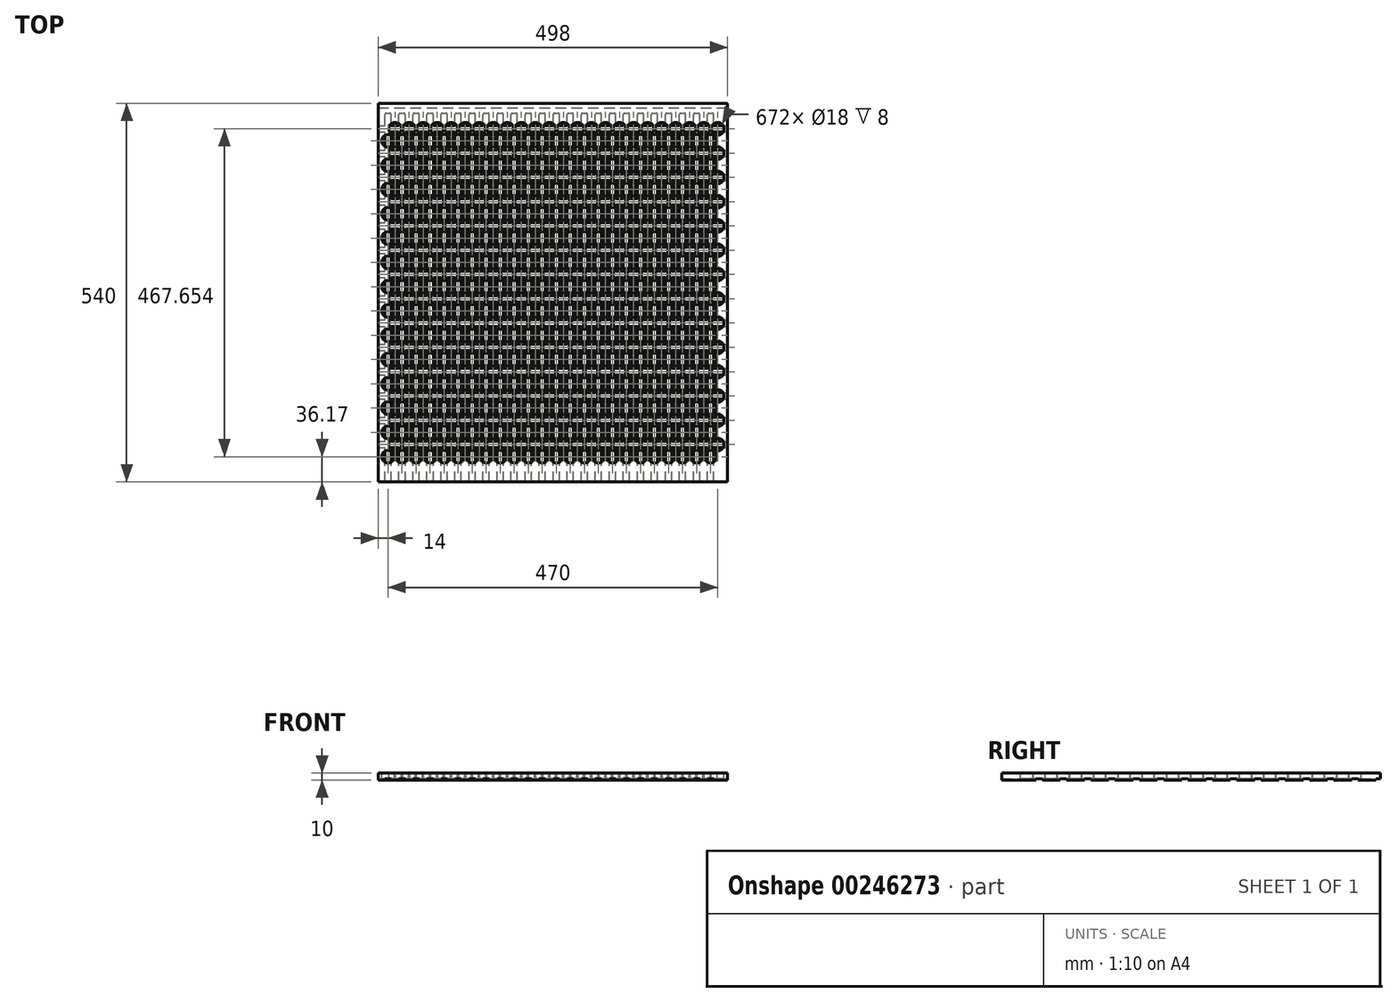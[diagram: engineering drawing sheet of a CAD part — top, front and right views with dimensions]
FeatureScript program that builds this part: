
annotation { "Feature Type Name" : "Feature", "Feature Type Description" : "" }
export const myFeature = defineFeature(function(context is Context, id is Id, definition is map)
    precondition{}
    {
        {
            var Q0;
            Q0=qCreatedBy(makeId("Top.planeOp"),FACE);
            var sketch = newSketch(context, id + "F0", { "sketchPlane" : qUnion([Q0])});
            skCircle(sketch, "E0", {"center": v(0, 0) * mm, "radius": 9 * mm});
            skCircle(sketch, "E1.1.0.0", {"center": v(20, 0) * mm, "radius": 9 * mm});
            skCircle(sketch, "E1.2.0.0", {"center": v(40, 0) * mm, "radius": 9 * mm});
            skCircle(sketch, "E1.3.0.0", {"center": v(60, 0) * mm, "radius": 9 * mm});
            skCircle(sketch, "E1.4.0.0", {"center": v(80, 0) * mm, "radius": 9 * mm});
            skCircle(sketch, "E1.5.0.0", {"center": v(100, 0) * mm, "radius": 9 * mm});
            skCircle(sketch, "E1.6.0.0", {"center": v(120, 0) * mm, "radius": 9 * mm});
            skCircle(sketch, "E1.7.0.0", {"center": v(140, 0) * mm, "radius": 9 * mm});
            skCircle(sketch, "E1.8.0.0", {"center": v(160, 0) * mm, "radius": 9 * mm});
            skCircle(sketch, "E1.9.0.0", {"center": v(180, 0) * mm, "radius": 9 * mm});
            skCircle(sketch, "E1.10.0.0", {"center": v(200, 0) * mm, "radius": 9 * mm});
            skCircle(sketch, "E1.11.0.0", {"center": v(220, 0) * mm, "radius": 9 * mm});
            skCircle(sketch, "E1.12.0.0", {"center": v(240, 0) * mm, "radius": 9 * mm});
            skCircle(sketch, "E1.13.0.0", {"center": v(260, 0) * mm, "radius": 9 * mm});
            skCircle(sketch, "E1.14.0.0", {"center": v(280, 0) * mm, "radius": 9 * mm});
            skCircle(sketch, "E1.15.0.0", {"center": v(300, 0) * mm, "radius": 9 * mm});
            skCircle(sketch, "E1.16.0.0", {"center": v(320, 0) * mm, "radius": 9 * mm});
            skCircle(sketch, "E1.17.0.0", {"center": v(340, 0) * mm, "radius": 9 * mm});
            skCircle(sketch, "E1.18.0.0", {"center": v(360, 0) * mm, "radius": 9 * mm});
            skCircle(sketch, "E1.19.0.0", {"center": v(380, 0) * mm, "radius": 9 * mm});
            skCircle(sketch, "E1.20.0.0", {"center": v(400, 0) * mm, "radius": 9 * mm});
            skCircle(sketch, "E1.21.0.0", {"center": v(420, 0) * mm, "radius": 9 * mm});
            skCircle(sketch, "E1.22.0.0", {"center": v(440, 0) * mm, "radius": 9 * mm});
            skCircle(sketch, "E1.23.0.0", {"center": v(460, 0) * mm, "radius": 9 * mm});
            skLineSegment(sketch, "E1.direction1", {"start": v(0, 0) * mm, "end": v(20, 0) * mm, "construction": true});
            skCircle(sketch, "E2", {"center": v(10, 17.32) * mm, "radius": 9 * mm});
            skCircle(sketch, "E3.1.0.0", {"center": v(30, 17.32) * mm, "radius": 9 * mm});
            skCircle(sketch, "E3.2.0.0", {"center": v(50, 17.32) * mm, "radius": 9 * mm});
            skCircle(sketch, "E3.3.0.0", {"center": v(70, 17.32) * mm, "radius": 9 * mm});
            skCircle(sketch, "E3.4.0.0", {"center": v(90, 17.32) * mm, "radius": 9 * mm});
            skCircle(sketch, "E3.5.0.0", {"center": v(110, 17.32) * mm, "radius": 9 * mm});
            skCircle(sketch, "E3.6.0.0", {"center": v(130, 17.32) * mm, "radius": 9 * mm});
            skCircle(sketch, "E3.7.0.0", {"center": v(150, 17.32) * mm, "radius": 9 * mm});
            skCircle(sketch, "E3.8.0.0", {"center": v(170, 17.32) * mm, "radius": 9 * mm});
            skCircle(sketch, "E3.9.0.0", {"center": v(190, 17.32) * mm, "radius": 9 * mm});
            skCircle(sketch, "E3.10.0.0", {"center": v(210, 17.32) * mm, "radius": 9 * mm});
            skCircle(sketch, "E3.11.0.0", {"center": v(230, 17.32) * mm, "radius": 9 * mm});
            skCircle(sketch, "E3.12.0.0", {"center": v(250, 17.32) * mm, "radius": 9 * mm});
            skCircle(sketch, "E3.13.0.0", {"center": v(270, 17.32) * mm, "radius": 9 * mm});
            skCircle(sketch, "E3.14.0.0", {"center": v(290, 17.32) * mm, "radius": 9 * mm});
            skCircle(sketch, "E3.15.0.0", {"center": v(310, 17.32) * mm, "radius": 9 * mm});
            skCircle(sketch, "E3.16.0.0", {"center": v(330, 17.32) * mm, "radius": 9 * mm});
            skCircle(sketch, "E3.17.0.0", {"center": v(350, 17.32) * mm, "radius": 9 * mm});
            skCircle(sketch, "E3.18.0.0", {"center": v(370, 17.32) * mm, "radius": 9 * mm});
            skCircle(sketch, "E3.19.0.0", {"center": v(390, 17.32) * mm, "radius": 9 * mm});
            skCircle(sketch, "E3.20.0.0", {"center": v(410, 17.32) * mm, "radius": 9 * mm});
            skCircle(sketch, "E3.21.0.0", {"center": v(430, 17.32) * mm, "radius": 9 * mm});
            skCircle(sketch, "E3.22.0.0", {"center": v(450, 17.32) * mm, "radius": 9 * mm});
            skCircle(sketch, "E3.23.0.0", {"center": v(470, 17.32) * mm, "radius": 9 * mm});
            skLineSegment(sketch, "E3.direction1", {"start": v(10, 17.32) * mm, "end": v(30, 17.32) * mm, "construction": true});
            skCircle(sketch, "E4.0.1.0", {"center": v(280, 34.64) * mm, "radius": 9 * mm});
            skCircle(sketch, "E4.0.1.1", {"center": v(260, 34.64) * mm, "radius": 9 * mm});
            skCircle(sketch, "E4.0.1.2", {"center": v(130, 51.96) * mm, "radius": 9 * mm});
            skCircle(sketch, "E4.0.1.3", {"center": v(60, 34.64) * mm, "radius": 9 * mm});
            skCircle(sketch, "E4.0.1.4", {"center": v(80, 34.64) * mm, "radius": 9 * mm});
            skCircle(sketch, "E4.0.1.5", {"center": v(100, 34.64) * mm, "radius": 9 * mm});
            skCircle(sketch, "E4.0.1.6", {"center": v(350, 51.96) * mm, "radius": 9 * mm});
            skCircle(sketch, "E4.0.1.7", {"center": v(0, 34.64) * mm, "radius": 9 * mm});
            skCircle(sketch, "E4.0.1.8", {"center": v(120, 34.64) * mm, "radius": 9 * mm});
            skCircle(sketch, "E4.0.1.9", {"center": v(30, 51.96) * mm, "radius": 9 * mm});
            skCircle(sketch, "E4.0.1.10", {"center": v(380, 34.64) * mm, "radius": 9 * mm});
            skCircle(sketch, "E4.0.1.11", {"center": v(140, 34.64) * mm, "radius": 9 * mm});
            skCircle(sketch, "E4.0.1.12", {"center": v(450, 51.96) * mm, "radius": 9 * mm});
            skCircle(sketch, "E4.0.1.13", {"center": v(160, 34.64) * mm, "radius": 9 * mm});
            skCircle(sketch, "E4.0.1.14", {"center": v(300, 34.64) * mm, "radius": 9 * mm});
            skCircle(sketch, "E4.0.1.15", {"center": v(40, 34.64) * mm, "radius": 9 * mm});
            skCircle(sketch, "E4.0.1.16", {"center": v(210, 51.96) * mm, "radius": 9 * mm});
            skCircle(sketch, "E4.0.1.17", {"center": v(330, 51.96) * mm, "radius": 9 * mm});
            skCircle(sketch, "E4.0.1.18", {"center": v(270, 51.96) * mm, "radius": 9 * mm});
            skCircle(sketch, "E4.0.1.19", {"center": v(440, 34.64) * mm, "radius": 9 * mm});
            skCircle(sketch, "E4.0.1.20", {"center": v(110, 51.96) * mm, "radius": 9 * mm});
            skCircle(sketch, "E4.0.1.21", {"center": v(250, 51.96) * mm, "radius": 9 * mm});
            skCircle(sketch, "E4.0.1.22", {"center": v(180, 34.64) * mm, "radius": 9 * mm});
            skCircle(sketch, "E4.0.1.23", {"center": v(430, 51.96) * mm, "radius": 9 * mm});
            skCircle(sketch, "E4.0.1.24", {"center": v(200, 34.64) * mm, "radius": 9 * mm});
            skCircle(sketch, "E4.0.1.25", {"center": v(420, 34.64) * mm, "radius": 9 * mm});
            skCircle(sketch, "E4.0.1.26", {"center": v(70, 51.96) * mm, "radius": 9 * mm});
            skCircle(sketch, "E4.0.1.27", {"center": v(390, 51.96) * mm, "radius": 9 * mm});
            skCircle(sketch, "E4.0.1.28", {"center": v(220, 34.64) * mm, "radius": 9 * mm});
            skCircle(sketch, "E4.0.1.29", {"center": v(190, 51.96) * mm, "radius": 9 * mm});
            skCircle(sketch, "E4.0.1.30", {"center": v(90, 51.96) * mm, "radius": 9 * mm});
            skCircle(sketch, "E4.0.1.31", {"center": v(230, 51.96) * mm, "radius": 9 * mm});
            skCircle(sketch, "E4.0.1.32", {"center": v(150, 51.96) * mm, "radius": 9 * mm});
            skCircle(sketch, "E4.0.1.33", {"center": v(470, 51.96) * mm, "radius": 9 * mm});
            skCircle(sketch, "E4.0.1.34", {"center": v(410, 51.96) * mm, "radius": 9 * mm});
            skCircle(sketch, "E4.0.1.35", {"center": v(50, 51.96) * mm, "radius": 9 * mm});
            skCircle(sketch, "E4.0.1.36", {"center": v(400, 34.64) * mm, "radius": 9 * mm});
            skCircle(sketch, "E4.0.1.37", {"center": v(240, 34.64) * mm, "radius": 9 * mm});
            skCircle(sketch, "E4.0.1.38", {"center": v(320, 34.64) * mm, "radius": 9 * mm});
            skCircle(sketch, "E4.0.1.39", {"center": v(370, 51.96) * mm, "radius": 9 * mm});
            skCircle(sketch, "E4.0.1.40", {"center": v(10, 51.96) * mm, "radius": 9 * mm});
            skCircle(sketch, "E4.0.1.41", {"center": v(290, 51.96) * mm, "radius": 9 * mm});
            skCircle(sketch, "E4.0.1.42", {"center": v(360, 34.64) * mm, "radius": 9 * mm});
            skCircle(sketch, "E4.0.1.43", {"center": v(460, 34.64) * mm, "radius": 9 * mm});
            skCircle(sketch, "E4.0.1.44", {"center": v(310, 51.96) * mm, "radius": 9 * mm});
            skCircle(sketch, "E4.0.1.45", {"center": v(340, 34.64) * mm, "radius": 9 * mm});
            skCircle(sketch, "E4.0.1.46", {"center": v(170, 51.96) * mm, "radius": 9 * mm});
            skCircle(sketch, "E4.0.1.47", {"center": v(20, 34.64) * mm, "radius": 9 * mm});
            skLineSegment(sketch, "E4.0.1.48", {"start": v(0, 34.64) * mm, "end": v(20, 34.64) * mm, "construction": true});
            skLineSegment(sketch, "E4.0.1.49", {"start": v(10, 51.96) * mm, "end": v(30, 51.96) * mm, "construction": true});
            skCircle(sketch, "E4.0.2.0", {"center": v(280, 69.28) * mm, "radius": 9 * mm});
            skCircle(sketch, "E4.0.2.1", {"center": v(260, 69.28) * mm, "radius": 9 * mm});
            skCircle(sketch, "E4.0.2.2", {"center": v(130, 86.6) * mm, "radius": 9 * mm});
            skCircle(sketch, "E4.0.2.3", {"center": v(60, 69.28) * mm, "radius": 9 * mm});
            skCircle(sketch, "E4.0.2.4", {"center": v(80, 69.28) * mm, "radius": 9 * mm});
            skCircle(sketch, "E4.0.2.5", {"center": v(100, 69.28) * mm, "radius": 9 * mm});
            skCircle(sketch, "E4.0.2.6", {"center": v(350, 86.6) * mm, "radius": 9 * mm});
            skCircle(sketch, "E4.0.2.7", {"center": v(0, 69.28) * mm, "radius": 9 * mm});
            skCircle(sketch, "E4.0.2.8", {"center": v(120, 69.28) * mm, "radius": 9 * mm});
            skCircle(sketch, "E4.0.2.9", {"center": v(30, 86.6) * mm, "radius": 9 * mm});
            skCircle(sketch, "E4.0.2.10", {"center": v(380, 69.28) * mm, "radius": 9 * mm});
            skCircle(sketch, "E4.0.2.11", {"center": v(140, 69.28) * mm, "radius": 9 * mm});
            skCircle(sketch, "E4.0.2.12", {"center": v(450, 86.6) * mm, "radius": 9 * mm});
            skCircle(sketch, "E4.0.2.13", {"center": v(160, 69.28) * mm, "radius": 9 * mm});
            skCircle(sketch, "E4.0.2.14", {"center": v(300, 69.28) * mm, "radius": 9 * mm});
            skCircle(sketch, "E4.0.2.15", {"center": v(40, 69.28) * mm, "radius": 9 * mm});
            skCircle(sketch, "E4.0.2.16", {"center": v(210, 86.6) * mm, "radius": 9 * mm});
            skCircle(sketch, "E4.0.2.17", {"center": v(330, 86.6) * mm, "radius": 9 * mm});
            skCircle(sketch, "E4.0.2.18", {"center": v(270, 86.6) * mm, "radius": 9 * mm});
            skCircle(sketch, "E4.0.2.19", {"center": v(440, 69.28) * mm, "radius": 9 * mm});
            skCircle(sketch, "E4.0.2.20", {"center": v(110, 86.6) * mm, "radius": 9 * mm});
            skCircle(sketch, "E4.0.2.21", {"center": v(250, 86.6) * mm, "radius": 9 * mm});
            skCircle(sketch, "E4.0.2.22", {"center": v(180, 69.28) * mm, "radius": 9 * mm});
            skCircle(sketch, "E4.0.2.23", {"center": v(430, 86.6) * mm, "radius": 9 * mm});
            skCircle(sketch, "E4.0.2.24", {"center": v(200, 69.28) * mm, "radius": 9 * mm});
            skCircle(sketch, "E4.0.2.25", {"center": v(420, 69.28) * mm, "radius": 9 * mm});
            skCircle(sketch, "E4.0.2.26", {"center": v(70, 86.6) * mm, "radius": 9 * mm});
            skCircle(sketch, "E4.0.2.27", {"center": v(390, 86.6) * mm, "radius": 9 * mm});
            skCircle(sketch, "E4.0.2.28", {"center": v(220, 69.28) * mm, "radius": 9 * mm});
            skCircle(sketch, "E4.0.2.29", {"center": v(190, 86.6) * mm, "radius": 9 * mm});
            skCircle(sketch, "E4.0.2.30", {"center": v(90, 86.6) * mm, "radius": 9 * mm});
            skCircle(sketch, "E4.0.2.31", {"center": v(230, 86.6) * mm, "radius": 9 * mm});
            skCircle(sketch, "E4.0.2.32", {"center": v(150, 86.6) * mm, "radius": 9 * mm});
            skCircle(sketch, "E4.0.2.33", {"center": v(470, 86.6) * mm, "radius": 9 * mm});
            skCircle(sketch, "E4.0.2.34", {"center": v(410, 86.6) * mm, "radius": 9 * mm});
            skCircle(sketch, "E4.0.2.35", {"center": v(50, 86.6) * mm, "radius": 9 * mm});
            skCircle(sketch, "E4.0.2.36", {"center": v(400, 69.28) * mm, "radius": 9 * mm});
            skCircle(sketch, "E4.0.2.37", {"center": v(240, 69.28) * mm, "radius": 9 * mm});
            skCircle(sketch, "E4.0.2.38", {"center": v(320, 69.28) * mm, "radius": 9 * mm});
            skCircle(sketch, "E4.0.2.39", {"center": v(370, 86.6) * mm, "radius": 9 * mm});
            skCircle(sketch, "E4.0.2.40", {"center": v(10, 86.6) * mm, "radius": 9 * mm});
            skCircle(sketch, "E4.0.2.41", {"center": v(290, 86.6) * mm, "radius": 9 * mm});
            skCircle(sketch, "E4.0.2.42", {"center": v(360, 69.28) * mm, "radius": 9 * mm});
            skCircle(sketch, "E4.0.2.43", {"center": v(460, 69.28) * mm, "radius": 9 * mm});
            skCircle(sketch, "E4.0.2.44", {"center": v(310, 86.6) * mm, "radius": 9 * mm});
            skCircle(sketch, "E4.0.2.45", {"center": v(340, 69.28) * mm, "radius": 9 * mm});
            skCircle(sketch, "E4.0.2.46", {"center": v(170, 86.6) * mm, "radius": 9 * mm});
            skCircle(sketch, "E4.0.2.47", {"center": v(20, 69.28) * mm, "radius": 9 * mm});
            skLineSegment(sketch, "E4.0.2.48", {"start": v(0, 69.28) * mm, "end": v(20, 69.28) * mm, "construction": true});
            skLineSegment(sketch, "E4.0.2.49", {"start": v(10, 86.6) * mm, "end": v(30, 86.6) * mm, "construction": true});
            skCircle(sketch, "E4.0.3.0", {"center": v(280, 103.92) * mm, "radius": 9 * mm});
            skCircle(sketch, "E4.0.3.1", {"center": v(260, 103.92) * mm, "radius": 9 * mm});
            skCircle(sketch, "E4.0.3.2", {"center": v(130, 121.24) * mm, "radius": 9 * mm});
            skCircle(sketch, "E4.0.3.3", {"center": v(60, 103.92) * mm, "radius": 9 * mm});
            skCircle(sketch, "E4.0.3.4", {"center": v(80, 103.92) * mm, "radius": 9 * mm});
            skCircle(sketch, "E4.0.3.5", {"center": v(100, 103.92) * mm, "radius": 9 * mm});
            skCircle(sketch, "E4.0.3.6", {"center": v(350, 121.24) * mm, "radius": 9 * mm});
            skCircle(sketch, "E4.0.3.7", {"center": v(0, 103.92) * mm, "radius": 9 * mm});
            skCircle(sketch, "E4.0.3.8", {"center": v(120, 103.92) * mm, "radius": 9 * mm});
            skCircle(sketch, "E4.0.3.9", {"center": v(30, 121.24) * mm, "radius": 9 * mm});
            skCircle(sketch, "E4.0.3.10", {"center": v(380, 103.92) * mm, "radius": 9 * mm});
            skCircle(sketch, "E4.0.3.11", {"center": v(140, 103.92) * mm, "radius": 9 * mm});
            skCircle(sketch, "E4.0.3.12", {"center": v(450, 121.24) * mm, "radius": 9 * mm});
            skCircle(sketch, "E4.0.3.13", {"center": v(160, 103.92) * mm, "radius": 9 * mm});
            skCircle(sketch, "E4.0.3.14", {"center": v(300, 103.92) * mm, "radius": 9 * mm});
            skCircle(sketch, "E4.0.3.15", {"center": v(40, 103.92) * mm, "radius": 9 * mm});
            skCircle(sketch, "E4.0.3.16", {"center": v(210, 121.24) * mm, "radius": 9 * mm});
            skCircle(sketch, "E4.0.3.17", {"center": v(330, 121.24) * mm, "radius": 9 * mm});
            skCircle(sketch, "E4.0.3.18", {"center": v(270, 121.24) * mm, "radius": 9 * mm});
            skCircle(sketch, "E4.0.3.19", {"center": v(440, 103.92) * mm, "radius": 9 * mm});
            skCircle(sketch, "E4.0.3.20", {"center": v(110, 121.24) * mm, "radius": 9 * mm});
            skCircle(sketch, "E4.0.3.21", {"center": v(250, 121.24) * mm, "radius": 9 * mm});
            skCircle(sketch, "E4.0.3.22", {"center": v(180, 103.92) * mm, "radius": 9 * mm});
            skCircle(sketch, "E4.0.3.23", {"center": v(430, 121.24) * mm, "radius": 9 * mm});
            skCircle(sketch, "E4.0.3.24", {"center": v(200, 103.92) * mm, "radius": 9 * mm});
            skCircle(sketch, "E4.0.3.25", {"center": v(420, 103.92) * mm, "radius": 9 * mm});
            skCircle(sketch, "E4.0.3.26", {"center": v(70, 121.24) * mm, "radius": 9 * mm});
            skCircle(sketch, "E4.0.3.27", {"center": v(390, 121.24) * mm, "radius": 9 * mm});
            skCircle(sketch, "E4.0.3.28", {"center": v(220, 103.92) * mm, "radius": 9 * mm});
            skCircle(sketch, "E4.0.3.29", {"center": v(190, 121.24) * mm, "radius": 9 * mm});
            skCircle(sketch, "E4.0.3.30", {"center": v(90, 121.24) * mm, "radius": 9 * mm});
            skCircle(sketch, "E4.0.3.31", {"center": v(230, 121.24) * mm, "radius": 9 * mm});
            skCircle(sketch, "E4.0.3.32", {"center": v(150, 121.24) * mm, "radius": 9 * mm});
            skCircle(sketch, "E4.0.3.33", {"center": v(470, 121.24) * mm, "radius": 9 * mm});
            skCircle(sketch, "E4.0.3.34", {"center": v(410, 121.24) * mm, "radius": 9 * mm});
            skCircle(sketch, "E4.0.3.35", {"center": v(50, 121.24) * mm, "radius": 9 * mm});
            skCircle(sketch, "E4.0.3.36", {"center": v(400, 103.92) * mm, "radius": 9 * mm});
            skCircle(sketch, "E4.0.3.37", {"center": v(240, 103.92) * mm, "radius": 9 * mm});
            skCircle(sketch, "E4.0.3.38", {"center": v(320, 103.92) * mm, "radius": 9 * mm});
            skCircle(sketch, "E4.0.3.39", {"center": v(370, 121.24) * mm, "radius": 9 * mm});
            skCircle(sketch, "E4.0.3.40", {"center": v(10, 121.24) * mm, "radius": 9 * mm});
            skCircle(sketch, "E4.0.3.41", {"center": v(290, 121.24) * mm, "radius": 9 * mm});
            skCircle(sketch, "E4.0.3.42", {"center": v(360, 103.92) * mm, "radius": 9 * mm});
            skCircle(sketch, "E4.0.3.43", {"center": v(460, 103.92) * mm, "radius": 9 * mm});
            skCircle(sketch, "E4.0.3.44", {"center": v(310, 121.24) * mm, "radius": 9 * mm});
            skCircle(sketch, "E4.0.3.45", {"center": v(340, 103.92) * mm, "radius": 9 * mm});
            skCircle(sketch, "E4.0.3.46", {"center": v(170, 121.24) * mm, "radius": 9 * mm});
            skCircle(sketch, "E4.0.3.47", {"center": v(20, 103.92) * mm, "radius": 9 * mm});
            skLineSegment(sketch, "E4.0.3.48", {"start": v(0, 103.92) * mm, "end": v(20, 103.92) * mm, "construction": true});
            skLineSegment(sketch, "E4.0.3.49", {"start": v(10, 121.24) * mm, "end": v(30, 121.24) * mm, "construction": true});
            skCircle(sketch, "E4.0.4.0", {"center": v(280, 138.56) * mm, "radius": 9 * mm});
            skCircle(sketch, "E4.0.4.1", {"center": v(260, 138.56) * mm, "radius": 9 * mm});
            skCircle(sketch, "E4.0.4.2", {"center": v(130, 155.88) * mm, "radius": 9 * mm});
            skCircle(sketch, "E4.0.4.3", {"center": v(60, 138.56) * mm, "radius": 9 * mm});
            skCircle(sketch, "E4.0.4.4", {"center": v(80, 138.56) * mm, "radius": 9 * mm});
            skCircle(sketch, "E4.0.4.5", {"center": v(100, 138.56) * mm, "radius": 9 * mm});
            skCircle(sketch, "E4.0.4.6", {"center": v(350, 155.88) * mm, "radius": 9 * mm});
            skCircle(sketch, "E4.0.4.7", {"center": v(0, 138.56) * mm, "radius": 9 * mm});
            skCircle(sketch, "E4.0.4.8", {"center": v(120, 138.56) * mm, "radius": 9 * mm});
            skCircle(sketch, "E4.0.4.9", {"center": v(30, 155.88) * mm, "radius": 9 * mm});
            skCircle(sketch, "E4.0.4.10", {"center": v(380, 138.56) * mm, "radius": 9 * mm});
            skCircle(sketch, "E4.0.4.11", {"center": v(140, 138.56) * mm, "radius": 9 * mm});
            skCircle(sketch, "E4.0.4.12", {"center": v(450, 155.88) * mm, "radius": 9 * mm});
            skCircle(sketch, "E4.0.4.13", {"center": v(160, 138.56) * mm, "radius": 9 * mm});
            skCircle(sketch, "E4.0.4.14", {"center": v(300, 138.56) * mm, "radius": 9 * mm});
            skCircle(sketch, "E4.0.4.15", {"center": v(40, 138.56) * mm, "radius": 9 * mm});
            skCircle(sketch, "E4.0.4.16", {"center": v(210, 155.88) * mm, "radius": 9 * mm});
            skCircle(sketch, "E4.0.4.17", {"center": v(330, 155.88) * mm, "radius": 9 * mm});
            skCircle(sketch, "E4.0.4.18", {"center": v(270, 155.88) * mm, "radius": 9 * mm});
            skCircle(sketch, "E4.0.4.19", {"center": v(440, 138.56) * mm, "radius": 9 * mm});
            skCircle(sketch, "E4.0.4.20", {"center": v(110, 155.88) * mm, "radius": 9 * mm});
            skCircle(sketch, "E4.0.4.21", {"center": v(250, 155.88) * mm, "radius": 9 * mm});
            skCircle(sketch, "E4.0.4.22", {"center": v(180, 138.56) * mm, "radius": 9 * mm});
            skCircle(sketch, "E4.0.4.23", {"center": v(430, 155.88) * mm, "radius": 9 * mm});
            skCircle(sketch, "E4.0.4.24", {"center": v(200, 138.56) * mm, "radius": 9 * mm});
            skCircle(sketch, "E4.0.4.25", {"center": v(420, 138.56) * mm, "radius": 9 * mm});
            skCircle(sketch, "E4.0.4.26", {"center": v(70, 155.88) * mm, "radius": 9 * mm});
            skCircle(sketch, "E4.0.4.27", {"center": v(390, 155.88) * mm, "radius": 9 * mm});
            skCircle(sketch, "E4.0.4.28", {"center": v(220, 138.56) * mm, "radius": 9 * mm});
            skCircle(sketch, "E4.0.4.29", {"center": v(190, 155.88) * mm, "radius": 9 * mm});
            skCircle(sketch, "E4.0.4.30", {"center": v(90, 155.88) * mm, "radius": 9 * mm});
            skCircle(sketch, "E4.0.4.31", {"center": v(230, 155.88) * mm, "radius": 9 * mm});
            skCircle(sketch, "E4.0.4.32", {"center": v(150, 155.88) * mm, "radius": 9 * mm});
            skCircle(sketch, "E4.0.4.33", {"center": v(470, 155.88) * mm, "radius": 9 * mm});
            skCircle(sketch, "E4.0.4.34", {"center": v(410, 155.88) * mm, "radius": 9 * mm});
            skCircle(sketch, "E4.0.4.35", {"center": v(50, 155.88) * mm, "radius": 9 * mm});
            skCircle(sketch, "E4.0.4.36", {"center": v(400, 138.56) * mm, "radius": 9 * mm});
            skCircle(sketch, "E4.0.4.37", {"center": v(240, 138.56) * mm, "radius": 9 * mm});
            skCircle(sketch, "E4.0.4.38", {"center": v(320, 138.56) * mm, "radius": 9 * mm});
            skCircle(sketch, "E4.0.4.39", {"center": v(370, 155.88) * mm, "radius": 9 * mm});
            skCircle(sketch, "E4.0.4.40", {"center": v(10, 155.88) * mm, "radius": 9 * mm});
            skCircle(sketch, "E4.0.4.41", {"center": v(290, 155.88) * mm, "radius": 9 * mm});
            skCircle(sketch, "E4.0.4.42", {"center": v(360, 138.56) * mm, "radius": 9 * mm});
            skCircle(sketch, "E4.0.4.43", {"center": v(460, 138.56) * mm, "radius": 9 * mm});
            skCircle(sketch, "E4.0.4.44", {"center": v(310, 155.88) * mm, "radius": 9 * mm});
            skCircle(sketch, "E4.0.4.45", {"center": v(340, 138.56) * mm, "radius": 9 * mm});
            skCircle(sketch, "E4.0.4.46", {"center": v(170, 155.88) * mm, "radius": 9 * mm});
            skCircle(sketch, "E4.0.4.47", {"center": v(20, 138.56) * mm, "radius": 9 * mm});
            skLineSegment(sketch, "E4.0.4.48", {"start": v(0, 138.56) * mm, "end": v(20, 138.56) * mm, "construction": true});
            skLineSegment(sketch, "E4.0.4.49", {"start": v(10, 155.88) * mm, "end": v(30, 155.88) * mm, "construction": true});
            skCircle(sketch, "E4.0.5.0", {"center": v(280, 173.2) * mm, "radius": 9 * mm});
            skCircle(sketch, "E4.0.5.1", {"center": v(260, 173.2) * mm, "radius": 9 * mm});
            skCircle(sketch, "E4.0.5.2", {"center": v(130, 190.53) * mm, "radius": 9 * mm});
            skCircle(sketch, "E4.0.5.3", {"center": v(60, 173.2) * mm, "radius": 9 * mm});
            skCircle(sketch, "E4.0.5.4", {"center": v(80, 173.2) * mm, "radius": 9 * mm});
            skCircle(sketch, "E4.0.5.5", {"center": v(100, 173.2) * mm, "radius": 9 * mm});
            skCircle(sketch, "E4.0.5.6", {"center": v(350, 190.53) * mm, "radius": 9 * mm});
            skCircle(sketch, "E4.0.5.7", {"center": v(0, 173.2) * mm, "radius": 9 * mm});
            skCircle(sketch, "E4.0.5.8", {"center": v(120, 173.2) * mm, "radius": 9 * mm});
            skCircle(sketch, "E4.0.5.9", {"center": v(30, 190.53) * mm, "radius": 9 * mm});
            skCircle(sketch, "E4.0.5.10", {"center": v(380, 173.2) * mm, "radius": 9 * mm});
            skCircle(sketch, "E4.0.5.11", {"center": v(140, 173.2) * mm, "radius": 9 * mm});
            skCircle(sketch, "E4.0.5.12", {"center": v(450, 190.53) * mm, "radius": 9 * mm});
            skCircle(sketch, "E4.0.5.13", {"center": v(160, 173.2) * mm, "radius": 9 * mm});
            skCircle(sketch, "E4.0.5.14", {"center": v(300, 173.2) * mm, "radius": 9 * mm});
            skCircle(sketch, "E4.0.5.15", {"center": v(40, 173.2) * mm, "radius": 9 * mm});
            skCircle(sketch, "E4.0.5.16", {"center": v(210, 190.53) * mm, "radius": 9 * mm});
            skCircle(sketch, "E4.0.5.17", {"center": v(330, 190.53) * mm, "radius": 9 * mm});
            skCircle(sketch, "E4.0.5.18", {"center": v(270, 190.53) * mm, "radius": 9 * mm});
            skCircle(sketch, "E4.0.5.19", {"center": v(440, 173.2) * mm, "radius": 9 * mm});
            skCircle(sketch, "E4.0.5.20", {"center": v(110, 190.53) * mm, "radius": 9 * mm});
            skCircle(sketch, "E4.0.5.21", {"center": v(250, 190.53) * mm, "radius": 9 * mm});
            skCircle(sketch, "E4.0.5.22", {"center": v(180, 173.2) * mm, "radius": 9 * mm});
            skCircle(sketch, "E4.0.5.23", {"center": v(430, 190.53) * mm, "radius": 9 * mm});
            skCircle(sketch, "E4.0.5.24", {"center": v(200, 173.2) * mm, "radius": 9 * mm});
            skCircle(sketch, "E4.0.5.25", {"center": v(420, 173.2) * mm, "radius": 9 * mm});
            skCircle(sketch, "E4.0.5.26", {"center": v(70, 190.53) * mm, "radius": 9 * mm});
            skCircle(sketch, "E4.0.5.27", {"center": v(390, 190.53) * mm, "radius": 9 * mm});
            skCircle(sketch, "E4.0.5.28", {"center": v(220, 173.2) * mm, "radius": 9 * mm});
            skCircle(sketch, "E4.0.5.29", {"center": v(190, 190.53) * mm, "radius": 9 * mm});
            skCircle(sketch, "E4.0.5.30", {"center": v(90, 190.53) * mm, "radius": 9 * mm});
            skCircle(sketch, "E4.0.5.31", {"center": v(230, 190.53) * mm, "radius": 9 * mm});
            skCircle(sketch, "E4.0.5.32", {"center": v(150, 190.53) * mm, "radius": 9 * mm});
            skCircle(sketch, "E4.0.5.33", {"center": v(470, 190.53) * mm, "radius": 9 * mm});
            skCircle(sketch, "E4.0.5.34", {"center": v(410, 190.53) * mm, "radius": 9 * mm});
            skCircle(sketch, "E4.0.5.35", {"center": v(50, 190.53) * mm, "radius": 9 * mm});
            skCircle(sketch, "E4.0.5.36", {"center": v(400, 173.2) * mm, "radius": 9 * mm});
            skCircle(sketch, "E4.0.5.37", {"center": v(240, 173.2) * mm, "radius": 9 * mm});
            skCircle(sketch, "E4.0.5.38", {"center": v(320, 173.2) * mm, "radius": 9 * mm});
            skCircle(sketch, "E4.0.5.39", {"center": v(370, 190.53) * mm, "radius": 9 * mm});
            skCircle(sketch, "E4.0.5.40", {"center": v(10, 190.53) * mm, "radius": 9 * mm});
            skCircle(sketch, "E4.0.5.41", {"center": v(290, 190.53) * mm, "radius": 9 * mm});
            skCircle(sketch, "E4.0.5.42", {"center": v(360, 173.2) * mm, "radius": 9 * mm});
            skCircle(sketch, "E4.0.5.43", {"center": v(460, 173.2) * mm, "radius": 9 * mm});
            skCircle(sketch, "E4.0.5.44", {"center": v(310, 190.53) * mm, "radius": 9 * mm});
            skCircle(sketch, "E4.0.5.45", {"center": v(340, 173.2) * mm, "radius": 9 * mm});
            skCircle(sketch, "E4.0.5.46", {"center": v(170, 190.53) * mm, "radius": 9 * mm});
            skCircle(sketch, "E4.0.5.47", {"center": v(20, 173.2) * mm, "radius": 9 * mm});
            skLineSegment(sketch, "E4.0.5.48", {"start": v(0, 173.2) * mm, "end": v(20, 173.2) * mm, "construction": true});
            skLineSegment(sketch, "E4.0.5.49", {"start": v(10, 190.53) * mm, "end": v(30, 190.53) * mm, "construction": true});
            skCircle(sketch, "E4.0.6.0", {"center": v(280, 207.85) * mm, "radius": 9 * mm});
            skCircle(sketch, "E4.0.6.1", {"center": v(260, 207.85) * mm, "radius": 9 * mm});
            skCircle(sketch, "E4.0.6.2", {"center": v(130, 225.17) * mm, "radius": 9 * mm});
            skCircle(sketch, "E4.0.6.3", {"center": v(60, 207.85) * mm, "radius": 9 * mm});
            skCircle(sketch, "E4.0.6.4", {"center": v(80, 207.85) * mm, "radius": 9 * mm});
            skCircle(sketch, "E4.0.6.5", {"center": v(100, 207.85) * mm, "radius": 9 * mm});
            skCircle(sketch, "E4.0.6.6", {"center": v(350, 225.17) * mm, "radius": 9 * mm});
            skCircle(sketch, "E4.0.6.7", {"center": v(0, 207.85) * mm, "radius": 9 * mm});
            skCircle(sketch, "E4.0.6.8", {"center": v(120, 207.85) * mm, "radius": 9 * mm});
            skCircle(sketch, "E4.0.6.9", {"center": v(30, 225.17) * mm, "radius": 9 * mm});
            skCircle(sketch, "E4.0.6.10", {"center": v(380, 207.85) * mm, "radius": 9 * mm});
            skCircle(sketch, "E4.0.6.11", {"center": v(140, 207.85) * mm, "radius": 9 * mm});
            skCircle(sketch, "E4.0.6.12", {"center": v(450, 225.17) * mm, "radius": 9 * mm});
            skCircle(sketch, "E4.0.6.13", {"center": v(160, 207.85) * mm, "radius": 9 * mm});
            skCircle(sketch, "E4.0.6.14", {"center": v(300, 207.85) * mm, "radius": 9 * mm});
            skCircle(sketch, "E4.0.6.15", {"center": v(40, 207.85) * mm, "radius": 9 * mm});
            skCircle(sketch, "E4.0.6.16", {"center": v(210, 225.17) * mm, "radius": 9 * mm});
            skCircle(sketch, "E4.0.6.17", {"center": v(330, 225.17) * mm, "radius": 9 * mm});
            skCircle(sketch, "E4.0.6.18", {"center": v(270, 225.17) * mm, "radius": 9 * mm});
            skCircle(sketch, "E4.0.6.19", {"center": v(440, 207.85) * mm, "radius": 9 * mm});
            skCircle(sketch, "E4.0.6.20", {"center": v(110, 225.17) * mm, "radius": 9 * mm});
            skCircle(sketch, "E4.0.6.21", {"center": v(250, 225.17) * mm, "radius": 9 * mm});
            skCircle(sketch, "E4.0.6.22", {"center": v(180, 207.85) * mm, "radius": 9 * mm});
            skCircle(sketch, "E4.0.6.23", {"center": v(430, 225.17) * mm, "radius": 9 * mm});
            skCircle(sketch, "E4.0.6.24", {"center": v(200, 207.85) * mm, "radius": 9 * mm});
            skCircle(sketch, "E4.0.6.25", {"center": v(420, 207.85) * mm, "radius": 9 * mm});
            skCircle(sketch, "E4.0.6.26", {"center": v(70, 225.17) * mm, "radius": 9 * mm});
            skCircle(sketch, "E4.0.6.27", {"center": v(390, 225.17) * mm, "radius": 9 * mm});
            skCircle(sketch, "E4.0.6.28", {"center": v(220, 207.85) * mm, "radius": 9 * mm});
            skCircle(sketch, "E4.0.6.29", {"center": v(190, 225.17) * mm, "radius": 9 * mm});
            skCircle(sketch, "E4.0.6.30", {"center": v(90, 225.17) * mm, "radius": 9 * mm});
            skCircle(sketch, "E4.0.6.31", {"center": v(230, 225.17) * mm, "radius": 9 * mm});
            skCircle(sketch, "E4.0.6.32", {"center": v(150, 225.17) * mm, "radius": 9 * mm});
            skCircle(sketch, "E4.0.6.33", {"center": v(470, 225.17) * mm, "radius": 9 * mm});
            skCircle(sketch, "E4.0.6.34", {"center": v(410, 225.17) * mm, "radius": 9 * mm});
            skCircle(sketch, "E4.0.6.35", {"center": v(50, 225.17) * mm, "radius": 9 * mm});
            skCircle(sketch, "E4.0.6.36", {"center": v(400, 207.85) * mm, "radius": 9 * mm});
            skCircle(sketch, "E4.0.6.37", {"center": v(240, 207.85) * mm, "radius": 9 * mm});
            skCircle(sketch, "E4.0.6.38", {"center": v(320, 207.85) * mm, "radius": 9 * mm});
            skCircle(sketch, "E4.0.6.39", {"center": v(370, 225.17) * mm, "radius": 9 * mm});
            skCircle(sketch, "E4.0.6.40", {"center": v(10, 225.17) * mm, "radius": 9 * mm});
            skCircle(sketch, "E4.0.6.41", {"center": v(290, 225.17) * mm, "radius": 9 * mm});
            skCircle(sketch, "E4.0.6.42", {"center": v(360, 207.85) * mm, "radius": 9 * mm});
            skCircle(sketch, "E4.0.6.43", {"center": v(460, 207.85) * mm, "radius": 9 * mm});
            skCircle(sketch, "E4.0.6.44", {"center": v(310, 225.17) * mm, "radius": 9 * mm});
            skCircle(sketch, "E4.0.6.45", {"center": v(340, 207.85) * mm, "radius": 9 * mm});
            skCircle(sketch, "E4.0.6.46", {"center": v(170, 225.17) * mm, "radius": 9 * mm});
            skCircle(sketch, "E4.0.6.47", {"center": v(20, 207.85) * mm, "radius": 9 * mm});
            skLineSegment(sketch, "E4.0.6.48", {"start": v(0, 207.85) * mm, "end": v(20, 207.85) * mm, "construction": true});
            skLineSegment(sketch, "E4.0.6.49", {"start": v(10, 225.17) * mm, "end": v(30, 225.17) * mm, "construction": true});
            skCircle(sketch, "E4.0.7.0", {"center": v(280, 242.49) * mm, "radius": 9 * mm});
            skCircle(sketch, "E4.0.7.1", {"center": v(260, 242.49) * mm, "radius": 9 * mm});
            skCircle(sketch, "E4.0.7.2", {"center": v(130, 259.8) * mm, "radius": 9 * mm});
            skCircle(sketch, "E4.0.7.3", {"center": v(60, 242.49) * mm, "radius": 9 * mm});
            skCircle(sketch, "E4.0.7.4", {"center": v(80, 242.49) * mm, "radius": 9 * mm});
            skCircle(sketch, "E4.0.7.5", {"center": v(100, 242.49) * mm, "radius": 9 * mm});
            skCircle(sketch, "E4.0.7.6", {"center": v(350, 259.8) * mm, "radius": 9 * mm});
            skCircle(sketch, "E4.0.7.7", {"center": v(0, 242.49) * mm, "radius": 9 * mm});
            skCircle(sketch, "E4.0.7.8", {"center": v(120, 242.49) * mm, "radius": 9 * mm});
            skCircle(sketch, "E4.0.7.9", {"center": v(30, 259.8) * mm, "radius": 9 * mm});
            skCircle(sketch, "E4.0.7.10", {"center": v(380, 242.49) * mm, "radius": 9 * mm});
            skCircle(sketch, "E4.0.7.11", {"center": v(140, 242.49) * mm, "radius": 9 * mm});
            skCircle(sketch, "E4.0.7.12", {"center": v(450, 259.8) * mm, "radius": 9 * mm});
            skCircle(sketch, "E4.0.7.13", {"center": v(160, 242.49) * mm, "radius": 9 * mm});
            skCircle(sketch, "E4.0.7.14", {"center": v(300, 242.49) * mm, "radius": 9 * mm});
            skCircle(sketch, "E4.0.7.15", {"center": v(40, 242.49) * mm, "radius": 9 * mm});
            skCircle(sketch, "E4.0.7.16", {"center": v(210, 259.8) * mm, "radius": 9 * mm});
            skCircle(sketch, "E4.0.7.17", {"center": v(330, 259.8) * mm, "radius": 9 * mm});
            skCircle(sketch, "E4.0.7.18", {"center": v(270, 259.8) * mm, "radius": 9 * mm});
            skCircle(sketch, "E4.0.7.19", {"center": v(440, 242.49) * mm, "radius": 9 * mm});
            skCircle(sketch, "E4.0.7.20", {"center": v(110, 259.8) * mm, "radius": 9 * mm});
            skCircle(sketch, "E4.0.7.21", {"center": v(250, 259.8) * mm, "radius": 9 * mm});
            skCircle(sketch, "E4.0.7.22", {"center": v(180, 242.49) * mm, "radius": 9 * mm});
            skCircle(sketch, "E4.0.7.23", {"center": v(430, 259.8) * mm, "radius": 9 * mm});
            skCircle(sketch, "E4.0.7.24", {"center": v(200, 242.49) * mm, "radius": 9 * mm});
            skCircle(sketch, "E4.0.7.25", {"center": v(420, 242.49) * mm, "radius": 9 * mm});
            skCircle(sketch, "E4.0.7.26", {"center": v(70, 259.8) * mm, "radius": 9 * mm});
            skCircle(sketch, "E4.0.7.27", {"center": v(390, 259.8) * mm, "radius": 9 * mm});
            skCircle(sketch, "E4.0.7.28", {"center": v(220, 242.49) * mm, "radius": 9 * mm});
            skCircle(sketch, "E4.0.7.29", {"center": v(190, 259.8) * mm, "radius": 9 * mm});
            skCircle(sketch, "E4.0.7.30", {"center": v(90, 259.8) * mm, "radius": 9 * mm});
            skCircle(sketch, "E4.0.7.31", {"center": v(230, 259.8) * mm, "radius": 9 * mm});
            skCircle(sketch, "E4.0.7.32", {"center": v(150, 259.8) * mm, "radius": 9 * mm});
            skCircle(sketch, "E4.0.7.33", {"center": v(470, 259.8) * mm, "radius": 9 * mm});
            skCircle(sketch, "E4.0.7.34", {"center": v(410, 259.8) * mm, "radius": 9 * mm});
            skCircle(sketch, "E4.0.7.35", {"center": v(50, 259.8) * mm, "radius": 9 * mm});
            skCircle(sketch, "E4.0.7.36", {"center": v(400, 242.49) * mm, "radius": 9 * mm});
            skCircle(sketch, "E4.0.7.37", {"center": v(240, 242.49) * mm, "radius": 9 * mm});
            skCircle(sketch, "E4.0.7.38", {"center": v(320, 242.49) * mm, "radius": 9 * mm});
            skCircle(sketch, "E4.0.7.39", {"center": v(370, 259.8) * mm, "radius": 9 * mm});
            skCircle(sketch, "E4.0.7.40", {"center": v(10, 259.8) * mm, "radius": 9 * mm});
            skCircle(sketch, "E4.0.7.41", {"center": v(290, 259.8) * mm, "radius": 9 * mm});
            skCircle(sketch, "E4.0.7.42", {"center": v(360, 242.49) * mm, "radius": 9 * mm});
            skCircle(sketch, "E4.0.7.43", {"center": v(460, 242.49) * mm, "radius": 9 * mm});
            skCircle(sketch, "E4.0.7.44", {"center": v(310, 259.8) * mm, "radius": 9 * mm});
            skCircle(sketch, "E4.0.7.45", {"center": v(340, 242.49) * mm, "radius": 9 * mm});
            skCircle(sketch, "E4.0.7.46", {"center": v(170, 259.8) * mm, "radius": 9 * mm});
            skCircle(sketch, "E4.0.7.47", {"center": v(20, 242.49) * mm, "radius": 9 * mm});
            skLineSegment(sketch, "E4.0.7.48", {"start": v(0, 242.49) * mm, "end": v(20, 242.49) * mm, "construction": true});
            skLineSegment(sketch, "E4.0.7.49", {"start": v(10, 259.8) * mm, "end": v(30, 259.8) * mm, "construction": true});
            skCircle(sketch, "E4.0.8.0", {"center": v(280, 277.13) * mm, "radius": 9 * mm});
            skCircle(sketch, "E4.0.8.1", {"center": v(260, 277.13) * mm, "radius": 9 * mm});
            skCircle(sketch, "E4.0.8.2", {"center": v(130, 294.45) * mm, "radius": 9 * mm});
            skCircle(sketch, "E4.0.8.3", {"center": v(60, 277.13) * mm, "radius": 9 * mm});
            skCircle(sketch, "E4.0.8.4", {"center": v(80, 277.13) * mm, "radius": 9 * mm});
            skCircle(sketch, "E4.0.8.5", {"center": v(100, 277.13) * mm, "radius": 9 * mm});
            skCircle(sketch, "E4.0.8.6", {"center": v(350, 294.45) * mm, "radius": 9 * mm});
            skCircle(sketch, "E4.0.8.7", {"center": v(0, 277.13) * mm, "radius": 9 * mm});
            skCircle(sketch, "E4.0.8.8", {"center": v(120, 277.13) * mm, "radius": 9 * mm});
            skCircle(sketch, "E4.0.8.9", {"center": v(30, 294.45) * mm, "radius": 9 * mm});
            skCircle(sketch, "E4.0.8.10", {"center": v(380, 277.13) * mm, "radius": 9 * mm});
            skCircle(sketch, "E4.0.8.11", {"center": v(140, 277.13) * mm, "radius": 9 * mm});
            skCircle(sketch, "E4.0.8.12", {"center": v(450, 294.45) * mm, "radius": 9 * mm});
            skCircle(sketch, "E4.0.8.13", {"center": v(160, 277.13) * mm, "radius": 9 * mm});
            skCircle(sketch, "E4.0.8.14", {"center": v(300, 277.13) * mm, "radius": 9 * mm});
            skCircle(sketch, "E4.0.8.15", {"center": v(40, 277.13) * mm, "radius": 9 * mm});
            skCircle(sketch, "E4.0.8.16", {"center": v(210, 294.45) * mm, "radius": 9 * mm});
            skCircle(sketch, "E4.0.8.17", {"center": v(330, 294.45) * mm, "radius": 9 * mm});
            skCircle(sketch, "E4.0.8.18", {"center": v(270, 294.45) * mm, "radius": 9 * mm});
            skCircle(sketch, "E4.0.8.19", {"center": v(440, 277.13) * mm, "radius": 9 * mm});
            skCircle(sketch, "E4.0.8.20", {"center": v(110, 294.45) * mm, "radius": 9 * mm});
            skCircle(sketch, "E4.0.8.21", {"center": v(250, 294.45) * mm, "radius": 9 * mm});
            skCircle(sketch, "E4.0.8.22", {"center": v(180, 277.13) * mm, "radius": 9 * mm});
            skCircle(sketch, "E4.0.8.23", {"center": v(430, 294.45) * mm, "radius": 9 * mm});
            skCircle(sketch, "E4.0.8.24", {"center": v(200, 277.13) * mm, "radius": 9 * mm});
            skCircle(sketch, "E4.0.8.25", {"center": v(420, 277.13) * mm, "radius": 9 * mm});
            skCircle(sketch, "E4.0.8.26", {"center": v(70, 294.45) * mm, "radius": 9 * mm});
            skCircle(sketch, "E4.0.8.27", {"center": v(390, 294.45) * mm, "radius": 9 * mm});
            skCircle(sketch, "E4.0.8.28", {"center": v(220, 277.13) * mm, "radius": 9 * mm});
            skCircle(sketch, "E4.0.8.29", {"center": v(190, 294.45) * mm, "radius": 9 * mm});
            skCircle(sketch, "E4.0.8.30", {"center": v(90, 294.45) * mm, "radius": 9 * mm});
            skCircle(sketch, "E4.0.8.31", {"center": v(230, 294.45) * mm, "radius": 9 * mm});
            skCircle(sketch, "E4.0.8.32", {"center": v(150, 294.45) * mm, "radius": 9 * mm});
            skCircle(sketch, "E4.0.8.33", {"center": v(470, 294.45) * mm, "radius": 9 * mm});
            skCircle(sketch, "E4.0.8.34", {"center": v(410, 294.45) * mm, "radius": 9 * mm});
            skCircle(sketch, "E4.0.8.35", {"center": v(50, 294.45) * mm, "radius": 9 * mm});
            skCircle(sketch, "E4.0.8.36", {"center": v(400, 277.13) * mm, "radius": 9 * mm});
            skCircle(sketch, "E4.0.8.37", {"center": v(240, 277.13) * mm, "radius": 9 * mm});
            skCircle(sketch, "E4.0.8.38", {"center": v(320, 277.13) * mm, "radius": 9 * mm});
            skCircle(sketch, "E4.0.8.39", {"center": v(370, 294.45) * mm, "radius": 9 * mm});
            skCircle(sketch, "E4.0.8.40", {"center": v(10, 294.45) * mm, "radius": 9 * mm});
            skCircle(sketch, "E4.0.8.41", {"center": v(290, 294.45) * mm, "radius": 9 * mm});
            skCircle(sketch, "E4.0.8.42", {"center": v(360, 277.13) * mm, "radius": 9 * mm});
            skCircle(sketch, "E4.0.8.43", {"center": v(460, 277.13) * mm, "radius": 9 * mm});
            skCircle(sketch, "E4.0.8.44", {"center": v(310, 294.45) * mm, "radius": 9 * mm});
            skCircle(sketch, "E4.0.8.45", {"center": v(340, 277.13) * mm, "radius": 9 * mm});
            skCircle(sketch, "E4.0.8.46", {"center": v(170, 294.45) * mm, "radius": 9 * mm});
            skCircle(sketch, "E4.0.8.47", {"center": v(20, 277.13) * mm, "radius": 9 * mm});
            skLineSegment(sketch, "E4.0.8.48", {"start": v(0, 277.13) * mm, "end": v(20, 277.13) * mm, "construction": true});
            skLineSegment(sketch, "E4.0.8.49", {"start": v(10, 294.45) * mm, "end": v(30, 294.45) * mm, "construction": true});
            skCircle(sketch, "E4.0.9.0", {"center": v(280, 311.77) * mm, "radius": 9 * mm});
            skCircle(sketch, "E4.0.9.1", {"center": v(260, 311.77) * mm, "radius": 9 * mm});
            skCircle(sketch, "E4.0.9.2", {"center": v(130, 329.09) * mm, "radius": 9 * mm});
            skCircle(sketch, "E4.0.9.3", {"center": v(60, 311.77) * mm, "radius": 9 * mm});
            skCircle(sketch, "E4.0.9.4", {"center": v(80, 311.77) * mm, "radius": 9 * mm});
            skCircle(sketch, "E4.0.9.5", {"center": v(100, 311.77) * mm, "radius": 9 * mm});
            skCircle(sketch, "E4.0.9.6", {"center": v(350, 329.09) * mm, "radius": 9 * mm});
            skCircle(sketch, "E4.0.9.7", {"center": v(0, 311.77) * mm, "radius": 9 * mm});
            skCircle(sketch, "E4.0.9.8", {"center": v(120, 311.77) * mm, "radius": 9 * mm});
            skCircle(sketch, "E4.0.9.9", {"center": v(30, 329.09) * mm, "radius": 9 * mm});
            skCircle(sketch, "E4.0.9.10", {"center": v(380, 311.77) * mm, "radius": 9 * mm});
            skCircle(sketch, "E4.0.9.11", {"center": v(140, 311.77) * mm, "radius": 9 * mm});
            skCircle(sketch, "E4.0.9.12", {"center": v(450, 329.09) * mm, "radius": 9 * mm});
            skCircle(sketch, "E4.0.9.13", {"center": v(160, 311.77) * mm, "radius": 9 * mm});
            skCircle(sketch, "E4.0.9.14", {"center": v(300, 311.77) * mm, "radius": 9 * mm});
            skCircle(sketch, "E4.0.9.15", {"center": v(40, 311.77) * mm, "radius": 9 * mm});
            skCircle(sketch, "E4.0.9.16", {"center": v(210, 329.09) * mm, "radius": 9 * mm});
            skCircle(sketch, "E4.0.9.17", {"center": v(330, 329.09) * mm, "radius": 9 * mm});
            skCircle(sketch, "E4.0.9.18", {"center": v(270, 329.09) * mm, "radius": 9 * mm});
            skCircle(sketch, "E4.0.9.19", {"center": v(440, 311.77) * mm, "radius": 9 * mm});
            skCircle(sketch, "E4.0.9.20", {"center": v(110, 329.09) * mm, "radius": 9 * mm});
            skCircle(sketch, "E4.0.9.21", {"center": v(250, 329.09) * mm, "radius": 9 * mm});
            skCircle(sketch, "E4.0.9.22", {"center": v(180, 311.77) * mm, "radius": 9 * mm});
            skCircle(sketch, "E4.0.9.23", {"center": v(430, 329.09) * mm, "radius": 9 * mm});
            skCircle(sketch, "E4.0.9.24", {"center": v(200, 311.77) * mm, "radius": 9 * mm});
            skCircle(sketch, "E4.0.9.25", {"center": v(420, 311.77) * mm, "radius": 9 * mm});
            skCircle(sketch, "E4.0.9.26", {"center": v(70, 329.09) * mm, "radius": 9 * mm});
            skCircle(sketch, "E4.0.9.27", {"center": v(390, 329.09) * mm, "radius": 9 * mm});
            skCircle(sketch, "E4.0.9.28", {"center": v(220, 311.77) * mm, "radius": 9 * mm});
            skCircle(sketch, "E4.0.9.29", {"center": v(190, 329.09) * mm, "radius": 9 * mm});
            skCircle(sketch, "E4.0.9.30", {"center": v(90, 329.09) * mm, "radius": 9 * mm});
            skCircle(sketch, "E4.0.9.31", {"center": v(230, 329.09) * mm, "radius": 9 * mm});
            skCircle(sketch, "E4.0.9.32", {"center": v(150, 329.09) * mm, "radius": 9 * mm});
            skCircle(sketch, "E4.0.9.33", {"center": v(470, 329.09) * mm, "radius": 9 * mm});
            skCircle(sketch, "E4.0.9.34", {"center": v(410, 329.09) * mm, "radius": 9 * mm});
            skCircle(sketch, "E4.0.9.35", {"center": v(50, 329.09) * mm, "radius": 9 * mm});
            skCircle(sketch, "E4.0.9.36", {"center": v(400, 311.77) * mm, "radius": 9 * mm});
            skCircle(sketch, "E4.0.9.37", {"center": v(240, 311.77) * mm, "radius": 9 * mm});
            skCircle(sketch, "E4.0.9.38", {"center": v(320, 311.77) * mm, "radius": 9 * mm});
            skCircle(sketch, "E4.0.9.39", {"center": v(370, 329.09) * mm, "radius": 9 * mm});
            skCircle(sketch, "E4.0.9.40", {"center": v(10, 329.09) * mm, "radius": 9 * mm});
            skCircle(sketch, "E4.0.9.41", {"center": v(290, 329.09) * mm, "radius": 9 * mm});
            skCircle(sketch, "E4.0.9.42", {"center": v(360, 311.77) * mm, "radius": 9 * mm});
            skCircle(sketch, "E4.0.9.43", {"center": v(460, 311.77) * mm, "radius": 9 * mm});
            skCircle(sketch, "E4.0.9.44", {"center": v(310, 329.09) * mm, "radius": 9 * mm});
            skCircle(sketch, "E4.0.9.45", {"center": v(340, 311.77) * mm, "radius": 9 * mm});
            skCircle(sketch, "E4.0.9.46", {"center": v(170, 329.09) * mm, "radius": 9 * mm});
            skCircle(sketch, "E4.0.9.47", {"center": v(20, 311.77) * mm, "radius": 9 * mm});
            skLineSegment(sketch, "E4.0.9.48", {"start": v(0, 311.77) * mm, "end": v(20, 311.77) * mm, "construction": true});
            skLineSegment(sketch, "E4.0.9.49", {"start": v(10, 329.09) * mm, "end": v(30, 329.09) * mm, "construction": true});
            skCircle(sketch, "E4.0.10.0", {"center": v(280, 346.41) * mm, "radius": 9 * mm});
            skCircle(sketch, "E4.0.10.1", {"center": v(260, 346.41) * mm, "radius": 9 * mm});
            skCircle(sketch, "E4.0.10.2", {"center": v(130, 363.73) * mm, "radius": 9 * mm});
            skCircle(sketch, "E4.0.10.3", {"center": v(60, 346.41) * mm, "radius": 9 * mm});
            skCircle(sketch, "E4.0.10.4", {"center": v(80, 346.41) * mm, "radius": 9 * mm});
            skCircle(sketch, "E4.0.10.5", {"center": v(100, 346.41) * mm, "radius": 9 * mm});
            skCircle(sketch, "E4.0.10.6", {"center": v(350, 363.73) * mm, "radius": 9 * mm});
            skCircle(sketch, "E4.0.10.7", {"center": v(0, 346.41) * mm, "radius": 9 * mm});
            skCircle(sketch, "E4.0.10.8", {"center": v(120, 346.41) * mm, "radius": 9 * mm});
            skCircle(sketch, "E4.0.10.9", {"center": v(30, 363.73) * mm, "radius": 9 * mm});
            skCircle(sketch, "E4.0.10.10", {"center": v(380, 346.41) * mm, "radius": 9 * mm});
            skCircle(sketch, "E4.0.10.11", {"center": v(140, 346.41) * mm, "radius": 9 * mm});
            skCircle(sketch, "E4.0.10.12", {"center": v(450, 363.73) * mm, "radius": 9 * mm});
            skCircle(sketch, "E4.0.10.13", {"center": v(160, 346.41) * mm, "radius": 9 * mm});
            skCircle(sketch, "E4.0.10.14", {"center": v(300, 346.41) * mm, "radius": 9 * mm});
            skCircle(sketch, "E4.0.10.15", {"center": v(40, 346.41) * mm, "radius": 9 * mm});
            skCircle(sketch, "E4.0.10.16", {"center": v(210, 363.73) * mm, "radius": 9 * mm});
            skCircle(sketch, "E4.0.10.17", {"center": v(330, 363.73) * mm, "radius": 9 * mm});
            skCircle(sketch, "E4.0.10.18", {"center": v(270, 363.73) * mm, "radius": 9 * mm});
            skCircle(sketch, "E4.0.10.19", {"center": v(440, 346.41) * mm, "radius": 9 * mm});
            skCircle(sketch, "E4.0.10.20", {"center": v(110, 363.73) * mm, "radius": 9 * mm});
            skCircle(sketch, "E4.0.10.21", {"center": v(250, 363.73) * mm, "radius": 9 * mm});
            skCircle(sketch, "E4.0.10.22", {"center": v(180, 346.41) * mm, "radius": 9 * mm});
            skCircle(sketch, "E4.0.10.23", {"center": v(430, 363.73) * mm, "radius": 9 * mm});
            skCircle(sketch, "E4.0.10.24", {"center": v(200, 346.41) * mm, "radius": 9 * mm});
            skCircle(sketch, "E4.0.10.25", {"center": v(420, 346.41) * mm, "radius": 9 * mm});
            skCircle(sketch, "E4.0.10.26", {"center": v(70, 363.73) * mm, "radius": 9 * mm});
            skCircle(sketch, "E4.0.10.27", {"center": v(390, 363.73) * mm, "radius": 9 * mm});
            skCircle(sketch, "E4.0.10.28", {"center": v(220, 346.41) * mm, "radius": 9 * mm});
            skCircle(sketch, "E4.0.10.29", {"center": v(190, 363.73) * mm, "radius": 9 * mm});
            skCircle(sketch, "E4.0.10.30", {"center": v(90, 363.73) * mm, "radius": 9 * mm});
            skCircle(sketch, "E4.0.10.31", {"center": v(230, 363.73) * mm, "radius": 9 * mm});
            skCircle(sketch, "E4.0.10.32", {"center": v(150, 363.73) * mm, "radius": 9 * mm});
            skCircle(sketch, "E4.0.10.33", {"center": v(470, 363.73) * mm, "radius": 9 * mm});
            skCircle(sketch, "E4.0.10.34", {"center": v(410, 363.73) * mm, "radius": 9 * mm});
            skCircle(sketch, "E4.0.10.35", {"center": v(50, 363.73) * mm, "radius": 9 * mm});
            skCircle(sketch, "E4.0.10.36", {"center": v(400, 346.41) * mm, "radius": 9 * mm});
            skCircle(sketch, "E4.0.10.37", {"center": v(240, 346.41) * mm, "radius": 9 * mm});
            skCircle(sketch, "E4.0.10.38", {"center": v(320, 346.41) * mm, "radius": 9 * mm});
            skCircle(sketch, "E4.0.10.39", {"center": v(370, 363.73) * mm, "radius": 9 * mm});
            skCircle(sketch, "E4.0.10.40", {"center": v(10, 363.73) * mm, "radius": 9 * mm});
            skCircle(sketch, "E4.0.10.41", {"center": v(290, 363.73) * mm, "radius": 9 * mm});
            skCircle(sketch, "E4.0.10.42", {"center": v(360, 346.41) * mm, "radius": 9 * mm});
            skCircle(sketch, "E4.0.10.43", {"center": v(460, 346.41) * mm, "radius": 9 * mm});
            skCircle(sketch, "E4.0.10.44", {"center": v(310, 363.73) * mm, "radius": 9 * mm});
            skCircle(sketch, "E4.0.10.45", {"center": v(340, 346.41) * mm, "radius": 9 * mm});
            skCircle(sketch, "E4.0.10.46", {"center": v(170, 363.73) * mm, "radius": 9 * mm});
            skCircle(sketch, "E4.0.10.47", {"center": v(20, 346.41) * mm, "radius": 9 * mm});
            skLineSegment(sketch, "E4.0.10.48", {"start": v(0, 346.41) * mm, "end": v(20, 346.41) * mm, "construction": true});
            skLineSegment(sketch, "E4.0.10.49", {"start": v(10, 363.73) * mm, "end": v(30, 363.73) * mm, "construction": true});
            skCircle(sketch, "E4.0.11.0", {"center": v(280, 381.05) * mm, "radius": 9 * mm});
            skCircle(sketch, "E4.0.11.1", {"center": v(260, 381.05) * mm, "radius": 9 * mm});
            skCircle(sketch, "E4.0.11.2", {"center": v(130, 398.37) * mm, "radius": 9 * mm});
            skCircle(sketch, "E4.0.11.3", {"center": v(60, 381.05) * mm, "radius": 9 * mm});
            skCircle(sketch, "E4.0.11.4", {"center": v(80, 381.05) * mm, "radius": 9 * mm});
            skCircle(sketch, "E4.0.11.5", {"center": v(100, 381.05) * mm, "radius": 9 * mm});
            skCircle(sketch, "E4.0.11.6", {"center": v(350, 398.37) * mm, "radius": 9 * mm});
            skCircle(sketch, "E4.0.11.7", {"center": v(0, 381.05) * mm, "radius": 9 * mm});
            skCircle(sketch, "E4.0.11.8", {"center": v(120, 381.05) * mm, "radius": 9 * mm});
            skCircle(sketch, "E4.0.11.9", {"center": v(30, 398.37) * mm, "radius": 9 * mm});
            skCircle(sketch, "E4.0.11.10", {"center": v(380, 381.05) * mm, "radius": 9 * mm});
            skCircle(sketch, "E4.0.11.11", {"center": v(140, 381.05) * mm, "radius": 9 * mm});
            skCircle(sketch, "E4.0.11.12", {"center": v(450, 398.37) * mm, "radius": 9 * mm});
            skCircle(sketch, "E4.0.11.13", {"center": v(160, 381.05) * mm, "radius": 9 * mm});
            skCircle(sketch, "E4.0.11.14", {"center": v(300, 381.05) * mm, "radius": 9 * mm});
            skCircle(sketch, "E4.0.11.15", {"center": v(40, 381.05) * mm, "radius": 9 * mm});
            skCircle(sketch, "E4.0.11.16", {"center": v(210, 398.37) * mm, "radius": 9 * mm});
            skCircle(sketch, "E4.0.11.17", {"center": v(330, 398.37) * mm, "radius": 9 * mm});
            skCircle(sketch, "E4.0.11.18", {"center": v(270, 398.37) * mm, "radius": 9 * mm});
            skCircle(sketch, "E4.0.11.19", {"center": v(440, 381.05) * mm, "radius": 9 * mm});
            skCircle(sketch, "E4.0.11.20", {"center": v(110, 398.37) * mm, "radius": 9 * mm});
            skCircle(sketch, "E4.0.11.21", {"center": v(250, 398.37) * mm, "radius": 9 * mm});
            skCircle(sketch, "E4.0.11.22", {"center": v(180, 381.05) * mm, "radius": 9 * mm});
            skCircle(sketch, "E4.0.11.23", {"center": v(430, 398.37) * mm, "radius": 9 * mm});
            skCircle(sketch, "E4.0.11.24", {"center": v(200, 381.05) * mm, "radius": 9 * mm});
            skCircle(sketch, "E4.0.11.25", {"center": v(420, 381.05) * mm, "radius": 9 * mm});
            skCircle(sketch, "E4.0.11.26", {"center": v(70, 398.37) * mm, "radius": 9 * mm});
            skCircle(sketch, "E4.0.11.27", {"center": v(390, 398.37) * mm, "radius": 9 * mm});
            skCircle(sketch, "E4.0.11.28", {"center": v(220, 381.05) * mm, "radius": 9 * mm});
            skCircle(sketch, "E4.0.11.29", {"center": v(190, 398.37) * mm, "radius": 9 * mm});
            skCircle(sketch, "E4.0.11.30", {"center": v(90, 398.37) * mm, "radius": 9 * mm});
            skCircle(sketch, "E4.0.11.31", {"center": v(230, 398.37) * mm, "radius": 9 * mm});
            skCircle(sketch, "E4.0.11.32", {"center": v(150, 398.37) * mm, "radius": 9 * mm});
            skCircle(sketch, "E4.0.11.33", {"center": v(470, 398.37) * mm, "radius": 9 * mm});
            skCircle(sketch, "E4.0.11.34", {"center": v(410, 398.37) * mm, "radius": 9 * mm});
            skCircle(sketch, "E4.0.11.35", {"center": v(50, 398.37) * mm, "radius": 9 * mm});
            skCircle(sketch, "E4.0.11.36", {"center": v(400, 381.05) * mm, "radius": 9 * mm});
            skCircle(sketch, "E4.0.11.37", {"center": v(240, 381.05) * mm, "radius": 9 * mm});
            skCircle(sketch, "E4.0.11.38", {"center": v(320, 381.05) * mm, "radius": 9 * mm});
            skCircle(sketch, "E4.0.11.39", {"center": v(370, 398.37) * mm, "radius": 9 * mm});
            skCircle(sketch, "E4.0.11.40", {"center": v(10, 398.37) * mm, "radius": 9 * mm});
            skCircle(sketch, "E4.0.11.41", {"center": v(290, 398.37) * mm, "radius": 9 * mm});
            skCircle(sketch, "E4.0.11.42", {"center": v(360, 381.05) * mm, "radius": 9 * mm});
            skCircle(sketch, "E4.0.11.43", {"center": v(460, 381.05) * mm, "radius": 9 * mm});
            skCircle(sketch, "E4.0.11.44", {"center": v(310, 398.37) * mm, "radius": 9 * mm});
            skCircle(sketch, "E4.0.11.45", {"center": v(340, 381.05) * mm, "radius": 9 * mm});
            skCircle(sketch, "E4.0.11.46", {"center": v(170, 398.37) * mm, "radius": 9 * mm});
            skCircle(sketch, "E4.0.11.47", {"center": v(20, 381.05) * mm, "radius": 9 * mm});
            skLineSegment(sketch, "E4.0.11.48", {"start": v(0, 381.05) * mm, "end": v(20, 381.05) * mm, "construction": true});
            skLineSegment(sketch, "E4.0.11.49", {"start": v(10, 398.37) * mm, "end": v(30, 398.37) * mm, "construction": true});
            skCircle(sketch, "E4.0.12.0", {"center": v(280, 415.7) * mm, "radius": 9 * mm});
            skCircle(sketch, "E4.0.12.1", {"center": v(260, 415.7) * mm, "radius": 9 * mm});
            skCircle(sketch, "E4.0.12.2", {"center": v(130, 433.01) * mm, "radius": 9 * mm});
            skCircle(sketch, "E4.0.12.3", {"center": v(60, 415.7) * mm, "radius": 9 * mm});
            skCircle(sketch, "E4.0.12.4", {"center": v(80, 415.7) * mm, "radius": 9 * mm});
            skCircle(sketch, "E4.0.12.5", {"center": v(100, 415.7) * mm, "radius": 9 * mm});
            skCircle(sketch, "E4.0.12.6", {"center": v(350, 433.01) * mm, "radius": 9 * mm});
            skCircle(sketch, "E4.0.12.7", {"center": v(0, 415.7) * mm, "radius": 9 * mm});
            skCircle(sketch, "E4.0.12.8", {"center": v(120, 415.7) * mm, "radius": 9 * mm});
            skCircle(sketch, "E4.0.12.9", {"center": v(30, 433.01) * mm, "radius": 9 * mm});
            skCircle(sketch, "E4.0.12.10", {"center": v(380, 415.7) * mm, "radius": 9 * mm});
            skCircle(sketch, "E4.0.12.11", {"center": v(140, 415.7) * mm, "radius": 9 * mm});
            skCircle(sketch, "E4.0.12.12", {"center": v(450, 433.01) * mm, "radius": 9 * mm});
            skCircle(sketch, "E4.0.12.13", {"center": v(160, 415.7) * mm, "radius": 9 * mm});
            skCircle(sketch, "E4.0.12.14", {"center": v(300, 415.7) * mm, "radius": 9 * mm});
            skCircle(sketch, "E4.0.12.15", {"center": v(40, 415.7) * mm, "radius": 9 * mm});
            skCircle(sketch, "E4.0.12.16", {"center": v(210, 433.01) * mm, "radius": 9 * mm});
            skCircle(sketch, "E4.0.12.17", {"center": v(330, 433.01) * mm, "radius": 9 * mm});
            skCircle(sketch, "E4.0.12.18", {"center": v(270, 433.01) * mm, "radius": 9 * mm});
            skCircle(sketch, "E4.0.12.19", {"center": v(440, 415.7) * mm, "radius": 9 * mm});
            skCircle(sketch, "E4.0.12.20", {"center": v(110, 433.01) * mm, "radius": 9 * mm});
            skCircle(sketch, "E4.0.12.21", {"center": v(250, 433.01) * mm, "radius": 9 * mm});
            skCircle(sketch, "E4.0.12.22", {"center": v(180, 415.7) * mm, "radius": 9 * mm});
            skCircle(sketch, "E4.0.12.23", {"center": v(430, 433.01) * mm, "radius": 9 * mm});
            skCircle(sketch, "E4.0.12.24", {"center": v(200, 415.7) * mm, "radius": 9 * mm});
            skCircle(sketch, "E4.0.12.25", {"center": v(420, 415.7) * mm, "radius": 9 * mm});
            skCircle(sketch, "E4.0.12.26", {"center": v(70, 433.01) * mm, "radius": 9 * mm});
            skCircle(sketch, "E4.0.12.27", {"center": v(390, 433.01) * mm, "radius": 9 * mm});
            skCircle(sketch, "E4.0.12.28", {"center": v(220, 415.7) * mm, "radius": 9 * mm});
            skCircle(sketch, "E4.0.12.29", {"center": v(190, 433.01) * mm, "radius": 9 * mm});
            skCircle(sketch, "E4.0.12.30", {"center": v(90, 433.01) * mm, "radius": 9 * mm});
            skCircle(sketch, "E4.0.12.31", {"center": v(230, 433.01) * mm, "radius": 9 * mm});
            skCircle(sketch, "E4.0.12.32", {"center": v(150, 433.01) * mm, "radius": 9 * mm});
            skCircle(sketch, "E4.0.12.33", {"center": v(470, 433.01) * mm, "radius": 9 * mm});
            skCircle(sketch, "E4.0.12.34", {"center": v(410, 433.01) * mm, "radius": 9 * mm});
            skCircle(sketch, "E4.0.12.35", {"center": v(50, 433.01) * mm, "radius": 9 * mm});
            skCircle(sketch, "E4.0.12.36", {"center": v(400, 415.7) * mm, "radius": 9 * mm});
            skCircle(sketch, "E4.0.12.37", {"center": v(240, 415.7) * mm, "radius": 9 * mm});
            skCircle(sketch, "E4.0.12.38", {"center": v(320, 415.7) * mm, "radius": 9 * mm});
            skCircle(sketch, "E4.0.12.39", {"center": v(370, 433.01) * mm, "radius": 9 * mm});
            skCircle(sketch, "E4.0.12.40", {"center": v(10, 433.01) * mm, "radius": 9 * mm});
            skCircle(sketch, "E4.0.12.41", {"center": v(290, 433.01) * mm, "radius": 9 * mm});
            skCircle(sketch, "E4.0.12.42", {"center": v(360, 415.7) * mm, "radius": 9 * mm});
            skCircle(sketch, "E4.0.12.43", {"center": v(460, 415.7) * mm, "radius": 9 * mm});
            skCircle(sketch, "E4.0.12.44", {"center": v(310, 433.01) * mm, "radius": 9 * mm});
            skCircle(sketch, "E4.0.12.45", {"center": v(340, 415.7) * mm, "radius": 9 * mm});
            skCircle(sketch, "E4.0.12.46", {"center": v(170, 433.01) * mm, "radius": 9 * mm});
            skCircle(sketch, "E4.0.12.47", {"center": v(20, 415.7) * mm, "radius": 9 * mm});
            skLineSegment(sketch, "E4.0.12.48", {"start": v(0, 415.7) * mm, "end": v(20, 415.7) * mm, "construction": true});
            skLineSegment(sketch, "E4.0.12.49", {"start": v(10, 433.01) * mm, "end": v(30, 433.01) * mm, "construction": true});
            skCircle(sketch, "E4.0.13.0", {"center": v(280, 450.33) * mm, "radius": 9 * mm});
            skCircle(sketch, "E4.0.13.1", {"center": v(260, 450.33) * mm, "radius": 9 * mm});
            skCircle(sketch, "E4.0.13.2", {"center": v(130, 467.65) * mm, "radius": 9 * mm});
            skCircle(sketch, "E4.0.13.3", {"center": v(60, 450.33) * mm, "radius": 9 * mm});
            skCircle(sketch, "E4.0.13.4", {"center": v(80, 450.33) * mm, "radius": 9 * mm});
            skCircle(sketch, "E4.0.13.5", {"center": v(100, 450.33) * mm, "radius": 9 * mm});
            skCircle(sketch, "E4.0.13.6", {"center": v(350, 467.65) * mm, "radius": 9 * mm});
            skCircle(sketch, "E4.0.13.7", {"center": v(0, 450.33) * mm, "radius": 9 * mm});
            skCircle(sketch, "E4.0.13.8", {"center": v(120, 450.33) * mm, "radius": 9 * mm});
            skCircle(sketch, "E4.0.13.9", {"center": v(30, 467.65) * mm, "radius": 9 * mm});
            skCircle(sketch, "E4.0.13.10", {"center": v(380, 450.33) * mm, "radius": 9 * mm});
            skCircle(sketch, "E4.0.13.11", {"center": v(140, 450.33) * mm, "radius": 9 * mm});
            skCircle(sketch, "E4.0.13.12", {"center": v(450, 467.65) * mm, "radius": 9 * mm});
            skCircle(sketch, "E4.0.13.13", {"center": v(160, 450.33) * mm, "radius": 9 * mm});
            skCircle(sketch, "E4.0.13.14", {"center": v(300, 450.33) * mm, "radius": 9 * mm});
            skCircle(sketch, "E4.0.13.15", {"center": v(40, 450.33) * mm, "radius": 9 * mm});
            skCircle(sketch, "E4.0.13.16", {"center": v(210, 467.65) * mm, "radius": 9 * mm});
            skCircle(sketch, "E4.0.13.17", {"center": v(330, 467.65) * mm, "radius": 9 * mm});
            skCircle(sketch, "E4.0.13.18", {"center": v(270, 467.65) * mm, "radius": 9 * mm});
            skCircle(sketch, "E4.0.13.19", {"center": v(440, 450.33) * mm, "radius": 9 * mm});
            skCircle(sketch, "E4.0.13.20", {"center": v(110, 467.65) * mm, "radius": 9 * mm});
            skCircle(sketch, "E4.0.13.21", {"center": v(250, 467.65) * mm, "radius": 9 * mm});
            skCircle(sketch, "E4.0.13.22", {"center": v(180, 450.33) * mm, "radius": 9 * mm});
            skCircle(sketch, "E4.0.13.23", {"center": v(430, 467.65) * mm, "radius": 9 * mm});
            skCircle(sketch, "E4.0.13.24", {"center": v(200, 450.33) * mm, "radius": 9 * mm});
            skCircle(sketch, "E4.0.13.25", {"center": v(420, 450.33) * mm, "radius": 9 * mm});
            skCircle(sketch, "E4.0.13.26", {"center": v(70, 467.65) * mm, "radius": 9 * mm});
            skCircle(sketch, "E4.0.13.27", {"center": v(390, 467.65) * mm, "radius": 9 * mm});
            skCircle(sketch, "E4.0.13.28", {"center": v(220, 450.33) * mm, "radius": 9 * mm});
            skCircle(sketch, "E4.0.13.29", {"center": v(190, 467.65) * mm, "radius": 9 * mm});
            skCircle(sketch, "E4.0.13.30", {"center": v(90, 467.65) * mm, "radius": 9 * mm});
            skCircle(sketch, "E4.0.13.31", {"center": v(230, 467.65) * mm, "radius": 9 * mm});
            skCircle(sketch, "E4.0.13.32", {"center": v(150, 467.65) * mm, "radius": 9 * mm});
            skCircle(sketch, "E4.0.13.33", {"center": v(470, 467.65) * mm, "radius": 9 * mm});
            skCircle(sketch, "E4.0.13.34", {"center": v(410, 467.65) * mm, "radius": 9 * mm});
            skCircle(sketch, "E4.0.13.35", {"center": v(50, 467.65) * mm, "radius": 9 * mm});
            skCircle(sketch, "E4.0.13.36", {"center": v(400, 450.33) * mm, "radius": 9 * mm});
            skCircle(sketch, "E4.0.13.37", {"center": v(240, 450.33) * mm, "radius": 9 * mm});
            skCircle(sketch, "E4.0.13.38", {"center": v(320, 450.33) * mm, "radius": 9 * mm});
            skCircle(sketch, "E4.0.13.39", {"center": v(370, 467.65) * mm, "radius": 9 * mm});
            skCircle(sketch, "E4.0.13.40", {"center": v(10, 467.65) * mm, "radius": 9 * mm});
            skCircle(sketch, "E4.0.13.41", {"center": v(290, 467.65) * mm, "radius": 9 * mm});
            skCircle(sketch, "E4.0.13.42", {"center": v(360, 450.33) * mm, "radius": 9 * mm});
            skCircle(sketch, "E4.0.13.43", {"center": v(460, 450.33) * mm, "radius": 9 * mm});
            skCircle(sketch, "E4.0.13.44", {"center": v(310, 467.65) * mm, "radius": 9 * mm});
            skCircle(sketch, "E4.0.13.45", {"center": v(340, 450.33) * mm, "radius": 9 * mm});
            skCircle(sketch, "E4.0.13.46", {"center": v(170, 467.65) * mm, "radius": 9 * mm});
            skCircle(sketch, "E4.0.13.47", {"center": v(20, 450.33) * mm, "radius": 9 * mm});
            skLineSegment(sketch, "E4.0.13.48", {"start": v(0, 450.33) * mm, "end": v(20, 450.33) * mm, "construction": true});
            skLineSegment(sketch, "E4.0.13.49", {"start": v(10, 467.65) * mm, "end": v(30, 467.65) * mm, "construction": true});
            skLineSegment(sketch, "E4.direction1", {"start": v(0, 0) * mm, "end": v(25, 0) * mm, "construction": true});
            skLineSegment(sketch, "E4.direction2", {"start": v(0, 0) * mm, "end": v(0, 34.64) * mm, "construction": true});
            skLineSegment(sketch, "E5.bottom", {"start": v(470, 467.65) * mm, "end": v(0, 467.65) * mm, "construction": true});
            skLineSegment(sketch, "E5.top", {"start": v(470, 0) * mm, "end": v(0, 0) * mm, "construction": true});
            skLineSegment(sketch, "E5.left", {"start": v(470, 467.65) * mm, "end": v(470, 0) * mm, "construction": true});
            skLineSegment(sketch, "E5.right", {"start": v(0, 467.65) * mm, "end": v(0, 0) * mm, "construction": true});
            skLineSegment(sketch, "E6", {"start": v(0, 0) * mm, "end": v(470, 467.65) * mm, "construction": true});
            skLineSegment(sketch, "E7", {"start": v(0, 467.65) * mm, "end": v(470, 0) * mm, "construction": true});
            skPoint(sketch, "E8", {"position": v(235, 233.83) * mm});
            skSolve(sketch);
        }
        {
            var Q0;
            Q0=qCreatedBy(makeId("Top.planeOp"),FACE);
            var sketch = newSketch(context, id + "F1", { "sketchPlane" : qUnion([Q0])});
            skLineSegment(sketch, "E9.bottom", {"start": v(-14, 503.83) * mm, "end": v(484, 503.83) * mm});
            skLineSegment(sketch, "E9.top", {"start": v(-14, -36.17) * mm, "end": v(484, -36.17) * mm});
            skLineSegment(sketch, "E9.left", {"start": v(-14, 503.83) * mm, "end": v(-14, -36.17) * mm});
            skLineSegment(sketch, "E9.right", {"start": v(484, 503.83) * mm, "end": v(484, -36.17) * mm});
            skLineSegment(sketch, "E10", {"start": v(-14, 503.83) * mm, "end": v(484, -36.17) * mm, "construction": true});
            skLineSegment(sketch, "E11", {"start": v(484, 503.83) * mm, "end": v(-14, -36.17) * mm, "construction": true});
            skPoint(sketch, "E12", {"position": v(235, 233.83) * mm});
            skSolve(sketch);
        }
        {
            var Q0;
            Q0=qSketchRegion(id+"F1",true);
            extrude(context, id + "F2", {"entities" : qUnion([Q0]), "oppositeDirection" : true, "depth" : 10 * mm});
        }
        {
            var Q0;
            Q0=qSketchRegion(id+"F0",true);
            extrude(context, id + "F3", {"entities" : qUnion([Q0]), "operationType" : NewBodyOperationType.REMOVE, "oppositeDirection" : true, "depth" : 8 * mm});
        }
        {
            var Q0;
            Q0=makeQuery(id+"F2.opExtrude","CAP_FACE",FACE,{"disambiguationData":[OSD([sQuery(id+"F1.wireOp",EDGE,"E9.bottom"),sQuery(id+"F1.wireOp",EDGE,"E9.top"),sQuery(id+"F1.wireOp",EDGE,"E9.left"),sQuery(id+"F1.wireOp",EDGE,"E9.right")])],"isStart":false});
            var sketch = newSketch(context, id + "F4", { "sketchPlane" : qUnion([Q0])});
            skLineSegment(sketch, "E13.bottom", {"start": v(-14, -12.82) * mm, "end": v(484, -12.82) * mm});
            skLineSegment(sketch, "E13.top", {"start": v(-14, -21.82) * mm, "end": v(484, -21.82) * mm});
            skLineSegment(sketch, "E13.left", {"start": v(-14, -12.82) * mm, "end": v(-14, -21.82) * mm});
            skLineSegment(sketch, "E13.right", {"start": v(484, -12.82) * mm, "end": v(484, -21.82) * mm});
            skLineSegment(sketch, "E14.0.1.0", {"start": v(-14, -47.46) * mm, "end": v(484, -47.46) * mm});
            skLineSegment(sketch, "E14.0.1.1", {"start": v(-14, -56.46) * mm, "end": v(484, -56.46) * mm});
            skLineSegment(sketch, "E14.0.1.2", {"start": v(-14, -47.46) * mm, "end": v(-14, -56.46) * mm});
            skLineSegment(sketch, "E14.0.1.3", {"start": v(484, -47.46) * mm, "end": v(484, -56.46) * mm});
            skLineSegment(sketch, "E14.0.2.0", {"start": v(-14, -82.1) * mm, "end": v(484, -82.1) * mm});
            skLineSegment(sketch, "E14.0.2.1", {"start": v(-14, -91.1) * mm, "end": v(484, -91.1) * mm});
            skLineSegment(sketch, "E14.0.2.2", {"start": v(-14, -82.1) * mm, "end": v(-14, -91.1) * mm});
            skLineSegment(sketch, "E14.0.2.3", {"start": v(484, -82.1) * mm, "end": v(484, -91.1) * mm});
            skLineSegment(sketch, "E14.0.3.0", {"start": v(-14, -116.74) * mm, "end": v(484, -116.74) * mm});
            skLineSegment(sketch, "E14.0.3.1", {"start": v(-14, -125.74) * mm, "end": v(484, -125.74) * mm});
            skLineSegment(sketch, "E14.0.3.2", {"start": v(-14, -116.74) * mm, "end": v(-14, -125.74) * mm});
            skLineSegment(sketch, "E14.0.3.3", {"start": v(484, -116.74) * mm, "end": v(484, -125.74) * mm});
            skLineSegment(sketch, "E14.0.4.0", {"start": v(-14, -151.38) * mm, "end": v(484, -151.38) * mm});
            skLineSegment(sketch, "E14.0.4.1", {"start": v(-14, -160.38) * mm, "end": v(484, -160.38) * mm});
            skLineSegment(sketch, "E14.0.4.2", {"start": v(-14, -151.38) * mm, "end": v(-14, -160.38) * mm});
            skLineSegment(sketch, "E14.0.4.3", {"start": v(484, -151.38) * mm, "end": v(484, -160.38) * mm});
            skLineSegment(sketch, "E14.0.5.0", {"start": v(-14, -186.03) * mm, "end": v(484, -186.03) * mm});
            skLineSegment(sketch, "E14.0.5.1", {"start": v(-14, -195.03) * mm, "end": v(484, -195.03) * mm});
            skLineSegment(sketch, "E14.0.5.2", {"start": v(-14, -186.03) * mm, "end": v(-14, -195.03) * mm});
            skLineSegment(sketch, "E14.0.5.3", {"start": v(484, -186.03) * mm, "end": v(484, -195.03) * mm});
            skLineSegment(sketch, "E14.0.6.0", {"start": v(-14, -220.67) * mm, "end": v(484, -220.67) * mm});
            skLineSegment(sketch, "E14.0.6.1", {"start": v(-14, -229.67) * mm, "end": v(484, -229.67) * mm});
            skLineSegment(sketch, "E14.0.6.2", {"start": v(-14, -220.67) * mm, "end": v(-14, -229.67) * mm});
            skLineSegment(sketch, "E14.0.6.3", {"start": v(484, -220.67) * mm, "end": v(484, -229.67) * mm});
            skLineSegment(sketch, "E14.0.7.0", {"start": v(-14, -255.3) * mm, "end": v(484, -255.3) * mm});
            skLineSegment(sketch, "E14.0.7.1", {"start": v(-14, -264.3) * mm, "end": v(484, -264.3) * mm});
            skLineSegment(sketch, "E14.0.7.2", {"start": v(-14, -255.3) * mm, "end": v(-14, -264.3) * mm});
            skLineSegment(sketch, "E14.0.7.3", {"start": v(484, -255.3) * mm, "end": v(484, -264.3) * mm});
            skLineSegment(sketch, "E14.0.8.0", {"start": v(-14, -289.95) * mm, "end": v(484, -289.95) * mm});
            skLineSegment(sketch, "E14.0.8.1", {"start": v(-14, -298.95) * mm, "end": v(484, -298.95) * mm});
            skLineSegment(sketch, "E14.0.8.2", {"start": v(-14, -289.95) * mm, "end": v(-14, -298.95) * mm});
            skLineSegment(sketch, "E14.0.8.3", {"start": v(484, -289.95) * mm, "end": v(484, -298.95) * mm});
            skLineSegment(sketch, "E14.0.9.0", {"start": v(-14, -324.59) * mm, "end": v(484, -324.59) * mm});
            skLineSegment(sketch, "E14.0.9.1", {"start": v(-14, -333.59) * mm, "end": v(484, -333.59) * mm});
            skLineSegment(sketch, "E14.0.9.2", {"start": v(-14, -324.59) * mm, "end": v(-14, -333.59) * mm});
            skLineSegment(sketch, "E14.0.9.3", {"start": v(484, -324.59) * mm, "end": v(484, -333.59) * mm});
            skLineSegment(sketch, "E14.0.10.0", {"start": v(-14, -359.23) * mm, "end": v(484, -359.23) * mm});
            skLineSegment(sketch, "E14.0.10.1", {"start": v(-14, -368.23) * mm, "end": v(484, -368.23) * mm});
            skLineSegment(sketch, "E14.0.10.2", {"start": v(-14, -359.23) * mm, "end": v(-14, -368.23) * mm});
            skLineSegment(sketch, "E14.0.10.3", {"start": v(484, -359.23) * mm, "end": v(484, -368.23) * mm});
            skLineSegment(sketch, "E14.0.11.0", {"start": v(-14, -393.87) * mm, "end": v(484, -393.87) * mm});
            skLineSegment(sketch, "E14.0.11.1", {"start": v(-14, -402.87) * mm, "end": v(484, -402.87) * mm});
            skLineSegment(sketch, "E14.0.11.2", {"start": v(-14, -393.87) * mm, "end": v(-14, -402.87) * mm});
            skLineSegment(sketch, "E14.0.11.3", {"start": v(484, -393.87) * mm, "end": v(484, -402.87) * mm});
            skLineSegment(sketch, "E14.0.12.0", {"start": v(-14, -428.51) * mm, "end": v(484, -428.51) * mm});
            skLineSegment(sketch, "E14.0.12.1", {"start": v(-14, -437.51) * mm, "end": v(484, -437.51) * mm});
            skLineSegment(sketch, "E14.0.12.2", {"start": v(-14, -428.51) * mm, "end": v(-14, -437.51) * mm});
            skLineSegment(sketch, "E14.0.12.3", {"start": v(484, -428.51) * mm, "end": v(484, -437.51) * mm});
            skLineSegment(sketch, "E14.0.13.0", {"start": v(-14, -463.15) * mm, "end": v(484, -463.15) * mm});
            skLineSegment(sketch, "E14.0.13.1", {"start": v(-14, -472.15) * mm, "end": v(484, -472.15) * mm});
            skLineSegment(sketch, "E14.0.13.2", {"start": v(-14, -463.15) * mm, "end": v(-14, -472.15) * mm});
            skLineSegment(sketch, "E14.0.13.3", {"start": v(484, -463.15) * mm, "end": v(484, -472.15) * mm});
            skLineSegment(sketch, "E14.0.14.0", {"start": v(-14, -497.8) * mm, "end": v(484, -497.8) * mm});
            skLineSegment(sketch, "E14.0.14.1", {"start": v(-14, -506.8) * mm, "end": v(484, -506.8) * mm});
            skLineSegment(sketch, "E14.0.14.2", {"start": v(-14, -497.8) * mm, "end": v(-14, -506.8) * mm});
            skLineSegment(sketch, "E14.0.14.3", {"start": v(484, -497.8) * mm, "end": v(484, -506.8) * mm});
            skLineSegment(sketch, "E14.direction1", {"start": v(-14, -21.82) * mm, "end": v(5, -21.82) * mm, "construction": true});
            skLineSegment(sketch, "E14.direction2", {"start": v(-14, -21.82) * mm, "end": v(-14, -56.46) * mm, "construction": true});
            skSolve(sketch);
        }
        {
            var Q0;
            Q0 = qSketchRegion(id + "F4", true);
            extrude(context, id + "F5", {"entities" : qUnion([Q0]), "operationType" : NewBodyOperationType.REMOVE, "oppositeDirection" : true, "depth" : 2 * mm});
        }
        {
            var Q0;
            {var subQ0=sQuery(id+"F1.wireOp",EDGE,"E9.top");var subQ1=sQuery(id+"F1.wireOp",EDGE,"E9.left");var subQ2=sQuery(id+"F1.wireOp",EDGE,"E9.right");Q0=makeQuery(id+"F5.boolean.opBoolean","SPLIT",FACE,{"disambiguationData":[TD([makeQuery(id+"F2.opExtrude","SWEPT_FACE",FACE,{"disambiguationData":[OSD([subQ0])]})])],"derivedFrom":makeQuery(id+"F2.opExtrude","CAP_FACE",FACE,{"disambiguationData":[OSD([sQuery(id+"F1.wireOp",EDGE,"E9.bottom"),subQ0,subQ1,subQ2])],"isStart":false})});}
            var sketch = newSketch(context, id + "F6", { "sketchPlane" : qUnion([Q0])});
            skLineSegment(sketch, "E15.bottom", {"start": v(-4.5, 36.17) * mm, "end": v(4.5, 36.17) * mm});
            skLineSegment(sketch, "E15.top", {"start": v(-2.5, -5) * mm, "end": v(2.5, -5) * mm});
            skLineSegment(sketch, "E15.left", {"start": v(-4.5, 36.17) * mm, "end": v(-4.5, -3) * mm});
            skLineSegment(sketch, "E15.right", {"start": v(4.5, 36.17) * mm, "end": v(4.5, -3) * mm});
            skPoint(sketch, "E16.visualSharp", {"position": v(-4.5, -5) * mm});
            skArc(sketch, "E16.filletArc", {"start": v(-4.5, -3) * mm, "mid": v(-3.91, -4.41) * mm, "end": v(-2.5, -5) * mm});
            skPoint(sketch, "E17.visualSharp", {"position": v(4.5, -5) * mm});
            skArc(sketch, "E17.filletArc", {"start": v(2.5, -5) * mm, "mid": v(3.91, -4.41) * mm, "end": v(4.5, -3) * mm});
            skPoint(sketch, "E18.0.1.0", {"position": v(-4.5, -39.64) * mm});
            skLineSegment(sketch, "E18.0.1.1", {"start": v(4.5, 1.53) * mm, "end": v(4.5, -37.64) * mm});
            skPoint(sketch, "E18.0.1.2", {"position": v(4.5, -39.64) * mm});
            skLineSegment(sketch, "E18.0.1.3", {"start": v(-4.5, 1.53) * mm, "end": v(4.5, 1.53) * mm});
            skLineSegment(sketch, "E18.0.1.4", {"start": v(-2.5, -39.64) * mm, "end": v(2.5, -39.64) * mm});
            skLineSegment(sketch, "E18.0.1.5", {"start": v(-4.5, 1.53) * mm, "end": v(-4.5, -37.64) * mm});
            skArc(sketch, "E18.0.1.6", {"start": v(2.5, -39.64) * mm, "mid": v(3.91, -39.06) * mm, "end": v(4.5, -37.64) * mm});
            skArc(sketch, "E18.0.1.7", {"start": v(-4.5, -37.64) * mm, "mid": v(-3.91, -39.06) * mm, "end": v(-2.5, -39.64) * mm});
            skPoint(sketch, "E18.0.2.0", {"position": v(-4.5, -74.28) * mm});
            skLineSegment(sketch, "E18.0.2.1", {"start": v(4.5, -33.1) * mm, "end": v(4.5, -72.28) * mm});
            skPoint(sketch, "E18.0.2.2", {"position": v(4.5, -74.28) * mm});
            skLineSegment(sketch, "E18.0.2.3", {"start": v(-4.5, -33.1) * mm, "end": v(4.5, -33.1) * mm});
            skLineSegment(sketch, "E18.0.2.4", {"start": v(-2.5, -74.28) * mm, "end": v(2.5, -74.28) * mm});
            skLineSegment(sketch, "E18.0.2.5", {"start": v(-4.5, -33.1) * mm, "end": v(-4.5, -72.28) * mm});
            skArc(sketch, "E18.0.2.6", {"start": v(2.5, -74.28) * mm, "mid": v(3.91, -73.7) * mm, "end": v(4.5, -72.28) * mm});
            skArc(sketch, "E18.0.2.7", {"start": v(-4.5, -72.28) * mm, "mid": v(-3.91, -73.7) * mm, "end": v(-2.5, -74.28) * mm});
            skPoint(sketch, "E18.0.3.0", {"position": v(-4.5, -108.92) * mm});
            skLineSegment(sketch, "E18.0.3.1", {"start": v(4.5, -67.75) * mm, "end": v(4.5, -106.92) * mm});
            skPoint(sketch, "E18.0.3.2", {"position": v(4.5, -108.92) * mm});
            skLineSegment(sketch, "E18.0.3.3", {"start": v(-4.5, -67.75) * mm, "end": v(4.5, -67.75) * mm});
            skLineSegment(sketch, "E18.0.3.4", {"start": v(-2.5, -108.92) * mm, "end": v(2.5, -108.92) * mm});
            skLineSegment(sketch, "E18.0.3.5", {"start": v(-4.5, -67.75) * mm, "end": v(-4.5, -106.92) * mm});
            skArc(sketch, "E18.0.3.6", {"start": v(2.5, -108.92) * mm, "mid": v(3.91, -108.34) * mm, "end": v(4.5, -106.92) * mm});
            skArc(sketch, "E18.0.3.7", {"start": v(-4.5, -106.92) * mm, "mid": v(-3.91, -108.34) * mm, "end": v(-2.5, -108.92) * mm});
            skPoint(sketch, "E18.0.4.0", {"position": v(-4.5, -143.56) * mm});
            skLineSegment(sketch, "E18.0.4.1", {"start": v(4.5, -102.4) * mm, "end": v(4.5, -141.56) * mm});
            skPoint(sketch, "E18.0.4.2", {"position": v(4.5, -143.56) * mm});
            skLineSegment(sketch, "E18.0.4.3", {"start": v(-4.5, -102.4) * mm, "end": v(4.5, -102.4) * mm});
            skLineSegment(sketch, "E18.0.4.4", {"start": v(-2.5, -143.56) * mm, "end": v(2.5, -143.56) * mm});
            skLineSegment(sketch, "E18.0.4.5", {"start": v(-4.5, -102.4) * mm, "end": v(-4.5, -141.56) * mm});
            skArc(sketch, "E18.0.4.6", {"start": v(2.5, -143.56) * mm, "mid": v(3.91, -142.98) * mm, "end": v(4.5, -141.56) * mm});
            skArc(sketch, "E18.0.4.7", {"start": v(-4.5, -141.56) * mm, "mid": v(-3.91, -142.98) * mm, "end": v(-2.5, -143.56) * mm});
            skPoint(sketch, "E18.0.5.0", {"position": v(-4.5, -178.2) * mm});
            skLineSegment(sketch, "E18.0.5.1", {"start": v(4.5, -137.03) * mm, "end": v(4.5, -176.2) * mm});
            skPoint(sketch, "E18.0.5.2", {"position": v(4.5, -178.2) * mm});
            skLineSegment(sketch, "E18.0.5.3", {"start": v(-4.5, -137.03) * mm, "end": v(4.5, -137.03) * mm});
            skLineSegment(sketch, "E18.0.5.4", {"start": v(-2.5, -178.2) * mm, "end": v(2.5, -178.2) * mm});
            skLineSegment(sketch, "E18.0.5.5", {"start": v(-4.5, -137.03) * mm, "end": v(-4.5, -176.2) * mm});
            skArc(sketch, "E18.0.5.6", {"start": v(2.5, -178.2) * mm, "mid": v(3.91, -177.62) * mm, "end": v(4.5, -176.2) * mm});
            skArc(sketch, "E18.0.5.7", {"start": v(-4.5, -176.2) * mm, "mid": v(-3.91, -177.62) * mm, "end": v(-2.5, -178.2) * mm});
            skPoint(sketch, "E18.0.6.0", {"position": v(-4.5, -212.85) * mm});
            skLineSegment(sketch, "E18.0.6.1", {"start": v(4.5, -171.67) * mm, "end": v(4.5, -210.85) * mm});
            skPoint(sketch, "E18.0.6.2", {"position": v(4.5, -212.85) * mm});
            skLineSegment(sketch, "E18.0.6.3", {"start": v(-4.5, -171.67) * mm, "end": v(4.5, -171.67) * mm});
            skLineSegment(sketch, "E18.0.6.4", {"start": v(-2.5, -212.85) * mm, "end": v(2.5, -212.85) * mm});
            skLineSegment(sketch, "E18.0.6.5", {"start": v(-4.5, -171.67) * mm, "end": v(-4.5, -210.85) * mm});
            skArc(sketch, "E18.0.6.6", {"start": v(2.5, -212.85) * mm, "mid": v(3.91, -212.26) * mm, "end": v(4.5, -210.85) * mm});
            skArc(sketch, "E18.0.6.7", {"start": v(-4.5, -210.85) * mm, "mid": v(-3.91, -212.26) * mm, "end": v(-2.5, -212.85) * mm});
            skPoint(sketch, "E18.0.7.0", {"position": v(-4.5, -247.49) * mm});
            skLineSegment(sketch, "E18.0.7.1", {"start": v(4.5, -206.31) * mm, "end": v(4.5, -245.49) * mm});
            skPoint(sketch, "E18.0.7.2", {"position": v(4.5, -247.49) * mm});
            skLineSegment(sketch, "E18.0.7.3", {"start": v(-4.5, -206.31) * mm, "end": v(4.5, -206.31) * mm});
            skLineSegment(sketch, "E18.0.7.4", {"start": v(-2.5, -247.49) * mm, "end": v(2.5, -247.49) * mm});
            skLineSegment(sketch, "E18.0.7.5", {"start": v(-4.5, -206.31) * mm, "end": v(-4.5, -245.49) * mm});
            skArc(sketch, "E18.0.7.6", {"start": v(2.5, -247.49) * mm, "mid": v(3.91, -246.9) * mm, "end": v(4.5, -245.49) * mm});
            skArc(sketch, "E18.0.7.7", {"start": v(-4.5, -245.49) * mm, "mid": v(-3.91, -246.9) * mm, "end": v(-2.5, -247.49) * mm});
            skPoint(sketch, "E18.0.8.0", {"position": v(-4.5, -282.13) * mm});
            skLineSegment(sketch, "E18.0.8.1", {"start": v(4.5, -240.95) * mm, "end": v(4.5, -280.13) * mm});
            skPoint(sketch, "E18.0.8.2", {"position": v(4.5, -282.13) * mm});
            skLineSegment(sketch, "E18.0.8.3", {"start": v(-4.5, -240.95) * mm, "end": v(4.5, -240.95) * mm});
            skLineSegment(sketch, "E18.0.8.4", {"start": v(-2.5, -282.13) * mm, "end": v(2.5, -282.13) * mm});
            skLineSegment(sketch, "E18.0.8.5", {"start": v(-4.5, -240.95) * mm, "end": v(-4.5, -280.13) * mm});
            skArc(sketch, "E18.0.8.6", {"start": v(2.5, -282.13) * mm, "mid": v(3.91, -281.54) * mm, "end": v(4.5, -280.13) * mm});
            skArc(sketch, "E18.0.8.7", {"start": v(-4.5, -280.13) * mm, "mid": v(-3.91, -281.54) * mm, "end": v(-2.5, -282.13) * mm});
            skPoint(sketch, "E18.0.9.0", {"position": v(-4.5, -316.77) * mm});
            skLineSegment(sketch, "E18.0.9.1", {"start": v(4.5, -275.6) * mm, "end": v(4.5, -314.77) * mm});
            skPoint(sketch, "E18.0.9.2", {"position": v(4.5, -316.77) * mm});
            skLineSegment(sketch, "E18.0.9.3", {"start": v(-4.5, -275.6) * mm, "end": v(4.5, -275.6) * mm});
            skLineSegment(sketch, "E18.0.9.4", {"start": v(-2.5, -316.77) * mm, "end": v(2.5, -316.77) * mm});
            skLineSegment(sketch, "E18.0.9.5", {"start": v(-4.5, -275.6) * mm, "end": v(-4.5, -314.77) * mm});
            skArc(sketch, "E18.0.9.6", {"start": v(2.5, -316.77) * mm, "mid": v(3.91, -316.18) * mm, "end": v(4.5, -314.77) * mm});
            skArc(sketch, "E18.0.9.7", {"start": v(-4.5, -314.77) * mm, "mid": v(-3.91, -316.18) * mm, "end": v(-2.5, -316.77) * mm});
            skPoint(sketch, "E18.0.10.0", {"position": v(-4.5, -351.41) * mm});
            skLineSegment(sketch, "E18.0.10.1", {"start": v(4.5, -310.24) * mm, "end": v(4.5, -349.41) * mm});
            skPoint(sketch, "E18.0.10.2", {"position": v(4.5, -351.41) * mm});
            skLineSegment(sketch, "E18.0.10.3", {"start": v(-4.5, -310.24) * mm, "end": v(4.5, -310.24) * mm});
            skLineSegment(sketch, "E18.0.10.4", {"start": v(-2.5, -351.41) * mm, "end": v(2.5, -351.41) * mm});
            skLineSegment(sketch, "E18.0.10.5", {"start": v(-4.5, -310.24) * mm, "end": v(-4.5, -349.41) * mm});
            skArc(sketch, "E18.0.10.6", {"start": v(2.5, -351.41) * mm, "mid": v(3.91, -350.82) * mm, "end": v(4.5, -349.41) * mm});
            skArc(sketch, "E18.0.10.7", {"start": v(-4.5, -349.41) * mm, "mid": v(-3.91, -350.82) * mm, "end": v(-2.5, -351.41) * mm});
            skPoint(sketch, "E18.0.11.0", {"position": v(-4.5, -386.05) * mm});
            skLineSegment(sketch, "E18.0.11.1", {"start": v(4.5, -344.88) * mm, "end": v(4.5, -384.05) * mm});
            skPoint(sketch, "E18.0.11.2", {"position": v(4.5, -386.05) * mm});
            skLineSegment(sketch, "E18.0.11.3", {"start": v(-4.5, -344.88) * mm, "end": v(4.5, -344.88) * mm});
            skLineSegment(sketch, "E18.0.11.4", {"start": v(-2.5, -386.05) * mm, "end": v(2.5, -386.05) * mm});
            skLineSegment(sketch, "E18.0.11.5", {"start": v(-4.5, -344.88) * mm, "end": v(-4.5, -384.05) * mm});
            skArc(sketch, "E18.0.11.6", {"start": v(2.5, -386.05) * mm, "mid": v(3.91, -385.47) * mm, "end": v(4.5, -384.05) * mm});
            skArc(sketch, "E18.0.11.7", {"start": v(-4.5, -384.05) * mm, "mid": v(-3.91, -385.47) * mm, "end": v(-2.5, -386.05) * mm});
            skPoint(sketch, "E18.0.12.0", {"position": v(-4.5, -420.7) * mm});
            skLineSegment(sketch, "E18.0.12.1", {"start": v(4.5, -379.52) * mm, "end": v(4.5, -418.7) * mm});
            skPoint(sketch, "E18.0.12.2", {"position": v(4.5, -420.7) * mm});
            skLineSegment(sketch, "E18.0.12.3", {"start": v(-4.5, -379.52) * mm, "end": v(4.5, -379.52) * mm});
            skLineSegment(sketch, "E18.0.12.4", {"start": v(-2.5, -420.7) * mm, "end": v(2.5, -420.7) * mm});
            skLineSegment(sketch, "E18.0.12.5", {"start": v(-4.5, -379.52) * mm, "end": v(-4.5, -418.7) * mm});
            skArc(sketch, "E18.0.12.6", {"start": v(2.5, -420.7) * mm, "mid": v(3.91, -420.1) * mm, "end": v(4.5, -418.7) * mm});
            skArc(sketch, "E18.0.12.7", {"start": v(-4.5, -418.7) * mm, "mid": v(-3.91, -420.1) * mm, "end": v(-2.5, -420.7) * mm});
            skPoint(sketch, "E18.0.13.0", {"position": v(-4.5, -455.33) * mm});
            skLineSegment(sketch, "E18.0.13.1", {"start": v(4.5, -414.16) * mm, "end": v(4.5, -453.33) * mm});
            skPoint(sketch, "E18.0.13.2", {"position": v(4.5, -455.33) * mm});
            skLineSegment(sketch, "E18.0.13.3", {"start": v(-4.5, -414.16) * mm, "end": v(4.5, -414.16) * mm});
            skLineSegment(sketch, "E18.0.13.4", {"start": v(-2.5, -455.33) * mm, "end": v(2.5, -455.33) * mm});
            skLineSegment(sketch, "E18.0.13.5", {"start": v(-4.5, -414.16) * mm, "end": v(-4.5, -453.33) * mm});
            skArc(sketch, "E18.0.13.6", {"start": v(2.5, -455.33) * mm, "mid": v(3.91, -454.75) * mm, "end": v(4.5, -453.33) * mm});
            skArc(sketch, "E18.0.13.7", {"start": v(-4.5, -453.33) * mm, "mid": v(-3.91, -454.75) * mm, "end": v(-2.5, -455.33) * mm});
            skPoint(sketch, "E18.0.14.0", {"position": v(-4.5, -489.97) * mm});
            skLineSegment(sketch, "E18.0.14.1", {"start": v(4.5, -448.8) * mm, "end": v(4.5, -487.97) * mm});
            skPoint(sketch, "E18.0.14.2", {"position": v(4.5, -489.97) * mm});
            skLineSegment(sketch, "E18.0.14.3", {"start": v(-4.5, -448.8) * mm, "end": v(4.5, -448.8) * mm});
            skLineSegment(sketch, "E18.0.14.4", {"start": v(-2.5, -489.97) * mm, "end": v(2.5, -489.97) * mm});
            skLineSegment(sketch, "E18.0.14.5", {"start": v(-4.5, -448.8) * mm, "end": v(-4.5, -487.97) * mm});
            skArc(sketch, "E18.0.14.6", {"start": v(2.5, -489.97) * mm, "mid": v(3.91, -489.39) * mm, "end": v(4.5, -487.97) * mm});
            skArc(sketch, "E18.0.14.7", {"start": v(-4.5, -487.97) * mm, "mid": v(-3.91, -489.39) * mm, "end": v(-2.5, -489.97) * mm});
            skPoint(sketch, "E18.1.0.0", {"position": v(15.5, -5) * mm});
            skLineSegment(sketch, "E18.1.0.1", {"start": v(24.5, 36.17) * mm, "end": v(24.5, -3) * mm});
            skPoint(sketch, "E18.1.0.2", {"position": v(24.5, -5) * mm});
            skLineSegment(sketch, "E18.1.0.3", {"start": v(15.5, 36.17) * mm, "end": v(24.5, 36.17) * mm});
            skLineSegment(sketch, "E18.1.0.4", {"start": v(17.5, -5) * mm, "end": v(22.5, -5) * mm});
            skLineSegment(sketch, "E18.1.0.5", {"start": v(15.5, 36.17) * mm, "end": v(15.5, -3) * mm});
            skArc(sketch, "E18.1.0.6", {"start": v(22.5, -5) * mm, "mid": v(23.91, -4.41) * mm, "end": v(24.5, -3) * mm});
            skArc(sketch, "E18.1.0.7", {"start": v(15.5, -3) * mm, "mid": v(16.09, -4.41) * mm, "end": v(17.5, -5) * mm});
            skPoint(sketch, "E18.1.1.0", {"position": v(15.5, -39.64) * mm});
            skLineSegment(sketch, "E18.1.1.1", {"start": v(24.5, 1.53) * mm, "end": v(24.5, -37.64) * mm});
            skPoint(sketch, "E18.1.1.2", {"position": v(24.5, -39.64) * mm});
            skLineSegment(sketch, "E18.1.1.3", {"start": v(15.5, 1.53) * mm, "end": v(24.5, 1.53) * mm});
            skLineSegment(sketch, "E18.1.1.4", {"start": v(17.5, -39.64) * mm, "end": v(22.5, -39.64) * mm});
            skLineSegment(sketch, "E18.1.1.5", {"start": v(15.5, 1.53) * mm, "end": v(15.5, -37.64) * mm});
            skArc(sketch, "E18.1.1.6", {"start": v(22.5, -39.64) * mm, "mid": v(23.91, -39.06) * mm, "end": v(24.5, -37.64) * mm});
            skArc(sketch, "E18.1.1.7", {"start": v(15.5, -37.64) * mm, "mid": v(16.09, -39.06) * mm, "end": v(17.5, -39.64) * mm});
            skPoint(sketch, "E18.1.2.0", {"position": v(15.5, -74.28) * mm});
            skLineSegment(sketch, "E18.1.2.1", {"start": v(24.5, -33.1) * mm, "end": v(24.5, -72.28) * mm});
            skPoint(sketch, "E18.1.2.2", {"position": v(24.5, -74.28) * mm});
            skLineSegment(sketch, "E18.1.2.3", {"start": v(15.5, -33.1) * mm, "end": v(24.5, -33.1) * mm});
            skLineSegment(sketch, "E18.1.2.4", {"start": v(17.5, -74.28) * mm, "end": v(22.5, -74.28) * mm});
            skLineSegment(sketch, "E18.1.2.5", {"start": v(15.5, -33.1) * mm, "end": v(15.5, -72.28) * mm});
            skArc(sketch, "E18.1.2.6", {"start": v(22.5, -74.28) * mm, "mid": v(23.91, -73.7) * mm, "end": v(24.5, -72.28) * mm});
            skArc(sketch, "E18.1.2.7", {"start": v(15.5, -72.28) * mm, "mid": v(16.09, -73.7) * mm, "end": v(17.5, -74.28) * mm});
            skPoint(sketch, "E18.1.3.0", {"position": v(15.5, -108.92) * mm});
            skLineSegment(sketch, "E18.1.3.1", {"start": v(24.5, -67.75) * mm, "end": v(24.5, -106.92) * mm});
            skPoint(sketch, "E18.1.3.2", {"position": v(24.5, -108.92) * mm});
            skLineSegment(sketch, "E18.1.3.3", {"start": v(15.5, -67.75) * mm, "end": v(24.5, -67.75) * mm});
            skLineSegment(sketch, "E18.1.3.4", {"start": v(17.5, -108.92) * mm, "end": v(22.5, -108.92) * mm});
            skLineSegment(sketch, "E18.1.3.5", {"start": v(15.5, -67.75) * mm, "end": v(15.5, -106.92) * mm});
            skArc(sketch, "E18.1.3.6", {"start": v(22.5, -108.92) * mm, "mid": v(23.91, -108.34) * mm, "end": v(24.5, -106.92) * mm});
            skArc(sketch, "E18.1.3.7", {"start": v(15.5, -106.92) * mm, "mid": v(16.09, -108.34) * mm, "end": v(17.5, -108.92) * mm});
            skPoint(sketch, "E18.1.4.0", {"position": v(15.5, -143.56) * mm});
            skLineSegment(sketch, "E18.1.4.1", {"start": v(24.5, -102.4) * mm, "end": v(24.5, -141.56) * mm});
            skPoint(sketch, "E18.1.4.2", {"position": v(24.5, -143.56) * mm});
            skLineSegment(sketch, "E18.1.4.3", {"start": v(15.5, -102.4) * mm, "end": v(24.5, -102.4) * mm});
            skLineSegment(sketch, "E18.1.4.4", {"start": v(17.5, -143.56) * mm, "end": v(22.5, -143.56) * mm});
            skLineSegment(sketch, "E18.1.4.5", {"start": v(15.5, -102.4) * mm, "end": v(15.5, -141.56) * mm});
            skArc(sketch, "E18.1.4.6", {"start": v(22.5, -143.56) * mm, "mid": v(23.91, -142.98) * mm, "end": v(24.5, -141.56) * mm});
            skArc(sketch, "E18.1.4.7", {"start": v(15.5, -141.56) * mm, "mid": v(16.09, -142.98) * mm, "end": v(17.5, -143.56) * mm});
            skPoint(sketch, "E18.1.5.0", {"position": v(15.5, -178.2) * mm});
            skLineSegment(sketch, "E18.1.5.1", {"start": v(24.5, -137.03) * mm, "end": v(24.5, -176.2) * mm});
            skPoint(sketch, "E18.1.5.2", {"position": v(24.5, -178.2) * mm});
            skLineSegment(sketch, "E18.1.5.3", {"start": v(15.5, -137.03) * mm, "end": v(24.5, -137.03) * mm});
            skLineSegment(sketch, "E18.1.5.4", {"start": v(17.5, -178.2) * mm, "end": v(22.5, -178.2) * mm});
            skLineSegment(sketch, "E18.1.5.5", {"start": v(15.5, -137.03) * mm, "end": v(15.5, -176.2) * mm});
            skArc(sketch, "E18.1.5.6", {"start": v(22.5, -178.2) * mm, "mid": v(23.91, -177.62) * mm, "end": v(24.5, -176.2) * mm});
            skArc(sketch, "E18.1.5.7", {"start": v(15.5, -176.2) * mm, "mid": v(16.09, -177.62) * mm, "end": v(17.5, -178.2) * mm});
            skPoint(sketch, "E18.1.6.0", {"position": v(15.5, -212.85) * mm});
            skLineSegment(sketch, "E18.1.6.1", {"start": v(24.5, -171.67) * mm, "end": v(24.5, -210.85) * mm});
            skPoint(sketch, "E18.1.6.2", {"position": v(24.5, -212.85) * mm});
            skLineSegment(sketch, "E18.1.6.3", {"start": v(15.5, -171.67) * mm, "end": v(24.5, -171.67) * mm});
            skLineSegment(sketch, "E18.1.6.4", {"start": v(17.5, -212.85) * mm, "end": v(22.5, -212.85) * mm});
            skLineSegment(sketch, "E18.1.6.5", {"start": v(15.5, -171.67) * mm, "end": v(15.5, -210.85) * mm});
            skArc(sketch, "E18.1.6.6", {"start": v(22.5, -212.85) * mm, "mid": v(23.91, -212.26) * mm, "end": v(24.5, -210.85) * mm});
            skArc(sketch, "E18.1.6.7", {"start": v(15.5, -210.85) * mm, "mid": v(16.09, -212.26) * mm, "end": v(17.5, -212.85) * mm});
            skPoint(sketch, "E18.1.7.0", {"position": v(15.5, -247.49) * mm});
            skLineSegment(sketch, "E18.1.7.1", {"start": v(24.5, -206.31) * mm, "end": v(24.5, -245.49) * mm});
            skPoint(sketch, "E18.1.7.2", {"position": v(24.5, -247.49) * mm});
            skLineSegment(sketch, "E18.1.7.3", {"start": v(15.5, -206.31) * mm, "end": v(24.5, -206.31) * mm});
            skLineSegment(sketch, "E18.1.7.4", {"start": v(17.5, -247.49) * mm, "end": v(22.5, -247.49) * mm});
            skLineSegment(sketch, "E18.1.7.5", {"start": v(15.5, -206.31) * mm, "end": v(15.5, -245.49) * mm});
            skArc(sketch, "E18.1.7.6", {"start": v(22.5, -247.49) * mm, "mid": v(23.91, -246.9) * mm, "end": v(24.5, -245.49) * mm});
            skArc(sketch, "E18.1.7.7", {"start": v(15.5, -245.49) * mm, "mid": v(16.09, -246.9) * mm, "end": v(17.5, -247.49) * mm});
            skPoint(sketch, "E18.1.8.0", {"position": v(15.5, -282.13) * mm});
            skLineSegment(sketch, "E18.1.8.1", {"start": v(24.5, -240.95) * mm, "end": v(24.5, -280.13) * mm});
            skPoint(sketch, "E18.1.8.2", {"position": v(24.5, -282.13) * mm});
            skLineSegment(sketch, "E18.1.8.3", {"start": v(15.5, -240.95) * mm, "end": v(24.5, -240.95) * mm});
            skLineSegment(sketch, "E18.1.8.4", {"start": v(17.5, -282.13) * mm, "end": v(22.5, -282.13) * mm});
            skLineSegment(sketch, "E18.1.8.5", {"start": v(15.5, -240.95) * mm, "end": v(15.5, -280.13) * mm});
            skArc(sketch, "E18.1.8.6", {"start": v(22.5, -282.13) * mm, "mid": v(23.91, -281.54) * mm, "end": v(24.5, -280.13) * mm});
            skArc(sketch, "E18.1.8.7", {"start": v(15.5, -280.13) * mm, "mid": v(16.09, -281.54) * mm, "end": v(17.5, -282.13) * mm});
            skPoint(sketch, "E18.1.9.0", {"position": v(15.5, -316.77) * mm});
            skLineSegment(sketch, "E18.1.9.1", {"start": v(24.5, -275.6) * mm, "end": v(24.5, -314.77) * mm});
            skPoint(sketch, "E18.1.9.2", {"position": v(24.5, -316.77) * mm});
            skLineSegment(sketch, "E18.1.9.3", {"start": v(15.5, -275.6) * mm, "end": v(24.5, -275.6) * mm});
            skLineSegment(sketch, "E18.1.9.4", {"start": v(17.5, -316.77) * mm, "end": v(22.5, -316.77) * mm});
            skLineSegment(sketch, "E18.1.9.5", {"start": v(15.5, -275.6) * mm, "end": v(15.5, -314.77) * mm});
            skArc(sketch, "E18.1.9.6", {"start": v(22.5, -316.77) * mm, "mid": v(23.91, -316.18) * mm, "end": v(24.5, -314.77) * mm});
            skArc(sketch, "E18.1.9.7", {"start": v(15.5, -314.77) * mm, "mid": v(16.09, -316.18) * mm, "end": v(17.5, -316.77) * mm});
            skPoint(sketch, "E18.1.10.0", {"position": v(15.5, -351.41) * mm});
            skLineSegment(sketch, "E18.1.10.1", {"start": v(24.5, -310.24) * mm, "end": v(24.5, -349.41) * mm});
            skPoint(sketch, "E18.1.10.2", {"position": v(24.5, -351.41) * mm});
            skLineSegment(sketch, "E18.1.10.3", {"start": v(15.5, -310.24) * mm, "end": v(24.5, -310.24) * mm});
            skLineSegment(sketch, "E18.1.10.4", {"start": v(17.5, -351.41) * mm, "end": v(22.5, -351.41) * mm});
            skLineSegment(sketch, "E18.1.10.5", {"start": v(15.5, -310.24) * mm, "end": v(15.5, -349.41) * mm});
            skArc(sketch, "E18.1.10.6", {"start": v(22.5, -351.41) * mm, "mid": v(23.91, -350.82) * mm, "end": v(24.5, -349.41) * mm});
            skArc(sketch, "E18.1.10.7", {"start": v(15.5, -349.41) * mm, "mid": v(16.09, -350.82) * mm, "end": v(17.5, -351.41) * mm});
            skPoint(sketch, "E18.1.11.0", {"position": v(15.5, -386.05) * mm});
            skLineSegment(sketch, "E18.1.11.1", {"start": v(24.5, -344.88) * mm, "end": v(24.5, -384.05) * mm});
            skPoint(sketch, "E18.1.11.2", {"position": v(24.5, -386.05) * mm});
            skLineSegment(sketch, "E18.1.11.3", {"start": v(15.5, -344.88) * mm, "end": v(24.5, -344.88) * mm});
            skLineSegment(sketch, "E18.1.11.4", {"start": v(17.5, -386.05) * mm, "end": v(22.5, -386.05) * mm});
            skLineSegment(sketch, "E18.1.11.5", {"start": v(15.5, -344.88) * mm, "end": v(15.5, -384.05) * mm});
            skArc(sketch, "E18.1.11.6", {"start": v(22.5, -386.05) * mm, "mid": v(23.91, -385.47) * mm, "end": v(24.5, -384.05) * mm});
            skArc(sketch, "E18.1.11.7", {"start": v(15.5, -384.05) * mm, "mid": v(16.09, -385.47) * mm, "end": v(17.5, -386.05) * mm});
            skPoint(sketch, "E18.1.12.0", {"position": v(15.5, -420.7) * mm});
            skLineSegment(sketch, "E18.1.12.1", {"start": v(24.5, -379.52) * mm, "end": v(24.5, -418.7) * mm});
            skPoint(sketch, "E18.1.12.2", {"position": v(24.5, -420.7) * mm});
            skLineSegment(sketch, "E18.1.12.3", {"start": v(15.5, -379.52) * mm, "end": v(24.5, -379.52) * mm});
            skLineSegment(sketch, "E18.1.12.4", {"start": v(17.5, -420.7) * mm, "end": v(22.5, -420.7) * mm});
            skLineSegment(sketch, "E18.1.12.5", {"start": v(15.5, -379.52) * mm, "end": v(15.5, -418.7) * mm});
            skArc(sketch, "E18.1.12.6", {"start": v(22.5, -420.7) * mm, "mid": v(23.91, -420.1) * mm, "end": v(24.5, -418.7) * mm});
            skArc(sketch, "E18.1.12.7", {"start": v(15.5, -418.7) * mm, "mid": v(16.09, -420.1) * mm, "end": v(17.5, -420.7) * mm});
            skPoint(sketch, "E18.1.13.0", {"position": v(15.5, -455.33) * mm});
            skLineSegment(sketch, "E18.1.13.1", {"start": v(24.5, -414.16) * mm, "end": v(24.5, -453.33) * mm});
            skPoint(sketch, "E18.1.13.2", {"position": v(24.5, -455.33) * mm});
            skLineSegment(sketch, "E18.1.13.3", {"start": v(15.5, -414.16) * mm, "end": v(24.5, -414.16) * mm});
            skLineSegment(sketch, "E18.1.13.4", {"start": v(17.5, -455.33) * mm, "end": v(22.5, -455.33) * mm});
            skLineSegment(sketch, "E18.1.13.5", {"start": v(15.5, -414.16) * mm, "end": v(15.5, -453.33) * mm});
            skArc(sketch, "E18.1.13.6", {"start": v(22.5, -455.33) * mm, "mid": v(23.91, -454.75) * mm, "end": v(24.5, -453.33) * mm});
            skArc(sketch, "E18.1.13.7", {"start": v(15.5, -453.33) * mm, "mid": v(16.09, -454.75) * mm, "end": v(17.5, -455.33) * mm});
            skPoint(sketch, "E18.1.14.0", {"position": v(15.5, -489.97) * mm});
            skLineSegment(sketch, "E18.1.14.1", {"start": v(24.5, -448.8) * mm, "end": v(24.5, -487.97) * mm});
            skPoint(sketch, "E18.1.14.2", {"position": v(24.5, -489.97) * mm});
            skLineSegment(sketch, "E18.1.14.3", {"start": v(15.5, -448.8) * mm, "end": v(24.5, -448.8) * mm});
            skLineSegment(sketch, "E18.1.14.4", {"start": v(17.5, -489.97) * mm, "end": v(22.5, -489.97) * mm});
            skLineSegment(sketch, "E18.1.14.5", {"start": v(15.5, -448.8) * mm, "end": v(15.5, -487.97) * mm});
            skArc(sketch, "E18.1.14.6", {"start": v(22.5, -489.97) * mm, "mid": v(23.91, -489.39) * mm, "end": v(24.5, -487.97) * mm});
            skArc(sketch, "E18.1.14.7", {"start": v(15.5, -487.97) * mm, "mid": v(16.09, -489.39) * mm, "end": v(17.5, -489.97) * mm});
            skPoint(sketch, "E18.2.0.0", {"position": v(35.5, -5) * mm});
            skLineSegment(sketch, "E18.2.0.1", {"start": v(44.5, 36.17) * mm, "end": v(44.5, -3) * mm});
            skPoint(sketch, "E18.2.0.2", {"position": v(44.5, -5) * mm});
            skLineSegment(sketch, "E18.2.0.3", {"start": v(35.5, 36.17) * mm, "end": v(44.5, 36.17) * mm});
            skLineSegment(sketch, "E18.2.0.4", {"start": v(37.5, -5) * mm, "end": v(42.5, -5) * mm});
            skLineSegment(sketch, "E18.2.0.5", {"start": v(35.5, 36.17) * mm, "end": v(35.5, -3) * mm});
            skArc(sketch, "E18.2.0.6", {"start": v(42.5, -5) * mm, "mid": v(43.91, -4.41) * mm, "end": v(44.5, -3) * mm});
            skArc(sketch, "E18.2.0.7", {"start": v(35.5, -3) * mm, "mid": v(36.09, -4.41) * mm, "end": v(37.5, -5) * mm});
            skPoint(sketch, "E18.2.1.0", {"position": v(35.5, -39.64) * mm});
            skLineSegment(sketch, "E18.2.1.1", {"start": v(44.5, 1.53) * mm, "end": v(44.5, -37.64) * mm});
            skPoint(sketch, "E18.2.1.2", {"position": v(44.5, -39.64) * mm});
            skLineSegment(sketch, "E18.2.1.3", {"start": v(35.5, 1.53) * mm, "end": v(44.5, 1.53) * mm});
            skLineSegment(sketch, "E18.2.1.4", {"start": v(37.5, -39.64) * mm, "end": v(42.5, -39.64) * mm});
            skLineSegment(sketch, "E18.2.1.5", {"start": v(35.5, 1.53) * mm, "end": v(35.5, -37.64) * mm});
            skArc(sketch, "E18.2.1.6", {"start": v(42.5, -39.64) * mm, "mid": v(43.91, -39.06) * mm, "end": v(44.5, -37.64) * mm});
            skArc(sketch, "E18.2.1.7", {"start": v(35.5, -37.64) * mm, "mid": v(36.09, -39.06) * mm, "end": v(37.5, -39.64) * mm});
            skPoint(sketch, "E18.2.2.0", {"position": v(35.5, -74.28) * mm});
            skLineSegment(sketch, "E18.2.2.1", {"start": v(44.5, -33.1) * mm, "end": v(44.5, -72.28) * mm});
            skPoint(sketch, "E18.2.2.2", {"position": v(44.5, -74.28) * mm});
            skLineSegment(sketch, "E18.2.2.3", {"start": v(35.5, -33.1) * mm, "end": v(44.5, -33.1) * mm});
            skLineSegment(sketch, "E18.2.2.4", {"start": v(37.5, -74.28) * mm, "end": v(42.5, -74.28) * mm});
            skLineSegment(sketch, "E18.2.2.5", {"start": v(35.5, -33.1) * mm, "end": v(35.5, -72.28) * mm});
            skArc(sketch, "E18.2.2.6", {"start": v(42.5, -74.28) * mm, "mid": v(43.91, -73.7) * mm, "end": v(44.5, -72.28) * mm});
            skArc(sketch, "E18.2.2.7", {"start": v(35.5, -72.28) * mm, "mid": v(36.09, -73.7) * mm, "end": v(37.5, -74.28) * mm});
            skPoint(sketch, "E18.2.3.0", {"position": v(35.5, -108.92) * mm});
            skLineSegment(sketch, "E18.2.3.1", {"start": v(44.5, -67.75) * mm, "end": v(44.5, -106.92) * mm});
            skPoint(sketch, "E18.2.3.2", {"position": v(44.5, -108.92) * mm});
            skLineSegment(sketch, "E18.2.3.3", {"start": v(35.5, -67.75) * mm, "end": v(44.5, -67.75) * mm});
            skLineSegment(sketch, "E18.2.3.4", {"start": v(37.5, -108.92) * mm, "end": v(42.5, -108.92) * mm});
            skLineSegment(sketch, "E18.2.3.5", {"start": v(35.5, -67.75) * mm, "end": v(35.5, -106.92) * mm});
            skArc(sketch, "E18.2.3.6", {"start": v(42.5, -108.92) * mm, "mid": v(43.91, -108.34) * mm, "end": v(44.5, -106.92) * mm});
            skArc(sketch, "E18.2.3.7", {"start": v(35.5, -106.92) * mm, "mid": v(36.09, -108.34) * mm, "end": v(37.5, -108.92) * mm});
            skPoint(sketch, "E18.2.4.0", {"position": v(35.5, -143.56) * mm});
            skLineSegment(sketch, "E18.2.4.1", {"start": v(44.5, -102.4) * mm, "end": v(44.5, -141.56) * mm});
            skPoint(sketch, "E18.2.4.2", {"position": v(44.5, -143.56) * mm});
            skLineSegment(sketch, "E18.2.4.3", {"start": v(35.5, -102.4) * mm, "end": v(44.5, -102.4) * mm});
            skLineSegment(sketch, "E18.2.4.4", {"start": v(37.5, -143.56) * mm, "end": v(42.5, -143.56) * mm});
            skLineSegment(sketch, "E18.2.4.5", {"start": v(35.5, -102.4) * mm, "end": v(35.5, -141.56) * mm});
            skArc(sketch, "E18.2.4.6", {"start": v(42.5, -143.56) * mm, "mid": v(43.91, -142.98) * mm, "end": v(44.5, -141.56) * mm});
            skArc(sketch, "E18.2.4.7", {"start": v(35.5, -141.56) * mm, "mid": v(36.09, -142.98) * mm, "end": v(37.5, -143.56) * mm});
            skPoint(sketch, "E18.2.5.0", {"position": v(35.5, -178.2) * mm});
            skLineSegment(sketch, "E18.2.5.1", {"start": v(44.5, -137.03) * mm, "end": v(44.5, -176.2) * mm});
            skPoint(sketch, "E18.2.5.2", {"position": v(44.5, -178.2) * mm});
            skLineSegment(sketch, "E18.2.5.3", {"start": v(35.5, -137.03) * mm, "end": v(44.5, -137.03) * mm});
            skLineSegment(sketch, "E18.2.5.4", {"start": v(37.5, -178.2) * mm, "end": v(42.5, -178.2) * mm});
            skLineSegment(sketch, "E18.2.5.5", {"start": v(35.5, -137.03) * mm, "end": v(35.5, -176.2) * mm});
            skArc(sketch, "E18.2.5.6", {"start": v(42.5, -178.2) * mm, "mid": v(43.91, -177.62) * mm, "end": v(44.5, -176.2) * mm});
            skArc(sketch, "E18.2.5.7", {"start": v(35.5, -176.2) * mm, "mid": v(36.09, -177.62) * mm, "end": v(37.5, -178.2) * mm});
            skPoint(sketch, "E18.2.6.0", {"position": v(35.5, -212.85) * mm});
            skLineSegment(sketch, "E18.2.6.1", {"start": v(44.5, -171.67) * mm, "end": v(44.5, -210.85) * mm});
            skPoint(sketch, "E18.2.6.2", {"position": v(44.5, -212.85) * mm});
            skLineSegment(sketch, "E18.2.6.3", {"start": v(35.5, -171.67) * mm, "end": v(44.5, -171.67) * mm});
            skLineSegment(sketch, "E18.2.6.4", {"start": v(37.5, -212.85) * mm, "end": v(42.5, -212.85) * mm});
            skLineSegment(sketch, "E18.2.6.5", {"start": v(35.5, -171.67) * mm, "end": v(35.5, -210.85) * mm});
            skArc(sketch, "E18.2.6.6", {"start": v(42.5, -212.85) * mm, "mid": v(43.91, -212.26) * mm, "end": v(44.5, -210.85) * mm});
            skArc(sketch, "E18.2.6.7", {"start": v(35.5, -210.85) * mm, "mid": v(36.09, -212.26) * mm, "end": v(37.5, -212.85) * mm});
            skPoint(sketch, "E18.2.7.0", {"position": v(35.5, -247.49) * mm});
            skLineSegment(sketch, "E18.2.7.1", {"start": v(44.5, -206.31) * mm, "end": v(44.5, -245.49) * mm});
            skPoint(sketch, "E18.2.7.2", {"position": v(44.5, -247.49) * mm});
            skLineSegment(sketch, "E18.2.7.3", {"start": v(35.5, -206.31) * mm, "end": v(44.5, -206.31) * mm});
            skLineSegment(sketch, "E18.2.7.4", {"start": v(37.5, -247.49) * mm, "end": v(42.5, -247.49) * mm});
            skLineSegment(sketch, "E18.2.7.5", {"start": v(35.5, -206.31) * mm, "end": v(35.5, -245.49) * mm});
            skArc(sketch, "E18.2.7.6", {"start": v(42.5, -247.49) * mm, "mid": v(43.91, -246.9) * mm, "end": v(44.5, -245.49) * mm});
            skArc(sketch, "E18.2.7.7", {"start": v(35.5, -245.49) * mm, "mid": v(36.09, -246.9) * mm, "end": v(37.5, -247.49) * mm});
            skPoint(sketch, "E18.2.8.0", {"position": v(35.5, -282.13) * mm});
            skLineSegment(sketch, "E18.2.8.1", {"start": v(44.5, -240.95) * mm, "end": v(44.5, -280.13) * mm});
            skPoint(sketch, "E18.2.8.2", {"position": v(44.5, -282.13) * mm});
            skLineSegment(sketch, "E18.2.8.3", {"start": v(35.5, -240.95) * mm, "end": v(44.5, -240.95) * mm});
            skLineSegment(sketch, "E18.2.8.4", {"start": v(37.5, -282.13) * mm, "end": v(42.5, -282.13) * mm});
            skLineSegment(sketch, "E18.2.8.5", {"start": v(35.5, -240.95) * mm, "end": v(35.5, -280.13) * mm});
            skArc(sketch, "E18.2.8.6", {"start": v(42.5, -282.13) * mm, "mid": v(43.91, -281.54) * mm, "end": v(44.5, -280.13) * mm});
            skArc(sketch, "E18.2.8.7", {"start": v(35.5, -280.13) * mm, "mid": v(36.09, -281.54) * mm, "end": v(37.5, -282.13) * mm});
            skPoint(sketch, "E18.2.9.0", {"position": v(35.5, -316.77) * mm});
            skLineSegment(sketch, "E18.2.9.1", {"start": v(44.5, -275.6) * mm, "end": v(44.5, -314.77) * mm});
            skPoint(sketch, "E18.2.9.2", {"position": v(44.5, -316.77) * mm});
            skLineSegment(sketch, "E18.2.9.3", {"start": v(35.5, -275.6) * mm, "end": v(44.5, -275.6) * mm});
            skLineSegment(sketch, "E18.2.9.4", {"start": v(37.5, -316.77) * mm, "end": v(42.5, -316.77) * mm});
            skLineSegment(sketch, "E18.2.9.5", {"start": v(35.5, -275.6) * mm, "end": v(35.5, -314.77) * mm});
            skArc(sketch, "E18.2.9.6", {"start": v(42.5, -316.77) * mm, "mid": v(43.91, -316.18) * mm, "end": v(44.5, -314.77) * mm});
            skArc(sketch, "E18.2.9.7", {"start": v(35.5, -314.77) * mm, "mid": v(36.09, -316.18) * mm, "end": v(37.5, -316.77) * mm});
            skPoint(sketch, "E18.2.10.0", {"position": v(35.5, -351.41) * mm});
            skLineSegment(sketch, "E18.2.10.1", {"start": v(44.5, -310.24) * mm, "end": v(44.5, -349.41) * mm});
            skPoint(sketch, "E18.2.10.2", {"position": v(44.5, -351.41) * mm});
            skLineSegment(sketch, "E18.2.10.3", {"start": v(35.5, -310.24) * mm, "end": v(44.5, -310.24) * mm});
            skLineSegment(sketch, "E18.2.10.4", {"start": v(37.5, -351.41) * mm, "end": v(42.5, -351.41) * mm});
            skLineSegment(sketch, "E18.2.10.5", {"start": v(35.5, -310.24) * mm, "end": v(35.5, -349.41) * mm});
            skArc(sketch, "E18.2.10.6", {"start": v(42.5, -351.41) * mm, "mid": v(43.91, -350.82) * mm, "end": v(44.5, -349.41) * mm});
            skArc(sketch, "E18.2.10.7", {"start": v(35.5, -349.41) * mm, "mid": v(36.09, -350.82) * mm, "end": v(37.5, -351.41) * mm});
            skPoint(sketch, "E18.2.11.0", {"position": v(35.5, -386.05) * mm});
            skLineSegment(sketch, "E18.2.11.1", {"start": v(44.5, -344.88) * mm, "end": v(44.5, -384.05) * mm});
            skPoint(sketch, "E18.2.11.2", {"position": v(44.5, -386.05) * mm});
            skLineSegment(sketch, "E18.2.11.3", {"start": v(35.5, -344.88) * mm, "end": v(44.5, -344.88) * mm});
            skLineSegment(sketch, "E18.2.11.4", {"start": v(37.5, -386.05) * mm, "end": v(42.5, -386.05) * mm});
            skLineSegment(sketch, "E18.2.11.5", {"start": v(35.5, -344.88) * mm, "end": v(35.5, -384.05) * mm});
            skArc(sketch, "E18.2.11.6", {"start": v(42.5, -386.05) * mm, "mid": v(43.91, -385.47) * mm, "end": v(44.5, -384.05) * mm});
            skArc(sketch, "E18.2.11.7", {"start": v(35.5, -384.05) * mm, "mid": v(36.09, -385.47) * mm, "end": v(37.5, -386.05) * mm});
            skPoint(sketch, "E18.2.12.0", {"position": v(35.5, -420.7) * mm});
            skLineSegment(sketch, "E18.2.12.1", {"start": v(44.5, -379.52) * mm, "end": v(44.5, -418.7) * mm});
            skPoint(sketch, "E18.2.12.2", {"position": v(44.5, -420.7) * mm});
            skLineSegment(sketch, "E18.2.12.3", {"start": v(35.5, -379.52) * mm, "end": v(44.5, -379.52) * mm});
            skLineSegment(sketch, "E18.2.12.4", {"start": v(37.5, -420.7) * mm, "end": v(42.5, -420.7) * mm});
            skLineSegment(sketch, "E18.2.12.5", {"start": v(35.5, -379.52) * mm, "end": v(35.5, -418.7) * mm});
            skArc(sketch, "E18.2.12.6", {"start": v(42.5, -420.7) * mm, "mid": v(43.91, -420.1) * mm, "end": v(44.5, -418.7) * mm});
            skArc(sketch, "E18.2.12.7", {"start": v(35.5, -418.7) * mm, "mid": v(36.09, -420.1) * mm, "end": v(37.5, -420.7) * mm});
            skPoint(sketch, "E18.2.13.0", {"position": v(35.5, -455.33) * mm});
            skLineSegment(sketch, "E18.2.13.1", {"start": v(44.5, -414.16) * mm, "end": v(44.5, -453.33) * mm});
            skPoint(sketch, "E18.2.13.2", {"position": v(44.5, -455.33) * mm});
            skLineSegment(sketch, "E18.2.13.3", {"start": v(35.5, -414.16) * mm, "end": v(44.5, -414.16) * mm});
            skLineSegment(sketch, "E18.2.13.4", {"start": v(37.5, -455.33) * mm, "end": v(42.5, -455.33) * mm});
            skLineSegment(sketch, "E18.2.13.5", {"start": v(35.5, -414.16) * mm, "end": v(35.5, -453.33) * mm});
            skArc(sketch, "E18.2.13.6", {"start": v(42.5, -455.33) * mm, "mid": v(43.91, -454.75) * mm, "end": v(44.5, -453.33) * mm});
            skArc(sketch, "E18.2.13.7", {"start": v(35.5, -453.33) * mm, "mid": v(36.09, -454.75) * mm, "end": v(37.5, -455.33) * mm});
            skPoint(sketch, "E18.2.14.0", {"position": v(35.5, -489.97) * mm});
            skLineSegment(sketch, "E18.2.14.1", {"start": v(44.5, -448.8) * mm, "end": v(44.5, -487.97) * mm});
            skPoint(sketch, "E18.2.14.2", {"position": v(44.5, -489.97) * mm});
            skLineSegment(sketch, "E18.2.14.3", {"start": v(35.5, -448.8) * mm, "end": v(44.5, -448.8) * mm});
            skLineSegment(sketch, "E18.2.14.4", {"start": v(37.5, -489.97) * mm, "end": v(42.5, -489.97) * mm});
            skLineSegment(sketch, "E18.2.14.5", {"start": v(35.5, -448.8) * mm, "end": v(35.5, -487.97) * mm});
            skArc(sketch, "E18.2.14.6", {"start": v(42.5, -489.97) * mm, "mid": v(43.91, -489.39) * mm, "end": v(44.5, -487.97) * mm});
            skArc(sketch, "E18.2.14.7", {"start": v(35.5, -487.97) * mm, "mid": v(36.09, -489.39) * mm, "end": v(37.5, -489.97) * mm});
            skLineSegment(sketch, "E18.direction1", {"start": v(-4.5, -5) * mm, "end": v(15.5, -5) * mm, "construction": true});
            skLineSegment(sketch, "E18.direction2", {"start": v(-4.5, -5) * mm, "end": v(-4.5, -39.64) * mm, "construction": true});
            skPoint(sketch, "E19.0.3.0", {"position": v(55.5, -5) * mm});
            skLineSegment(sketch, "E19.1.3.0", {"start": v(64.5, 36.17) * mm, "end": v(64.5, -3) * mm});
            skPoint(sketch, "E19.4.3.0", {"position": v(64.5, -5) * mm});
            skLineSegment(sketch, "E19.5.3.0", {"start": v(55.5, 36.17) * mm, "end": v(64.5, 36.17) * mm});
            skLineSegment(sketch, "E19.8.3.0", {"start": v(57.5, -5) * mm, "end": v(62.5, -5) * mm});
            skLineSegment(sketch, "E19.11.3.0", {"start": v(55.5, 36.17) * mm, "end": v(55.5, -3) * mm});
            skArc(sketch, "E19.14.3.0", {"start": v(62.5, -5) * mm, "mid": v(63.91, -4.41) * mm, "end": v(64.5, -3) * mm});
            skArc(sketch, "E19.18.3.0", {"start": v(55.5, -3) * mm, "mid": v(56.09, -4.41) * mm, "end": v(57.5, -5) * mm});
            skPoint(sketch, "E19.0.3.1", {"position": v(55.5, -39.64) * mm});
            skLineSegment(sketch, "E19.1.3.1", {"start": v(64.5, 1.53) * mm, "end": v(64.5, -37.64) * mm});
            skPoint(sketch, "E19.4.3.1", {"position": v(64.5, -39.64) * mm});
            skLineSegment(sketch, "E19.5.3.1", {"start": v(55.5, 1.53) * mm, "end": v(64.5, 1.53) * mm});
            skLineSegment(sketch, "E19.8.3.1", {"start": v(57.5, -39.64) * mm, "end": v(62.5, -39.64) * mm});
            skLineSegment(sketch, "E19.11.3.1", {"start": v(55.5, 1.53) * mm, "end": v(55.5, -37.64) * mm});
            skArc(sketch, "E19.14.3.1", {"start": v(62.5, -39.64) * mm, "mid": v(63.91, -39.06) * mm, "end": v(64.5, -37.64) * mm});
            skArc(sketch, "E19.18.3.1", {"start": v(55.5, -37.64) * mm, "mid": v(56.09, -39.06) * mm, "end": v(57.5, -39.64) * mm});
            skPoint(sketch, "E19.0.3.2", {"position": v(55.5, -74.28) * mm});
            skLineSegment(sketch, "E19.1.3.2", {"start": v(64.5, -33.1) * mm, "end": v(64.5, -72.28) * mm});
            skPoint(sketch, "E19.4.3.2", {"position": v(64.5, -74.28) * mm});
            skLineSegment(sketch, "E19.5.3.2", {"start": v(55.5, -33.1) * mm, "end": v(64.5, -33.1) * mm});
            skLineSegment(sketch, "E19.8.3.2", {"start": v(57.5, -74.28) * mm, "end": v(62.5, -74.28) * mm});
            skLineSegment(sketch, "E19.11.3.2", {"start": v(55.5, -33.1) * mm, "end": v(55.5, -72.28) * mm});
            skArc(sketch, "E19.14.3.2", {"start": v(62.5, -74.28) * mm, "mid": v(63.91, -73.7) * mm, "end": v(64.5, -72.28) * mm});
            skArc(sketch, "E19.18.3.2", {"start": v(55.5, -72.28) * mm, "mid": v(56.09, -73.7) * mm, "end": v(57.5, -74.28) * mm});
            skPoint(sketch, "E19.0.3.3", {"position": v(55.5, -108.92) * mm});
            skLineSegment(sketch, "E19.1.3.3", {"start": v(64.5, -67.75) * mm, "end": v(64.5, -106.92) * mm});
            skPoint(sketch, "E19.4.3.3", {"position": v(64.5, -108.92) * mm});
            skLineSegment(sketch, "E19.5.3.3", {"start": v(55.5, -67.75) * mm, "end": v(64.5, -67.75) * mm});
            skLineSegment(sketch, "E19.8.3.3", {"start": v(57.5, -108.92) * mm, "end": v(62.5, -108.92) * mm});
            skLineSegment(sketch, "E19.11.3.3", {"start": v(55.5, -67.75) * mm, "end": v(55.5, -106.92) * mm});
            skArc(sketch, "E19.14.3.3", {"start": v(62.5, -108.92) * mm, "mid": v(63.91, -108.34) * mm, "end": v(64.5, -106.92) * mm});
            skArc(sketch, "E19.18.3.3", {"start": v(55.5, -106.92) * mm, "mid": v(56.09, -108.34) * mm, "end": v(57.5, -108.92) * mm});
            skPoint(sketch, "E19.0.3.4", {"position": v(55.5, -143.56) * mm});
            skLineSegment(sketch, "E19.1.3.4", {"start": v(64.5, -102.4) * mm, "end": v(64.5, -141.56) * mm});
            skPoint(sketch, "E19.4.3.4", {"position": v(64.5, -143.56) * mm});
            skLineSegment(sketch, "E19.5.3.4", {"start": v(55.5, -102.4) * mm, "end": v(64.5, -102.4) * mm});
            skLineSegment(sketch, "E19.8.3.4", {"start": v(57.5, -143.56) * mm, "end": v(62.5, -143.56) * mm});
            skLineSegment(sketch, "E19.11.3.4", {"start": v(55.5, -102.4) * mm, "end": v(55.5, -141.56) * mm});
            skArc(sketch, "E19.14.3.4", {"start": v(62.5, -143.56) * mm, "mid": v(63.91, -142.98) * mm, "end": v(64.5, -141.56) * mm});
            skArc(sketch, "E19.18.3.4", {"start": v(55.5, -141.56) * mm, "mid": v(56.09, -142.98) * mm, "end": v(57.5, -143.56) * mm});
            skPoint(sketch, "E19.0.3.5", {"position": v(55.5, -178.2) * mm});
            skLineSegment(sketch, "E19.1.3.5", {"start": v(64.5, -137.03) * mm, "end": v(64.5, -176.2) * mm});
            skPoint(sketch, "E19.4.3.5", {"position": v(64.5, -178.2) * mm});
            skLineSegment(sketch, "E19.5.3.5", {"start": v(55.5, -137.03) * mm, "end": v(64.5, -137.03) * mm});
            skLineSegment(sketch, "E19.8.3.5", {"start": v(57.5, -178.2) * mm, "end": v(62.5, -178.2) * mm});
            skLineSegment(sketch, "E19.11.3.5", {"start": v(55.5, -137.03) * mm, "end": v(55.5, -176.2) * mm});
            skArc(sketch, "E19.14.3.5", {"start": v(62.5, -178.2) * mm, "mid": v(63.91, -177.62) * mm, "end": v(64.5, -176.2) * mm});
            skArc(sketch, "E19.18.3.5", {"start": v(55.5, -176.2) * mm, "mid": v(56.09, -177.62) * mm, "end": v(57.5, -178.2) * mm});
            skPoint(sketch, "E19.0.3.6", {"position": v(55.5, -212.85) * mm});
            skLineSegment(sketch, "E19.1.3.6", {"start": v(64.5, -171.67) * mm, "end": v(64.5, -210.85) * mm});
            skPoint(sketch, "E19.4.3.6", {"position": v(64.5, -212.85) * mm});
            skLineSegment(sketch, "E19.5.3.6", {"start": v(55.5, -171.67) * mm, "end": v(64.5, -171.67) * mm});
            skLineSegment(sketch, "E19.8.3.6", {"start": v(57.5, -212.85) * mm, "end": v(62.5, -212.85) * mm});
            skLineSegment(sketch, "E19.11.3.6", {"start": v(55.5, -171.67) * mm, "end": v(55.5, -210.85) * mm});
            skArc(sketch, "E19.14.3.6", {"start": v(62.5, -212.85) * mm, "mid": v(63.91, -212.26) * mm, "end": v(64.5, -210.85) * mm});
            skArc(sketch, "E19.18.3.6", {"start": v(55.5, -210.85) * mm, "mid": v(56.09, -212.26) * mm, "end": v(57.5, -212.85) * mm});
            skPoint(sketch, "E19.0.3.7", {"position": v(55.5, -247.49) * mm});
            skLineSegment(sketch, "E19.1.3.7", {"start": v(64.5, -206.31) * mm, "end": v(64.5, -245.49) * mm});
            skPoint(sketch, "E19.4.3.7", {"position": v(64.5, -247.49) * mm});
            skLineSegment(sketch, "E19.5.3.7", {"start": v(55.5, -206.31) * mm, "end": v(64.5, -206.31) * mm});
            skLineSegment(sketch, "E19.8.3.7", {"start": v(57.5, -247.49) * mm, "end": v(62.5, -247.49) * mm});
            skLineSegment(sketch, "E19.11.3.7", {"start": v(55.5, -206.31) * mm, "end": v(55.5, -245.49) * mm});
            skArc(sketch, "E19.14.3.7", {"start": v(62.5, -247.49) * mm, "mid": v(63.91, -246.9) * mm, "end": v(64.5, -245.49) * mm});
            skArc(sketch, "E19.18.3.7", {"start": v(55.5, -245.49) * mm, "mid": v(56.09, -246.9) * mm, "end": v(57.5, -247.49) * mm});
            skPoint(sketch, "E19.0.3.8", {"position": v(55.5, -282.13) * mm});
            skLineSegment(sketch, "E19.1.3.8", {"start": v(64.5, -240.95) * mm, "end": v(64.5, -280.13) * mm});
            skPoint(sketch, "E19.4.3.8", {"position": v(64.5, -282.13) * mm});
            skLineSegment(sketch, "E19.5.3.8", {"start": v(55.5, -240.95) * mm, "end": v(64.5, -240.95) * mm});
            skLineSegment(sketch, "E19.8.3.8", {"start": v(57.5, -282.13) * mm, "end": v(62.5, -282.13) * mm});
            skLineSegment(sketch, "E19.11.3.8", {"start": v(55.5, -240.95) * mm, "end": v(55.5, -280.13) * mm});
            skArc(sketch, "E19.14.3.8", {"start": v(62.5, -282.13) * mm, "mid": v(63.91, -281.54) * mm, "end": v(64.5, -280.13) * mm});
            skArc(sketch, "E19.18.3.8", {"start": v(55.5, -280.13) * mm, "mid": v(56.09, -281.54) * mm, "end": v(57.5, -282.13) * mm});
            skPoint(sketch, "E19.0.3.9", {"position": v(55.5, -316.77) * mm});
            skLineSegment(sketch, "E19.1.3.9", {"start": v(64.5, -275.6) * mm, "end": v(64.5, -314.77) * mm});
            skPoint(sketch, "E19.4.3.9", {"position": v(64.5, -316.77) * mm});
            skLineSegment(sketch, "E19.5.3.9", {"start": v(55.5, -275.6) * mm, "end": v(64.5, -275.6) * mm});
            skLineSegment(sketch, "E19.8.3.9", {"start": v(57.5, -316.77) * mm, "end": v(62.5, -316.77) * mm});
            skLineSegment(sketch, "E19.11.3.9", {"start": v(55.5, -275.6) * mm, "end": v(55.5, -314.77) * mm});
            skArc(sketch, "E19.14.3.9", {"start": v(62.5, -316.77) * mm, "mid": v(63.91, -316.18) * mm, "end": v(64.5, -314.77) * mm});
            skArc(sketch, "E19.18.3.9", {"start": v(55.5, -314.77) * mm, "mid": v(56.09, -316.18) * mm, "end": v(57.5, -316.77) * mm});
            skPoint(sketch, "E19.0.3.10", {"position": v(55.5, -351.41) * mm});
            skLineSegment(sketch, "E19.1.3.10", {"start": v(64.5, -310.24) * mm, "end": v(64.5, -349.41) * mm});
            skPoint(sketch, "E19.4.3.10", {"position": v(64.5, -351.41) * mm});
            skLineSegment(sketch, "E19.5.3.10", {"start": v(55.5, -310.24) * mm, "end": v(64.5, -310.24) * mm});
            skLineSegment(sketch, "E19.8.3.10", {"start": v(57.5, -351.41) * mm, "end": v(62.5, -351.41) * mm});
            skLineSegment(sketch, "E19.11.3.10", {"start": v(55.5, -310.24) * mm, "end": v(55.5, -349.41) * mm});
            skArc(sketch, "E19.14.3.10", {"start": v(62.5, -351.41) * mm, "mid": v(63.91, -350.82) * mm, "end": v(64.5, -349.41) * mm});
            skArc(sketch, "E19.18.3.10", {"start": v(55.5, -349.41) * mm, "mid": v(56.09, -350.82) * mm, "end": v(57.5, -351.41) * mm});
            skPoint(sketch, "E19.0.3.11", {"position": v(55.5, -386.05) * mm});
            skLineSegment(sketch, "E19.1.3.11", {"start": v(64.5, -344.88) * mm, "end": v(64.5, -384.05) * mm});
            skPoint(sketch, "E19.4.3.11", {"position": v(64.5, -386.05) * mm});
            skLineSegment(sketch, "E19.5.3.11", {"start": v(55.5, -344.88) * mm, "end": v(64.5, -344.88) * mm});
            skLineSegment(sketch, "E19.8.3.11", {"start": v(57.5, -386.05) * mm, "end": v(62.5, -386.05) * mm});
            skLineSegment(sketch, "E19.11.3.11", {"start": v(55.5, -344.88) * mm, "end": v(55.5, -384.05) * mm});
            skArc(sketch, "E19.14.3.11", {"start": v(62.5, -386.05) * mm, "mid": v(63.91, -385.47) * mm, "end": v(64.5, -384.05) * mm});
            skArc(sketch, "E19.18.3.11", {"start": v(55.5, -384.05) * mm, "mid": v(56.09, -385.47) * mm, "end": v(57.5, -386.05) * mm});
            skPoint(sketch, "E19.0.3.12", {"position": v(55.5, -420.7) * mm});
            skLineSegment(sketch, "E19.1.3.12", {"start": v(64.5, -379.52) * mm, "end": v(64.5, -418.7) * mm});
            skPoint(sketch, "E19.4.3.12", {"position": v(64.5, -420.7) * mm});
            skLineSegment(sketch, "E19.5.3.12", {"start": v(55.5, -379.52) * mm, "end": v(64.5, -379.52) * mm});
            skLineSegment(sketch, "E19.8.3.12", {"start": v(57.5, -420.7) * mm, "end": v(62.5, -420.7) * mm});
            skLineSegment(sketch, "E19.11.3.12", {"start": v(55.5, -379.52) * mm, "end": v(55.5, -418.7) * mm});
            skArc(sketch, "E19.14.3.12", {"start": v(62.5, -420.7) * mm, "mid": v(63.91, -420.1) * mm, "end": v(64.5, -418.7) * mm});
            skArc(sketch, "E19.18.3.12", {"start": v(55.5, -418.7) * mm, "mid": v(56.09, -420.1) * mm, "end": v(57.5, -420.7) * mm});
            skPoint(sketch, "E19.0.3.13", {"position": v(55.5, -455.33) * mm});
            skLineSegment(sketch, "E19.1.3.13", {"start": v(64.5, -414.16) * mm, "end": v(64.5, -453.33) * mm});
            skPoint(sketch, "E19.4.3.13", {"position": v(64.5, -455.33) * mm});
            skLineSegment(sketch, "E19.5.3.13", {"start": v(55.5, -414.16) * mm, "end": v(64.5, -414.16) * mm});
            skLineSegment(sketch, "E19.8.3.13", {"start": v(57.5, -455.33) * mm, "end": v(62.5, -455.33) * mm});
            skLineSegment(sketch, "E19.11.3.13", {"start": v(55.5, -414.16) * mm, "end": v(55.5, -453.33) * mm});
            skArc(sketch, "E19.14.3.13", {"start": v(62.5, -455.33) * mm, "mid": v(63.91, -454.75) * mm, "end": v(64.5, -453.33) * mm});
            skArc(sketch, "E19.18.3.13", {"start": v(55.5, -453.33) * mm, "mid": v(56.09, -454.75) * mm, "end": v(57.5, -455.33) * mm});
            skPoint(sketch, "E19.0.3.14", {"position": v(55.5, -489.97) * mm});
            skLineSegment(sketch, "E19.1.3.14", {"start": v(64.5, -448.8) * mm, "end": v(64.5, -487.97) * mm});
            skPoint(sketch, "E19.4.3.14", {"position": v(64.5, -489.97) * mm});
            skLineSegment(sketch, "E19.5.3.14", {"start": v(55.5, -448.8) * mm, "end": v(64.5, -448.8) * mm});
            skLineSegment(sketch, "E19.8.3.14", {"start": v(57.5, -489.97) * mm, "end": v(62.5, -489.97) * mm});
            skLineSegment(sketch, "E19.11.3.14", {"start": v(55.5, -448.8) * mm, "end": v(55.5, -487.97) * mm});
            skArc(sketch, "E19.14.3.14", {"start": v(62.5, -489.97) * mm, "mid": v(63.91, -489.39) * mm, "end": v(64.5, -487.97) * mm});
            skArc(sketch, "E19.18.3.14", {"start": v(55.5, -487.97) * mm, "mid": v(56.09, -489.39) * mm, "end": v(57.5, -489.97) * mm});
            skPoint(sketch, "E19.0.4.0", {"position": v(75.5, -5) * mm});
            skLineSegment(sketch, "E19.1.4.0", {"start": v(84.5, 36.17) * mm, "end": v(84.5, -3) * mm});
            skPoint(sketch, "E19.4.4.0", {"position": v(84.5, -5) * mm});
            skLineSegment(sketch, "E19.5.4.0", {"start": v(75.5, 36.17) * mm, "end": v(84.5, 36.17) * mm});
            skLineSegment(sketch, "E19.8.4.0", {"start": v(77.5, -5) * mm, "end": v(82.5, -5) * mm});
            skLineSegment(sketch, "E19.11.4.0", {"start": v(75.5, 36.17) * mm, "end": v(75.5, -3) * mm});
            skArc(sketch, "E19.14.4.0", {"start": v(82.5, -5) * mm, "mid": v(83.91, -4.41) * mm, "end": v(84.5, -3) * mm});
            skArc(sketch, "E19.18.4.0", {"start": v(75.5, -3) * mm, "mid": v(76.09, -4.41) * mm, "end": v(77.5, -5) * mm});
            skPoint(sketch, "E19.0.4.1", {"position": v(75.5, -39.64) * mm});
            skLineSegment(sketch, "E19.1.4.1", {"start": v(84.5, 1.53) * mm, "end": v(84.5, -37.64) * mm});
            skPoint(sketch, "E19.4.4.1", {"position": v(84.5, -39.64) * mm});
            skLineSegment(sketch, "E19.5.4.1", {"start": v(75.5, 1.53) * mm, "end": v(84.5, 1.53) * mm});
            skLineSegment(sketch, "E19.8.4.1", {"start": v(77.5, -39.64) * mm, "end": v(82.5, -39.64) * mm});
            skLineSegment(sketch, "E19.11.4.1", {"start": v(75.5, 1.53) * mm, "end": v(75.5, -37.64) * mm});
            skArc(sketch, "E19.14.4.1", {"start": v(82.5, -39.64) * mm, "mid": v(83.91, -39.06) * mm, "end": v(84.5, -37.64) * mm});
            skArc(sketch, "E19.18.4.1", {"start": v(75.5, -37.64) * mm, "mid": v(76.09, -39.06) * mm, "end": v(77.5, -39.64) * mm});
            skPoint(sketch, "E19.0.4.2", {"position": v(75.5, -74.28) * mm});
            skLineSegment(sketch, "E19.1.4.2", {"start": v(84.5, -33.1) * mm, "end": v(84.5, -72.28) * mm});
            skPoint(sketch, "E19.4.4.2", {"position": v(84.5, -74.28) * mm});
            skLineSegment(sketch, "E19.5.4.2", {"start": v(75.5, -33.1) * mm, "end": v(84.5, -33.1) * mm});
            skLineSegment(sketch, "E19.8.4.2", {"start": v(77.5, -74.28) * mm, "end": v(82.5, -74.28) * mm});
            skLineSegment(sketch, "E19.11.4.2", {"start": v(75.5, -33.1) * mm, "end": v(75.5, -72.28) * mm});
            skArc(sketch, "E19.14.4.2", {"start": v(82.5, -74.28) * mm, "mid": v(83.91, -73.7) * mm, "end": v(84.5, -72.28) * mm});
            skArc(sketch, "E19.18.4.2", {"start": v(75.5, -72.28) * mm, "mid": v(76.09, -73.7) * mm, "end": v(77.5, -74.28) * mm});
            skPoint(sketch, "E19.0.4.3", {"position": v(75.5, -108.92) * mm});
            skLineSegment(sketch, "E19.1.4.3", {"start": v(84.5, -67.75) * mm, "end": v(84.5, -106.92) * mm});
            skPoint(sketch, "E19.4.4.3", {"position": v(84.5, -108.92) * mm});
            skLineSegment(sketch, "E19.5.4.3", {"start": v(75.5, -67.75) * mm, "end": v(84.5, -67.75) * mm});
            skLineSegment(sketch, "E19.8.4.3", {"start": v(77.5, -108.92) * mm, "end": v(82.5, -108.92) * mm});
            skLineSegment(sketch, "E19.11.4.3", {"start": v(75.5, -67.75) * mm, "end": v(75.5, -106.92) * mm});
            skArc(sketch, "E19.14.4.3", {"start": v(82.5, -108.92) * mm, "mid": v(83.91, -108.34) * mm, "end": v(84.5, -106.92) * mm});
            skArc(sketch, "E19.18.4.3", {"start": v(75.5, -106.92) * mm, "mid": v(76.09, -108.34) * mm, "end": v(77.5, -108.92) * mm});
            skPoint(sketch, "E19.0.4.4", {"position": v(75.5, -143.56) * mm});
            skLineSegment(sketch, "E19.1.4.4", {"start": v(84.5, -102.4) * mm, "end": v(84.5, -141.56) * mm});
            skPoint(sketch, "E19.4.4.4", {"position": v(84.5, -143.56) * mm});
            skLineSegment(sketch, "E19.5.4.4", {"start": v(75.5, -102.4) * mm, "end": v(84.5, -102.4) * mm});
            skLineSegment(sketch, "E19.8.4.4", {"start": v(77.5, -143.56) * mm, "end": v(82.5, -143.56) * mm});
            skLineSegment(sketch, "E19.11.4.4", {"start": v(75.5, -102.4) * mm, "end": v(75.5, -141.56) * mm});
            skArc(sketch, "E19.14.4.4", {"start": v(82.5, -143.56) * mm, "mid": v(83.91, -142.98) * mm, "end": v(84.5, -141.56) * mm});
            skArc(sketch, "E19.18.4.4", {"start": v(75.5, -141.56) * mm, "mid": v(76.09, -142.98) * mm, "end": v(77.5, -143.56) * mm});
            skPoint(sketch, "E19.0.4.5", {"position": v(75.5, -178.2) * mm});
            skLineSegment(sketch, "E19.1.4.5", {"start": v(84.5, -137.03) * mm, "end": v(84.5, -176.2) * mm});
            skPoint(sketch, "E19.4.4.5", {"position": v(84.5, -178.2) * mm});
            skLineSegment(sketch, "E19.5.4.5", {"start": v(75.5, -137.03) * mm, "end": v(84.5, -137.03) * mm});
            skLineSegment(sketch, "E19.8.4.5", {"start": v(77.5, -178.2) * mm, "end": v(82.5, -178.2) * mm});
            skLineSegment(sketch, "E19.11.4.5", {"start": v(75.5, -137.03) * mm, "end": v(75.5, -176.2) * mm});
            skArc(sketch, "E19.14.4.5", {"start": v(82.5, -178.2) * mm, "mid": v(83.91, -177.62) * mm, "end": v(84.5, -176.2) * mm});
            skArc(sketch, "E19.18.4.5", {"start": v(75.5, -176.2) * mm, "mid": v(76.09, -177.62) * mm, "end": v(77.5, -178.2) * mm});
            skPoint(sketch, "E19.0.4.6", {"position": v(75.5, -212.85) * mm});
            skLineSegment(sketch, "E19.1.4.6", {"start": v(84.5, -171.67) * mm, "end": v(84.5, -210.85) * mm});
            skPoint(sketch, "E19.4.4.6", {"position": v(84.5, -212.85) * mm});
            skLineSegment(sketch, "E19.5.4.6", {"start": v(75.5, -171.67) * mm, "end": v(84.5, -171.67) * mm});
            skLineSegment(sketch, "E19.8.4.6", {"start": v(77.5, -212.85) * mm, "end": v(82.5, -212.85) * mm});
            skLineSegment(sketch, "E19.11.4.6", {"start": v(75.5, -171.67) * mm, "end": v(75.5, -210.85) * mm});
            skArc(sketch, "E19.14.4.6", {"start": v(82.5, -212.85) * mm, "mid": v(83.91, -212.26) * mm, "end": v(84.5, -210.85) * mm});
            skArc(sketch, "E19.18.4.6", {"start": v(75.5, -210.85) * mm, "mid": v(76.09, -212.26) * mm, "end": v(77.5, -212.85) * mm});
            skPoint(sketch, "E19.0.4.7", {"position": v(75.5, -247.49) * mm});
            skLineSegment(sketch, "E19.1.4.7", {"start": v(84.5, -206.31) * mm, "end": v(84.5, -245.49) * mm});
            skPoint(sketch, "E19.4.4.7", {"position": v(84.5, -247.49) * mm});
            skLineSegment(sketch, "E19.5.4.7", {"start": v(75.5, -206.31) * mm, "end": v(84.5, -206.31) * mm});
            skLineSegment(sketch, "E19.8.4.7", {"start": v(77.5, -247.49) * mm, "end": v(82.5, -247.49) * mm});
            skLineSegment(sketch, "E19.11.4.7", {"start": v(75.5, -206.31) * mm, "end": v(75.5, -245.49) * mm});
            skArc(sketch, "E19.14.4.7", {"start": v(82.5, -247.49) * mm, "mid": v(83.91, -246.9) * mm, "end": v(84.5, -245.49) * mm});
            skArc(sketch, "E19.18.4.7", {"start": v(75.5, -245.49) * mm, "mid": v(76.09, -246.9) * mm, "end": v(77.5, -247.49) * mm});
            skPoint(sketch, "E19.0.4.8", {"position": v(75.5, -282.13) * mm});
            skLineSegment(sketch, "E19.1.4.8", {"start": v(84.5, -240.95) * mm, "end": v(84.5, -280.13) * mm});
            skPoint(sketch, "E19.4.4.8", {"position": v(84.5, -282.13) * mm});
            skLineSegment(sketch, "E19.5.4.8", {"start": v(75.5, -240.95) * mm, "end": v(84.5, -240.95) * mm});
            skLineSegment(sketch, "E19.8.4.8", {"start": v(77.5, -282.13) * mm, "end": v(82.5, -282.13) * mm});
            skLineSegment(sketch, "E19.11.4.8", {"start": v(75.5, -240.95) * mm, "end": v(75.5, -280.13) * mm});
            skArc(sketch, "E19.14.4.8", {"start": v(82.5, -282.13) * mm, "mid": v(83.91, -281.54) * mm, "end": v(84.5, -280.13) * mm});
            skArc(sketch, "E19.18.4.8", {"start": v(75.5, -280.13) * mm, "mid": v(76.09, -281.54) * mm, "end": v(77.5, -282.13) * mm});
            skPoint(sketch, "E19.0.4.9", {"position": v(75.5, -316.77) * mm});
            skLineSegment(sketch, "E19.1.4.9", {"start": v(84.5, -275.6) * mm, "end": v(84.5, -314.77) * mm});
            skPoint(sketch, "E19.4.4.9", {"position": v(84.5, -316.77) * mm});
            skLineSegment(sketch, "E19.5.4.9", {"start": v(75.5, -275.6) * mm, "end": v(84.5, -275.6) * mm});
            skLineSegment(sketch, "E19.8.4.9", {"start": v(77.5, -316.77) * mm, "end": v(82.5, -316.77) * mm});
            skLineSegment(sketch, "E19.11.4.9", {"start": v(75.5, -275.6) * mm, "end": v(75.5, -314.77) * mm});
            skArc(sketch, "E19.14.4.9", {"start": v(82.5, -316.77) * mm, "mid": v(83.91, -316.18) * mm, "end": v(84.5, -314.77) * mm});
            skArc(sketch, "E19.18.4.9", {"start": v(75.5, -314.77) * mm, "mid": v(76.09, -316.18) * mm, "end": v(77.5, -316.77) * mm});
            skPoint(sketch, "E19.0.4.10", {"position": v(75.5, -351.41) * mm});
            skLineSegment(sketch, "E19.1.4.10", {"start": v(84.5, -310.24) * mm, "end": v(84.5, -349.41) * mm});
            skPoint(sketch, "E19.4.4.10", {"position": v(84.5, -351.41) * mm});
            skLineSegment(sketch, "E19.5.4.10", {"start": v(75.5, -310.24) * mm, "end": v(84.5, -310.24) * mm});
            skLineSegment(sketch, "E19.8.4.10", {"start": v(77.5, -351.41) * mm, "end": v(82.5, -351.41) * mm});
            skLineSegment(sketch, "E19.11.4.10", {"start": v(75.5, -310.24) * mm, "end": v(75.5, -349.41) * mm});
            skArc(sketch, "E19.14.4.10", {"start": v(82.5, -351.41) * mm, "mid": v(83.91, -350.82) * mm, "end": v(84.5, -349.41) * mm});
            skArc(sketch, "E19.18.4.10", {"start": v(75.5, -349.41) * mm, "mid": v(76.09, -350.82) * mm, "end": v(77.5, -351.41) * mm});
            skPoint(sketch, "E19.0.4.11", {"position": v(75.5, -386.05) * mm});
            skLineSegment(sketch, "E19.1.4.11", {"start": v(84.5, -344.88) * mm, "end": v(84.5, -384.05) * mm});
            skPoint(sketch, "E19.4.4.11", {"position": v(84.5, -386.05) * mm});
            skLineSegment(sketch, "E19.5.4.11", {"start": v(75.5, -344.88) * mm, "end": v(84.5, -344.88) * mm});
            skLineSegment(sketch, "E19.8.4.11", {"start": v(77.5, -386.05) * mm, "end": v(82.5, -386.05) * mm});
            skLineSegment(sketch, "E19.11.4.11", {"start": v(75.5, -344.88) * mm, "end": v(75.5, -384.05) * mm});
            skArc(sketch, "E19.14.4.11", {"start": v(82.5, -386.05) * mm, "mid": v(83.91, -385.47) * mm, "end": v(84.5, -384.05) * mm});
            skArc(sketch, "E19.18.4.11", {"start": v(75.5, -384.05) * mm, "mid": v(76.09, -385.47) * mm, "end": v(77.5, -386.05) * mm});
            skPoint(sketch, "E19.0.4.12", {"position": v(75.5, -420.7) * mm});
            skLineSegment(sketch, "E19.1.4.12", {"start": v(84.5, -379.52) * mm, "end": v(84.5, -418.7) * mm});
            skPoint(sketch, "E19.4.4.12", {"position": v(84.5, -420.7) * mm});
            skLineSegment(sketch, "E19.5.4.12", {"start": v(75.5, -379.52) * mm, "end": v(84.5, -379.52) * mm});
            skLineSegment(sketch, "E19.8.4.12", {"start": v(77.5, -420.7) * mm, "end": v(82.5, -420.7) * mm});
            skLineSegment(sketch, "E19.11.4.12", {"start": v(75.5, -379.52) * mm, "end": v(75.5, -418.7) * mm});
            skArc(sketch, "E19.14.4.12", {"start": v(82.5, -420.7) * mm, "mid": v(83.91, -420.1) * mm, "end": v(84.5, -418.7) * mm});
            skArc(sketch, "E19.18.4.12", {"start": v(75.5, -418.7) * mm, "mid": v(76.09, -420.1) * mm, "end": v(77.5, -420.7) * mm});
            skPoint(sketch, "E19.0.4.13", {"position": v(75.5, -455.33) * mm});
            skLineSegment(sketch, "E19.1.4.13", {"start": v(84.5, -414.16) * mm, "end": v(84.5, -453.33) * mm});
            skPoint(sketch, "E19.4.4.13", {"position": v(84.5, -455.33) * mm});
            skLineSegment(sketch, "E19.5.4.13", {"start": v(75.5, -414.16) * mm, "end": v(84.5, -414.16) * mm});
            skLineSegment(sketch, "E19.8.4.13", {"start": v(77.5, -455.33) * mm, "end": v(82.5, -455.33) * mm});
            skLineSegment(sketch, "E19.11.4.13", {"start": v(75.5, -414.16) * mm, "end": v(75.5, -453.33) * mm});
            skArc(sketch, "E19.14.4.13", {"start": v(82.5, -455.33) * mm, "mid": v(83.91, -454.75) * mm, "end": v(84.5, -453.33) * mm});
            skArc(sketch, "E19.18.4.13", {"start": v(75.5, -453.33) * mm, "mid": v(76.09, -454.75) * mm, "end": v(77.5, -455.33) * mm});
            skPoint(sketch, "E19.0.4.14", {"position": v(75.5, -489.97) * mm});
            skLineSegment(sketch, "E19.1.4.14", {"start": v(84.5, -448.8) * mm, "end": v(84.5, -487.97) * mm});
            skPoint(sketch, "E19.4.4.14", {"position": v(84.5, -489.97) * mm});
            skLineSegment(sketch, "E19.5.4.14", {"start": v(75.5, -448.8) * mm, "end": v(84.5, -448.8) * mm});
            skLineSegment(sketch, "E19.8.4.14", {"start": v(77.5, -489.97) * mm, "end": v(82.5, -489.97) * mm});
            skLineSegment(sketch, "E19.11.4.14", {"start": v(75.5, -448.8) * mm, "end": v(75.5, -487.97) * mm});
            skArc(sketch, "E19.14.4.14", {"start": v(82.5, -489.97) * mm, "mid": v(83.91, -489.39) * mm, "end": v(84.5, -487.97) * mm});
            skArc(sketch, "E19.18.4.14", {"start": v(75.5, -487.97) * mm, "mid": v(76.09, -489.39) * mm, "end": v(77.5, -489.97) * mm});
            skPoint(sketch, "E19.0.5.0", {"position": v(95.5, -5) * mm});
            skLineSegment(sketch, "E19.1.5.0", {"start": v(104.5, 36.17) * mm, "end": v(104.5, -3) * mm});
            skPoint(sketch, "E19.4.5.0", {"position": v(104.5, -5) * mm});
            skLineSegment(sketch, "E19.5.5.0", {"start": v(95.5, 36.17) * mm, "end": v(104.5, 36.17) * mm});
            skLineSegment(sketch, "E19.8.5.0", {"start": v(97.5, -5) * mm, "end": v(102.5, -5) * mm});
            skLineSegment(sketch, "E19.11.5.0", {"start": v(95.5, 36.17) * mm, "end": v(95.5, -3) * mm});
            skArc(sketch, "E19.14.5.0", {"start": v(102.5, -5) * mm, "mid": v(103.91, -4.41) * mm, "end": v(104.5, -3) * mm});
            skArc(sketch, "E19.18.5.0", {"start": v(95.5, -3) * mm, "mid": v(96.09, -4.41) * mm, "end": v(97.5, -5) * mm});
            skPoint(sketch, "E19.0.5.1", {"position": v(95.5, -39.64) * mm});
            skLineSegment(sketch, "E19.1.5.1", {"start": v(104.5, 1.53) * mm, "end": v(104.5, -37.64) * mm});
            skPoint(sketch, "E19.4.5.1", {"position": v(104.5, -39.64) * mm});
            skLineSegment(sketch, "E19.5.5.1", {"start": v(95.5, 1.53) * mm, "end": v(104.5, 1.53) * mm});
            skLineSegment(sketch, "E19.8.5.1", {"start": v(97.5, -39.64) * mm, "end": v(102.5, -39.64) * mm});
            skLineSegment(sketch, "E19.11.5.1", {"start": v(95.5, 1.53) * mm, "end": v(95.5, -37.64) * mm});
            skArc(sketch, "E19.14.5.1", {"start": v(102.5, -39.64) * mm, "mid": v(103.91, -39.06) * mm, "end": v(104.5, -37.64) * mm});
            skArc(sketch, "E19.18.5.1", {"start": v(95.5, -37.64) * mm, "mid": v(96.09, -39.06) * mm, "end": v(97.5, -39.64) * mm});
            skPoint(sketch, "E19.0.5.2", {"position": v(95.5, -74.28) * mm});
            skLineSegment(sketch, "E19.1.5.2", {"start": v(104.5, -33.1) * mm, "end": v(104.5, -72.28) * mm});
            skPoint(sketch, "E19.4.5.2", {"position": v(104.5, -74.28) * mm});
            skLineSegment(sketch, "E19.5.5.2", {"start": v(95.5, -33.1) * mm, "end": v(104.5, -33.1) * mm});
            skLineSegment(sketch, "E19.8.5.2", {"start": v(97.5, -74.28) * mm, "end": v(102.5, -74.28) * mm});
            skLineSegment(sketch, "E19.11.5.2", {"start": v(95.5, -33.1) * mm, "end": v(95.5, -72.28) * mm});
            skArc(sketch, "E19.14.5.2", {"start": v(102.5, -74.28) * mm, "mid": v(103.91, -73.7) * mm, "end": v(104.5, -72.28) * mm});
            skArc(sketch, "E19.18.5.2", {"start": v(95.5, -72.28) * mm, "mid": v(96.09, -73.7) * mm, "end": v(97.5, -74.28) * mm});
            skPoint(sketch, "E19.0.5.3", {"position": v(95.5, -108.92) * mm});
            skLineSegment(sketch, "E19.1.5.3", {"start": v(104.5, -67.75) * mm, "end": v(104.5, -106.92) * mm});
            skPoint(sketch, "E19.4.5.3", {"position": v(104.5, -108.92) * mm});
            skLineSegment(sketch, "E19.5.5.3", {"start": v(95.5, -67.75) * mm, "end": v(104.5, -67.75) * mm});
            skLineSegment(sketch, "E19.8.5.3", {"start": v(97.5, -108.92) * mm, "end": v(102.5, -108.92) * mm});
            skLineSegment(sketch, "E19.11.5.3", {"start": v(95.5, -67.75) * mm, "end": v(95.5, -106.92) * mm});
            skArc(sketch, "E19.14.5.3", {"start": v(102.5, -108.92) * mm, "mid": v(103.91, -108.34) * mm, "end": v(104.5, -106.92) * mm});
            skArc(sketch, "E19.18.5.3", {"start": v(95.5, -106.92) * mm, "mid": v(96.09, -108.34) * mm, "end": v(97.5, -108.92) * mm});
            skPoint(sketch, "E19.0.5.4", {"position": v(95.5, -143.56) * mm});
            skLineSegment(sketch, "E19.1.5.4", {"start": v(104.5, -102.4) * mm, "end": v(104.5, -141.56) * mm});
            skPoint(sketch, "E19.4.5.4", {"position": v(104.5, -143.56) * mm});
            skLineSegment(sketch, "E19.5.5.4", {"start": v(95.5, -102.4) * mm, "end": v(104.5, -102.4) * mm});
            skLineSegment(sketch, "E19.8.5.4", {"start": v(97.5, -143.56) * mm, "end": v(102.5, -143.56) * mm});
            skLineSegment(sketch, "E19.11.5.4", {"start": v(95.5, -102.4) * mm, "end": v(95.5, -141.56) * mm});
            skArc(sketch, "E19.14.5.4", {"start": v(102.5, -143.56) * mm, "mid": v(103.91, -142.98) * mm, "end": v(104.5, -141.56) * mm});
            skArc(sketch, "E19.18.5.4", {"start": v(95.5, -141.56) * mm, "mid": v(96.09, -142.98) * mm, "end": v(97.5, -143.56) * mm});
            skPoint(sketch, "E19.0.5.5", {"position": v(95.5, -178.2) * mm});
            skLineSegment(sketch, "E19.1.5.5", {"start": v(104.5, -137.03) * mm, "end": v(104.5, -176.2) * mm});
            skPoint(sketch, "E19.4.5.5", {"position": v(104.5, -178.2) * mm});
            skLineSegment(sketch, "E19.5.5.5", {"start": v(95.5, -137.03) * mm, "end": v(104.5, -137.03) * mm});
            skLineSegment(sketch, "E19.8.5.5", {"start": v(97.5, -178.2) * mm, "end": v(102.5, -178.2) * mm});
            skLineSegment(sketch, "E19.11.5.5", {"start": v(95.5, -137.03) * mm, "end": v(95.5, -176.2) * mm});
            skArc(sketch, "E19.14.5.5", {"start": v(102.5, -178.2) * mm, "mid": v(103.91, -177.62) * mm, "end": v(104.5, -176.2) * mm});
            skArc(sketch, "E19.18.5.5", {"start": v(95.5, -176.2) * mm, "mid": v(96.09, -177.62) * mm, "end": v(97.5, -178.2) * mm});
            skPoint(sketch, "E19.0.5.6", {"position": v(95.5, -212.85) * mm});
            skLineSegment(sketch, "E19.1.5.6", {"start": v(104.5, -171.67) * mm, "end": v(104.5, -210.85) * mm});
            skPoint(sketch, "E19.4.5.6", {"position": v(104.5, -212.85) * mm});
            skLineSegment(sketch, "E19.5.5.6", {"start": v(95.5, -171.67) * mm, "end": v(104.5, -171.67) * mm});
            skLineSegment(sketch, "E19.8.5.6", {"start": v(97.5, -212.85) * mm, "end": v(102.5, -212.85) * mm});
            skLineSegment(sketch, "E19.11.5.6", {"start": v(95.5, -171.67) * mm, "end": v(95.5, -210.85) * mm});
            skArc(sketch, "E19.14.5.6", {"start": v(102.5, -212.85) * mm, "mid": v(103.91, -212.26) * mm, "end": v(104.5, -210.85) * mm});
            skArc(sketch, "E19.18.5.6", {"start": v(95.5, -210.85) * mm, "mid": v(96.09, -212.26) * mm, "end": v(97.5, -212.85) * mm});
            skPoint(sketch, "E19.0.5.7", {"position": v(95.5, -247.49) * mm});
            skLineSegment(sketch, "E19.1.5.7", {"start": v(104.5, -206.31) * mm, "end": v(104.5, -245.49) * mm});
            skPoint(sketch, "E19.4.5.7", {"position": v(104.5, -247.49) * mm});
            skLineSegment(sketch, "E19.5.5.7", {"start": v(95.5, -206.31) * mm, "end": v(104.5, -206.31) * mm});
            skLineSegment(sketch, "E19.8.5.7", {"start": v(97.5, -247.49) * mm, "end": v(102.5, -247.49) * mm});
            skLineSegment(sketch, "E19.11.5.7", {"start": v(95.5, -206.31) * mm, "end": v(95.5, -245.49) * mm});
            skArc(sketch, "E19.14.5.7", {"start": v(102.5, -247.49) * mm, "mid": v(103.91, -246.9) * mm, "end": v(104.5, -245.49) * mm});
            skArc(sketch, "E19.18.5.7", {"start": v(95.5, -245.49) * mm, "mid": v(96.09, -246.9) * mm, "end": v(97.5, -247.49) * mm});
            skPoint(sketch, "E19.0.5.8", {"position": v(95.5, -282.13) * mm});
            skLineSegment(sketch, "E19.1.5.8", {"start": v(104.5, -240.95) * mm, "end": v(104.5, -280.13) * mm});
            skPoint(sketch, "E19.4.5.8", {"position": v(104.5, -282.13) * mm});
            skLineSegment(sketch, "E19.5.5.8", {"start": v(95.5, -240.95) * mm, "end": v(104.5, -240.95) * mm});
            skLineSegment(sketch, "E19.8.5.8", {"start": v(97.5, -282.13) * mm, "end": v(102.5, -282.13) * mm});
            skLineSegment(sketch, "E19.11.5.8", {"start": v(95.5, -240.95) * mm, "end": v(95.5, -280.13) * mm});
            skArc(sketch, "E19.14.5.8", {"start": v(102.5, -282.13) * mm, "mid": v(103.91, -281.54) * mm, "end": v(104.5, -280.13) * mm});
            skArc(sketch, "E19.18.5.8", {"start": v(95.5, -280.13) * mm, "mid": v(96.09, -281.54) * mm, "end": v(97.5, -282.13) * mm});
            skPoint(sketch, "E19.0.5.9", {"position": v(95.5, -316.77) * mm});
            skLineSegment(sketch, "E19.1.5.9", {"start": v(104.5, -275.6) * mm, "end": v(104.5, -314.77) * mm});
            skPoint(sketch, "E19.4.5.9", {"position": v(104.5, -316.77) * mm});
            skLineSegment(sketch, "E19.5.5.9", {"start": v(95.5, -275.6) * mm, "end": v(104.5, -275.6) * mm});
            skLineSegment(sketch, "E19.8.5.9", {"start": v(97.5, -316.77) * mm, "end": v(102.5, -316.77) * mm});
            skLineSegment(sketch, "E19.11.5.9", {"start": v(95.5, -275.6) * mm, "end": v(95.5, -314.77) * mm});
            skArc(sketch, "E19.14.5.9", {"start": v(102.5, -316.77) * mm, "mid": v(103.91, -316.18) * mm, "end": v(104.5, -314.77) * mm});
            skArc(sketch, "E19.18.5.9", {"start": v(95.5, -314.77) * mm, "mid": v(96.09, -316.18) * mm, "end": v(97.5, -316.77) * mm});
            skPoint(sketch, "E19.0.5.10", {"position": v(95.5, -351.41) * mm});
            skLineSegment(sketch, "E19.1.5.10", {"start": v(104.5, -310.24) * mm, "end": v(104.5, -349.41) * mm});
            skPoint(sketch, "E19.4.5.10", {"position": v(104.5, -351.41) * mm});
            skLineSegment(sketch, "E19.5.5.10", {"start": v(95.5, -310.24) * mm, "end": v(104.5, -310.24) * mm});
            skLineSegment(sketch, "E19.8.5.10", {"start": v(97.5, -351.41) * mm, "end": v(102.5, -351.41) * mm});
            skLineSegment(sketch, "E19.11.5.10", {"start": v(95.5, -310.24) * mm, "end": v(95.5, -349.41) * mm});
            skArc(sketch, "E19.14.5.10", {"start": v(102.5, -351.41) * mm, "mid": v(103.91, -350.82) * mm, "end": v(104.5, -349.41) * mm});
            skArc(sketch, "E19.18.5.10", {"start": v(95.5, -349.41) * mm, "mid": v(96.09, -350.82) * mm, "end": v(97.5, -351.41) * mm});
            skPoint(sketch, "E19.0.5.11", {"position": v(95.5, -386.05) * mm});
            skLineSegment(sketch, "E19.1.5.11", {"start": v(104.5, -344.88) * mm, "end": v(104.5, -384.05) * mm});
            skPoint(sketch, "E19.4.5.11", {"position": v(104.5, -386.05) * mm});
            skLineSegment(sketch, "E19.5.5.11", {"start": v(95.5, -344.88) * mm, "end": v(104.5, -344.88) * mm});
            skLineSegment(sketch, "E19.8.5.11", {"start": v(97.5, -386.05) * mm, "end": v(102.5, -386.05) * mm});
            skLineSegment(sketch, "E19.11.5.11", {"start": v(95.5, -344.88) * mm, "end": v(95.5, -384.05) * mm});
            skArc(sketch, "E19.14.5.11", {"start": v(102.5, -386.05) * mm, "mid": v(103.91, -385.47) * mm, "end": v(104.5, -384.05) * mm});
            skArc(sketch, "E19.18.5.11", {"start": v(95.5, -384.05) * mm, "mid": v(96.09, -385.47) * mm, "end": v(97.5, -386.05) * mm});
            skPoint(sketch, "E19.0.5.12", {"position": v(95.5, -420.7) * mm});
            skLineSegment(sketch, "E19.1.5.12", {"start": v(104.5, -379.52) * mm, "end": v(104.5, -418.7) * mm});
            skPoint(sketch, "E19.4.5.12", {"position": v(104.5, -420.7) * mm});
            skLineSegment(sketch, "E19.5.5.12", {"start": v(95.5, -379.52) * mm, "end": v(104.5, -379.52) * mm});
            skLineSegment(sketch, "E19.8.5.12", {"start": v(97.5, -420.7) * mm, "end": v(102.5, -420.7) * mm});
            skLineSegment(sketch, "E19.11.5.12", {"start": v(95.5, -379.52) * mm, "end": v(95.5, -418.7) * mm});
            skArc(sketch, "E19.14.5.12", {"start": v(102.5, -420.7) * mm, "mid": v(103.91, -420.1) * mm, "end": v(104.5, -418.7) * mm});
            skArc(sketch, "E19.18.5.12", {"start": v(95.5, -418.7) * mm, "mid": v(96.09, -420.1) * mm, "end": v(97.5, -420.7) * mm});
            skPoint(sketch, "E19.0.5.13", {"position": v(95.5, -455.33) * mm});
            skLineSegment(sketch, "E19.1.5.13", {"start": v(104.5, -414.16) * mm, "end": v(104.5, -453.33) * mm});
            skPoint(sketch, "E19.4.5.13", {"position": v(104.5, -455.33) * mm});
            skLineSegment(sketch, "E19.5.5.13", {"start": v(95.5, -414.16) * mm, "end": v(104.5, -414.16) * mm});
            skLineSegment(sketch, "E19.8.5.13", {"start": v(97.5, -455.33) * mm, "end": v(102.5, -455.33) * mm});
            skLineSegment(sketch, "E19.11.5.13", {"start": v(95.5, -414.16) * mm, "end": v(95.5, -453.33) * mm});
            skArc(sketch, "E19.14.5.13", {"start": v(102.5, -455.33) * mm, "mid": v(103.91, -454.75) * mm, "end": v(104.5, -453.33) * mm});
            skArc(sketch, "E19.18.5.13", {"start": v(95.5, -453.33) * mm, "mid": v(96.09, -454.75) * mm, "end": v(97.5, -455.33) * mm});
            skPoint(sketch, "E19.0.5.14", {"position": v(95.5, -489.97) * mm});
            skLineSegment(sketch, "E19.1.5.14", {"start": v(104.5, -448.8) * mm, "end": v(104.5, -487.97) * mm});
            skPoint(sketch, "E19.4.5.14", {"position": v(104.5, -489.97) * mm});
            skLineSegment(sketch, "E19.5.5.14", {"start": v(95.5, -448.8) * mm, "end": v(104.5, -448.8) * mm});
            skLineSegment(sketch, "E19.8.5.14", {"start": v(97.5, -489.97) * mm, "end": v(102.5, -489.97) * mm});
            skLineSegment(sketch, "E19.11.5.14", {"start": v(95.5, -448.8) * mm, "end": v(95.5, -487.97) * mm});
            skArc(sketch, "E19.14.5.14", {"start": v(102.5, -489.97) * mm, "mid": v(103.91, -489.39) * mm, "end": v(104.5, -487.97) * mm});
            skArc(sketch, "E19.18.5.14", {"start": v(95.5, -487.97) * mm, "mid": v(96.09, -489.39) * mm, "end": v(97.5, -489.97) * mm});
            skPoint(sketch, "E19.0.6.0", {"position": v(115.5, -5) * mm});
            skLineSegment(sketch, "E19.1.6.0", {"start": v(124.5, 36.17) * mm, "end": v(124.5, -3) * mm});
            skPoint(sketch, "E19.4.6.0", {"position": v(124.5, -5) * mm});
            skLineSegment(sketch, "E19.5.6.0", {"start": v(115.5, 36.17) * mm, "end": v(124.5, 36.17) * mm});
            skLineSegment(sketch, "E19.8.6.0", {"start": v(117.5, -5) * mm, "end": v(122.5, -5) * mm});
            skLineSegment(sketch, "E19.11.6.0", {"start": v(115.5, 36.17) * mm, "end": v(115.5, -3) * mm});
            skArc(sketch, "E19.14.6.0", {"start": v(122.5, -5) * mm, "mid": v(123.91, -4.41) * mm, "end": v(124.5, -3) * mm});
            skArc(sketch, "E19.18.6.0", {"start": v(115.5, -3) * mm, "mid": v(116.09, -4.41) * mm, "end": v(117.5, -5) * mm});
            skPoint(sketch, "E19.0.6.1", {"position": v(115.5, -39.64) * mm});
            skLineSegment(sketch, "E19.1.6.1", {"start": v(124.5, 1.53) * mm, "end": v(124.5, -37.64) * mm});
            skPoint(sketch, "E19.4.6.1", {"position": v(124.5, -39.64) * mm});
            skLineSegment(sketch, "E19.5.6.1", {"start": v(115.5, 1.53) * mm, "end": v(124.5, 1.53) * mm});
            skLineSegment(sketch, "E19.8.6.1", {"start": v(117.5, -39.64) * mm, "end": v(122.5, -39.64) * mm});
            skLineSegment(sketch, "E19.11.6.1", {"start": v(115.5, 1.53) * mm, "end": v(115.5, -37.64) * mm});
            skArc(sketch, "E19.14.6.1", {"start": v(122.5, -39.64) * mm, "mid": v(123.91, -39.06) * mm, "end": v(124.5, -37.64) * mm});
            skArc(sketch, "E19.18.6.1", {"start": v(115.5, -37.64) * mm, "mid": v(116.09, -39.06) * mm, "end": v(117.5, -39.64) * mm});
            skPoint(sketch, "E19.0.6.2", {"position": v(115.5, -74.28) * mm});
            skLineSegment(sketch, "E19.1.6.2", {"start": v(124.5, -33.1) * mm, "end": v(124.5, -72.28) * mm});
            skPoint(sketch, "E19.4.6.2", {"position": v(124.5, -74.28) * mm});
            skLineSegment(sketch, "E19.5.6.2", {"start": v(115.5, -33.1) * mm, "end": v(124.5, -33.1) * mm});
            skLineSegment(sketch, "E19.8.6.2", {"start": v(117.5, -74.28) * mm, "end": v(122.5, -74.28) * mm});
            skLineSegment(sketch, "E19.11.6.2", {"start": v(115.5, -33.1) * mm, "end": v(115.5, -72.28) * mm});
            skArc(sketch, "E19.14.6.2", {"start": v(122.5, -74.28) * mm, "mid": v(123.91, -73.7) * mm, "end": v(124.5, -72.28) * mm});
            skArc(sketch, "E19.18.6.2", {"start": v(115.5, -72.28) * mm, "mid": v(116.09, -73.7) * mm, "end": v(117.5, -74.28) * mm});
            skPoint(sketch, "E19.0.6.3", {"position": v(115.5, -108.92) * mm});
            skLineSegment(sketch, "E19.1.6.3", {"start": v(124.5, -67.75) * mm, "end": v(124.5, -106.92) * mm});
            skPoint(sketch, "E19.4.6.3", {"position": v(124.5, -108.92) * mm});
            skLineSegment(sketch, "E19.5.6.3", {"start": v(115.5, -67.75) * mm, "end": v(124.5, -67.75) * mm});
            skLineSegment(sketch, "E19.8.6.3", {"start": v(117.5, -108.92) * mm, "end": v(122.5, -108.92) * mm});
            skLineSegment(sketch, "E19.11.6.3", {"start": v(115.5, -67.75) * mm, "end": v(115.5, -106.92) * mm});
            skArc(sketch, "E19.14.6.3", {"start": v(122.5, -108.92) * mm, "mid": v(123.91, -108.34) * mm, "end": v(124.5, -106.92) * mm});
            skArc(sketch, "E19.18.6.3", {"start": v(115.5, -106.92) * mm, "mid": v(116.09, -108.34) * mm, "end": v(117.5, -108.92) * mm});
            skPoint(sketch, "E19.0.6.4", {"position": v(115.5, -143.56) * mm});
            skLineSegment(sketch, "E19.1.6.4", {"start": v(124.5, -102.4) * mm, "end": v(124.5, -141.56) * mm});
            skPoint(sketch, "E19.4.6.4", {"position": v(124.5, -143.56) * mm});
            skLineSegment(sketch, "E19.5.6.4", {"start": v(115.5, -102.4) * mm, "end": v(124.5, -102.4) * mm});
            skLineSegment(sketch, "E19.8.6.4", {"start": v(117.5, -143.56) * mm, "end": v(122.5, -143.56) * mm});
            skLineSegment(sketch, "E19.11.6.4", {"start": v(115.5, -102.4) * mm, "end": v(115.5, -141.56) * mm});
            skArc(sketch, "E19.14.6.4", {"start": v(122.5, -143.56) * mm, "mid": v(123.91, -142.98) * mm, "end": v(124.5, -141.56) * mm});
            skArc(sketch, "E19.18.6.4", {"start": v(115.5, -141.56) * mm, "mid": v(116.09, -142.98) * mm, "end": v(117.5, -143.56) * mm});
            skPoint(sketch, "E19.0.6.5", {"position": v(115.5, -178.2) * mm});
            skLineSegment(sketch, "E19.1.6.5", {"start": v(124.5, -137.03) * mm, "end": v(124.5, -176.2) * mm});
            skPoint(sketch, "E19.4.6.5", {"position": v(124.5, -178.2) * mm});
            skLineSegment(sketch, "E19.5.6.5", {"start": v(115.5, -137.03) * mm, "end": v(124.5, -137.03) * mm});
            skLineSegment(sketch, "E19.8.6.5", {"start": v(117.5, -178.2) * mm, "end": v(122.5, -178.2) * mm});
            skLineSegment(sketch, "E19.11.6.5", {"start": v(115.5, -137.03) * mm, "end": v(115.5, -176.2) * mm});
            skArc(sketch, "E19.14.6.5", {"start": v(122.5, -178.2) * mm, "mid": v(123.91, -177.62) * mm, "end": v(124.5, -176.2) * mm});
            skArc(sketch, "E19.18.6.5", {"start": v(115.5, -176.2) * mm, "mid": v(116.09, -177.62) * mm, "end": v(117.5, -178.2) * mm});
            skPoint(sketch, "E19.0.6.6", {"position": v(115.5, -212.85) * mm});
            skLineSegment(sketch, "E19.1.6.6", {"start": v(124.5, -171.67) * mm, "end": v(124.5, -210.85) * mm});
            skPoint(sketch, "E19.4.6.6", {"position": v(124.5, -212.85) * mm});
            skLineSegment(sketch, "E19.5.6.6", {"start": v(115.5, -171.67) * mm, "end": v(124.5, -171.67) * mm});
            skLineSegment(sketch, "E19.8.6.6", {"start": v(117.5, -212.85) * mm, "end": v(122.5, -212.85) * mm});
            skLineSegment(sketch, "E19.11.6.6", {"start": v(115.5, -171.67) * mm, "end": v(115.5, -210.85) * mm});
            skArc(sketch, "E19.14.6.6", {"start": v(122.5, -212.85) * mm, "mid": v(123.91, -212.26) * mm, "end": v(124.5, -210.85) * mm});
            skArc(sketch, "E19.18.6.6", {"start": v(115.5, -210.85) * mm, "mid": v(116.09, -212.26) * mm, "end": v(117.5, -212.85) * mm});
            skPoint(sketch, "E19.0.6.7", {"position": v(115.5, -247.49) * mm});
            skLineSegment(sketch, "E19.1.6.7", {"start": v(124.5, -206.31) * mm, "end": v(124.5, -245.49) * mm});
            skPoint(sketch, "E19.4.6.7", {"position": v(124.5, -247.49) * mm});
            skLineSegment(sketch, "E19.5.6.7", {"start": v(115.5, -206.31) * mm, "end": v(124.5, -206.31) * mm});
            skLineSegment(sketch, "E19.8.6.7", {"start": v(117.5, -247.49) * mm, "end": v(122.5, -247.49) * mm});
            skLineSegment(sketch, "E19.11.6.7", {"start": v(115.5, -206.31) * mm, "end": v(115.5, -245.49) * mm});
            skArc(sketch, "E19.14.6.7", {"start": v(122.5, -247.49) * mm, "mid": v(123.91, -246.9) * mm, "end": v(124.5, -245.49) * mm});
            skArc(sketch, "E19.18.6.7", {"start": v(115.5, -245.49) * mm, "mid": v(116.09, -246.9) * mm, "end": v(117.5, -247.49) * mm});
            skPoint(sketch, "E19.0.6.8", {"position": v(115.5, -282.13) * mm});
            skLineSegment(sketch, "E19.1.6.8", {"start": v(124.5, -240.95) * mm, "end": v(124.5, -280.13) * mm});
            skPoint(sketch, "E19.4.6.8", {"position": v(124.5, -282.13) * mm});
            skLineSegment(sketch, "E19.5.6.8", {"start": v(115.5, -240.95) * mm, "end": v(124.5, -240.95) * mm});
            skLineSegment(sketch, "E19.8.6.8", {"start": v(117.5, -282.13) * mm, "end": v(122.5, -282.13) * mm});
            skLineSegment(sketch, "E19.11.6.8", {"start": v(115.5, -240.95) * mm, "end": v(115.5, -280.13) * mm});
            skArc(sketch, "E19.14.6.8", {"start": v(122.5, -282.13) * mm, "mid": v(123.91, -281.54) * mm, "end": v(124.5, -280.13) * mm});
            skArc(sketch, "E19.18.6.8", {"start": v(115.5, -280.13) * mm, "mid": v(116.09, -281.54) * mm, "end": v(117.5, -282.13) * mm});
            skPoint(sketch, "E19.0.6.9", {"position": v(115.5, -316.77) * mm});
            skLineSegment(sketch, "E19.1.6.9", {"start": v(124.5, -275.6) * mm, "end": v(124.5, -314.77) * mm});
            skPoint(sketch, "E19.4.6.9", {"position": v(124.5, -316.77) * mm});
            skLineSegment(sketch, "E19.5.6.9", {"start": v(115.5, -275.6) * mm, "end": v(124.5, -275.6) * mm});
            skLineSegment(sketch, "E19.8.6.9", {"start": v(117.5, -316.77) * mm, "end": v(122.5, -316.77) * mm});
            skLineSegment(sketch, "E19.11.6.9", {"start": v(115.5, -275.6) * mm, "end": v(115.5, -314.77) * mm});
            skArc(sketch, "E19.14.6.9", {"start": v(122.5, -316.77) * mm, "mid": v(123.91, -316.18) * mm, "end": v(124.5, -314.77) * mm});
            skArc(sketch, "E19.18.6.9", {"start": v(115.5, -314.77) * mm, "mid": v(116.09, -316.18) * mm, "end": v(117.5, -316.77) * mm});
            skPoint(sketch, "E19.0.6.10", {"position": v(115.5, -351.41) * mm});
            skLineSegment(sketch, "E19.1.6.10", {"start": v(124.5, -310.24) * mm, "end": v(124.5, -349.41) * mm});
            skPoint(sketch, "E19.4.6.10", {"position": v(124.5, -351.41) * mm});
            skLineSegment(sketch, "E19.5.6.10", {"start": v(115.5, -310.24) * mm, "end": v(124.5, -310.24) * mm});
            skLineSegment(sketch, "E19.8.6.10", {"start": v(117.5, -351.41) * mm, "end": v(122.5, -351.41) * mm});
            skLineSegment(sketch, "E19.11.6.10", {"start": v(115.5, -310.24) * mm, "end": v(115.5, -349.41) * mm});
            skArc(sketch, "E19.14.6.10", {"start": v(122.5, -351.41) * mm, "mid": v(123.91, -350.82) * mm, "end": v(124.5, -349.41) * mm});
            skArc(sketch, "E19.18.6.10", {"start": v(115.5, -349.41) * mm, "mid": v(116.09, -350.82) * mm, "end": v(117.5, -351.41) * mm});
            skPoint(sketch, "E19.0.6.11", {"position": v(115.5, -386.05) * mm});
            skLineSegment(sketch, "E19.1.6.11", {"start": v(124.5, -344.88) * mm, "end": v(124.5, -384.05) * mm});
            skPoint(sketch, "E19.4.6.11", {"position": v(124.5, -386.05) * mm});
            skLineSegment(sketch, "E19.5.6.11", {"start": v(115.5, -344.88) * mm, "end": v(124.5, -344.88) * mm});
            skLineSegment(sketch, "E19.8.6.11", {"start": v(117.5, -386.05) * mm, "end": v(122.5, -386.05) * mm});
            skLineSegment(sketch, "E19.11.6.11", {"start": v(115.5, -344.88) * mm, "end": v(115.5, -384.05) * mm});
            skArc(sketch, "E19.14.6.11", {"start": v(122.5, -386.05) * mm, "mid": v(123.91, -385.47) * mm, "end": v(124.5, -384.05) * mm});
            skArc(sketch, "E19.18.6.11", {"start": v(115.5, -384.05) * mm, "mid": v(116.09, -385.47) * mm, "end": v(117.5, -386.05) * mm});
            skPoint(sketch, "E19.0.6.12", {"position": v(115.5, -420.7) * mm});
            skLineSegment(sketch, "E19.1.6.12", {"start": v(124.5, -379.52) * mm, "end": v(124.5, -418.7) * mm});
            skPoint(sketch, "E19.4.6.12", {"position": v(124.5, -420.7) * mm});
            skLineSegment(sketch, "E19.5.6.12", {"start": v(115.5, -379.52) * mm, "end": v(124.5, -379.52) * mm});
            skLineSegment(sketch, "E19.8.6.12", {"start": v(117.5, -420.7) * mm, "end": v(122.5, -420.7) * mm});
            skLineSegment(sketch, "E19.11.6.12", {"start": v(115.5, -379.52) * mm, "end": v(115.5, -418.7) * mm});
            skArc(sketch, "E19.14.6.12", {"start": v(122.5, -420.7) * mm, "mid": v(123.91, -420.1) * mm, "end": v(124.5, -418.7) * mm});
            skArc(sketch, "E19.18.6.12", {"start": v(115.5, -418.7) * mm, "mid": v(116.09, -420.1) * mm, "end": v(117.5, -420.7) * mm});
            skPoint(sketch, "E19.0.6.13", {"position": v(115.5, -455.33) * mm});
            skLineSegment(sketch, "E19.1.6.13", {"start": v(124.5, -414.16) * mm, "end": v(124.5, -453.33) * mm});
            skPoint(sketch, "E19.4.6.13", {"position": v(124.5, -455.33) * mm});
            skLineSegment(sketch, "E19.5.6.13", {"start": v(115.5, -414.16) * mm, "end": v(124.5, -414.16) * mm});
            skLineSegment(sketch, "E19.8.6.13", {"start": v(117.5, -455.33) * mm, "end": v(122.5, -455.33) * mm});
            skLineSegment(sketch, "E19.11.6.13", {"start": v(115.5, -414.16) * mm, "end": v(115.5, -453.33) * mm});
            skArc(sketch, "E19.14.6.13", {"start": v(122.5, -455.33) * mm, "mid": v(123.91, -454.75) * mm, "end": v(124.5, -453.33) * mm});
            skArc(sketch, "E19.18.6.13", {"start": v(115.5, -453.33) * mm, "mid": v(116.09, -454.75) * mm, "end": v(117.5, -455.33) * mm});
            skPoint(sketch, "E19.0.6.14", {"position": v(115.5, -489.97) * mm});
            skLineSegment(sketch, "E19.1.6.14", {"start": v(124.5, -448.8) * mm, "end": v(124.5, -487.97) * mm});
            skPoint(sketch, "E19.4.6.14", {"position": v(124.5, -489.97) * mm});
            skLineSegment(sketch, "E19.5.6.14", {"start": v(115.5, -448.8) * mm, "end": v(124.5, -448.8) * mm});
            skLineSegment(sketch, "E19.8.6.14", {"start": v(117.5, -489.97) * mm, "end": v(122.5, -489.97) * mm});
            skLineSegment(sketch, "E19.11.6.14", {"start": v(115.5, -448.8) * mm, "end": v(115.5, -487.97) * mm});
            skArc(sketch, "E19.14.6.14", {"start": v(122.5, -489.97) * mm, "mid": v(123.91, -489.39) * mm, "end": v(124.5, -487.97) * mm});
            skArc(sketch, "E19.18.6.14", {"start": v(115.5, -487.97) * mm, "mid": v(116.09, -489.39) * mm, "end": v(117.5, -489.97) * mm});
            skPoint(sketch, "E19.0.7.0", {"position": v(135.5, -5) * mm});
            skLineSegment(sketch, "E19.1.7.0", {"start": v(144.5, 36.17) * mm, "end": v(144.5, -3) * mm});
            skPoint(sketch, "E19.4.7.0", {"position": v(144.5, -5) * mm});
            skLineSegment(sketch, "E19.5.7.0", {"start": v(135.5, 36.17) * mm, "end": v(144.5, 36.17) * mm});
            skLineSegment(sketch, "E19.8.7.0", {"start": v(137.5, -5) * mm, "end": v(142.5, -5) * mm});
            skLineSegment(sketch, "E19.11.7.0", {"start": v(135.5, 36.17) * mm, "end": v(135.5, -3) * mm});
            skArc(sketch, "E19.14.7.0", {"start": v(142.5, -5) * mm, "mid": v(143.91, -4.41) * mm, "end": v(144.5, -3) * mm});
            skArc(sketch, "E19.18.7.0", {"start": v(135.5, -3) * mm, "mid": v(136.09, -4.41) * mm, "end": v(137.5, -5) * mm});
            skPoint(sketch, "E19.0.7.1", {"position": v(135.5, -39.64) * mm});
            skLineSegment(sketch, "E19.1.7.1", {"start": v(144.5, 1.53) * mm, "end": v(144.5, -37.64) * mm});
            skPoint(sketch, "E19.4.7.1", {"position": v(144.5, -39.64) * mm});
            skLineSegment(sketch, "E19.5.7.1", {"start": v(135.5, 1.53) * mm, "end": v(144.5, 1.53) * mm});
            skLineSegment(sketch, "E19.8.7.1", {"start": v(137.5, -39.64) * mm, "end": v(142.5, -39.64) * mm});
            skLineSegment(sketch, "E19.11.7.1", {"start": v(135.5, 1.53) * mm, "end": v(135.5, -37.64) * mm});
            skArc(sketch, "E19.14.7.1", {"start": v(142.5, -39.64) * mm, "mid": v(143.91, -39.06) * mm, "end": v(144.5, -37.64) * mm});
            skArc(sketch, "E19.18.7.1", {"start": v(135.5, -37.64) * mm, "mid": v(136.09, -39.06) * mm, "end": v(137.5, -39.64) * mm});
            skPoint(sketch, "E19.0.7.2", {"position": v(135.5, -74.28) * mm});
            skLineSegment(sketch, "E19.1.7.2", {"start": v(144.5, -33.1) * mm, "end": v(144.5, -72.28) * mm});
            skPoint(sketch, "E19.4.7.2", {"position": v(144.5, -74.28) * mm});
            skLineSegment(sketch, "E19.5.7.2", {"start": v(135.5, -33.1) * mm, "end": v(144.5, -33.1) * mm});
            skLineSegment(sketch, "E19.8.7.2", {"start": v(137.5, -74.28) * mm, "end": v(142.5, -74.28) * mm});
            skLineSegment(sketch, "E19.11.7.2", {"start": v(135.5, -33.1) * mm, "end": v(135.5, -72.28) * mm});
            skArc(sketch, "E19.14.7.2", {"start": v(142.5, -74.28) * mm, "mid": v(143.91, -73.7) * mm, "end": v(144.5, -72.28) * mm});
            skArc(sketch, "E19.18.7.2", {"start": v(135.5, -72.28) * mm, "mid": v(136.09, -73.7) * mm, "end": v(137.5, -74.28) * mm});
            skPoint(sketch, "E19.0.7.3", {"position": v(135.5, -108.92) * mm});
            skLineSegment(sketch, "E19.1.7.3", {"start": v(144.5, -67.75) * mm, "end": v(144.5, -106.92) * mm});
            skPoint(sketch, "E19.4.7.3", {"position": v(144.5, -108.92) * mm});
            skLineSegment(sketch, "E19.5.7.3", {"start": v(135.5, -67.75) * mm, "end": v(144.5, -67.75) * mm});
            skLineSegment(sketch, "E19.8.7.3", {"start": v(137.5, -108.92) * mm, "end": v(142.5, -108.92) * mm});
            skLineSegment(sketch, "E19.11.7.3", {"start": v(135.5, -67.75) * mm, "end": v(135.5, -106.92) * mm});
            skArc(sketch, "E19.14.7.3", {"start": v(142.5, -108.92) * mm, "mid": v(143.91, -108.34) * mm, "end": v(144.5, -106.92) * mm});
            skArc(sketch, "E19.18.7.3", {"start": v(135.5, -106.92) * mm, "mid": v(136.09, -108.34) * mm, "end": v(137.5, -108.92) * mm});
            skPoint(sketch, "E19.0.7.4", {"position": v(135.5, -143.56) * mm});
            skLineSegment(sketch, "E19.1.7.4", {"start": v(144.5, -102.4) * mm, "end": v(144.5, -141.56) * mm});
            skPoint(sketch, "E19.4.7.4", {"position": v(144.5, -143.56) * mm});
            skLineSegment(sketch, "E19.5.7.4", {"start": v(135.5, -102.4) * mm, "end": v(144.5, -102.4) * mm});
            skLineSegment(sketch, "E19.8.7.4", {"start": v(137.5, -143.56) * mm, "end": v(142.5, -143.56) * mm});
            skLineSegment(sketch, "E19.11.7.4", {"start": v(135.5, -102.4) * mm, "end": v(135.5, -141.56) * mm});
            skArc(sketch, "E19.14.7.4", {"start": v(142.5, -143.56) * mm, "mid": v(143.91, -142.98) * mm, "end": v(144.5, -141.56) * mm});
            skArc(sketch, "E19.18.7.4", {"start": v(135.5, -141.56) * mm, "mid": v(136.09, -142.98) * mm, "end": v(137.5, -143.56) * mm});
            skPoint(sketch, "E19.0.7.5", {"position": v(135.5, -178.2) * mm});
            skLineSegment(sketch, "E19.1.7.5", {"start": v(144.5, -137.03) * mm, "end": v(144.5, -176.2) * mm});
            skPoint(sketch, "E19.4.7.5", {"position": v(144.5, -178.2) * mm});
            skLineSegment(sketch, "E19.5.7.5", {"start": v(135.5, -137.03) * mm, "end": v(144.5, -137.03) * mm});
            skLineSegment(sketch, "E19.8.7.5", {"start": v(137.5, -178.2) * mm, "end": v(142.5, -178.2) * mm});
            skLineSegment(sketch, "E19.11.7.5", {"start": v(135.5, -137.03) * mm, "end": v(135.5, -176.2) * mm});
            skArc(sketch, "E19.14.7.5", {"start": v(142.5, -178.2) * mm, "mid": v(143.91, -177.62) * mm, "end": v(144.5, -176.2) * mm});
            skArc(sketch, "E19.18.7.5", {"start": v(135.5, -176.2) * mm, "mid": v(136.09, -177.62) * mm, "end": v(137.5, -178.2) * mm});
            skPoint(sketch, "E19.0.7.6", {"position": v(135.5, -212.85) * mm});
            skLineSegment(sketch, "E19.1.7.6", {"start": v(144.5, -171.67) * mm, "end": v(144.5, -210.85) * mm});
            skPoint(sketch, "E19.4.7.6", {"position": v(144.5, -212.85) * mm});
            skLineSegment(sketch, "E19.5.7.6", {"start": v(135.5, -171.67) * mm, "end": v(144.5, -171.67) * mm});
            skLineSegment(sketch, "E19.8.7.6", {"start": v(137.5, -212.85) * mm, "end": v(142.5, -212.85) * mm});
            skLineSegment(sketch, "E19.11.7.6", {"start": v(135.5, -171.67) * mm, "end": v(135.5, -210.85) * mm});
            skArc(sketch, "E19.14.7.6", {"start": v(142.5, -212.85) * mm, "mid": v(143.91, -212.26) * mm, "end": v(144.5, -210.85) * mm});
            skArc(sketch, "E19.18.7.6", {"start": v(135.5, -210.85) * mm, "mid": v(136.09, -212.26) * mm, "end": v(137.5, -212.85) * mm});
            skPoint(sketch, "E19.0.7.7", {"position": v(135.5, -247.49) * mm});
            skLineSegment(sketch, "E19.1.7.7", {"start": v(144.5, -206.31) * mm, "end": v(144.5, -245.49) * mm});
            skPoint(sketch, "E19.4.7.7", {"position": v(144.5, -247.49) * mm});
            skLineSegment(sketch, "E19.5.7.7", {"start": v(135.5, -206.31) * mm, "end": v(144.5, -206.31) * mm});
            skLineSegment(sketch, "E19.8.7.7", {"start": v(137.5, -247.49) * mm, "end": v(142.5, -247.49) * mm});
            skLineSegment(sketch, "E19.11.7.7", {"start": v(135.5, -206.31) * mm, "end": v(135.5, -245.49) * mm});
            skArc(sketch, "E19.14.7.7", {"start": v(142.5, -247.49) * mm, "mid": v(143.91, -246.9) * mm, "end": v(144.5, -245.49) * mm});
            skArc(sketch, "E19.18.7.7", {"start": v(135.5, -245.49) * mm, "mid": v(136.09, -246.9) * mm, "end": v(137.5, -247.49) * mm});
            skPoint(sketch, "E19.0.7.8", {"position": v(135.5, -282.13) * mm});
            skLineSegment(sketch, "E19.1.7.8", {"start": v(144.5, -240.95) * mm, "end": v(144.5, -280.13) * mm});
            skPoint(sketch, "E19.4.7.8", {"position": v(144.5, -282.13) * mm});
            skLineSegment(sketch, "E19.5.7.8", {"start": v(135.5, -240.95) * mm, "end": v(144.5, -240.95) * mm});
            skLineSegment(sketch, "E19.8.7.8", {"start": v(137.5, -282.13) * mm, "end": v(142.5, -282.13) * mm});
            skLineSegment(sketch, "E19.11.7.8", {"start": v(135.5, -240.95) * mm, "end": v(135.5, -280.13) * mm});
            skArc(sketch, "E19.14.7.8", {"start": v(142.5, -282.13) * mm, "mid": v(143.91, -281.54) * mm, "end": v(144.5, -280.13) * mm});
            skArc(sketch, "E19.18.7.8", {"start": v(135.5, -280.13) * mm, "mid": v(136.09, -281.54) * mm, "end": v(137.5, -282.13) * mm});
            skPoint(sketch, "E19.0.7.9", {"position": v(135.5, -316.77) * mm});
            skLineSegment(sketch, "E19.1.7.9", {"start": v(144.5, -275.6) * mm, "end": v(144.5, -314.77) * mm});
            skPoint(sketch, "E19.4.7.9", {"position": v(144.5, -316.77) * mm});
            skLineSegment(sketch, "E19.5.7.9", {"start": v(135.5, -275.6) * mm, "end": v(144.5, -275.6) * mm});
            skLineSegment(sketch, "E19.8.7.9", {"start": v(137.5, -316.77) * mm, "end": v(142.5, -316.77) * mm});
            skLineSegment(sketch, "E19.11.7.9", {"start": v(135.5, -275.6) * mm, "end": v(135.5, -314.77) * mm});
            skArc(sketch, "E19.14.7.9", {"start": v(142.5, -316.77) * mm, "mid": v(143.91, -316.18) * mm, "end": v(144.5, -314.77) * mm});
            skArc(sketch, "E19.18.7.9", {"start": v(135.5, -314.77) * mm, "mid": v(136.09, -316.18) * mm, "end": v(137.5, -316.77) * mm});
            skPoint(sketch, "E19.0.7.10", {"position": v(135.5, -351.41) * mm});
            skLineSegment(sketch, "E19.1.7.10", {"start": v(144.5, -310.24) * mm, "end": v(144.5, -349.41) * mm});
            skPoint(sketch, "E19.4.7.10", {"position": v(144.5, -351.41) * mm});
            skLineSegment(sketch, "E19.5.7.10", {"start": v(135.5, -310.24) * mm, "end": v(144.5, -310.24) * mm});
            skLineSegment(sketch, "E19.8.7.10", {"start": v(137.5, -351.41) * mm, "end": v(142.5, -351.41) * mm});
            skLineSegment(sketch, "E19.11.7.10", {"start": v(135.5, -310.24) * mm, "end": v(135.5, -349.41) * mm});
            skArc(sketch, "E19.14.7.10", {"start": v(142.5, -351.41) * mm, "mid": v(143.91, -350.82) * mm, "end": v(144.5, -349.41) * mm});
            skArc(sketch, "E19.18.7.10", {"start": v(135.5, -349.41) * mm, "mid": v(136.09, -350.82) * mm, "end": v(137.5, -351.41) * mm});
            skPoint(sketch, "E19.0.7.11", {"position": v(135.5, -386.05) * mm});
            skLineSegment(sketch, "E19.1.7.11", {"start": v(144.5, -344.88) * mm, "end": v(144.5, -384.05) * mm});
            skPoint(sketch, "E19.4.7.11", {"position": v(144.5, -386.05) * mm});
            skLineSegment(sketch, "E19.5.7.11", {"start": v(135.5, -344.88) * mm, "end": v(144.5, -344.88) * mm});
            skLineSegment(sketch, "E19.8.7.11", {"start": v(137.5, -386.05) * mm, "end": v(142.5, -386.05) * mm});
            skLineSegment(sketch, "E19.11.7.11", {"start": v(135.5, -344.88) * mm, "end": v(135.5, -384.05) * mm});
            skArc(sketch, "E19.14.7.11", {"start": v(142.5, -386.05) * mm, "mid": v(143.91, -385.47) * mm, "end": v(144.5, -384.05) * mm});
            skArc(sketch, "E19.18.7.11", {"start": v(135.5, -384.05) * mm, "mid": v(136.09, -385.47) * mm, "end": v(137.5, -386.05) * mm});
            skPoint(sketch, "E19.0.7.12", {"position": v(135.5, -420.7) * mm});
            skLineSegment(sketch, "E19.1.7.12", {"start": v(144.5, -379.52) * mm, "end": v(144.5, -418.7) * mm});
            skPoint(sketch, "E19.4.7.12", {"position": v(144.5, -420.7) * mm});
            skLineSegment(sketch, "E19.5.7.12", {"start": v(135.5, -379.52) * mm, "end": v(144.5, -379.52) * mm});
            skLineSegment(sketch, "E19.8.7.12", {"start": v(137.5, -420.7) * mm, "end": v(142.5, -420.7) * mm});
            skLineSegment(sketch, "E19.11.7.12", {"start": v(135.5, -379.52) * mm, "end": v(135.5, -418.7) * mm});
            skArc(sketch, "E19.14.7.12", {"start": v(142.5, -420.7) * mm, "mid": v(143.91, -420.1) * mm, "end": v(144.5, -418.7) * mm});
            skArc(sketch, "E19.18.7.12", {"start": v(135.5, -418.7) * mm, "mid": v(136.09, -420.1) * mm, "end": v(137.5, -420.7) * mm});
            skPoint(sketch, "E19.0.7.13", {"position": v(135.5, -455.33) * mm});
            skLineSegment(sketch, "E19.1.7.13", {"start": v(144.5, -414.16) * mm, "end": v(144.5, -453.33) * mm});
            skPoint(sketch, "E19.4.7.13", {"position": v(144.5, -455.33) * mm});
            skLineSegment(sketch, "E19.5.7.13", {"start": v(135.5, -414.16) * mm, "end": v(144.5, -414.16) * mm});
            skLineSegment(sketch, "E19.8.7.13", {"start": v(137.5, -455.33) * mm, "end": v(142.5, -455.33) * mm});
            skLineSegment(sketch, "E19.11.7.13", {"start": v(135.5, -414.16) * mm, "end": v(135.5, -453.33) * mm});
            skArc(sketch, "E19.14.7.13", {"start": v(142.5, -455.33) * mm, "mid": v(143.91, -454.75) * mm, "end": v(144.5, -453.33) * mm});
            skArc(sketch, "E19.18.7.13", {"start": v(135.5, -453.33) * mm, "mid": v(136.09, -454.75) * mm, "end": v(137.5, -455.33) * mm});
            skPoint(sketch, "E19.0.7.14", {"position": v(135.5, -489.97) * mm});
            skLineSegment(sketch, "E19.1.7.14", {"start": v(144.5, -448.8) * mm, "end": v(144.5, -487.97) * mm});
            skPoint(sketch, "E19.4.7.14", {"position": v(144.5, -489.97) * mm});
            skLineSegment(sketch, "E19.5.7.14", {"start": v(135.5, -448.8) * mm, "end": v(144.5, -448.8) * mm});
            skLineSegment(sketch, "E19.8.7.14", {"start": v(137.5, -489.97) * mm, "end": v(142.5, -489.97) * mm});
            skLineSegment(sketch, "E19.11.7.14", {"start": v(135.5, -448.8) * mm, "end": v(135.5, -487.97) * mm});
            skArc(sketch, "E19.14.7.14", {"start": v(142.5, -489.97) * mm, "mid": v(143.91, -489.39) * mm, "end": v(144.5, -487.97) * mm});
            skArc(sketch, "E19.18.7.14", {"start": v(135.5, -487.97) * mm, "mid": v(136.09, -489.39) * mm, "end": v(137.5, -489.97) * mm});
            skPoint(sketch, "E19.0.8.0", {"position": v(155.5, -5) * mm});
            skLineSegment(sketch, "E19.1.8.0", {"start": v(164.5, 36.17) * mm, "end": v(164.5, -3) * mm});
            skPoint(sketch, "E19.4.8.0", {"position": v(164.5, -5) * mm});
            skLineSegment(sketch, "E19.5.8.0", {"start": v(155.5, 36.17) * mm, "end": v(164.5, 36.17) * mm});
            skLineSegment(sketch, "E19.8.8.0", {"start": v(157.5, -5) * mm, "end": v(162.5, -5) * mm});
            skLineSegment(sketch, "E19.11.8.0", {"start": v(155.5, 36.17) * mm, "end": v(155.5, -3) * mm});
            skArc(sketch, "E19.14.8.0", {"start": v(162.5, -5) * mm, "mid": v(163.91, -4.41) * mm, "end": v(164.5, -3) * mm});
            skArc(sketch, "E19.18.8.0", {"start": v(155.5, -3) * mm, "mid": v(156.09, -4.41) * mm, "end": v(157.5, -5) * mm});
            skPoint(sketch, "E19.0.8.1", {"position": v(155.5, -39.64) * mm});
            skLineSegment(sketch, "E19.1.8.1", {"start": v(164.5, 1.53) * mm, "end": v(164.5, -37.64) * mm});
            skPoint(sketch, "E19.4.8.1", {"position": v(164.5, -39.64) * mm});
            skLineSegment(sketch, "E19.5.8.1", {"start": v(155.5, 1.53) * mm, "end": v(164.5, 1.53) * mm});
            skLineSegment(sketch, "E19.8.8.1", {"start": v(157.5, -39.64) * mm, "end": v(162.5, -39.64) * mm});
            skLineSegment(sketch, "E19.11.8.1", {"start": v(155.5, 1.53) * mm, "end": v(155.5, -37.64) * mm});
            skArc(sketch, "E19.14.8.1", {"start": v(162.5, -39.64) * mm, "mid": v(163.91, -39.06) * mm, "end": v(164.5, -37.64) * mm});
            skArc(sketch, "E19.18.8.1", {"start": v(155.5, -37.64) * mm, "mid": v(156.09, -39.06) * mm, "end": v(157.5, -39.64) * mm});
            skPoint(sketch, "E19.0.8.2", {"position": v(155.5, -74.28) * mm});
            skLineSegment(sketch, "E19.1.8.2", {"start": v(164.5, -33.1) * mm, "end": v(164.5, -72.28) * mm});
            skPoint(sketch, "E19.4.8.2", {"position": v(164.5, -74.28) * mm});
            skLineSegment(sketch, "E19.5.8.2", {"start": v(155.5, -33.1) * mm, "end": v(164.5, -33.1) * mm});
            skLineSegment(sketch, "E19.8.8.2", {"start": v(157.5, -74.28) * mm, "end": v(162.5, -74.28) * mm});
            skLineSegment(sketch, "E19.11.8.2", {"start": v(155.5, -33.1) * mm, "end": v(155.5, -72.28) * mm});
            skArc(sketch, "E19.14.8.2", {"start": v(162.5, -74.28) * mm, "mid": v(163.91, -73.7) * mm, "end": v(164.5, -72.28) * mm});
            skArc(sketch, "E19.18.8.2", {"start": v(155.5, -72.28) * mm, "mid": v(156.09, -73.7) * mm, "end": v(157.5, -74.28) * mm});
            skPoint(sketch, "E19.0.8.3", {"position": v(155.5, -108.92) * mm});
            skLineSegment(sketch, "E19.1.8.3", {"start": v(164.5, -67.75) * mm, "end": v(164.5, -106.92) * mm});
            skPoint(sketch, "E19.4.8.3", {"position": v(164.5, -108.92) * mm});
            skLineSegment(sketch, "E19.5.8.3", {"start": v(155.5, -67.75) * mm, "end": v(164.5, -67.75) * mm});
            skLineSegment(sketch, "E19.8.8.3", {"start": v(157.5, -108.92) * mm, "end": v(162.5, -108.92) * mm});
            skLineSegment(sketch, "E19.11.8.3", {"start": v(155.5, -67.75) * mm, "end": v(155.5, -106.92) * mm});
            skArc(sketch, "E19.14.8.3", {"start": v(162.5, -108.92) * mm, "mid": v(163.91, -108.34) * mm, "end": v(164.5, -106.92) * mm});
            skArc(sketch, "E19.18.8.3", {"start": v(155.5, -106.92) * mm, "mid": v(156.09, -108.34) * mm, "end": v(157.5, -108.92) * mm});
            skPoint(sketch, "E19.0.8.4", {"position": v(155.5, -143.56) * mm});
            skLineSegment(sketch, "E19.1.8.4", {"start": v(164.5, -102.4) * mm, "end": v(164.5, -141.56) * mm});
            skPoint(sketch, "E19.4.8.4", {"position": v(164.5, -143.56) * mm});
            skLineSegment(sketch, "E19.5.8.4", {"start": v(155.5, -102.4) * mm, "end": v(164.5, -102.4) * mm});
            skLineSegment(sketch, "E19.8.8.4", {"start": v(157.5, -143.56) * mm, "end": v(162.5, -143.56) * mm});
            skLineSegment(sketch, "E19.11.8.4", {"start": v(155.5, -102.4) * mm, "end": v(155.5, -141.56) * mm});
            skArc(sketch, "E19.14.8.4", {"start": v(162.5, -143.56) * mm, "mid": v(163.91, -142.98) * mm, "end": v(164.5, -141.56) * mm});
            skArc(sketch, "E19.18.8.4", {"start": v(155.5, -141.56) * mm, "mid": v(156.09, -142.98) * mm, "end": v(157.5, -143.56) * mm});
            skPoint(sketch, "E19.0.8.5", {"position": v(155.5, -178.2) * mm});
            skLineSegment(sketch, "E19.1.8.5", {"start": v(164.5, -137.03) * mm, "end": v(164.5, -176.2) * mm});
            skPoint(sketch, "E19.4.8.5", {"position": v(164.5, -178.2) * mm});
            skLineSegment(sketch, "E19.5.8.5", {"start": v(155.5, -137.03) * mm, "end": v(164.5, -137.03) * mm});
            skLineSegment(sketch, "E19.8.8.5", {"start": v(157.5, -178.2) * mm, "end": v(162.5, -178.2) * mm});
            skLineSegment(sketch, "E19.11.8.5", {"start": v(155.5, -137.03) * mm, "end": v(155.5, -176.2) * mm});
            skArc(sketch, "E19.14.8.5", {"start": v(162.5, -178.2) * mm, "mid": v(163.91, -177.62) * mm, "end": v(164.5, -176.2) * mm});
            skArc(sketch, "E19.18.8.5", {"start": v(155.5, -176.2) * mm, "mid": v(156.09, -177.62) * mm, "end": v(157.5, -178.2) * mm});
            skPoint(sketch, "E19.0.8.6", {"position": v(155.5, -212.85) * mm});
            skLineSegment(sketch, "E19.1.8.6", {"start": v(164.5, -171.67) * mm, "end": v(164.5, -210.85) * mm});
            skPoint(sketch, "E19.4.8.6", {"position": v(164.5, -212.85) * mm});
            skLineSegment(sketch, "E19.5.8.6", {"start": v(155.5, -171.67) * mm, "end": v(164.5, -171.67) * mm});
            skLineSegment(sketch, "E19.8.8.6", {"start": v(157.5, -212.85) * mm, "end": v(162.5, -212.85) * mm});
            skLineSegment(sketch, "E19.11.8.6", {"start": v(155.5, -171.67) * mm, "end": v(155.5, -210.85) * mm});
            skArc(sketch, "E19.14.8.6", {"start": v(162.5, -212.85) * mm, "mid": v(163.91, -212.26) * mm, "end": v(164.5, -210.85) * mm});
            skArc(sketch, "E19.18.8.6", {"start": v(155.5, -210.85) * mm, "mid": v(156.09, -212.26) * mm, "end": v(157.5, -212.85) * mm});
            skPoint(sketch, "E19.0.8.7", {"position": v(155.5, -247.49) * mm});
            skLineSegment(sketch, "E19.1.8.7", {"start": v(164.5, -206.31) * mm, "end": v(164.5, -245.49) * mm});
            skPoint(sketch, "E19.4.8.7", {"position": v(164.5, -247.49) * mm});
            skLineSegment(sketch, "E19.5.8.7", {"start": v(155.5, -206.31) * mm, "end": v(164.5, -206.31) * mm});
            skLineSegment(sketch, "E19.8.8.7", {"start": v(157.5, -247.49) * mm, "end": v(162.5, -247.49) * mm});
            skLineSegment(sketch, "E19.11.8.7", {"start": v(155.5, -206.31) * mm, "end": v(155.5, -245.49) * mm});
            skArc(sketch, "E19.14.8.7", {"start": v(162.5, -247.49) * mm, "mid": v(163.91, -246.9) * mm, "end": v(164.5, -245.49) * mm});
            skArc(sketch, "E19.18.8.7", {"start": v(155.5, -245.49) * mm, "mid": v(156.09, -246.9) * mm, "end": v(157.5, -247.49) * mm});
            skPoint(sketch, "E19.0.8.8", {"position": v(155.5, -282.13) * mm});
            skLineSegment(sketch, "E19.1.8.8", {"start": v(164.5, -240.95) * mm, "end": v(164.5, -280.13) * mm});
            skPoint(sketch, "E19.4.8.8", {"position": v(164.5, -282.13) * mm});
            skLineSegment(sketch, "E19.5.8.8", {"start": v(155.5, -240.95) * mm, "end": v(164.5, -240.95) * mm});
            skLineSegment(sketch, "E19.8.8.8", {"start": v(157.5, -282.13) * mm, "end": v(162.5, -282.13) * mm});
            skLineSegment(sketch, "E19.11.8.8", {"start": v(155.5, -240.95) * mm, "end": v(155.5, -280.13) * mm});
            skArc(sketch, "E19.14.8.8", {"start": v(162.5, -282.13) * mm, "mid": v(163.91, -281.54) * mm, "end": v(164.5, -280.13) * mm});
            skArc(sketch, "E19.18.8.8", {"start": v(155.5, -280.13) * mm, "mid": v(156.09, -281.54) * mm, "end": v(157.5, -282.13) * mm});
            skPoint(sketch, "E19.0.8.9", {"position": v(155.5, -316.77) * mm});
            skLineSegment(sketch, "E19.1.8.9", {"start": v(164.5, -275.6) * mm, "end": v(164.5, -314.77) * mm});
            skPoint(sketch, "E19.4.8.9", {"position": v(164.5, -316.77) * mm});
            skLineSegment(sketch, "E19.5.8.9", {"start": v(155.5, -275.6) * mm, "end": v(164.5, -275.6) * mm});
            skLineSegment(sketch, "E19.8.8.9", {"start": v(157.5, -316.77) * mm, "end": v(162.5, -316.77) * mm});
            skLineSegment(sketch, "E19.11.8.9", {"start": v(155.5, -275.6) * mm, "end": v(155.5, -314.77) * mm});
            skArc(sketch, "E19.14.8.9", {"start": v(162.5, -316.77) * mm, "mid": v(163.91, -316.18) * mm, "end": v(164.5, -314.77) * mm});
            skArc(sketch, "E19.18.8.9", {"start": v(155.5, -314.77) * mm, "mid": v(156.09, -316.18) * mm, "end": v(157.5, -316.77) * mm});
            skPoint(sketch, "E19.0.8.10", {"position": v(155.5, -351.41) * mm});
            skLineSegment(sketch, "E19.1.8.10", {"start": v(164.5, -310.24) * mm, "end": v(164.5, -349.41) * mm});
            skPoint(sketch, "E19.4.8.10", {"position": v(164.5, -351.41) * mm});
            skLineSegment(sketch, "E19.5.8.10", {"start": v(155.5, -310.24) * mm, "end": v(164.5, -310.24) * mm});
            skLineSegment(sketch, "E19.8.8.10", {"start": v(157.5, -351.41) * mm, "end": v(162.5, -351.41) * mm});
            skLineSegment(sketch, "E19.11.8.10", {"start": v(155.5, -310.24) * mm, "end": v(155.5, -349.41) * mm});
            skArc(sketch, "E19.14.8.10", {"start": v(162.5, -351.41) * mm, "mid": v(163.91, -350.82) * mm, "end": v(164.5, -349.41) * mm});
            skArc(sketch, "E19.18.8.10", {"start": v(155.5, -349.41) * mm, "mid": v(156.09, -350.82) * mm, "end": v(157.5, -351.41) * mm});
            skPoint(sketch, "E19.0.8.11", {"position": v(155.5, -386.05) * mm});
            skLineSegment(sketch, "E19.1.8.11", {"start": v(164.5, -344.88) * mm, "end": v(164.5, -384.05) * mm});
            skPoint(sketch, "E19.4.8.11", {"position": v(164.5, -386.05) * mm});
            skLineSegment(sketch, "E19.5.8.11", {"start": v(155.5, -344.88) * mm, "end": v(164.5, -344.88) * mm});
            skLineSegment(sketch, "E19.8.8.11", {"start": v(157.5, -386.05) * mm, "end": v(162.5, -386.05) * mm});
            skLineSegment(sketch, "E19.11.8.11", {"start": v(155.5, -344.88) * mm, "end": v(155.5, -384.05) * mm});
            skArc(sketch, "E19.14.8.11", {"start": v(162.5, -386.05) * mm, "mid": v(163.91, -385.47) * mm, "end": v(164.5, -384.05) * mm});
            skArc(sketch, "E19.18.8.11", {"start": v(155.5, -384.05) * mm, "mid": v(156.09, -385.47) * mm, "end": v(157.5, -386.05) * mm});
            skPoint(sketch, "E19.0.8.12", {"position": v(155.5, -420.7) * mm});
            skLineSegment(sketch, "E19.1.8.12", {"start": v(164.5, -379.52) * mm, "end": v(164.5, -418.7) * mm});
            skPoint(sketch, "E19.4.8.12", {"position": v(164.5, -420.7) * mm});
            skLineSegment(sketch, "E19.5.8.12", {"start": v(155.5, -379.52) * mm, "end": v(164.5, -379.52) * mm});
            skLineSegment(sketch, "E19.8.8.12", {"start": v(157.5, -420.7) * mm, "end": v(162.5, -420.7) * mm});
            skLineSegment(sketch, "E19.11.8.12", {"start": v(155.5, -379.52) * mm, "end": v(155.5, -418.7) * mm});
            skArc(sketch, "E19.14.8.12", {"start": v(162.5, -420.7) * mm, "mid": v(163.91, -420.1) * mm, "end": v(164.5, -418.7) * mm});
            skArc(sketch, "E19.18.8.12", {"start": v(155.5, -418.7) * mm, "mid": v(156.09, -420.1) * mm, "end": v(157.5, -420.7) * mm});
            skPoint(sketch, "E19.0.8.13", {"position": v(155.5, -455.33) * mm});
            skLineSegment(sketch, "E19.1.8.13", {"start": v(164.5, -414.16) * mm, "end": v(164.5, -453.33) * mm});
            skPoint(sketch, "E19.4.8.13", {"position": v(164.5, -455.33) * mm});
            skLineSegment(sketch, "E19.5.8.13", {"start": v(155.5, -414.16) * mm, "end": v(164.5, -414.16) * mm});
            skLineSegment(sketch, "E19.8.8.13", {"start": v(157.5, -455.33) * mm, "end": v(162.5, -455.33) * mm});
            skLineSegment(sketch, "E19.11.8.13", {"start": v(155.5, -414.16) * mm, "end": v(155.5, -453.33) * mm});
            skArc(sketch, "E19.14.8.13", {"start": v(162.5, -455.33) * mm, "mid": v(163.91, -454.75) * mm, "end": v(164.5, -453.33) * mm});
            skArc(sketch, "E19.18.8.13", {"start": v(155.5, -453.33) * mm, "mid": v(156.09, -454.75) * mm, "end": v(157.5, -455.33) * mm});
            skPoint(sketch, "E19.0.8.14", {"position": v(155.5, -489.97) * mm});
            skLineSegment(sketch, "E19.1.8.14", {"start": v(164.5, -448.8) * mm, "end": v(164.5, -487.97) * mm});
            skPoint(sketch, "E19.4.8.14", {"position": v(164.5, -489.97) * mm});
            skLineSegment(sketch, "E19.5.8.14", {"start": v(155.5, -448.8) * mm, "end": v(164.5, -448.8) * mm});
            skLineSegment(sketch, "E19.8.8.14", {"start": v(157.5, -489.97) * mm, "end": v(162.5, -489.97) * mm});
            skLineSegment(sketch, "E19.11.8.14", {"start": v(155.5, -448.8) * mm, "end": v(155.5, -487.97) * mm});
            skArc(sketch, "E19.14.8.14", {"start": v(162.5, -489.97) * mm, "mid": v(163.91, -489.39) * mm, "end": v(164.5, -487.97) * mm});
            skArc(sketch, "E19.18.8.14", {"start": v(155.5, -487.97) * mm, "mid": v(156.09, -489.39) * mm, "end": v(157.5, -489.97) * mm});
            skPoint(sketch, "E19.0.9.0", {"position": v(175.5, -5) * mm});
            skLineSegment(sketch, "E19.1.9.0", {"start": v(184.5, 36.17) * mm, "end": v(184.5, -3) * mm});
            skPoint(sketch, "E19.4.9.0", {"position": v(184.5, -5) * mm});
            skLineSegment(sketch, "E19.5.9.0", {"start": v(175.5, 36.17) * mm, "end": v(184.5, 36.17) * mm});
            skLineSegment(sketch, "E19.8.9.0", {"start": v(177.5, -5) * mm, "end": v(182.5, -5) * mm});
            skLineSegment(sketch, "E19.11.9.0", {"start": v(175.5, 36.17) * mm, "end": v(175.5, -3) * mm});
            skArc(sketch, "E19.14.9.0", {"start": v(182.5, -5) * mm, "mid": v(183.91, -4.41) * mm, "end": v(184.5, -3) * mm});
            skArc(sketch, "E19.18.9.0", {"start": v(175.5, -3) * mm, "mid": v(176.09, -4.41) * mm, "end": v(177.5, -5) * mm});
            skPoint(sketch, "E19.0.9.1", {"position": v(175.5, -39.64) * mm});
            skLineSegment(sketch, "E19.1.9.1", {"start": v(184.5, 1.53) * mm, "end": v(184.5, -37.64) * mm});
            skPoint(sketch, "E19.4.9.1", {"position": v(184.5, -39.64) * mm});
            skLineSegment(sketch, "E19.5.9.1", {"start": v(175.5, 1.53) * mm, "end": v(184.5, 1.53) * mm});
            skLineSegment(sketch, "E19.8.9.1", {"start": v(177.5, -39.64) * mm, "end": v(182.5, -39.64) * mm});
            skLineSegment(sketch, "E19.11.9.1", {"start": v(175.5, 1.53) * mm, "end": v(175.5, -37.64) * mm});
            skArc(sketch, "E19.14.9.1", {"start": v(182.5, -39.64) * mm, "mid": v(183.91, -39.06) * mm, "end": v(184.5, -37.64) * mm});
            skArc(sketch, "E19.18.9.1", {"start": v(175.5, -37.64) * mm, "mid": v(176.09, -39.06) * mm, "end": v(177.5, -39.64) * mm});
            skPoint(sketch, "E19.0.9.2", {"position": v(175.5, -74.28) * mm});
            skLineSegment(sketch, "E19.1.9.2", {"start": v(184.5, -33.1) * mm, "end": v(184.5, -72.28) * mm});
            skPoint(sketch, "E19.4.9.2", {"position": v(184.5, -74.28) * mm});
            skLineSegment(sketch, "E19.5.9.2", {"start": v(175.5, -33.1) * mm, "end": v(184.5, -33.1) * mm});
            skLineSegment(sketch, "E19.8.9.2", {"start": v(177.5, -74.28) * mm, "end": v(182.5, -74.28) * mm});
            skLineSegment(sketch, "E19.11.9.2", {"start": v(175.5, -33.1) * mm, "end": v(175.5, -72.28) * mm});
            skArc(sketch, "E19.14.9.2", {"start": v(182.5, -74.28) * mm, "mid": v(183.91, -73.7) * mm, "end": v(184.5, -72.28) * mm});
            skArc(sketch, "E19.18.9.2", {"start": v(175.5, -72.28) * mm, "mid": v(176.09, -73.7) * mm, "end": v(177.5, -74.28) * mm});
            skPoint(sketch, "E19.0.9.3", {"position": v(175.5, -108.92) * mm});
            skLineSegment(sketch, "E19.1.9.3", {"start": v(184.5, -67.75) * mm, "end": v(184.5, -106.92) * mm});
            skPoint(sketch, "E19.4.9.3", {"position": v(184.5, -108.92) * mm});
            skLineSegment(sketch, "E19.5.9.3", {"start": v(175.5, -67.75) * mm, "end": v(184.5, -67.75) * mm});
            skLineSegment(sketch, "E19.8.9.3", {"start": v(177.5, -108.92) * mm, "end": v(182.5, -108.92) * mm});
            skLineSegment(sketch, "E19.11.9.3", {"start": v(175.5, -67.75) * mm, "end": v(175.5, -106.92) * mm});
            skArc(sketch, "E19.14.9.3", {"start": v(182.5, -108.92) * mm, "mid": v(183.91, -108.34) * mm, "end": v(184.5, -106.92) * mm});
            skArc(sketch, "E19.18.9.3", {"start": v(175.5, -106.92) * mm, "mid": v(176.09, -108.34) * mm, "end": v(177.5, -108.92) * mm});
            skPoint(sketch, "E19.0.9.4", {"position": v(175.5, -143.56) * mm});
            skLineSegment(sketch, "E19.1.9.4", {"start": v(184.5, -102.4) * mm, "end": v(184.5, -141.56) * mm});
            skPoint(sketch, "E19.4.9.4", {"position": v(184.5, -143.56) * mm});
            skLineSegment(sketch, "E19.5.9.4", {"start": v(175.5, -102.4) * mm, "end": v(184.5, -102.4) * mm});
            skLineSegment(sketch, "E19.8.9.4", {"start": v(177.5, -143.56) * mm, "end": v(182.5, -143.56) * mm});
            skLineSegment(sketch, "E19.11.9.4", {"start": v(175.5, -102.4) * mm, "end": v(175.5, -141.56) * mm});
            skArc(sketch, "E19.14.9.4", {"start": v(182.5, -143.56) * mm, "mid": v(183.91, -142.98) * mm, "end": v(184.5, -141.56) * mm});
            skArc(sketch, "E19.18.9.4", {"start": v(175.5, -141.56) * mm, "mid": v(176.09, -142.98) * mm, "end": v(177.5, -143.56) * mm});
            skPoint(sketch, "E19.0.9.5", {"position": v(175.5, -178.2) * mm});
            skLineSegment(sketch, "E19.1.9.5", {"start": v(184.5, -137.03) * mm, "end": v(184.5, -176.2) * mm});
            skPoint(sketch, "E19.4.9.5", {"position": v(184.5, -178.2) * mm});
            skLineSegment(sketch, "E19.5.9.5", {"start": v(175.5, -137.03) * mm, "end": v(184.5, -137.03) * mm});
            skLineSegment(sketch, "E19.8.9.5", {"start": v(177.5, -178.2) * mm, "end": v(182.5, -178.2) * mm});
            skLineSegment(sketch, "E19.11.9.5", {"start": v(175.5, -137.03) * mm, "end": v(175.5, -176.2) * mm});
            skArc(sketch, "E19.14.9.5", {"start": v(182.5, -178.2) * mm, "mid": v(183.91, -177.62) * mm, "end": v(184.5, -176.2) * mm});
            skArc(sketch, "E19.18.9.5", {"start": v(175.5, -176.2) * mm, "mid": v(176.09, -177.62) * mm, "end": v(177.5, -178.2) * mm});
            skPoint(sketch, "E19.0.9.6", {"position": v(175.5, -212.85) * mm});
            skLineSegment(sketch, "E19.1.9.6", {"start": v(184.5, -171.67) * mm, "end": v(184.5, -210.85) * mm});
            skPoint(sketch, "E19.4.9.6", {"position": v(184.5, -212.85) * mm});
            skLineSegment(sketch, "E19.5.9.6", {"start": v(175.5, -171.67) * mm, "end": v(184.5, -171.67) * mm});
            skLineSegment(sketch, "E19.8.9.6", {"start": v(177.5, -212.85) * mm, "end": v(182.5, -212.85) * mm});
            skLineSegment(sketch, "E19.11.9.6", {"start": v(175.5, -171.67) * mm, "end": v(175.5, -210.85) * mm});
            skArc(sketch, "E19.14.9.6", {"start": v(182.5, -212.85) * mm, "mid": v(183.91, -212.26) * mm, "end": v(184.5, -210.85) * mm});
            skArc(sketch, "E19.18.9.6", {"start": v(175.5, -210.85) * mm, "mid": v(176.09, -212.26) * mm, "end": v(177.5, -212.85) * mm});
            skPoint(sketch, "E19.0.9.7", {"position": v(175.5, -247.49) * mm});
            skLineSegment(sketch, "E19.1.9.7", {"start": v(184.5, -206.31) * mm, "end": v(184.5, -245.49) * mm});
            skPoint(sketch, "E19.4.9.7", {"position": v(184.5, -247.49) * mm});
            skLineSegment(sketch, "E19.5.9.7", {"start": v(175.5, -206.31) * mm, "end": v(184.5, -206.31) * mm});
            skLineSegment(sketch, "E19.8.9.7", {"start": v(177.5, -247.49) * mm, "end": v(182.5, -247.49) * mm});
            skLineSegment(sketch, "E19.11.9.7", {"start": v(175.5, -206.31) * mm, "end": v(175.5, -245.49) * mm});
            skArc(sketch, "E19.14.9.7", {"start": v(182.5, -247.49) * mm, "mid": v(183.91, -246.9) * mm, "end": v(184.5, -245.49) * mm});
            skArc(sketch, "E19.18.9.7", {"start": v(175.5, -245.49) * mm, "mid": v(176.09, -246.9) * mm, "end": v(177.5, -247.49) * mm});
            skPoint(sketch, "E19.0.9.8", {"position": v(175.5, -282.13) * mm});
            skLineSegment(sketch, "E19.1.9.8", {"start": v(184.5, -240.95) * mm, "end": v(184.5, -280.13) * mm});
            skPoint(sketch, "E19.4.9.8", {"position": v(184.5, -282.13) * mm});
            skLineSegment(sketch, "E19.5.9.8", {"start": v(175.5, -240.95) * mm, "end": v(184.5, -240.95) * mm});
            skLineSegment(sketch, "E19.8.9.8", {"start": v(177.5, -282.13) * mm, "end": v(182.5, -282.13) * mm});
            skLineSegment(sketch, "E19.11.9.8", {"start": v(175.5, -240.95) * mm, "end": v(175.5, -280.13) * mm});
            skArc(sketch, "E19.14.9.8", {"start": v(182.5, -282.13) * mm, "mid": v(183.91, -281.54) * mm, "end": v(184.5, -280.13) * mm});
            skArc(sketch, "E19.18.9.8", {"start": v(175.5, -280.13) * mm, "mid": v(176.09, -281.54) * mm, "end": v(177.5, -282.13) * mm});
            skPoint(sketch, "E19.0.9.9", {"position": v(175.5, -316.77) * mm});
            skLineSegment(sketch, "E19.1.9.9", {"start": v(184.5, -275.6) * mm, "end": v(184.5, -314.77) * mm});
            skPoint(sketch, "E19.4.9.9", {"position": v(184.5, -316.77) * mm});
            skLineSegment(sketch, "E19.5.9.9", {"start": v(175.5, -275.6) * mm, "end": v(184.5, -275.6) * mm});
            skLineSegment(sketch, "E19.8.9.9", {"start": v(177.5, -316.77) * mm, "end": v(182.5, -316.77) * mm});
            skLineSegment(sketch, "E19.11.9.9", {"start": v(175.5, -275.6) * mm, "end": v(175.5, -314.77) * mm});
            skArc(sketch, "E19.14.9.9", {"start": v(182.5, -316.77) * mm, "mid": v(183.91, -316.18) * mm, "end": v(184.5, -314.77) * mm});
            skArc(sketch, "E19.18.9.9", {"start": v(175.5, -314.77) * mm, "mid": v(176.09, -316.18) * mm, "end": v(177.5, -316.77) * mm});
            skPoint(sketch, "E19.0.9.10", {"position": v(175.5, -351.41) * mm});
            skLineSegment(sketch, "E19.1.9.10", {"start": v(184.5, -310.24) * mm, "end": v(184.5, -349.41) * mm});
            skPoint(sketch, "E19.4.9.10", {"position": v(184.5, -351.41) * mm});
            skLineSegment(sketch, "E19.5.9.10", {"start": v(175.5, -310.24) * mm, "end": v(184.5, -310.24) * mm});
            skLineSegment(sketch, "E19.8.9.10", {"start": v(177.5, -351.41) * mm, "end": v(182.5, -351.41) * mm});
            skLineSegment(sketch, "E19.11.9.10", {"start": v(175.5, -310.24) * mm, "end": v(175.5, -349.41) * mm});
            skArc(sketch, "E19.14.9.10", {"start": v(182.5, -351.41) * mm, "mid": v(183.91, -350.82) * mm, "end": v(184.5, -349.41) * mm});
            skArc(sketch, "E19.18.9.10", {"start": v(175.5, -349.41) * mm, "mid": v(176.09, -350.82) * mm, "end": v(177.5, -351.41) * mm});
            skPoint(sketch, "E19.0.9.11", {"position": v(175.5, -386.05) * mm});
            skLineSegment(sketch, "E19.1.9.11", {"start": v(184.5, -344.88) * mm, "end": v(184.5, -384.05) * mm});
            skPoint(sketch, "E19.4.9.11", {"position": v(184.5, -386.05) * mm});
            skLineSegment(sketch, "E19.5.9.11", {"start": v(175.5, -344.88) * mm, "end": v(184.5, -344.88) * mm});
            skLineSegment(sketch, "E19.8.9.11", {"start": v(177.5, -386.05) * mm, "end": v(182.5, -386.05) * mm});
            skLineSegment(sketch, "E19.11.9.11", {"start": v(175.5, -344.88) * mm, "end": v(175.5, -384.05) * mm});
            skArc(sketch, "E19.14.9.11", {"start": v(182.5, -386.05) * mm, "mid": v(183.91, -385.47) * mm, "end": v(184.5, -384.05) * mm});
            skArc(sketch, "E19.18.9.11", {"start": v(175.5, -384.05) * mm, "mid": v(176.09, -385.47) * mm, "end": v(177.5, -386.05) * mm});
            skPoint(sketch, "E19.0.9.12", {"position": v(175.5, -420.7) * mm});
            skLineSegment(sketch, "E19.1.9.12", {"start": v(184.5, -379.52) * mm, "end": v(184.5, -418.7) * mm});
            skPoint(sketch, "E19.4.9.12", {"position": v(184.5, -420.7) * mm});
            skLineSegment(sketch, "E19.5.9.12", {"start": v(175.5, -379.52) * mm, "end": v(184.5, -379.52) * mm});
            skLineSegment(sketch, "E19.8.9.12", {"start": v(177.5, -420.7) * mm, "end": v(182.5, -420.7) * mm});
            skLineSegment(sketch, "E19.11.9.12", {"start": v(175.5, -379.52) * mm, "end": v(175.5, -418.7) * mm});
            skArc(sketch, "E19.14.9.12", {"start": v(182.5, -420.7) * mm, "mid": v(183.91, -420.1) * mm, "end": v(184.5, -418.7) * mm});
            skArc(sketch, "E19.18.9.12", {"start": v(175.5, -418.7) * mm, "mid": v(176.09, -420.1) * mm, "end": v(177.5, -420.7) * mm});
            skPoint(sketch, "E19.0.9.13", {"position": v(175.5, -455.33) * mm});
            skLineSegment(sketch, "E19.1.9.13", {"start": v(184.5, -414.16) * mm, "end": v(184.5, -453.33) * mm});
            skPoint(sketch, "E19.4.9.13", {"position": v(184.5, -455.33) * mm});
            skLineSegment(sketch, "E19.5.9.13", {"start": v(175.5, -414.16) * mm, "end": v(184.5, -414.16) * mm});
            skLineSegment(sketch, "E19.8.9.13", {"start": v(177.5, -455.33) * mm, "end": v(182.5, -455.33) * mm});
            skLineSegment(sketch, "E19.11.9.13", {"start": v(175.5, -414.16) * mm, "end": v(175.5, -453.33) * mm});
            skArc(sketch, "E19.14.9.13", {"start": v(182.5, -455.33) * mm, "mid": v(183.91, -454.75) * mm, "end": v(184.5, -453.33) * mm});
            skArc(sketch, "E19.18.9.13", {"start": v(175.5, -453.33) * mm, "mid": v(176.09, -454.75) * mm, "end": v(177.5, -455.33) * mm});
            skPoint(sketch, "E19.0.9.14", {"position": v(175.5, -489.97) * mm});
            skLineSegment(sketch, "E19.1.9.14", {"start": v(184.5, -448.8) * mm, "end": v(184.5, -487.97) * mm});
            skPoint(sketch, "E19.4.9.14", {"position": v(184.5, -489.97) * mm});
            skLineSegment(sketch, "E19.5.9.14", {"start": v(175.5, -448.8) * mm, "end": v(184.5, -448.8) * mm});
            skLineSegment(sketch, "E19.8.9.14", {"start": v(177.5, -489.97) * mm, "end": v(182.5, -489.97) * mm});
            skLineSegment(sketch, "E19.11.9.14", {"start": v(175.5, -448.8) * mm, "end": v(175.5, -487.97) * mm});
            skArc(sketch, "E19.14.9.14", {"start": v(182.5, -489.97) * mm, "mid": v(183.91, -489.39) * mm, "end": v(184.5, -487.97) * mm});
            skArc(sketch, "E19.18.9.14", {"start": v(175.5, -487.97) * mm, "mid": v(176.09, -489.39) * mm, "end": v(177.5, -489.97) * mm});
            skPoint(sketch, "E19.0.10.0", {"position": v(195.5, -5) * mm});
            skLineSegment(sketch, "E19.1.10.0", {"start": v(204.5, 36.17) * mm, "end": v(204.5, -3) * mm});
            skPoint(sketch, "E19.4.10.0", {"position": v(204.5, -5) * mm});
            skLineSegment(sketch, "E19.5.10.0", {"start": v(195.5, 36.17) * mm, "end": v(204.5, 36.17) * mm});
            skLineSegment(sketch, "E19.8.10.0", {"start": v(197.5, -5) * mm, "end": v(202.5, -5) * mm});
            skLineSegment(sketch, "E19.11.10.0", {"start": v(195.5, 36.17) * mm, "end": v(195.5, -3) * mm});
            skArc(sketch, "E19.14.10.0", {"start": v(202.5, -5) * mm, "mid": v(203.91, -4.41) * mm, "end": v(204.5, -3) * mm});
            skArc(sketch, "E19.18.10.0", {"start": v(195.5, -3) * mm, "mid": v(196.09, -4.41) * mm, "end": v(197.5, -5) * mm});
            skPoint(sketch, "E19.0.10.1", {"position": v(195.5, -39.64) * mm});
            skLineSegment(sketch, "E19.1.10.1", {"start": v(204.5, 1.53) * mm, "end": v(204.5, -37.64) * mm});
            skPoint(sketch, "E19.4.10.1", {"position": v(204.5, -39.64) * mm});
            skLineSegment(sketch, "E19.5.10.1", {"start": v(195.5, 1.53) * mm, "end": v(204.5, 1.53) * mm});
            skLineSegment(sketch, "E19.8.10.1", {"start": v(197.5, -39.64) * mm, "end": v(202.5, -39.64) * mm});
            skLineSegment(sketch, "E19.11.10.1", {"start": v(195.5, 1.53) * mm, "end": v(195.5, -37.64) * mm});
            skArc(sketch, "E19.14.10.1", {"start": v(202.5, -39.64) * mm, "mid": v(203.91, -39.06) * mm, "end": v(204.5, -37.64) * mm});
            skArc(sketch, "E19.18.10.1", {"start": v(195.5, -37.64) * mm, "mid": v(196.09, -39.06) * mm, "end": v(197.5, -39.64) * mm});
            skPoint(sketch, "E19.0.10.2", {"position": v(195.5, -74.28) * mm});
            skLineSegment(sketch, "E19.1.10.2", {"start": v(204.5, -33.1) * mm, "end": v(204.5, -72.28) * mm});
            skPoint(sketch, "E19.4.10.2", {"position": v(204.5, -74.28) * mm});
            skLineSegment(sketch, "E19.5.10.2", {"start": v(195.5, -33.1) * mm, "end": v(204.5, -33.1) * mm});
            skLineSegment(sketch, "E19.8.10.2", {"start": v(197.5, -74.28) * mm, "end": v(202.5, -74.28) * mm});
            skLineSegment(sketch, "E19.11.10.2", {"start": v(195.5, -33.1) * mm, "end": v(195.5, -72.28) * mm});
            skArc(sketch, "E19.14.10.2", {"start": v(202.5, -74.28) * mm, "mid": v(203.91, -73.7) * mm, "end": v(204.5, -72.28) * mm});
            skArc(sketch, "E19.18.10.2", {"start": v(195.5, -72.28) * mm, "mid": v(196.09, -73.7) * mm, "end": v(197.5, -74.28) * mm});
            skPoint(sketch, "E19.0.10.3", {"position": v(195.5, -108.92) * mm});
            skLineSegment(sketch, "E19.1.10.3", {"start": v(204.5, -67.75) * mm, "end": v(204.5, -106.92) * mm});
            skPoint(sketch, "E19.4.10.3", {"position": v(204.5, -108.92) * mm});
            skLineSegment(sketch, "E19.5.10.3", {"start": v(195.5, -67.75) * mm, "end": v(204.5, -67.75) * mm});
            skLineSegment(sketch, "E19.8.10.3", {"start": v(197.5, -108.92) * mm, "end": v(202.5, -108.92) * mm});
            skLineSegment(sketch, "E19.11.10.3", {"start": v(195.5, -67.75) * mm, "end": v(195.5, -106.92) * mm});
            skArc(sketch, "E19.14.10.3", {"start": v(202.5, -108.92) * mm, "mid": v(203.91, -108.34) * mm, "end": v(204.5, -106.92) * mm});
            skArc(sketch, "E19.18.10.3", {"start": v(195.5, -106.92) * mm, "mid": v(196.09, -108.34) * mm, "end": v(197.5, -108.92) * mm});
            skPoint(sketch, "E19.0.10.4", {"position": v(195.5, -143.56) * mm});
            skLineSegment(sketch, "E19.1.10.4", {"start": v(204.5, -102.4) * mm, "end": v(204.5, -141.56) * mm});
            skPoint(sketch, "E19.4.10.4", {"position": v(204.5, -143.56) * mm});
            skLineSegment(sketch, "E19.5.10.4", {"start": v(195.5, -102.4) * mm, "end": v(204.5, -102.4) * mm});
            skLineSegment(sketch, "E19.8.10.4", {"start": v(197.5, -143.56) * mm, "end": v(202.5, -143.56) * mm});
            skLineSegment(sketch, "E19.11.10.4", {"start": v(195.5, -102.4) * mm, "end": v(195.5, -141.56) * mm});
            skArc(sketch, "E19.14.10.4", {"start": v(202.5, -143.56) * mm, "mid": v(203.91, -142.98) * mm, "end": v(204.5, -141.56) * mm});
            skArc(sketch, "E19.18.10.4", {"start": v(195.5, -141.56) * mm, "mid": v(196.09, -142.98) * mm, "end": v(197.5, -143.56) * mm});
            skPoint(sketch, "E19.0.10.5", {"position": v(195.5, -178.2) * mm});
            skLineSegment(sketch, "E19.1.10.5", {"start": v(204.5, -137.03) * mm, "end": v(204.5, -176.2) * mm});
            skPoint(sketch, "E19.4.10.5", {"position": v(204.5, -178.2) * mm});
            skLineSegment(sketch, "E19.5.10.5", {"start": v(195.5, -137.03) * mm, "end": v(204.5, -137.03) * mm});
            skLineSegment(sketch, "E19.8.10.5", {"start": v(197.5, -178.2) * mm, "end": v(202.5, -178.2) * mm});
            skLineSegment(sketch, "E19.11.10.5", {"start": v(195.5, -137.03) * mm, "end": v(195.5, -176.2) * mm});
            skArc(sketch, "E19.14.10.5", {"start": v(202.5, -178.2) * mm, "mid": v(203.91, -177.62) * mm, "end": v(204.5, -176.2) * mm});
            skArc(sketch, "E19.18.10.5", {"start": v(195.5, -176.2) * mm, "mid": v(196.09, -177.62) * mm, "end": v(197.5, -178.2) * mm});
            skPoint(sketch, "E19.0.10.6", {"position": v(195.5, -212.85) * mm});
            skLineSegment(sketch, "E19.1.10.6", {"start": v(204.5, -171.67) * mm, "end": v(204.5, -210.85) * mm});
            skPoint(sketch, "E19.4.10.6", {"position": v(204.5, -212.85) * mm});
            skLineSegment(sketch, "E19.5.10.6", {"start": v(195.5, -171.67) * mm, "end": v(204.5, -171.67) * mm});
            skLineSegment(sketch, "E19.8.10.6", {"start": v(197.5, -212.85) * mm, "end": v(202.5, -212.85) * mm});
            skLineSegment(sketch, "E19.11.10.6", {"start": v(195.5, -171.67) * mm, "end": v(195.5, -210.85) * mm});
            skArc(sketch, "E19.14.10.6", {"start": v(202.5, -212.85) * mm, "mid": v(203.91, -212.26) * mm, "end": v(204.5, -210.85) * mm});
            skArc(sketch, "E19.18.10.6", {"start": v(195.5, -210.85) * mm, "mid": v(196.09, -212.26) * mm, "end": v(197.5, -212.85) * mm});
            skPoint(sketch, "E19.0.10.7", {"position": v(195.5, -247.49) * mm});
            skLineSegment(sketch, "E19.1.10.7", {"start": v(204.5, -206.31) * mm, "end": v(204.5, -245.49) * mm});
            skPoint(sketch, "E19.4.10.7", {"position": v(204.5, -247.49) * mm});
            skLineSegment(sketch, "E19.5.10.7", {"start": v(195.5, -206.31) * mm, "end": v(204.5, -206.31) * mm});
            skLineSegment(sketch, "E19.8.10.7", {"start": v(197.5, -247.49) * mm, "end": v(202.5, -247.49) * mm});
            skLineSegment(sketch, "E19.11.10.7", {"start": v(195.5, -206.31) * mm, "end": v(195.5, -245.49) * mm});
            skArc(sketch, "E19.14.10.7", {"start": v(202.5, -247.49) * mm, "mid": v(203.91, -246.9) * mm, "end": v(204.5, -245.49) * mm});
            skArc(sketch, "E19.18.10.7", {"start": v(195.5, -245.49) * mm, "mid": v(196.09, -246.9) * mm, "end": v(197.5, -247.49) * mm});
            skPoint(sketch, "E19.0.10.8", {"position": v(195.5, -282.13) * mm});
            skLineSegment(sketch, "E19.1.10.8", {"start": v(204.5, -240.95) * mm, "end": v(204.5, -280.13) * mm});
            skPoint(sketch, "E19.4.10.8", {"position": v(204.5, -282.13) * mm});
            skLineSegment(sketch, "E19.5.10.8", {"start": v(195.5, -240.95) * mm, "end": v(204.5, -240.95) * mm});
            skLineSegment(sketch, "E19.8.10.8", {"start": v(197.5, -282.13) * mm, "end": v(202.5, -282.13) * mm});
            skLineSegment(sketch, "E19.11.10.8", {"start": v(195.5, -240.95) * mm, "end": v(195.5, -280.13) * mm});
            skArc(sketch, "E19.14.10.8", {"start": v(202.5, -282.13) * mm, "mid": v(203.91, -281.54) * mm, "end": v(204.5, -280.13) * mm});
            skArc(sketch, "E19.18.10.8", {"start": v(195.5, -280.13) * mm, "mid": v(196.09, -281.54) * mm, "end": v(197.5, -282.13) * mm});
            skPoint(sketch, "E19.0.10.9", {"position": v(195.5, -316.77) * mm});
            skLineSegment(sketch, "E19.1.10.9", {"start": v(204.5, -275.6) * mm, "end": v(204.5, -314.77) * mm});
            skPoint(sketch, "E19.4.10.9", {"position": v(204.5, -316.77) * mm});
            skLineSegment(sketch, "E19.5.10.9", {"start": v(195.5, -275.6) * mm, "end": v(204.5, -275.6) * mm});
            skLineSegment(sketch, "E19.8.10.9", {"start": v(197.5, -316.77) * mm, "end": v(202.5, -316.77) * mm});
            skLineSegment(sketch, "E19.11.10.9", {"start": v(195.5, -275.6) * mm, "end": v(195.5, -314.77) * mm});
            skArc(sketch, "E19.14.10.9", {"start": v(202.5, -316.77) * mm, "mid": v(203.91, -316.18) * mm, "end": v(204.5, -314.77) * mm});
            skArc(sketch, "E19.18.10.9", {"start": v(195.5, -314.77) * mm, "mid": v(196.09, -316.18) * mm, "end": v(197.5, -316.77) * mm});
            skPoint(sketch, "E19.0.10.10", {"position": v(195.5, -351.41) * mm});
            skLineSegment(sketch, "E19.1.10.10", {"start": v(204.5, -310.24) * mm, "end": v(204.5, -349.41) * mm});
            skPoint(sketch, "E19.4.10.10", {"position": v(204.5, -351.41) * mm});
            skLineSegment(sketch, "E19.5.10.10", {"start": v(195.5, -310.24) * mm, "end": v(204.5, -310.24) * mm});
            skLineSegment(sketch, "E19.8.10.10", {"start": v(197.5, -351.41) * mm, "end": v(202.5, -351.41) * mm});
            skLineSegment(sketch, "E19.11.10.10", {"start": v(195.5, -310.24) * mm, "end": v(195.5, -349.41) * mm});
            skArc(sketch, "E19.14.10.10", {"start": v(202.5, -351.41) * mm, "mid": v(203.91, -350.82) * mm, "end": v(204.5, -349.41) * mm});
            skArc(sketch, "E19.18.10.10", {"start": v(195.5, -349.41) * mm, "mid": v(196.09, -350.82) * mm, "end": v(197.5, -351.41) * mm});
            skPoint(sketch, "E19.0.10.11", {"position": v(195.5, -386.05) * mm});
            skLineSegment(sketch, "E19.1.10.11", {"start": v(204.5, -344.88) * mm, "end": v(204.5, -384.05) * mm});
            skPoint(sketch, "E19.4.10.11", {"position": v(204.5, -386.05) * mm});
            skLineSegment(sketch, "E19.5.10.11", {"start": v(195.5, -344.88) * mm, "end": v(204.5, -344.88) * mm});
            skLineSegment(sketch, "E19.8.10.11", {"start": v(197.5, -386.05) * mm, "end": v(202.5, -386.05) * mm});
            skLineSegment(sketch, "E19.11.10.11", {"start": v(195.5, -344.88) * mm, "end": v(195.5, -384.05) * mm});
            skArc(sketch, "E19.14.10.11", {"start": v(202.5, -386.05) * mm, "mid": v(203.91, -385.47) * mm, "end": v(204.5, -384.05) * mm});
            skArc(sketch, "E19.18.10.11", {"start": v(195.5, -384.05) * mm, "mid": v(196.09, -385.47) * mm, "end": v(197.5, -386.05) * mm});
            skPoint(sketch, "E19.0.10.12", {"position": v(195.5, -420.7) * mm});
            skLineSegment(sketch, "E19.1.10.12", {"start": v(204.5, -379.52) * mm, "end": v(204.5, -418.7) * mm});
            skPoint(sketch, "E19.4.10.12", {"position": v(204.5, -420.7) * mm});
            skLineSegment(sketch, "E19.5.10.12", {"start": v(195.5, -379.52) * mm, "end": v(204.5, -379.52) * mm});
            skLineSegment(sketch, "E19.8.10.12", {"start": v(197.5, -420.7) * mm, "end": v(202.5, -420.7) * mm});
            skLineSegment(sketch, "E19.11.10.12", {"start": v(195.5, -379.52) * mm, "end": v(195.5, -418.7) * mm});
            skArc(sketch, "E19.14.10.12", {"start": v(202.5, -420.7) * mm, "mid": v(203.91, -420.1) * mm, "end": v(204.5, -418.7) * mm});
            skArc(sketch, "E19.18.10.12", {"start": v(195.5, -418.7) * mm, "mid": v(196.09, -420.1) * mm, "end": v(197.5, -420.7) * mm});
            skPoint(sketch, "E19.0.10.13", {"position": v(195.5, -455.33) * mm});
            skLineSegment(sketch, "E19.1.10.13", {"start": v(204.5, -414.16) * mm, "end": v(204.5, -453.33) * mm});
            skPoint(sketch, "E19.4.10.13", {"position": v(204.5, -455.33) * mm});
            skLineSegment(sketch, "E19.5.10.13", {"start": v(195.5, -414.16) * mm, "end": v(204.5, -414.16) * mm});
            skLineSegment(sketch, "E19.8.10.13", {"start": v(197.5, -455.33) * mm, "end": v(202.5, -455.33) * mm});
            skLineSegment(sketch, "E19.11.10.13", {"start": v(195.5, -414.16) * mm, "end": v(195.5, -453.33) * mm});
            skArc(sketch, "E19.14.10.13", {"start": v(202.5, -455.33) * mm, "mid": v(203.91, -454.75) * mm, "end": v(204.5, -453.33) * mm});
            skArc(sketch, "E19.18.10.13", {"start": v(195.5, -453.33) * mm, "mid": v(196.09, -454.75) * mm, "end": v(197.5, -455.33) * mm});
            skPoint(sketch, "E19.0.10.14", {"position": v(195.5, -489.97) * mm});
            skLineSegment(sketch, "E19.1.10.14", {"start": v(204.5, -448.8) * mm, "end": v(204.5, -487.97) * mm});
            skPoint(sketch, "E19.4.10.14", {"position": v(204.5, -489.97) * mm});
            skLineSegment(sketch, "E19.5.10.14", {"start": v(195.5, -448.8) * mm, "end": v(204.5, -448.8) * mm});
            skLineSegment(sketch, "E19.8.10.14", {"start": v(197.5, -489.97) * mm, "end": v(202.5, -489.97) * mm});
            skLineSegment(sketch, "E19.11.10.14", {"start": v(195.5, -448.8) * mm, "end": v(195.5, -487.97) * mm});
            skArc(sketch, "E19.14.10.14", {"start": v(202.5, -489.97) * mm, "mid": v(203.91, -489.39) * mm, "end": v(204.5, -487.97) * mm});
            skArc(sketch, "E19.18.10.14", {"start": v(195.5, -487.97) * mm, "mid": v(196.09, -489.39) * mm, "end": v(197.5, -489.97) * mm});
            skPoint(sketch, "E19.0.11.0", {"position": v(215.5, -5) * mm});
            skLineSegment(sketch, "E19.1.11.0", {"start": v(224.5, 36.17) * mm, "end": v(224.5, -3) * mm});
            skPoint(sketch, "E19.4.11.0", {"position": v(224.5, -5) * mm});
            skLineSegment(sketch, "E19.5.11.0", {"start": v(215.5, 36.17) * mm, "end": v(224.5, 36.17) * mm});
            skLineSegment(sketch, "E19.8.11.0", {"start": v(217.5, -5) * mm, "end": v(222.5, -5) * mm});
            skLineSegment(sketch, "E19.11.11.0", {"start": v(215.5, 36.17) * mm, "end": v(215.5, -3) * mm});
            skArc(sketch, "E19.14.11.0", {"start": v(222.5, -5) * mm, "mid": v(223.91, -4.41) * mm, "end": v(224.5, -3) * mm});
            skArc(sketch, "E19.18.11.0", {"start": v(215.5, -3) * mm, "mid": v(216.09, -4.41) * mm, "end": v(217.5, -5) * mm});
            skPoint(sketch, "E19.0.11.1", {"position": v(215.5, -39.64) * mm});
            skLineSegment(sketch, "E19.1.11.1", {"start": v(224.5, 1.53) * mm, "end": v(224.5, -37.64) * mm});
            skPoint(sketch, "E19.4.11.1", {"position": v(224.5, -39.64) * mm});
            skLineSegment(sketch, "E19.5.11.1", {"start": v(215.5, 1.53) * mm, "end": v(224.5, 1.53) * mm});
            skLineSegment(sketch, "E19.8.11.1", {"start": v(217.5, -39.64) * mm, "end": v(222.5, -39.64) * mm});
            skLineSegment(sketch, "E19.11.11.1", {"start": v(215.5, 1.53) * mm, "end": v(215.5, -37.64) * mm});
            skArc(sketch, "E19.14.11.1", {"start": v(222.5, -39.64) * mm, "mid": v(223.91, -39.06) * mm, "end": v(224.5, -37.64) * mm});
            skArc(sketch, "E19.18.11.1", {"start": v(215.5, -37.64) * mm, "mid": v(216.09, -39.06) * mm, "end": v(217.5, -39.64) * mm});
            skPoint(sketch, "E19.0.11.2", {"position": v(215.5, -74.28) * mm});
            skLineSegment(sketch, "E19.1.11.2", {"start": v(224.5, -33.1) * mm, "end": v(224.5, -72.28) * mm});
            skPoint(sketch, "E19.4.11.2", {"position": v(224.5, -74.28) * mm});
            skLineSegment(sketch, "E19.5.11.2", {"start": v(215.5, -33.1) * mm, "end": v(224.5, -33.1) * mm});
            skLineSegment(sketch, "E19.8.11.2", {"start": v(217.5, -74.28) * mm, "end": v(222.5, -74.28) * mm});
            skLineSegment(sketch, "E19.11.11.2", {"start": v(215.5, -33.1) * mm, "end": v(215.5, -72.28) * mm});
            skArc(sketch, "E19.14.11.2", {"start": v(222.5, -74.28) * mm, "mid": v(223.91, -73.7) * mm, "end": v(224.5, -72.28) * mm});
            skArc(sketch, "E19.18.11.2", {"start": v(215.5, -72.28) * mm, "mid": v(216.09, -73.7) * mm, "end": v(217.5, -74.28) * mm});
            skPoint(sketch, "E19.0.11.3", {"position": v(215.5, -108.92) * mm});
            skLineSegment(sketch, "E19.1.11.3", {"start": v(224.5, -67.75) * mm, "end": v(224.5, -106.92) * mm});
            skPoint(sketch, "E19.4.11.3", {"position": v(224.5, -108.92) * mm});
            skLineSegment(sketch, "E19.5.11.3", {"start": v(215.5, -67.75) * mm, "end": v(224.5, -67.75) * mm});
            skLineSegment(sketch, "E19.8.11.3", {"start": v(217.5, -108.92) * mm, "end": v(222.5, -108.92) * mm});
            skLineSegment(sketch, "E19.11.11.3", {"start": v(215.5, -67.75) * mm, "end": v(215.5, -106.92) * mm});
            skArc(sketch, "E19.14.11.3", {"start": v(222.5, -108.92) * mm, "mid": v(223.91, -108.34) * mm, "end": v(224.5, -106.92) * mm});
            skArc(sketch, "E19.18.11.3", {"start": v(215.5, -106.92) * mm, "mid": v(216.09, -108.34) * mm, "end": v(217.5, -108.92) * mm});
            skPoint(sketch, "E19.0.11.4", {"position": v(215.5, -143.56) * mm});
            skLineSegment(sketch, "E19.1.11.4", {"start": v(224.5, -102.4) * mm, "end": v(224.5, -141.56) * mm});
            skPoint(sketch, "E19.4.11.4", {"position": v(224.5, -143.56) * mm});
            skLineSegment(sketch, "E19.5.11.4", {"start": v(215.5, -102.4) * mm, "end": v(224.5, -102.4) * mm});
            skLineSegment(sketch, "E19.8.11.4", {"start": v(217.5, -143.56) * mm, "end": v(222.5, -143.56) * mm});
            skLineSegment(sketch, "E19.11.11.4", {"start": v(215.5, -102.4) * mm, "end": v(215.5, -141.56) * mm});
            skArc(sketch, "E19.14.11.4", {"start": v(222.5, -143.56) * mm, "mid": v(223.91, -142.98) * mm, "end": v(224.5, -141.56) * mm});
            skArc(sketch, "E19.18.11.4", {"start": v(215.5, -141.56) * mm, "mid": v(216.09, -142.98) * mm, "end": v(217.5, -143.56) * mm});
            skPoint(sketch, "E19.0.11.5", {"position": v(215.5, -178.2) * mm});
            skLineSegment(sketch, "E19.1.11.5", {"start": v(224.5, -137.03) * mm, "end": v(224.5, -176.2) * mm});
            skPoint(sketch, "E19.4.11.5", {"position": v(224.5, -178.2) * mm});
            skLineSegment(sketch, "E19.5.11.5", {"start": v(215.5, -137.03) * mm, "end": v(224.5, -137.03) * mm});
            skLineSegment(sketch, "E19.8.11.5", {"start": v(217.5, -178.2) * mm, "end": v(222.5, -178.2) * mm});
            skLineSegment(sketch, "E19.11.11.5", {"start": v(215.5, -137.03) * mm, "end": v(215.5, -176.2) * mm});
            skArc(sketch, "E19.14.11.5", {"start": v(222.5, -178.2) * mm, "mid": v(223.91, -177.62) * mm, "end": v(224.5, -176.2) * mm});
            skArc(sketch, "E19.18.11.5", {"start": v(215.5, -176.2) * mm, "mid": v(216.09, -177.62) * mm, "end": v(217.5, -178.2) * mm});
            skPoint(sketch, "E19.0.11.6", {"position": v(215.5, -212.85) * mm});
            skLineSegment(sketch, "E19.1.11.6", {"start": v(224.5, -171.67) * mm, "end": v(224.5, -210.85) * mm});
            skPoint(sketch, "E19.4.11.6", {"position": v(224.5, -212.85) * mm});
            skLineSegment(sketch, "E19.5.11.6", {"start": v(215.5, -171.67) * mm, "end": v(224.5, -171.67) * mm});
            skLineSegment(sketch, "E19.8.11.6", {"start": v(217.5, -212.85) * mm, "end": v(222.5, -212.85) * mm});
            skLineSegment(sketch, "E19.11.11.6", {"start": v(215.5, -171.67) * mm, "end": v(215.5, -210.85) * mm});
            skArc(sketch, "E19.14.11.6", {"start": v(222.5, -212.85) * mm, "mid": v(223.91, -212.26) * mm, "end": v(224.5, -210.85) * mm});
            skArc(sketch, "E19.18.11.6", {"start": v(215.5, -210.85) * mm, "mid": v(216.09, -212.26) * mm, "end": v(217.5, -212.85) * mm});
            skPoint(sketch, "E19.0.11.7", {"position": v(215.5, -247.49) * mm});
            skLineSegment(sketch, "E19.1.11.7", {"start": v(224.5, -206.31) * mm, "end": v(224.5, -245.49) * mm});
            skPoint(sketch, "E19.4.11.7", {"position": v(224.5, -247.49) * mm});
            skLineSegment(sketch, "E19.5.11.7", {"start": v(215.5, -206.31) * mm, "end": v(224.5, -206.31) * mm});
            skLineSegment(sketch, "E19.8.11.7", {"start": v(217.5, -247.49) * mm, "end": v(222.5, -247.49) * mm});
            skLineSegment(sketch, "E19.11.11.7", {"start": v(215.5, -206.31) * mm, "end": v(215.5, -245.49) * mm});
            skArc(sketch, "E19.14.11.7", {"start": v(222.5, -247.49) * mm, "mid": v(223.91, -246.9) * mm, "end": v(224.5, -245.49) * mm});
            skArc(sketch, "E19.18.11.7", {"start": v(215.5, -245.49) * mm, "mid": v(216.09, -246.9) * mm, "end": v(217.5, -247.49) * mm});
            skPoint(sketch, "E19.0.11.8", {"position": v(215.5, -282.13) * mm});
            skLineSegment(sketch, "E19.1.11.8", {"start": v(224.5, -240.95) * mm, "end": v(224.5, -280.13) * mm});
            skPoint(sketch, "E19.4.11.8", {"position": v(224.5, -282.13) * mm});
            skLineSegment(sketch, "E19.5.11.8", {"start": v(215.5, -240.95) * mm, "end": v(224.5, -240.95) * mm});
            skLineSegment(sketch, "E19.8.11.8", {"start": v(217.5, -282.13) * mm, "end": v(222.5, -282.13) * mm});
            skLineSegment(sketch, "E19.11.11.8", {"start": v(215.5, -240.95) * mm, "end": v(215.5, -280.13) * mm});
            skArc(sketch, "E19.14.11.8", {"start": v(222.5, -282.13) * mm, "mid": v(223.91, -281.54) * mm, "end": v(224.5, -280.13) * mm});
            skArc(sketch, "E19.18.11.8", {"start": v(215.5, -280.13) * mm, "mid": v(216.09, -281.54) * mm, "end": v(217.5, -282.13) * mm});
            skPoint(sketch, "E19.0.11.9", {"position": v(215.5, -316.77) * mm});
            skLineSegment(sketch, "E19.1.11.9", {"start": v(224.5, -275.6) * mm, "end": v(224.5, -314.77) * mm});
            skPoint(sketch, "E19.4.11.9", {"position": v(224.5, -316.77) * mm});
            skLineSegment(sketch, "E19.5.11.9", {"start": v(215.5, -275.6) * mm, "end": v(224.5, -275.6) * mm});
            skLineSegment(sketch, "E19.8.11.9", {"start": v(217.5, -316.77) * mm, "end": v(222.5, -316.77) * mm});
            skLineSegment(sketch, "E19.11.11.9", {"start": v(215.5, -275.6) * mm, "end": v(215.5, -314.77) * mm});
            skArc(sketch, "E19.14.11.9", {"start": v(222.5, -316.77) * mm, "mid": v(223.91, -316.18) * mm, "end": v(224.5, -314.77) * mm});
            skArc(sketch, "E19.18.11.9", {"start": v(215.5, -314.77) * mm, "mid": v(216.09, -316.18) * mm, "end": v(217.5, -316.77) * mm});
            skPoint(sketch, "E19.0.11.10", {"position": v(215.5, -351.41) * mm});
            skLineSegment(sketch, "E19.1.11.10", {"start": v(224.5, -310.24) * mm, "end": v(224.5, -349.41) * mm});
            skPoint(sketch, "E19.4.11.10", {"position": v(224.5, -351.41) * mm});
            skLineSegment(sketch, "E19.5.11.10", {"start": v(215.5, -310.24) * mm, "end": v(224.5, -310.24) * mm});
            skLineSegment(sketch, "E19.8.11.10", {"start": v(217.5, -351.41) * mm, "end": v(222.5, -351.41) * mm});
            skLineSegment(sketch, "E19.11.11.10", {"start": v(215.5, -310.24) * mm, "end": v(215.5, -349.41) * mm});
            skArc(sketch, "E19.14.11.10", {"start": v(222.5, -351.41) * mm, "mid": v(223.91, -350.82) * mm, "end": v(224.5, -349.41) * mm});
            skArc(sketch, "E19.18.11.10", {"start": v(215.5, -349.41) * mm, "mid": v(216.09, -350.82) * mm, "end": v(217.5, -351.41) * mm});
            skPoint(sketch, "E19.0.11.11", {"position": v(215.5, -386.05) * mm});
            skLineSegment(sketch, "E19.1.11.11", {"start": v(224.5, -344.88) * mm, "end": v(224.5, -384.05) * mm});
            skPoint(sketch, "E19.4.11.11", {"position": v(224.5, -386.05) * mm});
            skLineSegment(sketch, "E19.5.11.11", {"start": v(215.5, -344.88) * mm, "end": v(224.5, -344.88) * mm});
            skLineSegment(sketch, "E19.8.11.11", {"start": v(217.5, -386.05) * mm, "end": v(222.5, -386.05) * mm});
            skLineSegment(sketch, "E19.11.11.11", {"start": v(215.5, -344.88) * mm, "end": v(215.5, -384.05) * mm});
            skArc(sketch, "E19.14.11.11", {"start": v(222.5, -386.05) * mm, "mid": v(223.91, -385.47) * mm, "end": v(224.5, -384.05) * mm});
            skArc(sketch, "E19.18.11.11", {"start": v(215.5, -384.05) * mm, "mid": v(216.09, -385.47) * mm, "end": v(217.5, -386.05) * mm});
            skPoint(sketch, "E19.0.11.12", {"position": v(215.5, -420.7) * mm});
            skLineSegment(sketch, "E19.1.11.12", {"start": v(224.5, -379.52) * mm, "end": v(224.5, -418.7) * mm});
            skPoint(sketch, "E19.4.11.12", {"position": v(224.5, -420.7) * mm});
            skLineSegment(sketch, "E19.5.11.12", {"start": v(215.5, -379.52) * mm, "end": v(224.5, -379.52) * mm});
            skLineSegment(sketch, "E19.8.11.12", {"start": v(217.5, -420.7) * mm, "end": v(222.5, -420.7) * mm});
            skLineSegment(sketch, "E19.11.11.12", {"start": v(215.5, -379.52) * mm, "end": v(215.5, -418.7) * mm});
            skArc(sketch, "E19.14.11.12", {"start": v(222.5, -420.7) * mm, "mid": v(223.91, -420.1) * mm, "end": v(224.5, -418.7) * mm});
            skArc(sketch, "E19.18.11.12", {"start": v(215.5, -418.7) * mm, "mid": v(216.09, -420.1) * mm, "end": v(217.5, -420.7) * mm});
            skPoint(sketch, "E19.0.11.13", {"position": v(215.5, -455.33) * mm});
            skLineSegment(sketch, "E19.1.11.13", {"start": v(224.5, -414.16) * mm, "end": v(224.5, -453.33) * mm});
            skPoint(sketch, "E19.4.11.13", {"position": v(224.5, -455.33) * mm});
            skLineSegment(sketch, "E19.5.11.13", {"start": v(215.5, -414.16) * mm, "end": v(224.5, -414.16) * mm});
            skLineSegment(sketch, "E19.8.11.13", {"start": v(217.5, -455.33) * mm, "end": v(222.5, -455.33) * mm});
            skLineSegment(sketch, "E19.11.11.13", {"start": v(215.5, -414.16) * mm, "end": v(215.5, -453.33) * mm});
            skArc(sketch, "E19.14.11.13", {"start": v(222.5, -455.33) * mm, "mid": v(223.91, -454.75) * mm, "end": v(224.5, -453.33) * mm});
            skArc(sketch, "E19.18.11.13", {"start": v(215.5, -453.33) * mm, "mid": v(216.09, -454.75) * mm, "end": v(217.5, -455.33) * mm});
            skPoint(sketch, "E19.0.11.14", {"position": v(215.5, -489.97) * mm});
            skLineSegment(sketch, "E19.1.11.14", {"start": v(224.5, -448.8) * mm, "end": v(224.5, -487.97) * mm});
            skPoint(sketch, "E19.4.11.14", {"position": v(224.5, -489.97) * mm});
            skLineSegment(sketch, "E19.5.11.14", {"start": v(215.5, -448.8) * mm, "end": v(224.5, -448.8) * mm});
            skLineSegment(sketch, "E19.8.11.14", {"start": v(217.5, -489.97) * mm, "end": v(222.5, -489.97) * mm});
            skLineSegment(sketch, "E19.11.11.14", {"start": v(215.5, -448.8) * mm, "end": v(215.5, -487.97) * mm});
            skArc(sketch, "E19.14.11.14", {"start": v(222.5, -489.97) * mm, "mid": v(223.91, -489.39) * mm, "end": v(224.5, -487.97) * mm});
            skArc(sketch, "E19.18.11.14", {"start": v(215.5, -487.97) * mm, "mid": v(216.09, -489.39) * mm, "end": v(217.5, -489.97) * mm});
            skPoint(sketch, "E19.0.12.0", {"position": v(235.5, -5) * mm});
            skLineSegment(sketch, "E19.1.12.0", {"start": v(244.5, 36.17) * mm, "end": v(244.5, -3) * mm});
            skPoint(sketch, "E19.4.12.0", {"position": v(244.5, -5) * mm});
            skLineSegment(sketch, "E19.5.12.0", {"start": v(235.5, 36.17) * mm, "end": v(244.5, 36.17) * mm});
            skLineSegment(sketch, "E19.8.12.0", {"start": v(237.5, -5) * mm, "end": v(242.5, -5) * mm});
            skLineSegment(sketch, "E19.11.12.0", {"start": v(235.5, 36.17) * mm, "end": v(235.5, -3) * mm});
            skArc(sketch, "E19.14.12.0", {"start": v(242.5, -5) * mm, "mid": v(243.91, -4.41) * mm, "end": v(244.5, -3) * mm});
            skArc(sketch, "E19.18.12.0", {"start": v(235.5, -3) * mm, "mid": v(236.09, -4.41) * mm, "end": v(237.5, -5) * mm});
            skPoint(sketch, "E19.0.12.1", {"position": v(235.5, -39.64) * mm});
            skLineSegment(sketch, "E19.1.12.1", {"start": v(244.5, 1.53) * mm, "end": v(244.5, -37.64) * mm});
            skPoint(sketch, "E19.4.12.1", {"position": v(244.5, -39.64) * mm});
            skLineSegment(sketch, "E19.5.12.1", {"start": v(235.5, 1.53) * mm, "end": v(244.5, 1.53) * mm});
            skLineSegment(sketch, "E19.8.12.1", {"start": v(237.5, -39.64) * mm, "end": v(242.5, -39.64) * mm});
            skLineSegment(sketch, "E19.11.12.1", {"start": v(235.5, 1.53) * mm, "end": v(235.5, -37.64) * mm});
            skArc(sketch, "E19.14.12.1", {"start": v(242.5, -39.64) * mm, "mid": v(243.91, -39.06) * mm, "end": v(244.5, -37.64) * mm});
            skArc(sketch, "E19.18.12.1", {"start": v(235.5, -37.64) * mm, "mid": v(236.09, -39.06) * mm, "end": v(237.5, -39.64) * mm});
            skPoint(sketch, "E19.0.12.2", {"position": v(235.5, -74.28) * mm});
            skLineSegment(sketch, "E19.1.12.2", {"start": v(244.5, -33.1) * mm, "end": v(244.5, -72.28) * mm});
            skPoint(sketch, "E19.4.12.2", {"position": v(244.5, -74.28) * mm});
            skLineSegment(sketch, "E19.5.12.2", {"start": v(235.5, -33.1) * mm, "end": v(244.5, -33.1) * mm});
            skLineSegment(sketch, "E19.8.12.2", {"start": v(237.5, -74.28) * mm, "end": v(242.5, -74.28) * mm});
            skLineSegment(sketch, "E19.11.12.2", {"start": v(235.5, -33.1) * mm, "end": v(235.5, -72.28) * mm});
            skArc(sketch, "E19.14.12.2", {"start": v(242.5, -74.28) * mm, "mid": v(243.91, -73.7) * mm, "end": v(244.5, -72.28) * mm});
            skArc(sketch, "E19.18.12.2", {"start": v(235.5, -72.28) * mm, "mid": v(236.09, -73.7) * mm, "end": v(237.5, -74.28) * mm});
            skPoint(sketch, "E19.0.12.3", {"position": v(235.5, -108.92) * mm});
            skLineSegment(sketch, "E19.1.12.3", {"start": v(244.5, -67.75) * mm, "end": v(244.5, -106.92) * mm});
            skPoint(sketch, "E19.4.12.3", {"position": v(244.5, -108.92) * mm});
            skLineSegment(sketch, "E19.5.12.3", {"start": v(235.5, -67.75) * mm, "end": v(244.5, -67.75) * mm});
            skLineSegment(sketch, "E19.8.12.3", {"start": v(237.5, -108.92) * mm, "end": v(242.5, -108.92) * mm});
            skLineSegment(sketch, "E19.11.12.3", {"start": v(235.5, -67.75) * mm, "end": v(235.5, -106.92) * mm});
            skArc(sketch, "E19.14.12.3", {"start": v(242.5, -108.92) * mm, "mid": v(243.91, -108.34) * mm, "end": v(244.5, -106.92) * mm});
            skArc(sketch, "E19.18.12.3", {"start": v(235.5, -106.92) * mm, "mid": v(236.09, -108.34) * mm, "end": v(237.5, -108.92) * mm});
            skPoint(sketch, "E19.0.12.4", {"position": v(235.5, -143.56) * mm});
            skLineSegment(sketch, "E19.1.12.4", {"start": v(244.5, -102.4) * mm, "end": v(244.5, -141.56) * mm});
            skPoint(sketch, "E19.4.12.4", {"position": v(244.5, -143.56) * mm});
            skLineSegment(sketch, "E19.5.12.4", {"start": v(235.5, -102.4) * mm, "end": v(244.5, -102.4) * mm});
            skLineSegment(sketch, "E19.8.12.4", {"start": v(237.5, -143.56) * mm, "end": v(242.5, -143.56) * mm});
            skLineSegment(sketch, "E19.11.12.4", {"start": v(235.5, -102.4) * mm, "end": v(235.5, -141.56) * mm});
            skArc(sketch, "E19.14.12.4", {"start": v(242.5, -143.56) * mm, "mid": v(243.91, -142.98) * mm, "end": v(244.5, -141.56) * mm});
            skArc(sketch, "E19.18.12.4", {"start": v(235.5, -141.56) * mm, "mid": v(236.09, -142.98) * mm, "end": v(237.5, -143.56) * mm});
            skPoint(sketch, "E19.0.12.5", {"position": v(235.5, -178.2) * mm});
            skLineSegment(sketch, "E19.1.12.5", {"start": v(244.5, -137.03) * mm, "end": v(244.5, -176.2) * mm});
            skPoint(sketch, "E19.4.12.5", {"position": v(244.5, -178.2) * mm});
            skLineSegment(sketch, "E19.5.12.5", {"start": v(235.5, -137.03) * mm, "end": v(244.5, -137.03) * mm});
            skLineSegment(sketch, "E19.8.12.5", {"start": v(237.5, -178.2) * mm, "end": v(242.5, -178.2) * mm});
            skLineSegment(sketch, "E19.11.12.5", {"start": v(235.5, -137.03) * mm, "end": v(235.5, -176.2) * mm});
            skArc(sketch, "E19.14.12.5", {"start": v(242.5, -178.2) * mm, "mid": v(243.91, -177.62) * mm, "end": v(244.5, -176.2) * mm});
            skArc(sketch, "E19.18.12.5", {"start": v(235.5, -176.2) * mm, "mid": v(236.09, -177.62) * mm, "end": v(237.5, -178.2) * mm});
            skPoint(sketch, "E19.0.12.6", {"position": v(235.5, -212.85) * mm});
            skLineSegment(sketch, "E19.1.12.6", {"start": v(244.5, -171.67) * mm, "end": v(244.5, -210.85) * mm});
            skPoint(sketch, "E19.4.12.6", {"position": v(244.5, -212.85) * mm});
            skLineSegment(sketch, "E19.5.12.6", {"start": v(235.5, -171.67) * mm, "end": v(244.5, -171.67) * mm});
            skLineSegment(sketch, "E19.8.12.6", {"start": v(237.5, -212.85) * mm, "end": v(242.5, -212.85) * mm});
            skLineSegment(sketch, "E19.11.12.6", {"start": v(235.5, -171.67) * mm, "end": v(235.5, -210.85) * mm});
            skArc(sketch, "E19.14.12.6", {"start": v(242.5, -212.85) * mm, "mid": v(243.91, -212.26) * mm, "end": v(244.5, -210.85) * mm});
            skArc(sketch, "E19.18.12.6", {"start": v(235.5, -210.85) * mm, "mid": v(236.09, -212.26) * mm, "end": v(237.5, -212.85) * mm});
            skPoint(sketch, "E19.0.12.7", {"position": v(235.5, -247.49) * mm});
            skLineSegment(sketch, "E19.1.12.7", {"start": v(244.5, -206.31) * mm, "end": v(244.5, -245.49) * mm});
            skPoint(sketch, "E19.4.12.7", {"position": v(244.5, -247.49) * mm});
            skLineSegment(sketch, "E19.5.12.7", {"start": v(235.5, -206.31) * mm, "end": v(244.5, -206.31) * mm});
            skLineSegment(sketch, "E19.8.12.7", {"start": v(237.5, -247.49) * mm, "end": v(242.5, -247.49) * mm});
            skLineSegment(sketch, "E19.11.12.7", {"start": v(235.5, -206.31) * mm, "end": v(235.5, -245.49) * mm});
            skArc(sketch, "E19.14.12.7", {"start": v(242.5, -247.49) * mm, "mid": v(243.91, -246.9) * mm, "end": v(244.5, -245.49) * mm});
            skArc(sketch, "E19.18.12.7", {"start": v(235.5, -245.49) * mm, "mid": v(236.09, -246.9) * mm, "end": v(237.5, -247.49) * mm});
            skPoint(sketch, "E19.0.12.8", {"position": v(235.5, -282.13) * mm});
            skLineSegment(sketch, "E19.1.12.8", {"start": v(244.5, -240.95) * mm, "end": v(244.5, -280.13) * mm});
            skPoint(sketch, "E19.4.12.8", {"position": v(244.5, -282.13) * mm});
            skLineSegment(sketch, "E19.5.12.8", {"start": v(235.5, -240.95) * mm, "end": v(244.5, -240.95) * mm});
            skLineSegment(sketch, "E19.8.12.8", {"start": v(237.5, -282.13) * mm, "end": v(242.5, -282.13) * mm});
            skLineSegment(sketch, "E19.11.12.8", {"start": v(235.5, -240.95) * mm, "end": v(235.5, -280.13) * mm});
            skArc(sketch, "E19.14.12.8", {"start": v(242.5, -282.13) * mm, "mid": v(243.91, -281.54) * mm, "end": v(244.5, -280.13) * mm});
            skArc(sketch, "E19.18.12.8", {"start": v(235.5, -280.13) * mm, "mid": v(236.09, -281.54) * mm, "end": v(237.5, -282.13) * mm});
            skPoint(sketch, "E19.0.12.9", {"position": v(235.5, -316.77) * mm});
            skLineSegment(sketch, "E19.1.12.9", {"start": v(244.5, -275.6) * mm, "end": v(244.5, -314.77) * mm});
            skPoint(sketch, "E19.4.12.9", {"position": v(244.5, -316.77) * mm});
            skLineSegment(sketch, "E19.5.12.9", {"start": v(235.5, -275.6) * mm, "end": v(244.5, -275.6) * mm});
            skLineSegment(sketch, "E19.8.12.9", {"start": v(237.5, -316.77) * mm, "end": v(242.5, -316.77) * mm});
            skLineSegment(sketch, "E19.11.12.9", {"start": v(235.5, -275.6) * mm, "end": v(235.5, -314.77) * mm});
            skArc(sketch, "E19.14.12.9", {"start": v(242.5, -316.77) * mm, "mid": v(243.91, -316.18) * mm, "end": v(244.5, -314.77) * mm});
            skArc(sketch, "E19.18.12.9", {"start": v(235.5, -314.77) * mm, "mid": v(236.09, -316.18) * mm, "end": v(237.5, -316.77) * mm});
            skPoint(sketch, "E19.0.12.10", {"position": v(235.5, -351.41) * mm});
            skLineSegment(sketch, "E19.1.12.10", {"start": v(244.5, -310.24) * mm, "end": v(244.5, -349.41) * mm});
            skPoint(sketch, "E19.4.12.10", {"position": v(244.5, -351.41) * mm});
            skLineSegment(sketch, "E19.5.12.10", {"start": v(235.5, -310.24) * mm, "end": v(244.5, -310.24) * mm});
            skLineSegment(sketch, "E19.8.12.10", {"start": v(237.5, -351.41) * mm, "end": v(242.5, -351.41) * mm});
            skLineSegment(sketch, "E19.11.12.10", {"start": v(235.5, -310.24) * mm, "end": v(235.5, -349.41) * mm});
            skArc(sketch, "E19.14.12.10", {"start": v(242.5, -351.41) * mm, "mid": v(243.91, -350.82) * mm, "end": v(244.5, -349.41) * mm});
            skArc(sketch, "E19.18.12.10", {"start": v(235.5, -349.41) * mm, "mid": v(236.09, -350.82) * mm, "end": v(237.5, -351.41) * mm});
            skPoint(sketch, "E19.0.12.11", {"position": v(235.5, -386.05) * mm});
            skLineSegment(sketch, "E19.1.12.11", {"start": v(244.5, -344.88) * mm, "end": v(244.5, -384.05) * mm});
            skPoint(sketch, "E19.4.12.11", {"position": v(244.5, -386.05) * mm});
            skLineSegment(sketch, "E19.5.12.11", {"start": v(235.5, -344.88) * mm, "end": v(244.5, -344.88) * mm});
            skLineSegment(sketch, "E19.8.12.11", {"start": v(237.5, -386.05) * mm, "end": v(242.5, -386.05) * mm});
            skLineSegment(sketch, "E19.11.12.11", {"start": v(235.5, -344.88) * mm, "end": v(235.5, -384.05) * mm});
            skArc(sketch, "E19.14.12.11", {"start": v(242.5, -386.05) * mm, "mid": v(243.91, -385.47) * mm, "end": v(244.5, -384.05) * mm});
            skArc(sketch, "E19.18.12.11", {"start": v(235.5, -384.05) * mm, "mid": v(236.09, -385.47) * mm, "end": v(237.5, -386.05) * mm});
            skPoint(sketch, "E19.0.12.12", {"position": v(235.5, -420.7) * mm});
            skLineSegment(sketch, "E19.1.12.12", {"start": v(244.5, -379.52) * mm, "end": v(244.5, -418.7) * mm});
            skPoint(sketch, "E19.4.12.12", {"position": v(244.5, -420.7) * mm});
            skLineSegment(sketch, "E19.5.12.12", {"start": v(235.5, -379.52) * mm, "end": v(244.5, -379.52) * mm});
            skLineSegment(sketch, "E19.8.12.12", {"start": v(237.5, -420.7) * mm, "end": v(242.5, -420.7) * mm});
            skLineSegment(sketch, "E19.11.12.12", {"start": v(235.5, -379.52) * mm, "end": v(235.5, -418.7) * mm});
            skArc(sketch, "E19.14.12.12", {"start": v(242.5, -420.7) * mm, "mid": v(243.91, -420.1) * mm, "end": v(244.5, -418.7) * mm});
            skArc(sketch, "E19.18.12.12", {"start": v(235.5, -418.7) * mm, "mid": v(236.09, -420.1) * mm, "end": v(237.5, -420.7) * mm});
            skPoint(sketch, "E19.0.12.13", {"position": v(235.5, -455.33) * mm});
            skLineSegment(sketch, "E19.1.12.13", {"start": v(244.5, -414.16) * mm, "end": v(244.5, -453.33) * mm});
            skPoint(sketch, "E19.4.12.13", {"position": v(244.5, -455.33) * mm});
            skLineSegment(sketch, "E19.5.12.13", {"start": v(235.5, -414.16) * mm, "end": v(244.5, -414.16) * mm});
            skLineSegment(sketch, "E19.8.12.13", {"start": v(237.5, -455.33) * mm, "end": v(242.5, -455.33) * mm});
            skLineSegment(sketch, "E19.11.12.13", {"start": v(235.5, -414.16) * mm, "end": v(235.5, -453.33) * mm});
            skArc(sketch, "E19.14.12.13", {"start": v(242.5, -455.33) * mm, "mid": v(243.91, -454.75) * mm, "end": v(244.5, -453.33) * mm});
            skArc(sketch, "E19.18.12.13", {"start": v(235.5, -453.33) * mm, "mid": v(236.09, -454.75) * mm, "end": v(237.5, -455.33) * mm});
            skPoint(sketch, "E19.0.12.14", {"position": v(235.5, -489.97) * mm});
            skLineSegment(sketch, "E19.1.12.14", {"start": v(244.5, -448.8) * mm, "end": v(244.5, -487.97) * mm});
            skPoint(sketch, "E19.4.12.14", {"position": v(244.5, -489.97) * mm});
            skLineSegment(sketch, "E19.5.12.14", {"start": v(235.5, -448.8) * mm, "end": v(244.5, -448.8) * mm});
            skLineSegment(sketch, "E19.8.12.14", {"start": v(237.5, -489.97) * mm, "end": v(242.5, -489.97) * mm});
            skLineSegment(sketch, "E19.11.12.14", {"start": v(235.5, -448.8) * mm, "end": v(235.5, -487.97) * mm});
            skArc(sketch, "E19.14.12.14", {"start": v(242.5, -489.97) * mm, "mid": v(243.91, -489.39) * mm, "end": v(244.5, -487.97) * mm});
            skArc(sketch, "E19.18.12.14", {"start": v(235.5, -487.97) * mm, "mid": v(236.09, -489.39) * mm, "end": v(237.5, -489.97) * mm});
            skPoint(sketch, "E19.0.13.0", {"position": v(255.5, -5) * mm});
            skLineSegment(sketch, "E19.1.13.0", {"start": v(264.5, 36.17) * mm, "end": v(264.5, -3) * mm});
            skPoint(sketch, "E19.4.13.0", {"position": v(264.5, -5) * mm});
            skLineSegment(sketch, "E19.5.13.0", {"start": v(255.5, 36.17) * mm, "end": v(264.5, 36.17) * mm});
            skLineSegment(sketch, "E19.8.13.0", {"start": v(257.5, -5) * mm, "end": v(262.5, -5) * mm});
            skLineSegment(sketch, "E19.11.13.0", {"start": v(255.5, 36.17) * mm, "end": v(255.5, -3) * mm});
            skArc(sketch, "E19.14.13.0", {"start": v(262.5, -5) * mm, "mid": v(263.91, -4.41) * mm, "end": v(264.5, -3) * mm});
            skArc(sketch, "E19.18.13.0", {"start": v(255.5, -3) * mm, "mid": v(256.09, -4.41) * mm, "end": v(257.5, -5) * mm});
            skPoint(sketch, "E19.0.13.1", {"position": v(255.5, -39.64) * mm});
            skLineSegment(sketch, "E19.1.13.1", {"start": v(264.5, 1.53) * mm, "end": v(264.5, -37.64) * mm});
            skPoint(sketch, "E19.4.13.1", {"position": v(264.5, -39.64) * mm});
            skLineSegment(sketch, "E19.5.13.1", {"start": v(255.5, 1.53) * mm, "end": v(264.5, 1.53) * mm});
            skLineSegment(sketch, "E19.8.13.1", {"start": v(257.5, -39.64) * mm, "end": v(262.5, -39.64) * mm});
            skLineSegment(sketch, "E19.11.13.1", {"start": v(255.5, 1.53) * mm, "end": v(255.5, -37.64) * mm});
            skArc(sketch, "E19.14.13.1", {"start": v(262.5, -39.64) * mm, "mid": v(263.91, -39.06) * mm, "end": v(264.5, -37.64) * mm});
            skArc(sketch, "E19.18.13.1", {"start": v(255.5, -37.64) * mm, "mid": v(256.09, -39.06) * mm, "end": v(257.5, -39.64) * mm});
            skPoint(sketch, "E19.0.13.2", {"position": v(255.5, -74.28) * mm});
            skLineSegment(sketch, "E19.1.13.2", {"start": v(264.5, -33.1) * mm, "end": v(264.5, -72.28) * mm});
            skPoint(sketch, "E19.4.13.2", {"position": v(264.5, -74.28) * mm});
            skLineSegment(sketch, "E19.5.13.2", {"start": v(255.5, -33.1) * mm, "end": v(264.5, -33.1) * mm});
            skLineSegment(sketch, "E19.8.13.2", {"start": v(257.5, -74.28) * mm, "end": v(262.5, -74.28) * mm});
            skLineSegment(sketch, "E19.11.13.2", {"start": v(255.5, -33.1) * mm, "end": v(255.5, -72.28) * mm});
            skArc(sketch, "E19.14.13.2", {"start": v(262.5, -74.28) * mm, "mid": v(263.91, -73.7) * mm, "end": v(264.5, -72.28) * mm});
            skArc(sketch, "E19.18.13.2", {"start": v(255.5, -72.28) * mm, "mid": v(256.09, -73.7) * mm, "end": v(257.5, -74.28) * mm});
            skPoint(sketch, "E19.0.13.3", {"position": v(255.5, -108.92) * mm});
            skLineSegment(sketch, "E19.1.13.3", {"start": v(264.5, -67.75) * mm, "end": v(264.5, -106.92) * mm});
            skPoint(sketch, "E19.4.13.3", {"position": v(264.5, -108.92) * mm});
            skLineSegment(sketch, "E19.5.13.3", {"start": v(255.5, -67.75) * mm, "end": v(264.5, -67.75) * mm});
            skLineSegment(sketch, "E19.8.13.3", {"start": v(257.5, -108.92) * mm, "end": v(262.5, -108.92) * mm});
            skLineSegment(sketch, "E19.11.13.3", {"start": v(255.5, -67.75) * mm, "end": v(255.5, -106.92) * mm});
            skArc(sketch, "E19.14.13.3", {"start": v(262.5, -108.92) * mm, "mid": v(263.91, -108.34) * mm, "end": v(264.5, -106.92) * mm});
            skArc(sketch, "E19.18.13.3", {"start": v(255.5, -106.92) * mm, "mid": v(256.09, -108.34) * mm, "end": v(257.5, -108.92) * mm});
            skPoint(sketch, "E19.0.13.4", {"position": v(255.5, -143.56) * mm});
            skLineSegment(sketch, "E19.1.13.4", {"start": v(264.5, -102.4) * mm, "end": v(264.5, -141.56) * mm});
            skPoint(sketch, "E19.4.13.4", {"position": v(264.5, -143.56) * mm});
            skLineSegment(sketch, "E19.5.13.4", {"start": v(255.5, -102.4) * mm, "end": v(264.5, -102.4) * mm});
            skLineSegment(sketch, "E19.8.13.4", {"start": v(257.5, -143.56) * mm, "end": v(262.5, -143.56) * mm});
            skLineSegment(sketch, "E19.11.13.4", {"start": v(255.5, -102.4) * mm, "end": v(255.5, -141.56) * mm});
            skArc(sketch, "E19.14.13.4", {"start": v(262.5, -143.56) * mm, "mid": v(263.91, -142.98) * mm, "end": v(264.5, -141.56) * mm});
            skArc(sketch, "E19.18.13.4", {"start": v(255.5, -141.56) * mm, "mid": v(256.09, -142.98) * mm, "end": v(257.5, -143.56) * mm});
            skPoint(sketch, "E19.0.13.5", {"position": v(255.5, -178.2) * mm});
            skLineSegment(sketch, "E19.1.13.5", {"start": v(264.5, -137.03) * mm, "end": v(264.5, -176.2) * mm});
            skPoint(sketch, "E19.4.13.5", {"position": v(264.5, -178.2) * mm});
            skLineSegment(sketch, "E19.5.13.5", {"start": v(255.5, -137.03) * mm, "end": v(264.5, -137.03) * mm});
            skLineSegment(sketch, "E19.8.13.5", {"start": v(257.5, -178.2) * mm, "end": v(262.5, -178.2) * mm});
            skLineSegment(sketch, "E19.11.13.5", {"start": v(255.5, -137.03) * mm, "end": v(255.5, -176.2) * mm});
            skArc(sketch, "E19.14.13.5", {"start": v(262.5, -178.2) * mm, "mid": v(263.91, -177.62) * mm, "end": v(264.5, -176.2) * mm});
            skArc(sketch, "E19.18.13.5", {"start": v(255.5, -176.2) * mm, "mid": v(256.09, -177.62) * mm, "end": v(257.5, -178.2) * mm});
            skPoint(sketch, "E19.0.13.6", {"position": v(255.5, -212.85) * mm});
            skLineSegment(sketch, "E19.1.13.6", {"start": v(264.5, -171.67) * mm, "end": v(264.5, -210.85) * mm});
            skPoint(sketch, "E19.4.13.6", {"position": v(264.5, -212.85) * mm});
            skLineSegment(sketch, "E19.5.13.6", {"start": v(255.5, -171.67) * mm, "end": v(264.5, -171.67) * mm});
            skLineSegment(sketch, "E19.8.13.6", {"start": v(257.5, -212.85) * mm, "end": v(262.5, -212.85) * mm});
            skLineSegment(sketch, "E19.11.13.6", {"start": v(255.5, -171.67) * mm, "end": v(255.5, -210.85) * mm});
            skArc(sketch, "E19.14.13.6", {"start": v(262.5, -212.85) * mm, "mid": v(263.91, -212.26) * mm, "end": v(264.5, -210.85) * mm});
            skArc(sketch, "E19.18.13.6", {"start": v(255.5, -210.85) * mm, "mid": v(256.09, -212.26) * mm, "end": v(257.5, -212.85) * mm});
            skPoint(sketch, "E19.0.13.7", {"position": v(255.5, -247.49) * mm});
            skLineSegment(sketch, "E19.1.13.7", {"start": v(264.5, -206.31) * mm, "end": v(264.5, -245.49) * mm});
            skPoint(sketch, "E19.4.13.7", {"position": v(264.5, -247.49) * mm});
            skLineSegment(sketch, "E19.5.13.7", {"start": v(255.5, -206.31) * mm, "end": v(264.5, -206.31) * mm});
            skLineSegment(sketch, "E19.8.13.7", {"start": v(257.5, -247.49) * mm, "end": v(262.5, -247.49) * mm});
            skLineSegment(sketch, "E19.11.13.7", {"start": v(255.5, -206.31) * mm, "end": v(255.5, -245.49) * mm});
            skArc(sketch, "E19.14.13.7", {"start": v(262.5, -247.49) * mm, "mid": v(263.91, -246.9) * mm, "end": v(264.5, -245.49) * mm});
            skArc(sketch, "E19.18.13.7", {"start": v(255.5, -245.49) * mm, "mid": v(256.09, -246.9) * mm, "end": v(257.5, -247.49) * mm});
            skPoint(sketch, "E19.0.13.8", {"position": v(255.5, -282.13) * mm});
            skLineSegment(sketch, "E19.1.13.8", {"start": v(264.5, -240.95) * mm, "end": v(264.5, -280.13) * mm});
            skPoint(sketch, "E19.4.13.8", {"position": v(264.5, -282.13) * mm});
            skLineSegment(sketch, "E19.5.13.8", {"start": v(255.5, -240.95) * mm, "end": v(264.5, -240.95) * mm});
            skLineSegment(sketch, "E19.8.13.8", {"start": v(257.5, -282.13) * mm, "end": v(262.5, -282.13) * mm});
            skLineSegment(sketch, "E19.11.13.8", {"start": v(255.5, -240.95) * mm, "end": v(255.5, -280.13) * mm});
            skArc(sketch, "E19.14.13.8", {"start": v(262.5, -282.13) * mm, "mid": v(263.91, -281.54) * mm, "end": v(264.5, -280.13) * mm});
            skArc(sketch, "E19.18.13.8", {"start": v(255.5, -280.13) * mm, "mid": v(256.09, -281.54) * mm, "end": v(257.5, -282.13) * mm});
            skPoint(sketch, "E19.0.13.9", {"position": v(255.5, -316.77) * mm});
            skLineSegment(sketch, "E19.1.13.9", {"start": v(264.5, -275.6) * mm, "end": v(264.5, -314.77) * mm});
            skPoint(sketch, "E19.4.13.9", {"position": v(264.5, -316.77) * mm});
            skLineSegment(sketch, "E19.5.13.9", {"start": v(255.5, -275.6) * mm, "end": v(264.5, -275.6) * mm});
            skLineSegment(sketch, "E19.8.13.9", {"start": v(257.5, -316.77) * mm, "end": v(262.5, -316.77) * mm});
            skLineSegment(sketch, "E19.11.13.9", {"start": v(255.5, -275.6) * mm, "end": v(255.5, -314.77) * mm});
            skArc(sketch, "E19.14.13.9", {"start": v(262.5, -316.77) * mm, "mid": v(263.91, -316.18) * mm, "end": v(264.5, -314.77) * mm});
            skArc(sketch, "E19.18.13.9", {"start": v(255.5, -314.77) * mm, "mid": v(256.09, -316.18) * mm, "end": v(257.5, -316.77) * mm});
            skPoint(sketch, "E19.0.13.10", {"position": v(255.5, -351.41) * mm});
            skLineSegment(sketch, "E19.1.13.10", {"start": v(264.5, -310.24) * mm, "end": v(264.5, -349.41) * mm});
            skPoint(sketch, "E19.4.13.10", {"position": v(264.5, -351.41) * mm});
            skLineSegment(sketch, "E19.5.13.10", {"start": v(255.5, -310.24) * mm, "end": v(264.5, -310.24) * mm});
            skLineSegment(sketch, "E19.8.13.10", {"start": v(257.5, -351.41) * mm, "end": v(262.5, -351.41) * mm});
            skLineSegment(sketch, "E19.11.13.10", {"start": v(255.5, -310.24) * mm, "end": v(255.5, -349.41) * mm});
            skArc(sketch, "E19.14.13.10", {"start": v(262.5, -351.41) * mm, "mid": v(263.91, -350.82) * mm, "end": v(264.5, -349.41) * mm});
            skArc(sketch, "E19.18.13.10", {"start": v(255.5, -349.41) * mm, "mid": v(256.09, -350.82) * mm, "end": v(257.5, -351.41) * mm});
            skPoint(sketch, "E19.0.13.11", {"position": v(255.5, -386.05) * mm});
            skLineSegment(sketch, "E19.1.13.11", {"start": v(264.5, -344.88) * mm, "end": v(264.5, -384.05) * mm});
            skPoint(sketch, "E19.4.13.11", {"position": v(264.5, -386.05) * mm});
            skLineSegment(sketch, "E19.5.13.11", {"start": v(255.5, -344.88) * mm, "end": v(264.5, -344.88) * mm});
            skLineSegment(sketch, "E19.8.13.11", {"start": v(257.5, -386.05) * mm, "end": v(262.5, -386.05) * mm});
            skLineSegment(sketch, "E19.11.13.11", {"start": v(255.5, -344.88) * mm, "end": v(255.5, -384.05) * mm});
            skArc(sketch, "E19.14.13.11", {"start": v(262.5, -386.05) * mm, "mid": v(263.91, -385.47) * mm, "end": v(264.5, -384.05) * mm});
            skArc(sketch, "E19.18.13.11", {"start": v(255.5, -384.05) * mm, "mid": v(256.09, -385.47) * mm, "end": v(257.5, -386.05) * mm});
            skPoint(sketch, "E19.0.13.12", {"position": v(255.5, -420.7) * mm});
            skLineSegment(sketch, "E19.1.13.12", {"start": v(264.5, -379.52) * mm, "end": v(264.5, -418.7) * mm});
            skPoint(sketch, "E19.4.13.12", {"position": v(264.5, -420.7) * mm});
            skLineSegment(sketch, "E19.5.13.12", {"start": v(255.5, -379.52) * mm, "end": v(264.5, -379.52) * mm});
            skLineSegment(sketch, "E19.8.13.12", {"start": v(257.5, -420.7) * mm, "end": v(262.5, -420.7) * mm});
            skLineSegment(sketch, "E19.11.13.12", {"start": v(255.5, -379.52) * mm, "end": v(255.5, -418.7) * mm});
            skArc(sketch, "E19.14.13.12", {"start": v(262.5, -420.7) * mm, "mid": v(263.91, -420.1) * mm, "end": v(264.5, -418.7) * mm});
            skArc(sketch, "E19.18.13.12", {"start": v(255.5, -418.7) * mm, "mid": v(256.09, -420.1) * mm, "end": v(257.5, -420.7) * mm});
            skPoint(sketch, "E19.0.13.13", {"position": v(255.5, -455.33) * mm});
            skLineSegment(sketch, "E19.1.13.13", {"start": v(264.5, -414.16) * mm, "end": v(264.5, -453.33) * mm});
            skPoint(sketch, "E19.4.13.13", {"position": v(264.5, -455.33) * mm});
            skLineSegment(sketch, "E19.5.13.13", {"start": v(255.5, -414.16) * mm, "end": v(264.5, -414.16) * mm});
            skLineSegment(sketch, "E19.8.13.13", {"start": v(257.5, -455.33) * mm, "end": v(262.5, -455.33) * mm});
            skLineSegment(sketch, "E19.11.13.13", {"start": v(255.5, -414.16) * mm, "end": v(255.5, -453.33) * mm});
            skArc(sketch, "E19.14.13.13", {"start": v(262.5, -455.33) * mm, "mid": v(263.91, -454.75) * mm, "end": v(264.5, -453.33) * mm});
            skArc(sketch, "E19.18.13.13", {"start": v(255.5, -453.33) * mm, "mid": v(256.09, -454.75) * mm, "end": v(257.5, -455.33) * mm});
            skPoint(sketch, "E19.0.13.14", {"position": v(255.5, -489.97) * mm});
            skLineSegment(sketch, "E19.1.13.14", {"start": v(264.5, -448.8) * mm, "end": v(264.5, -487.97) * mm});
            skPoint(sketch, "E19.4.13.14", {"position": v(264.5, -489.97) * mm});
            skLineSegment(sketch, "E19.5.13.14", {"start": v(255.5, -448.8) * mm, "end": v(264.5, -448.8) * mm});
            skLineSegment(sketch, "E19.8.13.14", {"start": v(257.5, -489.97) * mm, "end": v(262.5, -489.97) * mm});
            skLineSegment(sketch, "E19.11.13.14", {"start": v(255.5, -448.8) * mm, "end": v(255.5, -487.97) * mm});
            skArc(sketch, "E19.14.13.14", {"start": v(262.5, -489.97) * mm, "mid": v(263.91, -489.39) * mm, "end": v(264.5, -487.97) * mm});
            skArc(sketch, "E19.18.13.14", {"start": v(255.5, -487.97) * mm, "mid": v(256.09, -489.39) * mm, "end": v(257.5, -489.97) * mm});
            skPoint(sketch, "E19.0.14.0", {"position": v(275.5, -5) * mm});
            skLineSegment(sketch, "E19.1.14.0", {"start": v(284.5, 36.17) * mm, "end": v(284.5, -3) * mm});
            skPoint(sketch, "E19.4.14.0", {"position": v(284.5, -5) * mm});
            skLineSegment(sketch, "E19.5.14.0", {"start": v(275.5, 36.17) * mm, "end": v(284.5, 36.17) * mm});
            skLineSegment(sketch, "E19.8.14.0", {"start": v(277.5, -5) * mm, "end": v(282.5, -5) * mm});
            skLineSegment(sketch, "E19.11.14.0", {"start": v(275.5, 36.17) * mm, "end": v(275.5, -3) * mm});
            skArc(sketch, "E19.14.14.0", {"start": v(282.5, -5) * mm, "mid": v(283.91, -4.41) * mm, "end": v(284.5, -3) * mm});
            skArc(sketch, "E19.18.14.0", {"start": v(275.5, -3) * mm, "mid": v(276.09, -4.41) * mm, "end": v(277.5, -5) * mm});
            skPoint(sketch, "E19.0.14.1", {"position": v(275.5, -39.64) * mm});
            skLineSegment(sketch, "E19.1.14.1", {"start": v(284.5, 1.53) * mm, "end": v(284.5, -37.64) * mm});
            skPoint(sketch, "E19.4.14.1", {"position": v(284.5, -39.64) * mm});
            skLineSegment(sketch, "E19.5.14.1", {"start": v(275.5, 1.53) * mm, "end": v(284.5, 1.53) * mm});
            skLineSegment(sketch, "E19.8.14.1", {"start": v(277.5, -39.64) * mm, "end": v(282.5, -39.64) * mm});
            skLineSegment(sketch, "E19.11.14.1", {"start": v(275.5, 1.53) * mm, "end": v(275.5, -37.64) * mm});
            skArc(sketch, "E19.14.14.1", {"start": v(282.5, -39.64) * mm, "mid": v(283.91, -39.06) * mm, "end": v(284.5, -37.64) * mm});
            skArc(sketch, "E19.18.14.1", {"start": v(275.5, -37.64) * mm, "mid": v(276.09, -39.06) * mm, "end": v(277.5, -39.64) * mm});
            skPoint(sketch, "E19.0.14.2", {"position": v(275.5, -74.28) * mm});
            skLineSegment(sketch, "E19.1.14.2", {"start": v(284.5, -33.1) * mm, "end": v(284.5, -72.28) * mm});
            skPoint(sketch, "E19.4.14.2", {"position": v(284.5, -74.28) * mm});
            skLineSegment(sketch, "E19.5.14.2", {"start": v(275.5, -33.1) * mm, "end": v(284.5, -33.1) * mm});
            skLineSegment(sketch, "E19.8.14.2", {"start": v(277.5, -74.28) * mm, "end": v(282.5, -74.28) * mm});
            skLineSegment(sketch, "E19.11.14.2", {"start": v(275.5, -33.1) * mm, "end": v(275.5, -72.28) * mm});
            skArc(sketch, "E19.14.14.2", {"start": v(282.5, -74.28) * mm, "mid": v(283.91, -73.7) * mm, "end": v(284.5, -72.28) * mm});
            skArc(sketch, "E19.18.14.2", {"start": v(275.5, -72.28) * mm, "mid": v(276.09, -73.7) * mm, "end": v(277.5, -74.28) * mm});
            skPoint(sketch, "E19.0.14.3", {"position": v(275.5, -108.92) * mm});
            skLineSegment(sketch, "E19.1.14.3", {"start": v(284.5, -67.75) * mm, "end": v(284.5, -106.92) * mm});
            skPoint(sketch, "E19.4.14.3", {"position": v(284.5, -108.92) * mm});
            skLineSegment(sketch, "E19.5.14.3", {"start": v(275.5, -67.75) * mm, "end": v(284.5, -67.75) * mm});
            skLineSegment(sketch, "E19.8.14.3", {"start": v(277.5, -108.92) * mm, "end": v(282.5, -108.92) * mm});
            skLineSegment(sketch, "E19.11.14.3", {"start": v(275.5, -67.75) * mm, "end": v(275.5, -106.92) * mm});
            skArc(sketch, "E19.14.14.3", {"start": v(282.5, -108.92) * mm, "mid": v(283.91, -108.34) * mm, "end": v(284.5, -106.92) * mm});
            skArc(sketch, "E19.18.14.3", {"start": v(275.5, -106.92) * mm, "mid": v(276.09, -108.34) * mm, "end": v(277.5, -108.92) * mm});
            skPoint(sketch, "E19.0.14.4", {"position": v(275.5, -143.56) * mm});
            skLineSegment(sketch, "E19.1.14.4", {"start": v(284.5, -102.4) * mm, "end": v(284.5, -141.56) * mm});
            skPoint(sketch, "E19.4.14.4", {"position": v(284.5, -143.56) * mm});
            skLineSegment(sketch, "E19.5.14.4", {"start": v(275.5, -102.4) * mm, "end": v(284.5, -102.4) * mm});
            skLineSegment(sketch, "E19.8.14.4", {"start": v(277.5, -143.56) * mm, "end": v(282.5, -143.56) * mm});
            skLineSegment(sketch, "E19.11.14.4", {"start": v(275.5, -102.4) * mm, "end": v(275.5, -141.56) * mm});
            skArc(sketch, "E19.14.14.4", {"start": v(282.5, -143.56) * mm, "mid": v(283.91, -142.98) * mm, "end": v(284.5, -141.56) * mm});
            skArc(sketch, "E19.18.14.4", {"start": v(275.5, -141.56) * mm, "mid": v(276.09, -142.98) * mm, "end": v(277.5, -143.56) * mm});
            skPoint(sketch, "E19.0.14.5", {"position": v(275.5, -178.2) * mm});
            skLineSegment(sketch, "E19.1.14.5", {"start": v(284.5, -137.03) * mm, "end": v(284.5, -176.2) * mm});
            skPoint(sketch, "E19.4.14.5", {"position": v(284.5, -178.2) * mm});
            skLineSegment(sketch, "E19.5.14.5", {"start": v(275.5, -137.03) * mm, "end": v(284.5, -137.03) * mm});
            skLineSegment(sketch, "E19.8.14.5", {"start": v(277.5, -178.2) * mm, "end": v(282.5, -178.2) * mm});
            skLineSegment(sketch, "E19.11.14.5", {"start": v(275.5, -137.03) * mm, "end": v(275.5, -176.2) * mm});
            skArc(sketch, "E19.14.14.5", {"start": v(282.5, -178.2) * mm, "mid": v(283.91, -177.62) * mm, "end": v(284.5, -176.2) * mm});
            skArc(sketch, "E19.18.14.5", {"start": v(275.5, -176.2) * mm, "mid": v(276.09, -177.62) * mm, "end": v(277.5, -178.2) * mm});
            skPoint(sketch, "E19.0.14.6", {"position": v(275.5, -212.85) * mm});
            skLineSegment(sketch, "E19.1.14.6", {"start": v(284.5, -171.67) * mm, "end": v(284.5, -210.85) * mm});
            skPoint(sketch, "E19.4.14.6", {"position": v(284.5, -212.85) * mm});
            skLineSegment(sketch, "E19.5.14.6", {"start": v(275.5, -171.67) * mm, "end": v(284.5, -171.67) * mm});
            skLineSegment(sketch, "E19.8.14.6", {"start": v(277.5, -212.85) * mm, "end": v(282.5, -212.85) * mm});
            skLineSegment(sketch, "E19.11.14.6", {"start": v(275.5, -171.67) * mm, "end": v(275.5, -210.85) * mm});
            skArc(sketch, "E19.14.14.6", {"start": v(282.5, -212.85) * mm, "mid": v(283.91, -212.26) * mm, "end": v(284.5, -210.85) * mm});
            skArc(sketch, "E19.18.14.6", {"start": v(275.5, -210.85) * mm, "mid": v(276.09, -212.26) * mm, "end": v(277.5, -212.85) * mm});
            skPoint(sketch, "E19.0.14.7", {"position": v(275.5, -247.49) * mm});
            skLineSegment(sketch, "E19.1.14.7", {"start": v(284.5, -206.31) * mm, "end": v(284.5, -245.49) * mm});
            skPoint(sketch, "E19.4.14.7", {"position": v(284.5, -247.49) * mm});
            skLineSegment(sketch, "E19.5.14.7", {"start": v(275.5, -206.31) * mm, "end": v(284.5, -206.31) * mm});
            skLineSegment(sketch, "E19.8.14.7", {"start": v(277.5, -247.49) * mm, "end": v(282.5, -247.49) * mm});
            skLineSegment(sketch, "E19.11.14.7", {"start": v(275.5, -206.31) * mm, "end": v(275.5, -245.49) * mm});
            skArc(sketch, "E19.14.14.7", {"start": v(282.5, -247.49) * mm, "mid": v(283.91, -246.9) * mm, "end": v(284.5, -245.49) * mm});
            skArc(sketch, "E19.18.14.7", {"start": v(275.5, -245.49) * mm, "mid": v(276.09, -246.9) * mm, "end": v(277.5, -247.49) * mm});
            skPoint(sketch, "E19.0.14.8", {"position": v(275.5, -282.13) * mm});
            skLineSegment(sketch, "E19.1.14.8", {"start": v(284.5, -240.95) * mm, "end": v(284.5, -280.13) * mm});
            skPoint(sketch, "E19.4.14.8", {"position": v(284.5, -282.13) * mm});
            skLineSegment(sketch, "E19.5.14.8", {"start": v(275.5, -240.95) * mm, "end": v(284.5, -240.95) * mm});
            skLineSegment(sketch, "E19.8.14.8", {"start": v(277.5, -282.13) * mm, "end": v(282.5, -282.13) * mm});
            skLineSegment(sketch, "E19.11.14.8", {"start": v(275.5, -240.95) * mm, "end": v(275.5, -280.13) * mm});
            skArc(sketch, "E19.14.14.8", {"start": v(282.5, -282.13) * mm, "mid": v(283.91, -281.54) * mm, "end": v(284.5, -280.13) * mm});
            skArc(sketch, "E19.18.14.8", {"start": v(275.5, -280.13) * mm, "mid": v(276.09, -281.54) * mm, "end": v(277.5, -282.13) * mm});
            skPoint(sketch, "E19.0.14.9", {"position": v(275.5, -316.77) * mm});
            skLineSegment(sketch, "E19.1.14.9", {"start": v(284.5, -275.6) * mm, "end": v(284.5, -314.77) * mm});
            skPoint(sketch, "E19.4.14.9", {"position": v(284.5, -316.77) * mm});
            skLineSegment(sketch, "E19.5.14.9", {"start": v(275.5, -275.6) * mm, "end": v(284.5, -275.6) * mm});
            skLineSegment(sketch, "E19.8.14.9", {"start": v(277.5, -316.77) * mm, "end": v(282.5, -316.77) * mm});
            skLineSegment(sketch, "E19.11.14.9", {"start": v(275.5, -275.6) * mm, "end": v(275.5, -314.77) * mm});
            skArc(sketch, "E19.14.14.9", {"start": v(282.5, -316.77) * mm, "mid": v(283.91, -316.18) * mm, "end": v(284.5, -314.77) * mm});
            skArc(sketch, "E19.18.14.9", {"start": v(275.5, -314.77) * mm, "mid": v(276.09, -316.18) * mm, "end": v(277.5, -316.77) * mm});
            skPoint(sketch, "E19.0.14.10", {"position": v(275.5, -351.41) * mm});
            skLineSegment(sketch, "E19.1.14.10", {"start": v(284.5, -310.24) * mm, "end": v(284.5, -349.41) * mm});
            skPoint(sketch, "E19.4.14.10", {"position": v(284.5, -351.41) * mm});
            skLineSegment(sketch, "E19.5.14.10", {"start": v(275.5, -310.24) * mm, "end": v(284.5, -310.24) * mm});
            skLineSegment(sketch, "E19.8.14.10", {"start": v(277.5, -351.41) * mm, "end": v(282.5, -351.41) * mm});
            skLineSegment(sketch, "E19.11.14.10", {"start": v(275.5, -310.24) * mm, "end": v(275.5, -349.41) * mm});
            skArc(sketch, "E19.14.14.10", {"start": v(282.5, -351.41) * mm, "mid": v(283.91, -350.82) * mm, "end": v(284.5, -349.41) * mm});
            skArc(sketch, "E19.18.14.10", {"start": v(275.5, -349.41) * mm, "mid": v(276.09, -350.82) * mm, "end": v(277.5, -351.41) * mm});
            skPoint(sketch, "E19.0.14.11", {"position": v(275.5, -386.05) * mm});
            skLineSegment(sketch, "E19.1.14.11", {"start": v(284.5, -344.88) * mm, "end": v(284.5, -384.05) * mm});
            skPoint(sketch, "E19.4.14.11", {"position": v(284.5, -386.05) * mm});
            skLineSegment(sketch, "E19.5.14.11", {"start": v(275.5, -344.88) * mm, "end": v(284.5, -344.88) * mm});
            skLineSegment(sketch, "E19.8.14.11", {"start": v(277.5, -386.05) * mm, "end": v(282.5, -386.05) * mm});
            skLineSegment(sketch, "E19.11.14.11", {"start": v(275.5, -344.88) * mm, "end": v(275.5, -384.05) * mm});
            skArc(sketch, "E19.14.14.11", {"start": v(282.5, -386.05) * mm, "mid": v(283.91, -385.47) * mm, "end": v(284.5, -384.05) * mm});
            skArc(sketch, "E19.18.14.11", {"start": v(275.5, -384.05) * mm, "mid": v(276.09, -385.47) * mm, "end": v(277.5, -386.05) * mm});
            skPoint(sketch, "E19.0.14.12", {"position": v(275.5, -420.7) * mm});
            skLineSegment(sketch, "E19.1.14.12", {"start": v(284.5, -379.52) * mm, "end": v(284.5, -418.7) * mm});
            skPoint(sketch, "E19.4.14.12", {"position": v(284.5, -420.7) * mm});
            skLineSegment(sketch, "E19.5.14.12", {"start": v(275.5, -379.52) * mm, "end": v(284.5, -379.52) * mm});
            skLineSegment(sketch, "E19.8.14.12", {"start": v(277.5, -420.7) * mm, "end": v(282.5, -420.7) * mm});
            skLineSegment(sketch, "E19.11.14.12", {"start": v(275.5, -379.52) * mm, "end": v(275.5, -418.7) * mm});
            skArc(sketch, "E19.14.14.12", {"start": v(282.5, -420.7) * mm, "mid": v(283.91, -420.1) * mm, "end": v(284.5, -418.7) * mm});
            skArc(sketch, "E19.18.14.12", {"start": v(275.5, -418.7) * mm, "mid": v(276.09, -420.1) * mm, "end": v(277.5, -420.7) * mm});
            skPoint(sketch, "E19.0.14.13", {"position": v(275.5, -455.33) * mm});
            skLineSegment(sketch, "E19.1.14.13", {"start": v(284.5, -414.16) * mm, "end": v(284.5, -453.33) * mm});
            skPoint(sketch, "E19.4.14.13", {"position": v(284.5, -455.33) * mm});
            skLineSegment(sketch, "E19.5.14.13", {"start": v(275.5, -414.16) * mm, "end": v(284.5, -414.16) * mm});
            skLineSegment(sketch, "E19.8.14.13", {"start": v(277.5, -455.33) * mm, "end": v(282.5, -455.33) * mm});
            skLineSegment(sketch, "E19.11.14.13", {"start": v(275.5, -414.16) * mm, "end": v(275.5, -453.33) * mm});
            skArc(sketch, "E19.14.14.13", {"start": v(282.5, -455.33) * mm, "mid": v(283.91, -454.75) * mm, "end": v(284.5, -453.33) * mm});
            skArc(sketch, "E19.18.14.13", {"start": v(275.5, -453.33) * mm, "mid": v(276.09, -454.75) * mm, "end": v(277.5, -455.33) * mm});
            skPoint(sketch, "E19.0.14.14", {"position": v(275.5, -489.97) * mm});
            skLineSegment(sketch, "E19.1.14.14", {"start": v(284.5, -448.8) * mm, "end": v(284.5, -487.97) * mm});
            skPoint(sketch, "E19.4.14.14", {"position": v(284.5, -489.97) * mm});
            skLineSegment(sketch, "E19.5.14.14", {"start": v(275.5, -448.8) * mm, "end": v(284.5, -448.8) * mm});
            skLineSegment(sketch, "E19.8.14.14", {"start": v(277.5, -489.97) * mm, "end": v(282.5, -489.97) * mm});
            skLineSegment(sketch, "E19.11.14.14", {"start": v(275.5, -448.8) * mm, "end": v(275.5, -487.97) * mm});
            skArc(sketch, "E19.14.14.14", {"start": v(282.5, -489.97) * mm, "mid": v(283.91, -489.39) * mm, "end": v(284.5, -487.97) * mm});
            skArc(sketch, "E19.18.14.14", {"start": v(275.5, -487.97) * mm, "mid": v(276.09, -489.39) * mm, "end": v(277.5, -489.97) * mm});
            skPoint(sketch, "E19.0.15.0", {"position": v(295.5, -5) * mm});
            skLineSegment(sketch, "E19.1.15.0", {"start": v(304.5, 36.17) * mm, "end": v(304.5, -3) * mm});
            skPoint(sketch, "E19.4.15.0", {"position": v(304.5, -5) * mm});
            skLineSegment(sketch, "E19.5.15.0", {"start": v(295.5, 36.17) * mm, "end": v(304.5, 36.17) * mm});
            skLineSegment(sketch, "E19.8.15.0", {"start": v(297.5, -5) * mm, "end": v(302.5, -5) * mm});
            skLineSegment(sketch, "E19.11.15.0", {"start": v(295.5, 36.17) * mm, "end": v(295.5, -3) * mm});
            skArc(sketch, "E19.14.15.0", {"start": v(302.5, -5) * mm, "mid": v(303.91, -4.41) * mm, "end": v(304.5, -3) * mm});
            skArc(sketch, "E19.18.15.0", {"start": v(295.5, -3) * mm, "mid": v(296.09, -4.41) * mm, "end": v(297.5, -5) * mm});
            skPoint(sketch, "E19.0.15.1", {"position": v(295.5, -39.64) * mm});
            skLineSegment(sketch, "E19.1.15.1", {"start": v(304.5, 1.53) * mm, "end": v(304.5, -37.64) * mm});
            skPoint(sketch, "E19.4.15.1", {"position": v(304.5, -39.64) * mm});
            skLineSegment(sketch, "E19.5.15.1", {"start": v(295.5, 1.53) * mm, "end": v(304.5, 1.53) * mm});
            skLineSegment(sketch, "E19.8.15.1", {"start": v(297.5, -39.64) * mm, "end": v(302.5, -39.64) * mm});
            skLineSegment(sketch, "E19.11.15.1", {"start": v(295.5, 1.53) * mm, "end": v(295.5, -37.64) * mm});
            skArc(sketch, "E19.14.15.1", {"start": v(302.5, -39.64) * mm, "mid": v(303.91, -39.06) * mm, "end": v(304.5, -37.64) * mm});
            skArc(sketch, "E19.18.15.1", {"start": v(295.5, -37.64) * mm, "mid": v(296.09, -39.06) * mm, "end": v(297.5, -39.64) * mm});
            skPoint(sketch, "E19.0.15.2", {"position": v(295.5, -74.28) * mm});
            skLineSegment(sketch, "E19.1.15.2", {"start": v(304.5, -33.1) * mm, "end": v(304.5, -72.28) * mm});
            skPoint(sketch, "E19.4.15.2", {"position": v(304.5, -74.28) * mm});
            skLineSegment(sketch, "E19.5.15.2", {"start": v(295.5, -33.1) * mm, "end": v(304.5, -33.1) * mm});
            skLineSegment(sketch, "E19.8.15.2", {"start": v(297.5, -74.28) * mm, "end": v(302.5, -74.28) * mm});
            skLineSegment(sketch, "E19.11.15.2", {"start": v(295.5, -33.1) * mm, "end": v(295.5, -72.28) * mm});
            skArc(sketch, "E19.14.15.2", {"start": v(302.5, -74.28) * mm, "mid": v(303.91, -73.7) * mm, "end": v(304.5, -72.28) * mm});
            skArc(sketch, "E19.18.15.2", {"start": v(295.5, -72.28) * mm, "mid": v(296.09, -73.7) * mm, "end": v(297.5, -74.28) * mm});
            skPoint(sketch, "E19.0.15.3", {"position": v(295.5, -108.92) * mm});
            skLineSegment(sketch, "E19.1.15.3", {"start": v(304.5, -67.75) * mm, "end": v(304.5, -106.92) * mm});
            skPoint(sketch, "E19.4.15.3", {"position": v(304.5, -108.92) * mm});
            skLineSegment(sketch, "E19.5.15.3", {"start": v(295.5, -67.75) * mm, "end": v(304.5, -67.75) * mm});
            skLineSegment(sketch, "E19.8.15.3", {"start": v(297.5, -108.92) * mm, "end": v(302.5, -108.92) * mm});
            skLineSegment(sketch, "E19.11.15.3", {"start": v(295.5, -67.75) * mm, "end": v(295.5, -106.92) * mm});
            skArc(sketch, "E19.14.15.3", {"start": v(302.5, -108.92) * mm, "mid": v(303.91, -108.34) * mm, "end": v(304.5, -106.92) * mm});
            skArc(sketch, "E19.18.15.3", {"start": v(295.5, -106.92) * mm, "mid": v(296.09, -108.34) * mm, "end": v(297.5, -108.92) * mm});
            skPoint(sketch, "E19.0.15.4", {"position": v(295.5, -143.56) * mm});
            skLineSegment(sketch, "E19.1.15.4", {"start": v(304.5, -102.4) * mm, "end": v(304.5, -141.56) * mm});
            skPoint(sketch, "E19.4.15.4", {"position": v(304.5, -143.56) * mm});
            skLineSegment(sketch, "E19.5.15.4", {"start": v(295.5, -102.4) * mm, "end": v(304.5, -102.4) * mm});
            skLineSegment(sketch, "E19.8.15.4", {"start": v(297.5, -143.56) * mm, "end": v(302.5, -143.56) * mm});
            skLineSegment(sketch, "E19.11.15.4", {"start": v(295.5, -102.4) * mm, "end": v(295.5, -141.56) * mm});
            skArc(sketch, "E19.14.15.4", {"start": v(302.5, -143.56) * mm, "mid": v(303.91, -142.98) * mm, "end": v(304.5, -141.56) * mm});
            skArc(sketch, "E19.18.15.4", {"start": v(295.5, -141.56) * mm, "mid": v(296.09, -142.98) * mm, "end": v(297.5, -143.56) * mm});
            skPoint(sketch, "E19.0.15.5", {"position": v(295.5, -178.2) * mm});
            skLineSegment(sketch, "E19.1.15.5", {"start": v(304.5, -137.03) * mm, "end": v(304.5, -176.2) * mm});
            skPoint(sketch, "E19.4.15.5", {"position": v(304.5, -178.2) * mm});
            skLineSegment(sketch, "E19.5.15.5", {"start": v(295.5, -137.03) * mm, "end": v(304.5, -137.03) * mm});
            skLineSegment(sketch, "E19.8.15.5", {"start": v(297.5, -178.2) * mm, "end": v(302.5, -178.2) * mm});
            skLineSegment(sketch, "E19.11.15.5", {"start": v(295.5, -137.03) * mm, "end": v(295.5, -176.2) * mm});
            skArc(sketch, "E19.14.15.5", {"start": v(302.5, -178.2) * mm, "mid": v(303.91, -177.62) * mm, "end": v(304.5, -176.2) * mm});
            skArc(sketch, "E19.18.15.5", {"start": v(295.5, -176.2) * mm, "mid": v(296.09, -177.62) * mm, "end": v(297.5, -178.2) * mm});
            skPoint(sketch, "E19.0.15.6", {"position": v(295.5, -212.85) * mm});
            skLineSegment(sketch, "E19.1.15.6", {"start": v(304.5, -171.67) * mm, "end": v(304.5, -210.85) * mm});
            skPoint(sketch, "E19.4.15.6", {"position": v(304.5, -212.85) * mm});
            skLineSegment(sketch, "E19.5.15.6", {"start": v(295.5, -171.67) * mm, "end": v(304.5, -171.67) * mm});
            skLineSegment(sketch, "E19.8.15.6", {"start": v(297.5, -212.85) * mm, "end": v(302.5, -212.85) * mm});
            skLineSegment(sketch, "E19.11.15.6", {"start": v(295.5, -171.67) * mm, "end": v(295.5, -210.85) * mm});
            skArc(sketch, "E19.14.15.6", {"start": v(302.5, -212.85) * mm, "mid": v(303.91, -212.26) * mm, "end": v(304.5, -210.85) * mm});
            skArc(sketch, "E19.18.15.6", {"start": v(295.5, -210.85) * mm, "mid": v(296.09, -212.26) * mm, "end": v(297.5, -212.85) * mm});
            skPoint(sketch, "E19.0.15.7", {"position": v(295.5, -247.49) * mm});
            skLineSegment(sketch, "E19.1.15.7", {"start": v(304.5, -206.31) * mm, "end": v(304.5, -245.49) * mm});
            skPoint(sketch, "E19.4.15.7", {"position": v(304.5, -247.49) * mm});
            skLineSegment(sketch, "E19.5.15.7", {"start": v(295.5, -206.31) * mm, "end": v(304.5, -206.31) * mm});
            skLineSegment(sketch, "E19.8.15.7", {"start": v(297.5, -247.49) * mm, "end": v(302.5, -247.49) * mm});
            skLineSegment(sketch, "E19.11.15.7", {"start": v(295.5, -206.31) * mm, "end": v(295.5, -245.49) * mm});
            skArc(sketch, "E19.14.15.7", {"start": v(302.5, -247.49) * mm, "mid": v(303.91, -246.9) * mm, "end": v(304.5, -245.49) * mm});
            skArc(sketch, "E19.18.15.7", {"start": v(295.5, -245.49) * mm, "mid": v(296.09, -246.9) * mm, "end": v(297.5, -247.49) * mm});
            skPoint(sketch, "E19.0.15.8", {"position": v(295.5, -282.13) * mm});
            skLineSegment(sketch, "E19.1.15.8", {"start": v(304.5, -240.95) * mm, "end": v(304.5, -280.13) * mm});
            skPoint(sketch, "E19.4.15.8", {"position": v(304.5, -282.13) * mm});
            skLineSegment(sketch, "E19.5.15.8", {"start": v(295.5, -240.95) * mm, "end": v(304.5, -240.95) * mm});
            skLineSegment(sketch, "E19.8.15.8", {"start": v(297.5, -282.13) * mm, "end": v(302.5, -282.13) * mm});
            skLineSegment(sketch, "E19.11.15.8", {"start": v(295.5, -240.95) * mm, "end": v(295.5, -280.13) * mm});
            skArc(sketch, "E19.14.15.8", {"start": v(302.5, -282.13) * mm, "mid": v(303.91, -281.54) * mm, "end": v(304.5, -280.13) * mm});
            skArc(sketch, "E19.18.15.8", {"start": v(295.5, -280.13) * mm, "mid": v(296.09, -281.54) * mm, "end": v(297.5, -282.13) * mm});
            skPoint(sketch, "E19.0.15.9", {"position": v(295.5, -316.77) * mm});
            skLineSegment(sketch, "E19.1.15.9", {"start": v(304.5, -275.6) * mm, "end": v(304.5, -314.77) * mm});
            skPoint(sketch, "E19.4.15.9", {"position": v(304.5, -316.77) * mm});
            skLineSegment(sketch, "E19.5.15.9", {"start": v(295.5, -275.6) * mm, "end": v(304.5, -275.6) * mm});
            skLineSegment(sketch, "E19.8.15.9", {"start": v(297.5, -316.77) * mm, "end": v(302.5, -316.77) * mm});
            skLineSegment(sketch, "E19.11.15.9", {"start": v(295.5, -275.6) * mm, "end": v(295.5, -314.77) * mm});
            skArc(sketch, "E19.14.15.9", {"start": v(302.5, -316.77) * mm, "mid": v(303.91, -316.18) * mm, "end": v(304.5, -314.77) * mm});
            skArc(sketch, "E19.18.15.9", {"start": v(295.5, -314.77) * mm, "mid": v(296.09, -316.18) * mm, "end": v(297.5, -316.77) * mm});
            skPoint(sketch, "E19.0.15.10", {"position": v(295.5, -351.41) * mm});
            skLineSegment(sketch, "E19.1.15.10", {"start": v(304.5, -310.24) * mm, "end": v(304.5, -349.41) * mm});
            skPoint(sketch, "E19.4.15.10", {"position": v(304.5, -351.41) * mm});
            skLineSegment(sketch, "E19.5.15.10", {"start": v(295.5, -310.24) * mm, "end": v(304.5, -310.24) * mm});
            skLineSegment(sketch, "E19.8.15.10", {"start": v(297.5, -351.41) * mm, "end": v(302.5, -351.41) * mm});
            skLineSegment(sketch, "E19.11.15.10", {"start": v(295.5, -310.24) * mm, "end": v(295.5, -349.41) * mm});
            skArc(sketch, "E19.14.15.10", {"start": v(302.5, -351.41) * mm, "mid": v(303.91, -350.82) * mm, "end": v(304.5, -349.41) * mm});
            skArc(sketch, "E19.18.15.10", {"start": v(295.5, -349.41) * mm, "mid": v(296.09, -350.82) * mm, "end": v(297.5, -351.41) * mm});
            skPoint(sketch, "E19.0.15.11", {"position": v(295.5, -386.05) * mm});
            skLineSegment(sketch, "E19.1.15.11", {"start": v(304.5, -344.88) * mm, "end": v(304.5, -384.05) * mm});
            skPoint(sketch, "E19.4.15.11", {"position": v(304.5, -386.05) * mm});
            skLineSegment(sketch, "E19.5.15.11", {"start": v(295.5, -344.88) * mm, "end": v(304.5, -344.88) * mm});
            skLineSegment(sketch, "E19.8.15.11", {"start": v(297.5, -386.05) * mm, "end": v(302.5, -386.05) * mm});
            skLineSegment(sketch, "E19.11.15.11", {"start": v(295.5, -344.88) * mm, "end": v(295.5, -384.05) * mm});
            skArc(sketch, "E19.14.15.11", {"start": v(302.5, -386.05) * mm, "mid": v(303.91, -385.47) * mm, "end": v(304.5, -384.05) * mm});
            skArc(sketch, "E19.18.15.11", {"start": v(295.5, -384.05) * mm, "mid": v(296.09, -385.47) * mm, "end": v(297.5, -386.05) * mm});
            skPoint(sketch, "E19.0.15.12", {"position": v(295.5, -420.7) * mm});
            skLineSegment(sketch, "E19.1.15.12", {"start": v(304.5, -379.52) * mm, "end": v(304.5, -418.7) * mm});
            skPoint(sketch, "E19.4.15.12", {"position": v(304.5, -420.7) * mm});
            skLineSegment(sketch, "E19.5.15.12", {"start": v(295.5, -379.52) * mm, "end": v(304.5, -379.52) * mm});
            skLineSegment(sketch, "E19.8.15.12", {"start": v(297.5, -420.7) * mm, "end": v(302.5, -420.7) * mm});
            skLineSegment(sketch, "E19.11.15.12", {"start": v(295.5, -379.52) * mm, "end": v(295.5, -418.7) * mm});
            skArc(sketch, "E19.14.15.12", {"start": v(302.5, -420.7) * mm, "mid": v(303.91, -420.1) * mm, "end": v(304.5, -418.7) * mm});
            skArc(sketch, "E19.18.15.12", {"start": v(295.5, -418.7) * mm, "mid": v(296.09, -420.1) * mm, "end": v(297.5, -420.7) * mm});
            skPoint(sketch, "E19.0.15.13", {"position": v(295.5, -455.33) * mm});
            skLineSegment(sketch, "E19.1.15.13", {"start": v(304.5, -414.16) * mm, "end": v(304.5, -453.33) * mm});
            skPoint(sketch, "E19.4.15.13", {"position": v(304.5, -455.33) * mm});
            skLineSegment(sketch, "E19.5.15.13", {"start": v(295.5, -414.16) * mm, "end": v(304.5, -414.16) * mm});
            skLineSegment(sketch, "E19.8.15.13", {"start": v(297.5, -455.33) * mm, "end": v(302.5, -455.33) * mm});
            skLineSegment(sketch, "E19.11.15.13", {"start": v(295.5, -414.16) * mm, "end": v(295.5, -453.33) * mm});
            skArc(sketch, "E19.14.15.13", {"start": v(302.5, -455.33) * mm, "mid": v(303.91, -454.75) * mm, "end": v(304.5, -453.33) * mm});
            skArc(sketch, "E19.18.15.13", {"start": v(295.5, -453.33) * mm, "mid": v(296.09, -454.75) * mm, "end": v(297.5, -455.33) * mm});
            skPoint(sketch, "E19.0.15.14", {"position": v(295.5, -489.97) * mm});
            skLineSegment(sketch, "E19.1.15.14", {"start": v(304.5, -448.8) * mm, "end": v(304.5, -487.97) * mm});
            skPoint(sketch, "E19.4.15.14", {"position": v(304.5, -489.97) * mm});
            skLineSegment(sketch, "E19.5.15.14", {"start": v(295.5, -448.8) * mm, "end": v(304.5, -448.8) * mm});
            skLineSegment(sketch, "E19.8.15.14", {"start": v(297.5, -489.97) * mm, "end": v(302.5, -489.97) * mm});
            skLineSegment(sketch, "E19.11.15.14", {"start": v(295.5, -448.8) * mm, "end": v(295.5, -487.97) * mm});
            skArc(sketch, "E19.14.15.14", {"start": v(302.5, -489.97) * mm, "mid": v(303.91, -489.39) * mm, "end": v(304.5, -487.97) * mm});
            skArc(sketch, "E19.18.15.14", {"start": v(295.5, -487.97) * mm, "mid": v(296.09, -489.39) * mm, "end": v(297.5, -489.97) * mm});
            skPoint(sketch, "E19.0.16.0", {"position": v(315.5, -5) * mm});
            skLineSegment(sketch, "E19.1.16.0", {"start": v(324.5, 36.17) * mm, "end": v(324.5, -3) * mm});
            skPoint(sketch, "E19.4.16.0", {"position": v(324.5, -5) * mm});
            skLineSegment(sketch, "E19.5.16.0", {"start": v(315.5, 36.17) * mm, "end": v(324.5, 36.17) * mm});
            skLineSegment(sketch, "E19.8.16.0", {"start": v(317.5, -5) * mm, "end": v(322.5, -5) * mm});
            skLineSegment(sketch, "E19.11.16.0", {"start": v(315.5, 36.17) * mm, "end": v(315.5, -3) * mm});
            skArc(sketch, "E19.14.16.0", {"start": v(322.5, -5) * mm, "mid": v(323.91, -4.41) * mm, "end": v(324.5, -3) * mm});
            skArc(sketch, "E19.18.16.0", {"start": v(315.5, -3) * mm, "mid": v(316.09, -4.41) * mm, "end": v(317.5, -5) * mm});
            skPoint(sketch, "E19.0.16.1", {"position": v(315.5, -39.64) * mm});
            skLineSegment(sketch, "E19.1.16.1", {"start": v(324.5, 1.53) * mm, "end": v(324.5, -37.64) * mm});
            skPoint(sketch, "E19.4.16.1", {"position": v(324.5, -39.64) * mm});
            skLineSegment(sketch, "E19.5.16.1", {"start": v(315.5, 1.53) * mm, "end": v(324.5, 1.53) * mm});
            skLineSegment(sketch, "E19.8.16.1", {"start": v(317.5, -39.64) * mm, "end": v(322.5, -39.64) * mm});
            skLineSegment(sketch, "E19.11.16.1", {"start": v(315.5, 1.53) * mm, "end": v(315.5, -37.64) * mm});
            skArc(sketch, "E19.14.16.1", {"start": v(322.5, -39.64) * mm, "mid": v(323.91, -39.06) * mm, "end": v(324.5, -37.64) * mm});
            skArc(sketch, "E19.18.16.1", {"start": v(315.5, -37.64) * mm, "mid": v(316.09, -39.06) * mm, "end": v(317.5, -39.64) * mm});
            skPoint(sketch, "E19.0.16.2", {"position": v(315.5, -74.28) * mm});
            skLineSegment(sketch, "E19.1.16.2", {"start": v(324.5, -33.1) * mm, "end": v(324.5, -72.28) * mm});
            skPoint(sketch, "E19.4.16.2", {"position": v(324.5, -74.28) * mm});
            skLineSegment(sketch, "E19.5.16.2", {"start": v(315.5, -33.1) * mm, "end": v(324.5, -33.1) * mm});
            skLineSegment(sketch, "E19.8.16.2", {"start": v(317.5, -74.28) * mm, "end": v(322.5, -74.28) * mm});
            skLineSegment(sketch, "E19.11.16.2", {"start": v(315.5, -33.1) * mm, "end": v(315.5, -72.28) * mm});
            skArc(sketch, "E19.14.16.2", {"start": v(322.5, -74.28) * mm, "mid": v(323.91, -73.7) * mm, "end": v(324.5, -72.28) * mm});
            skArc(sketch, "E19.18.16.2", {"start": v(315.5, -72.28) * mm, "mid": v(316.09, -73.7) * mm, "end": v(317.5, -74.28) * mm});
            skPoint(sketch, "E19.0.16.3", {"position": v(315.5, -108.92) * mm});
            skLineSegment(sketch, "E19.1.16.3", {"start": v(324.5, -67.75) * mm, "end": v(324.5, -106.92) * mm});
            skPoint(sketch, "E19.4.16.3", {"position": v(324.5, -108.92) * mm});
            skLineSegment(sketch, "E19.5.16.3", {"start": v(315.5, -67.75) * mm, "end": v(324.5, -67.75) * mm});
            skLineSegment(sketch, "E19.8.16.3", {"start": v(317.5, -108.92) * mm, "end": v(322.5, -108.92) * mm});
            skLineSegment(sketch, "E19.11.16.3", {"start": v(315.5, -67.75) * mm, "end": v(315.5, -106.92) * mm});
            skArc(sketch, "E19.14.16.3", {"start": v(322.5, -108.92) * mm, "mid": v(323.91, -108.34) * mm, "end": v(324.5, -106.92) * mm});
            skArc(sketch, "E19.18.16.3", {"start": v(315.5, -106.92) * mm, "mid": v(316.09, -108.34) * mm, "end": v(317.5, -108.92) * mm});
            skPoint(sketch, "E19.0.16.4", {"position": v(315.5, -143.56) * mm});
            skLineSegment(sketch, "E19.1.16.4", {"start": v(324.5, -102.4) * mm, "end": v(324.5, -141.56) * mm});
            skPoint(sketch, "E19.4.16.4", {"position": v(324.5, -143.56) * mm});
            skLineSegment(sketch, "E19.5.16.4", {"start": v(315.5, -102.4) * mm, "end": v(324.5, -102.4) * mm});
            skLineSegment(sketch, "E19.8.16.4", {"start": v(317.5, -143.56) * mm, "end": v(322.5, -143.56) * mm});
            skLineSegment(sketch, "E19.11.16.4", {"start": v(315.5, -102.4) * mm, "end": v(315.5, -141.56) * mm});
            skArc(sketch, "E19.14.16.4", {"start": v(322.5, -143.56) * mm, "mid": v(323.91, -142.98) * mm, "end": v(324.5, -141.56) * mm});
            skArc(sketch, "E19.18.16.4", {"start": v(315.5, -141.56) * mm, "mid": v(316.09, -142.98) * mm, "end": v(317.5, -143.56) * mm});
            skPoint(sketch, "E19.0.16.5", {"position": v(315.5, -178.2) * mm});
            skLineSegment(sketch, "E19.1.16.5", {"start": v(324.5, -137.03) * mm, "end": v(324.5, -176.2) * mm});
            skPoint(sketch, "E19.4.16.5", {"position": v(324.5, -178.2) * mm});
            skLineSegment(sketch, "E19.5.16.5", {"start": v(315.5, -137.03) * mm, "end": v(324.5, -137.03) * mm});
            skLineSegment(sketch, "E19.8.16.5", {"start": v(317.5, -178.2) * mm, "end": v(322.5, -178.2) * mm});
            skLineSegment(sketch, "E19.11.16.5", {"start": v(315.5, -137.03) * mm, "end": v(315.5, -176.2) * mm});
            skArc(sketch, "E19.14.16.5", {"start": v(322.5, -178.2) * mm, "mid": v(323.91, -177.62) * mm, "end": v(324.5, -176.2) * mm});
            skArc(sketch, "E19.18.16.5", {"start": v(315.5, -176.2) * mm, "mid": v(316.09, -177.62) * mm, "end": v(317.5, -178.2) * mm});
            skPoint(sketch, "E19.0.16.6", {"position": v(315.5, -212.85) * mm});
            skLineSegment(sketch, "E19.1.16.6", {"start": v(324.5, -171.67) * mm, "end": v(324.5, -210.85) * mm});
            skPoint(sketch, "E19.4.16.6", {"position": v(324.5, -212.85) * mm});
            skLineSegment(sketch, "E19.5.16.6", {"start": v(315.5, -171.67) * mm, "end": v(324.5, -171.67) * mm});
            skLineSegment(sketch, "E19.8.16.6", {"start": v(317.5, -212.85) * mm, "end": v(322.5, -212.85) * mm});
            skLineSegment(sketch, "E19.11.16.6", {"start": v(315.5, -171.67) * mm, "end": v(315.5, -210.85) * mm});
            skArc(sketch, "E19.14.16.6", {"start": v(322.5, -212.85) * mm, "mid": v(323.91, -212.26) * mm, "end": v(324.5, -210.85) * mm});
            skArc(sketch, "E19.18.16.6", {"start": v(315.5, -210.85) * mm, "mid": v(316.09, -212.26) * mm, "end": v(317.5, -212.85) * mm});
            skPoint(sketch, "E19.0.16.7", {"position": v(315.5, -247.49) * mm});
            skLineSegment(sketch, "E19.1.16.7", {"start": v(324.5, -206.31) * mm, "end": v(324.5, -245.49) * mm});
            skPoint(sketch, "E19.4.16.7", {"position": v(324.5, -247.49) * mm});
            skLineSegment(sketch, "E19.5.16.7", {"start": v(315.5, -206.31) * mm, "end": v(324.5, -206.31) * mm});
            skLineSegment(sketch, "E19.8.16.7", {"start": v(317.5, -247.49) * mm, "end": v(322.5, -247.49) * mm});
            skLineSegment(sketch, "E19.11.16.7", {"start": v(315.5, -206.31) * mm, "end": v(315.5, -245.49) * mm});
            skArc(sketch, "E19.14.16.7", {"start": v(322.5, -247.49) * mm, "mid": v(323.91, -246.9) * mm, "end": v(324.5, -245.49) * mm});
            skArc(sketch, "E19.18.16.7", {"start": v(315.5, -245.49) * mm, "mid": v(316.09, -246.9) * mm, "end": v(317.5, -247.49) * mm});
            skPoint(sketch, "E19.0.16.8", {"position": v(315.5, -282.13) * mm});
            skLineSegment(sketch, "E19.1.16.8", {"start": v(324.5, -240.95) * mm, "end": v(324.5, -280.13) * mm});
            skPoint(sketch, "E19.4.16.8", {"position": v(324.5, -282.13) * mm});
            skLineSegment(sketch, "E19.5.16.8", {"start": v(315.5, -240.95) * mm, "end": v(324.5, -240.95) * mm});
            skLineSegment(sketch, "E19.8.16.8", {"start": v(317.5, -282.13) * mm, "end": v(322.5, -282.13) * mm});
            skLineSegment(sketch, "E19.11.16.8", {"start": v(315.5, -240.95) * mm, "end": v(315.5, -280.13) * mm});
            skArc(sketch, "E19.14.16.8", {"start": v(322.5, -282.13) * mm, "mid": v(323.91, -281.54) * mm, "end": v(324.5, -280.13) * mm});
            skArc(sketch, "E19.18.16.8", {"start": v(315.5, -280.13) * mm, "mid": v(316.09, -281.54) * mm, "end": v(317.5, -282.13) * mm});
            skPoint(sketch, "E19.0.16.9", {"position": v(315.5, -316.77) * mm});
            skLineSegment(sketch, "E19.1.16.9", {"start": v(324.5, -275.6) * mm, "end": v(324.5, -314.77) * mm});
            skPoint(sketch, "E19.4.16.9", {"position": v(324.5, -316.77) * mm});
            skLineSegment(sketch, "E19.5.16.9", {"start": v(315.5, -275.6) * mm, "end": v(324.5, -275.6) * mm});
            skLineSegment(sketch, "E19.8.16.9", {"start": v(317.5, -316.77) * mm, "end": v(322.5, -316.77) * mm});
            skLineSegment(sketch, "E19.11.16.9", {"start": v(315.5, -275.6) * mm, "end": v(315.5, -314.77) * mm});
            skArc(sketch, "E19.14.16.9", {"start": v(322.5, -316.77) * mm, "mid": v(323.91, -316.18) * mm, "end": v(324.5, -314.77) * mm});
            skArc(sketch, "E19.18.16.9", {"start": v(315.5, -314.77) * mm, "mid": v(316.09, -316.18) * mm, "end": v(317.5, -316.77) * mm});
            skPoint(sketch, "E19.0.16.10", {"position": v(315.5, -351.41) * mm});
            skLineSegment(sketch, "E19.1.16.10", {"start": v(324.5, -310.24) * mm, "end": v(324.5, -349.41) * mm});
            skPoint(sketch, "E19.4.16.10", {"position": v(324.5, -351.41) * mm});
            skLineSegment(sketch, "E19.5.16.10", {"start": v(315.5, -310.24) * mm, "end": v(324.5, -310.24) * mm});
            skLineSegment(sketch, "E19.8.16.10", {"start": v(317.5, -351.41) * mm, "end": v(322.5, -351.41) * mm});
            skLineSegment(sketch, "E19.11.16.10", {"start": v(315.5, -310.24) * mm, "end": v(315.5, -349.41) * mm});
            skArc(sketch, "E19.14.16.10", {"start": v(322.5, -351.41) * mm, "mid": v(323.91, -350.82) * mm, "end": v(324.5, -349.41) * mm});
            skArc(sketch, "E19.18.16.10", {"start": v(315.5, -349.41) * mm, "mid": v(316.09, -350.82) * mm, "end": v(317.5, -351.41) * mm});
            skPoint(sketch, "E19.0.16.11", {"position": v(315.5, -386.05) * mm});
            skLineSegment(sketch, "E19.1.16.11", {"start": v(324.5, -344.88) * mm, "end": v(324.5, -384.05) * mm});
            skPoint(sketch, "E19.4.16.11", {"position": v(324.5, -386.05) * mm});
            skLineSegment(sketch, "E19.5.16.11", {"start": v(315.5, -344.88) * mm, "end": v(324.5, -344.88) * mm});
            skLineSegment(sketch, "E19.8.16.11", {"start": v(317.5, -386.05) * mm, "end": v(322.5, -386.05) * mm});
            skLineSegment(sketch, "E19.11.16.11", {"start": v(315.5, -344.88) * mm, "end": v(315.5, -384.05) * mm});
            skArc(sketch, "E19.14.16.11", {"start": v(322.5, -386.05) * mm, "mid": v(323.91, -385.47) * mm, "end": v(324.5, -384.05) * mm});
            skArc(sketch, "E19.18.16.11", {"start": v(315.5, -384.05) * mm, "mid": v(316.09, -385.47) * mm, "end": v(317.5, -386.05) * mm});
            skPoint(sketch, "E19.0.16.12", {"position": v(315.5, -420.7) * mm});
            skLineSegment(sketch, "E19.1.16.12", {"start": v(324.5, -379.52) * mm, "end": v(324.5, -418.7) * mm});
            skPoint(sketch, "E19.4.16.12", {"position": v(324.5, -420.7) * mm});
            skLineSegment(sketch, "E19.5.16.12", {"start": v(315.5, -379.52) * mm, "end": v(324.5, -379.52) * mm});
            skLineSegment(sketch, "E19.8.16.12", {"start": v(317.5, -420.7) * mm, "end": v(322.5, -420.7) * mm});
            skLineSegment(sketch, "E19.11.16.12", {"start": v(315.5, -379.52) * mm, "end": v(315.5, -418.7) * mm});
            skArc(sketch, "E19.14.16.12", {"start": v(322.5, -420.7) * mm, "mid": v(323.91, -420.1) * mm, "end": v(324.5, -418.7) * mm});
            skArc(sketch, "E19.18.16.12", {"start": v(315.5, -418.7) * mm, "mid": v(316.09, -420.1) * mm, "end": v(317.5, -420.7) * mm});
            skPoint(sketch, "E19.0.16.13", {"position": v(315.5, -455.33) * mm});
            skLineSegment(sketch, "E19.1.16.13", {"start": v(324.5, -414.16) * mm, "end": v(324.5, -453.33) * mm});
            skPoint(sketch, "E19.4.16.13", {"position": v(324.5, -455.33) * mm});
            skLineSegment(sketch, "E19.5.16.13", {"start": v(315.5, -414.16) * mm, "end": v(324.5, -414.16) * mm});
            skLineSegment(sketch, "E19.8.16.13", {"start": v(317.5, -455.33) * mm, "end": v(322.5, -455.33) * mm});
            skLineSegment(sketch, "E19.11.16.13", {"start": v(315.5, -414.16) * mm, "end": v(315.5, -453.33) * mm});
            skArc(sketch, "E19.14.16.13", {"start": v(322.5, -455.33) * mm, "mid": v(323.91, -454.75) * mm, "end": v(324.5, -453.33) * mm});
            skArc(sketch, "E19.18.16.13", {"start": v(315.5, -453.33) * mm, "mid": v(316.09, -454.75) * mm, "end": v(317.5, -455.33) * mm});
            skPoint(sketch, "E19.0.16.14", {"position": v(315.5, -489.97) * mm});
            skLineSegment(sketch, "E19.1.16.14", {"start": v(324.5, -448.8) * mm, "end": v(324.5, -487.97) * mm});
            skPoint(sketch, "E19.4.16.14", {"position": v(324.5, -489.97) * mm});
            skLineSegment(sketch, "E19.5.16.14", {"start": v(315.5, -448.8) * mm, "end": v(324.5, -448.8) * mm});
            skLineSegment(sketch, "E19.8.16.14", {"start": v(317.5, -489.97) * mm, "end": v(322.5, -489.97) * mm});
            skLineSegment(sketch, "E19.11.16.14", {"start": v(315.5, -448.8) * mm, "end": v(315.5, -487.97) * mm});
            skArc(sketch, "E19.14.16.14", {"start": v(322.5, -489.97) * mm, "mid": v(323.91, -489.39) * mm, "end": v(324.5, -487.97) * mm});
            skArc(sketch, "E19.18.16.14", {"start": v(315.5, -487.97) * mm, "mid": v(316.09, -489.39) * mm, "end": v(317.5, -489.97) * mm});
            skPoint(sketch, "E19.0.17.0", {"position": v(335.5, -5) * mm});
            skLineSegment(sketch, "E19.1.17.0", {"start": v(344.5, 36.17) * mm, "end": v(344.5, -3) * mm});
            skPoint(sketch, "E19.4.17.0", {"position": v(344.5, -5) * mm});
            skLineSegment(sketch, "E19.5.17.0", {"start": v(335.5, 36.17) * mm, "end": v(344.5, 36.17) * mm});
            skLineSegment(sketch, "E19.8.17.0", {"start": v(337.5, -5) * mm, "end": v(342.5, -5) * mm});
            skLineSegment(sketch, "E19.11.17.0", {"start": v(335.5, 36.17) * mm, "end": v(335.5, -3) * mm});
            skArc(sketch, "E19.14.17.0", {"start": v(342.5, -5) * mm, "mid": v(343.91, -4.41) * mm, "end": v(344.5, -3) * mm});
            skArc(sketch, "E19.18.17.0", {"start": v(335.5, -3) * mm, "mid": v(336.09, -4.41) * mm, "end": v(337.5, -5) * mm});
            skPoint(sketch, "E19.0.17.1", {"position": v(335.5, -39.64) * mm});
            skLineSegment(sketch, "E19.1.17.1", {"start": v(344.5, 1.53) * mm, "end": v(344.5, -37.64) * mm});
            skPoint(sketch, "E19.4.17.1", {"position": v(344.5, -39.64) * mm});
            skLineSegment(sketch, "E19.5.17.1", {"start": v(335.5, 1.53) * mm, "end": v(344.5, 1.53) * mm});
            skLineSegment(sketch, "E19.8.17.1", {"start": v(337.5, -39.64) * mm, "end": v(342.5, -39.64) * mm});
            skLineSegment(sketch, "E19.11.17.1", {"start": v(335.5, 1.53) * mm, "end": v(335.5, -37.64) * mm});
            skArc(sketch, "E19.14.17.1", {"start": v(342.5, -39.64) * mm, "mid": v(343.91, -39.06) * mm, "end": v(344.5, -37.64) * mm});
            skArc(sketch, "E19.18.17.1", {"start": v(335.5, -37.64) * mm, "mid": v(336.09, -39.06) * mm, "end": v(337.5, -39.64) * mm});
            skPoint(sketch, "E19.0.17.2", {"position": v(335.5, -74.28) * mm});
            skLineSegment(sketch, "E19.1.17.2", {"start": v(344.5, -33.1) * mm, "end": v(344.5, -72.28) * mm});
            skPoint(sketch, "E19.4.17.2", {"position": v(344.5, -74.28) * mm});
            skLineSegment(sketch, "E19.5.17.2", {"start": v(335.5, -33.1) * mm, "end": v(344.5, -33.1) * mm});
            skLineSegment(sketch, "E19.8.17.2", {"start": v(337.5, -74.28) * mm, "end": v(342.5, -74.28) * mm});
            skLineSegment(sketch, "E19.11.17.2", {"start": v(335.5, -33.1) * mm, "end": v(335.5, -72.28) * mm});
            skArc(sketch, "E19.14.17.2", {"start": v(342.5, -74.28) * mm, "mid": v(343.91, -73.7) * mm, "end": v(344.5, -72.28) * mm});
            skArc(sketch, "E19.18.17.2", {"start": v(335.5, -72.28) * mm, "mid": v(336.09, -73.7) * mm, "end": v(337.5, -74.28) * mm});
            skPoint(sketch, "E19.0.17.3", {"position": v(335.5, -108.92) * mm});
            skLineSegment(sketch, "E19.1.17.3", {"start": v(344.5, -67.75) * mm, "end": v(344.5, -106.92) * mm});
            skPoint(sketch, "E19.4.17.3", {"position": v(344.5, -108.92) * mm});
            skLineSegment(sketch, "E19.5.17.3", {"start": v(335.5, -67.75) * mm, "end": v(344.5, -67.75) * mm});
            skLineSegment(sketch, "E19.8.17.3", {"start": v(337.5, -108.92) * mm, "end": v(342.5, -108.92) * mm});
            skLineSegment(sketch, "E19.11.17.3", {"start": v(335.5, -67.75) * mm, "end": v(335.5, -106.92) * mm});
            skArc(sketch, "E19.14.17.3", {"start": v(342.5, -108.92) * mm, "mid": v(343.91, -108.34) * mm, "end": v(344.5, -106.92) * mm});
            skArc(sketch, "E19.18.17.3", {"start": v(335.5, -106.92) * mm, "mid": v(336.09, -108.34) * mm, "end": v(337.5, -108.92) * mm});
            skPoint(sketch, "E19.0.17.4", {"position": v(335.5, -143.56) * mm});
            skLineSegment(sketch, "E19.1.17.4", {"start": v(344.5, -102.4) * mm, "end": v(344.5, -141.56) * mm});
            skPoint(sketch, "E19.4.17.4", {"position": v(344.5, -143.56) * mm});
            skLineSegment(sketch, "E19.5.17.4", {"start": v(335.5, -102.4) * mm, "end": v(344.5, -102.4) * mm});
            skLineSegment(sketch, "E19.8.17.4", {"start": v(337.5, -143.56) * mm, "end": v(342.5, -143.56) * mm});
            skLineSegment(sketch, "E19.11.17.4", {"start": v(335.5, -102.4) * mm, "end": v(335.5, -141.56) * mm});
            skArc(sketch, "E19.14.17.4", {"start": v(342.5, -143.56) * mm, "mid": v(343.91, -142.98) * mm, "end": v(344.5, -141.56) * mm});
            skArc(sketch, "E19.18.17.4", {"start": v(335.5, -141.56) * mm, "mid": v(336.09, -142.98) * mm, "end": v(337.5, -143.56) * mm});
            skPoint(sketch, "E19.0.17.5", {"position": v(335.5, -178.2) * mm});
            skLineSegment(sketch, "E19.1.17.5", {"start": v(344.5, -137.03) * mm, "end": v(344.5, -176.2) * mm});
            skPoint(sketch, "E19.4.17.5", {"position": v(344.5, -178.2) * mm});
            skLineSegment(sketch, "E19.5.17.5", {"start": v(335.5, -137.03) * mm, "end": v(344.5, -137.03) * mm});
            skLineSegment(sketch, "E19.8.17.5", {"start": v(337.5, -178.2) * mm, "end": v(342.5, -178.2) * mm});
            skLineSegment(sketch, "E19.11.17.5", {"start": v(335.5, -137.03) * mm, "end": v(335.5, -176.2) * mm});
            skArc(sketch, "E19.14.17.5", {"start": v(342.5, -178.2) * mm, "mid": v(343.91, -177.62) * mm, "end": v(344.5, -176.2) * mm});
            skArc(sketch, "E19.18.17.5", {"start": v(335.5, -176.2) * mm, "mid": v(336.09, -177.62) * mm, "end": v(337.5, -178.2) * mm});
            skPoint(sketch, "E19.0.17.6", {"position": v(335.5, -212.85) * mm});
            skLineSegment(sketch, "E19.1.17.6", {"start": v(344.5, -171.67) * mm, "end": v(344.5, -210.85) * mm});
            skPoint(sketch, "E19.4.17.6", {"position": v(344.5, -212.85) * mm});
            skLineSegment(sketch, "E19.5.17.6", {"start": v(335.5, -171.67) * mm, "end": v(344.5, -171.67) * mm});
            skLineSegment(sketch, "E19.8.17.6", {"start": v(337.5, -212.85) * mm, "end": v(342.5, -212.85) * mm});
            skLineSegment(sketch, "E19.11.17.6", {"start": v(335.5, -171.67) * mm, "end": v(335.5, -210.85) * mm});
            skArc(sketch, "E19.14.17.6", {"start": v(342.5, -212.85) * mm, "mid": v(343.91, -212.26) * mm, "end": v(344.5, -210.85) * mm});
            skArc(sketch, "E19.18.17.6", {"start": v(335.5, -210.85) * mm, "mid": v(336.09, -212.26) * mm, "end": v(337.5, -212.85) * mm});
            skPoint(sketch, "E19.0.17.7", {"position": v(335.5, -247.49) * mm});
            skLineSegment(sketch, "E19.1.17.7", {"start": v(344.5, -206.31) * mm, "end": v(344.5, -245.49) * mm});
            skPoint(sketch, "E19.4.17.7", {"position": v(344.5, -247.49) * mm});
            skLineSegment(sketch, "E19.5.17.7", {"start": v(335.5, -206.31) * mm, "end": v(344.5, -206.31) * mm});
            skLineSegment(sketch, "E19.8.17.7", {"start": v(337.5, -247.49) * mm, "end": v(342.5, -247.49) * mm});
            skLineSegment(sketch, "E19.11.17.7", {"start": v(335.5, -206.31) * mm, "end": v(335.5, -245.49) * mm});
            skArc(sketch, "E19.14.17.7", {"start": v(342.5, -247.49) * mm, "mid": v(343.91, -246.9) * mm, "end": v(344.5, -245.49) * mm});
            skArc(sketch, "E19.18.17.7", {"start": v(335.5, -245.49) * mm, "mid": v(336.09, -246.9) * mm, "end": v(337.5, -247.49) * mm});
            skPoint(sketch, "E19.0.17.8", {"position": v(335.5, -282.13) * mm});
            skLineSegment(sketch, "E19.1.17.8", {"start": v(344.5, -240.95) * mm, "end": v(344.5, -280.13) * mm});
            skPoint(sketch, "E19.4.17.8", {"position": v(344.5, -282.13) * mm});
            skLineSegment(sketch, "E19.5.17.8", {"start": v(335.5, -240.95) * mm, "end": v(344.5, -240.95) * mm});
            skLineSegment(sketch, "E19.8.17.8", {"start": v(337.5, -282.13) * mm, "end": v(342.5, -282.13) * mm});
            skLineSegment(sketch, "E19.11.17.8", {"start": v(335.5, -240.95) * mm, "end": v(335.5, -280.13) * mm});
            skArc(sketch, "E19.14.17.8", {"start": v(342.5, -282.13) * mm, "mid": v(343.91, -281.54) * mm, "end": v(344.5, -280.13) * mm});
            skArc(sketch, "E19.18.17.8", {"start": v(335.5, -280.13) * mm, "mid": v(336.09, -281.54) * mm, "end": v(337.5, -282.13) * mm});
            skPoint(sketch, "E19.0.17.9", {"position": v(335.5, -316.77) * mm});
            skLineSegment(sketch, "E19.1.17.9", {"start": v(344.5, -275.6) * mm, "end": v(344.5, -314.77) * mm});
            skPoint(sketch, "E19.4.17.9", {"position": v(344.5, -316.77) * mm});
            skLineSegment(sketch, "E19.5.17.9", {"start": v(335.5, -275.6) * mm, "end": v(344.5, -275.6) * mm});
            skLineSegment(sketch, "E19.8.17.9", {"start": v(337.5, -316.77) * mm, "end": v(342.5, -316.77) * mm});
            skLineSegment(sketch, "E19.11.17.9", {"start": v(335.5, -275.6) * mm, "end": v(335.5, -314.77) * mm});
            skArc(sketch, "E19.14.17.9", {"start": v(342.5, -316.77) * mm, "mid": v(343.91, -316.18) * mm, "end": v(344.5, -314.77) * mm});
            skArc(sketch, "E19.18.17.9", {"start": v(335.5, -314.77) * mm, "mid": v(336.09, -316.18) * mm, "end": v(337.5, -316.77) * mm});
            skPoint(sketch, "E19.0.17.10", {"position": v(335.5, -351.41) * mm});
            skLineSegment(sketch, "E19.1.17.10", {"start": v(344.5, -310.24) * mm, "end": v(344.5, -349.41) * mm});
            skPoint(sketch, "E19.4.17.10", {"position": v(344.5, -351.41) * mm});
            skLineSegment(sketch, "E19.5.17.10", {"start": v(335.5, -310.24) * mm, "end": v(344.5, -310.24) * mm});
            skLineSegment(sketch, "E19.8.17.10", {"start": v(337.5, -351.41) * mm, "end": v(342.5, -351.41) * mm});
            skLineSegment(sketch, "E19.11.17.10", {"start": v(335.5, -310.24) * mm, "end": v(335.5, -349.41) * mm});
            skArc(sketch, "E19.14.17.10", {"start": v(342.5, -351.41) * mm, "mid": v(343.91, -350.82) * mm, "end": v(344.5, -349.41) * mm});
            skArc(sketch, "E19.18.17.10", {"start": v(335.5, -349.41) * mm, "mid": v(336.09, -350.82) * mm, "end": v(337.5, -351.41) * mm});
            skPoint(sketch, "E19.0.17.11", {"position": v(335.5, -386.05) * mm});
            skLineSegment(sketch, "E19.1.17.11", {"start": v(344.5, -344.88) * mm, "end": v(344.5, -384.05) * mm});
            skPoint(sketch, "E19.4.17.11", {"position": v(344.5, -386.05) * mm});
            skLineSegment(sketch, "E19.5.17.11", {"start": v(335.5, -344.88) * mm, "end": v(344.5, -344.88) * mm});
            skLineSegment(sketch, "E19.8.17.11", {"start": v(337.5, -386.05) * mm, "end": v(342.5, -386.05) * mm});
            skLineSegment(sketch, "E19.11.17.11", {"start": v(335.5, -344.88) * mm, "end": v(335.5, -384.05) * mm});
            skArc(sketch, "E19.14.17.11", {"start": v(342.5, -386.05) * mm, "mid": v(343.91, -385.47) * mm, "end": v(344.5, -384.05) * mm});
            skArc(sketch, "E19.18.17.11", {"start": v(335.5, -384.05) * mm, "mid": v(336.09, -385.47) * mm, "end": v(337.5, -386.05) * mm});
            skPoint(sketch, "E19.0.17.12", {"position": v(335.5, -420.7) * mm});
            skLineSegment(sketch, "E19.1.17.12", {"start": v(344.5, -379.52) * mm, "end": v(344.5, -418.7) * mm});
            skPoint(sketch, "E19.4.17.12", {"position": v(344.5, -420.7) * mm});
            skLineSegment(sketch, "E19.5.17.12", {"start": v(335.5, -379.52) * mm, "end": v(344.5, -379.52) * mm});
            skLineSegment(sketch, "E19.8.17.12", {"start": v(337.5, -420.7) * mm, "end": v(342.5, -420.7) * mm});
            skLineSegment(sketch, "E19.11.17.12", {"start": v(335.5, -379.52) * mm, "end": v(335.5, -418.7) * mm});
            skArc(sketch, "E19.14.17.12", {"start": v(342.5, -420.7) * mm, "mid": v(343.91, -420.1) * mm, "end": v(344.5, -418.7) * mm});
            skArc(sketch, "E19.18.17.12", {"start": v(335.5, -418.7) * mm, "mid": v(336.09, -420.1) * mm, "end": v(337.5, -420.7) * mm});
            skPoint(sketch, "E19.0.17.13", {"position": v(335.5, -455.33) * mm});
            skLineSegment(sketch, "E19.1.17.13", {"start": v(344.5, -414.16) * mm, "end": v(344.5, -453.33) * mm});
            skPoint(sketch, "E19.4.17.13", {"position": v(344.5, -455.33) * mm});
            skLineSegment(sketch, "E19.5.17.13", {"start": v(335.5, -414.16) * mm, "end": v(344.5, -414.16) * mm});
            skLineSegment(sketch, "E19.8.17.13", {"start": v(337.5, -455.33) * mm, "end": v(342.5, -455.33) * mm});
            skLineSegment(sketch, "E19.11.17.13", {"start": v(335.5, -414.16) * mm, "end": v(335.5, -453.33) * mm});
            skArc(sketch, "E19.14.17.13", {"start": v(342.5, -455.33) * mm, "mid": v(343.91, -454.75) * mm, "end": v(344.5, -453.33) * mm});
            skArc(sketch, "E19.18.17.13", {"start": v(335.5, -453.33) * mm, "mid": v(336.09, -454.75) * mm, "end": v(337.5, -455.33) * mm});
            skPoint(sketch, "E19.0.17.14", {"position": v(335.5, -489.97) * mm});
            skLineSegment(sketch, "E19.1.17.14", {"start": v(344.5, -448.8) * mm, "end": v(344.5, -487.97) * mm});
            skPoint(sketch, "E19.4.17.14", {"position": v(344.5, -489.97) * mm});
            skLineSegment(sketch, "E19.5.17.14", {"start": v(335.5, -448.8) * mm, "end": v(344.5, -448.8) * mm});
            skLineSegment(sketch, "E19.8.17.14", {"start": v(337.5, -489.97) * mm, "end": v(342.5, -489.97) * mm});
            skLineSegment(sketch, "E19.11.17.14", {"start": v(335.5, -448.8) * mm, "end": v(335.5, -487.97) * mm});
            skArc(sketch, "E19.14.17.14", {"start": v(342.5, -489.97) * mm, "mid": v(343.91, -489.39) * mm, "end": v(344.5, -487.97) * mm});
            skArc(sketch, "E19.18.17.14", {"start": v(335.5, -487.97) * mm, "mid": v(336.09, -489.39) * mm, "end": v(337.5, -489.97) * mm});
            skPoint(sketch, "E19.0.18.0", {"position": v(355.5, -5) * mm});
            skLineSegment(sketch, "E19.1.18.0", {"start": v(364.5, 36.17) * mm, "end": v(364.5, -3) * mm});
            skPoint(sketch, "E19.4.18.0", {"position": v(364.5, -5) * mm});
            skLineSegment(sketch, "E19.5.18.0", {"start": v(355.5, 36.17) * mm, "end": v(364.5, 36.17) * mm});
            skLineSegment(sketch, "E19.8.18.0", {"start": v(357.5, -5) * mm, "end": v(362.5, -5) * mm});
            skLineSegment(sketch, "E19.11.18.0", {"start": v(355.5, 36.17) * mm, "end": v(355.5, -3) * mm});
            skArc(sketch, "E19.14.18.0", {"start": v(362.5, -5) * mm, "mid": v(363.91, -4.41) * mm, "end": v(364.5, -3) * mm});
            skArc(sketch, "E19.18.18.0", {"start": v(355.5, -3) * mm, "mid": v(356.09, -4.41) * mm, "end": v(357.5, -5) * mm});
            skPoint(sketch, "E19.0.18.1", {"position": v(355.5, -39.64) * mm});
            skLineSegment(sketch, "E19.1.18.1", {"start": v(364.5, 1.53) * mm, "end": v(364.5, -37.64) * mm});
            skPoint(sketch, "E19.4.18.1", {"position": v(364.5, -39.64) * mm});
            skLineSegment(sketch, "E19.5.18.1", {"start": v(355.5, 1.53) * mm, "end": v(364.5, 1.53) * mm});
            skLineSegment(sketch, "E19.8.18.1", {"start": v(357.5, -39.64) * mm, "end": v(362.5, -39.64) * mm});
            skLineSegment(sketch, "E19.11.18.1", {"start": v(355.5, 1.53) * mm, "end": v(355.5, -37.64) * mm});
            skArc(sketch, "E19.14.18.1", {"start": v(362.5, -39.64) * mm, "mid": v(363.91, -39.06) * mm, "end": v(364.5, -37.64) * mm});
            skArc(sketch, "E19.18.18.1", {"start": v(355.5, -37.64) * mm, "mid": v(356.09, -39.06) * mm, "end": v(357.5, -39.64) * mm});
            skPoint(sketch, "E19.0.18.2", {"position": v(355.5, -74.28) * mm});
            skLineSegment(sketch, "E19.1.18.2", {"start": v(364.5, -33.1) * mm, "end": v(364.5, -72.28) * mm});
            skPoint(sketch, "E19.4.18.2", {"position": v(364.5, -74.28) * mm});
            skLineSegment(sketch, "E19.5.18.2", {"start": v(355.5, -33.1) * mm, "end": v(364.5, -33.1) * mm});
            skLineSegment(sketch, "E19.8.18.2", {"start": v(357.5, -74.28) * mm, "end": v(362.5, -74.28) * mm});
            skLineSegment(sketch, "E19.11.18.2", {"start": v(355.5, -33.1) * mm, "end": v(355.5, -72.28) * mm});
            skArc(sketch, "E19.14.18.2", {"start": v(362.5, -74.28) * mm, "mid": v(363.91, -73.7) * mm, "end": v(364.5, -72.28) * mm});
            skArc(sketch, "E19.18.18.2", {"start": v(355.5, -72.28) * mm, "mid": v(356.09, -73.7) * mm, "end": v(357.5, -74.28) * mm});
            skPoint(sketch, "E19.0.18.3", {"position": v(355.5, -108.92) * mm});
            skLineSegment(sketch, "E19.1.18.3", {"start": v(364.5, -67.75) * mm, "end": v(364.5, -106.92) * mm});
            skPoint(sketch, "E19.4.18.3", {"position": v(364.5, -108.92) * mm});
            skLineSegment(sketch, "E19.5.18.3", {"start": v(355.5, -67.75) * mm, "end": v(364.5, -67.75) * mm});
            skLineSegment(sketch, "E19.8.18.3", {"start": v(357.5, -108.92) * mm, "end": v(362.5, -108.92) * mm});
            skLineSegment(sketch, "E19.11.18.3", {"start": v(355.5, -67.75) * mm, "end": v(355.5, -106.92) * mm});
            skArc(sketch, "E19.14.18.3", {"start": v(362.5, -108.92) * mm, "mid": v(363.91, -108.34) * mm, "end": v(364.5, -106.92) * mm});
            skArc(sketch, "E19.18.18.3", {"start": v(355.5, -106.92) * mm, "mid": v(356.09, -108.34) * mm, "end": v(357.5, -108.92) * mm});
            skPoint(sketch, "E19.0.18.4", {"position": v(355.5, -143.56) * mm});
            skLineSegment(sketch, "E19.1.18.4", {"start": v(364.5, -102.4) * mm, "end": v(364.5, -141.56) * mm});
            skPoint(sketch, "E19.4.18.4", {"position": v(364.5, -143.56) * mm});
            skLineSegment(sketch, "E19.5.18.4", {"start": v(355.5, -102.4) * mm, "end": v(364.5, -102.4) * mm});
            skLineSegment(sketch, "E19.8.18.4", {"start": v(357.5, -143.56) * mm, "end": v(362.5, -143.56) * mm});
            skLineSegment(sketch, "E19.11.18.4", {"start": v(355.5, -102.4) * mm, "end": v(355.5, -141.56) * mm});
            skArc(sketch, "E19.14.18.4", {"start": v(362.5, -143.56) * mm, "mid": v(363.91, -142.98) * mm, "end": v(364.5, -141.56) * mm});
            skArc(sketch, "E19.18.18.4", {"start": v(355.5, -141.56) * mm, "mid": v(356.09, -142.98) * mm, "end": v(357.5, -143.56) * mm});
            skPoint(sketch, "E19.0.18.5", {"position": v(355.5, -178.2) * mm});
            skLineSegment(sketch, "E19.1.18.5", {"start": v(364.5, -137.03) * mm, "end": v(364.5, -176.2) * mm});
            skPoint(sketch, "E19.4.18.5", {"position": v(364.5, -178.2) * mm});
            skLineSegment(sketch, "E19.5.18.5", {"start": v(355.5, -137.03) * mm, "end": v(364.5, -137.03) * mm});
            skLineSegment(sketch, "E19.8.18.5", {"start": v(357.5, -178.2) * mm, "end": v(362.5, -178.2) * mm});
            skLineSegment(sketch, "E19.11.18.5", {"start": v(355.5, -137.03) * mm, "end": v(355.5, -176.2) * mm});
            skArc(sketch, "E19.14.18.5", {"start": v(362.5, -178.2) * mm, "mid": v(363.91, -177.62) * mm, "end": v(364.5, -176.2) * mm});
            skArc(sketch, "E19.18.18.5", {"start": v(355.5, -176.2) * mm, "mid": v(356.09, -177.62) * mm, "end": v(357.5, -178.2) * mm});
            skPoint(sketch, "E19.0.18.6", {"position": v(355.5, -212.85) * mm});
            skLineSegment(sketch, "E19.1.18.6", {"start": v(364.5, -171.67) * mm, "end": v(364.5, -210.85) * mm});
            skPoint(sketch, "E19.4.18.6", {"position": v(364.5, -212.85) * mm});
            skLineSegment(sketch, "E19.5.18.6", {"start": v(355.5, -171.67) * mm, "end": v(364.5, -171.67) * mm});
            skLineSegment(sketch, "E19.8.18.6", {"start": v(357.5, -212.85) * mm, "end": v(362.5, -212.85) * mm});
            skLineSegment(sketch, "E19.11.18.6", {"start": v(355.5, -171.67) * mm, "end": v(355.5, -210.85) * mm});
            skArc(sketch, "E19.14.18.6", {"start": v(362.5, -212.85) * mm, "mid": v(363.91, -212.26) * mm, "end": v(364.5, -210.85) * mm});
            skArc(sketch, "E19.18.18.6", {"start": v(355.5, -210.85) * mm, "mid": v(356.09, -212.26) * mm, "end": v(357.5, -212.85) * mm});
            skPoint(sketch, "E19.0.18.7", {"position": v(355.5, -247.49) * mm});
            skLineSegment(sketch, "E19.1.18.7", {"start": v(364.5, -206.31) * mm, "end": v(364.5, -245.49) * mm});
            skPoint(sketch, "E19.4.18.7", {"position": v(364.5, -247.49) * mm});
            skLineSegment(sketch, "E19.5.18.7", {"start": v(355.5, -206.31) * mm, "end": v(364.5, -206.31) * mm});
            skLineSegment(sketch, "E19.8.18.7", {"start": v(357.5, -247.49) * mm, "end": v(362.5, -247.49) * mm});
            skLineSegment(sketch, "E19.11.18.7", {"start": v(355.5, -206.31) * mm, "end": v(355.5, -245.49) * mm});
            skArc(sketch, "E19.14.18.7", {"start": v(362.5, -247.49) * mm, "mid": v(363.91, -246.9) * mm, "end": v(364.5, -245.49) * mm});
            skArc(sketch, "E19.18.18.7", {"start": v(355.5, -245.49) * mm, "mid": v(356.09, -246.9) * mm, "end": v(357.5, -247.49) * mm});
            skPoint(sketch, "E19.0.18.8", {"position": v(355.5, -282.13) * mm});
            skLineSegment(sketch, "E19.1.18.8", {"start": v(364.5, -240.95) * mm, "end": v(364.5, -280.13) * mm});
            skPoint(sketch, "E19.4.18.8", {"position": v(364.5, -282.13) * mm});
            skLineSegment(sketch, "E19.5.18.8", {"start": v(355.5, -240.95) * mm, "end": v(364.5, -240.95) * mm});
            skLineSegment(sketch, "E19.8.18.8", {"start": v(357.5, -282.13) * mm, "end": v(362.5, -282.13) * mm});
            skLineSegment(sketch, "E19.11.18.8", {"start": v(355.5, -240.95) * mm, "end": v(355.5, -280.13) * mm});
            skArc(sketch, "E19.14.18.8", {"start": v(362.5, -282.13) * mm, "mid": v(363.91, -281.54) * mm, "end": v(364.5, -280.13) * mm});
            skArc(sketch, "E19.18.18.8", {"start": v(355.5, -280.13) * mm, "mid": v(356.09, -281.54) * mm, "end": v(357.5, -282.13) * mm});
            skPoint(sketch, "E19.0.18.9", {"position": v(355.5, -316.77) * mm});
            skLineSegment(sketch, "E19.1.18.9", {"start": v(364.5, -275.6) * mm, "end": v(364.5, -314.77) * mm});
            skPoint(sketch, "E19.4.18.9", {"position": v(364.5, -316.77) * mm});
            skLineSegment(sketch, "E19.5.18.9", {"start": v(355.5, -275.6) * mm, "end": v(364.5, -275.6) * mm});
            skLineSegment(sketch, "E19.8.18.9", {"start": v(357.5, -316.77) * mm, "end": v(362.5, -316.77) * mm});
            skLineSegment(sketch, "E19.11.18.9", {"start": v(355.5, -275.6) * mm, "end": v(355.5, -314.77) * mm});
            skArc(sketch, "E19.14.18.9", {"start": v(362.5, -316.77) * mm, "mid": v(363.91, -316.18) * mm, "end": v(364.5, -314.77) * mm});
            skArc(sketch, "E19.18.18.9", {"start": v(355.5, -314.77) * mm, "mid": v(356.09, -316.18) * mm, "end": v(357.5, -316.77) * mm});
            skPoint(sketch, "E19.0.18.10", {"position": v(355.5, -351.41) * mm});
            skLineSegment(sketch, "E19.1.18.10", {"start": v(364.5, -310.24) * mm, "end": v(364.5, -349.41) * mm});
            skPoint(sketch, "E19.4.18.10", {"position": v(364.5, -351.41) * mm});
            skLineSegment(sketch, "E19.5.18.10", {"start": v(355.5, -310.24) * mm, "end": v(364.5, -310.24) * mm});
            skLineSegment(sketch, "E19.8.18.10", {"start": v(357.5, -351.41) * mm, "end": v(362.5, -351.41) * mm});
            skLineSegment(sketch, "E19.11.18.10", {"start": v(355.5, -310.24) * mm, "end": v(355.5, -349.41) * mm});
            skArc(sketch, "E19.14.18.10", {"start": v(362.5, -351.41) * mm, "mid": v(363.91, -350.82) * mm, "end": v(364.5, -349.41) * mm});
            skArc(sketch, "E19.18.18.10", {"start": v(355.5, -349.41) * mm, "mid": v(356.09, -350.82) * mm, "end": v(357.5, -351.41) * mm});
            skPoint(sketch, "E19.0.18.11", {"position": v(355.5, -386.05) * mm});
            skLineSegment(sketch, "E19.1.18.11", {"start": v(364.5, -344.88) * mm, "end": v(364.5, -384.05) * mm});
            skPoint(sketch, "E19.4.18.11", {"position": v(364.5, -386.05) * mm});
            skLineSegment(sketch, "E19.5.18.11", {"start": v(355.5, -344.88) * mm, "end": v(364.5, -344.88) * mm});
            skLineSegment(sketch, "E19.8.18.11", {"start": v(357.5, -386.05) * mm, "end": v(362.5, -386.05) * mm});
            skLineSegment(sketch, "E19.11.18.11", {"start": v(355.5, -344.88) * mm, "end": v(355.5, -384.05) * mm});
            skArc(sketch, "E19.14.18.11", {"start": v(362.5, -386.05) * mm, "mid": v(363.91, -385.47) * mm, "end": v(364.5, -384.05) * mm});
            skArc(sketch, "E19.18.18.11", {"start": v(355.5, -384.05) * mm, "mid": v(356.09, -385.47) * mm, "end": v(357.5, -386.05) * mm});
            skPoint(sketch, "E19.0.18.12", {"position": v(355.5, -420.7) * mm});
            skLineSegment(sketch, "E19.1.18.12", {"start": v(364.5, -379.52) * mm, "end": v(364.5, -418.7) * mm});
            skPoint(sketch, "E19.4.18.12", {"position": v(364.5, -420.7) * mm});
            skLineSegment(sketch, "E19.5.18.12", {"start": v(355.5, -379.52) * mm, "end": v(364.5, -379.52) * mm});
            skLineSegment(sketch, "E19.8.18.12", {"start": v(357.5, -420.7) * mm, "end": v(362.5, -420.7) * mm});
            skLineSegment(sketch, "E19.11.18.12", {"start": v(355.5, -379.52) * mm, "end": v(355.5, -418.7) * mm});
            skArc(sketch, "E19.14.18.12", {"start": v(362.5, -420.7) * mm, "mid": v(363.91, -420.1) * mm, "end": v(364.5, -418.7) * mm});
            skArc(sketch, "E19.18.18.12", {"start": v(355.5, -418.7) * mm, "mid": v(356.09, -420.1) * mm, "end": v(357.5, -420.7) * mm});
            skPoint(sketch, "E19.0.18.13", {"position": v(355.5, -455.33) * mm});
            skLineSegment(sketch, "E19.1.18.13", {"start": v(364.5, -414.16) * mm, "end": v(364.5, -453.33) * mm});
            skPoint(sketch, "E19.4.18.13", {"position": v(364.5, -455.33) * mm});
            skLineSegment(sketch, "E19.5.18.13", {"start": v(355.5, -414.16) * mm, "end": v(364.5, -414.16) * mm});
            skLineSegment(sketch, "E19.8.18.13", {"start": v(357.5, -455.33) * mm, "end": v(362.5, -455.33) * mm});
            skLineSegment(sketch, "E19.11.18.13", {"start": v(355.5, -414.16) * mm, "end": v(355.5, -453.33) * mm});
            skArc(sketch, "E19.14.18.13", {"start": v(362.5, -455.33) * mm, "mid": v(363.91, -454.75) * mm, "end": v(364.5, -453.33) * mm});
            skArc(sketch, "E19.18.18.13", {"start": v(355.5, -453.33) * mm, "mid": v(356.09, -454.75) * mm, "end": v(357.5, -455.33) * mm});
            skPoint(sketch, "E19.0.18.14", {"position": v(355.5, -489.97) * mm});
            skLineSegment(sketch, "E19.1.18.14", {"start": v(364.5, -448.8) * mm, "end": v(364.5, -487.97) * mm});
            skPoint(sketch, "E19.4.18.14", {"position": v(364.5, -489.97) * mm});
            skLineSegment(sketch, "E19.5.18.14", {"start": v(355.5, -448.8) * mm, "end": v(364.5, -448.8) * mm});
            skLineSegment(sketch, "E19.8.18.14", {"start": v(357.5, -489.97) * mm, "end": v(362.5, -489.97) * mm});
            skLineSegment(sketch, "E19.11.18.14", {"start": v(355.5, -448.8) * mm, "end": v(355.5, -487.97) * mm});
            skArc(sketch, "E19.14.18.14", {"start": v(362.5, -489.97) * mm, "mid": v(363.91, -489.39) * mm, "end": v(364.5, -487.97) * mm});
            skArc(sketch, "E19.18.18.14", {"start": v(355.5, -487.97) * mm, "mid": v(356.09, -489.39) * mm, "end": v(357.5, -489.97) * mm});
            skPoint(sketch, "E19.0.19.0", {"position": v(375.5, -5) * mm});
            skLineSegment(sketch, "E19.1.19.0", {"start": v(384.5, 36.17) * mm, "end": v(384.5, -3) * mm});
            skPoint(sketch, "E19.4.19.0", {"position": v(384.5, -5) * mm});
            skLineSegment(sketch, "E19.5.19.0", {"start": v(375.5, 36.17) * mm, "end": v(384.5, 36.17) * mm});
            skLineSegment(sketch, "E19.8.19.0", {"start": v(377.5, -5) * mm, "end": v(382.5, -5) * mm});
            skLineSegment(sketch, "E19.11.19.0", {"start": v(375.5, 36.17) * mm, "end": v(375.5, -3) * mm});
            skArc(sketch, "E19.14.19.0", {"start": v(382.5, -5) * mm, "mid": v(383.91, -4.41) * mm, "end": v(384.5, -3) * mm});
            skArc(sketch, "E19.18.19.0", {"start": v(375.5, -3) * mm, "mid": v(376.09, -4.41) * mm, "end": v(377.5, -5) * mm});
            skPoint(sketch, "E19.0.19.1", {"position": v(375.5, -39.64) * mm});
            skLineSegment(sketch, "E19.1.19.1", {"start": v(384.5, 1.53) * mm, "end": v(384.5, -37.64) * mm});
            skPoint(sketch, "E19.4.19.1", {"position": v(384.5, -39.64) * mm});
            skLineSegment(sketch, "E19.5.19.1", {"start": v(375.5, 1.53) * mm, "end": v(384.5, 1.53) * mm});
            skLineSegment(sketch, "E19.8.19.1", {"start": v(377.5, -39.64) * mm, "end": v(382.5, -39.64) * mm});
            skLineSegment(sketch, "E19.11.19.1", {"start": v(375.5, 1.53) * mm, "end": v(375.5, -37.64) * mm});
            skArc(sketch, "E19.14.19.1", {"start": v(382.5, -39.64) * mm, "mid": v(383.91, -39.06) * mm, "end": v(384.5, -37.64) * mm});
            skArc(sketch, "E19.18.19.1", {"start": v(375.5, -37.64) * mm, "mid": v(376.09, -39.06) * mm, "end": v(377.5, -39.64) * mm});
            skPoint(sketch, "E19.0.19.2", {"position": v(375.5, -74.28) * mm});
            skLineSegment(sketch, "E19.1.19.2", {"start": v(384.5, -33.1) * mm, "end": v(384.5, -72.28) * mm});
            skPoint(sketch, "E19.4.19.2", {"position": v(384.5, -74.28) * mm});
            skLineSegment(sketch, "E19.5.19.2", {"start": v(375.5, -33.1) * mm, "end": v(384.5, -33.1) * mm});
            skLineSegment(sketch, "E19.8.19.2", {"start": v(377.5, -74.28) * mm, "end": v(382.5, -74.28) * mm});
            skLineSegment(sketch, "E19.11.19.2", {"start": v(375.5, -33.1) * mm, "end": v(375.5, -72.28) * mm});
            skArc(sketch, "E19.14.19.2", {"start": v(382.5, -74.28) * mm, "mid": v(383.91, -73.7) * mm, "end": v(384.5, -72.28) * mm});
            skArc(sketch, "E19.18.19.2", {"start": v(375.5, -72.28) * mm, "mid": v(376.09, -73.7) * mm, "end": v(377.5, -74.28) * mm});
            skPoint(sketch, "E19.0.19.3", {"position": v(375.5, -108.92) * mm});
            skLineSegment(sketch, "E19.1.19.3", {"start": v(384.5, -67.75) * mm, "end": v(384.5, -106.92) * mm});
            skPoint(sketch, "E19.4.19.3", {"position": v(384.5, -108.92) * mm});
            skLineSegment(sketch, "E19.5.19.3", {"start": v(375.5, -67.75) * mm, "end": v(384.5, -67.75) * mm});
            skLineSegment(sketch, "E19.8.19.3", {"start": v(377.5, -108.92) * mm, "end": v(382.5, -108.92) * mm});
            skLineSegment(sketch, "E19.11.19.3", {"start": v(375.5, -67.75) * mm, "end": v(375.5, -106.92) * mm});
            skArc(sketch, "E19.14.19.3", {"start": v(382.5, -108.92) * mm, "mid": v(383.91, -108.34) * mm, "end": v(384.5, -106.92) * mm});
            skArc(sketch, "E19.18.19.3", {"start": v(375.5, -106.92) * mm, "mid": v(376.09, -108.34) * mm, "end": v(377.5, -108.92) * mm});
            skPoint(sketch, "E19.0.19.4", {"position": v(375.5, -143.56) * mm});
            skLineSegment(sketch, "E19.1.19.4", {"start": v(384.5, -102.4) * mm, "end": v(384.5, -141.56) * mm});
            skPoint(sketch, "E19.4.19.4", {"position": v(384.5, -143.56) * mm});
            skLineSegment(sketch, "E19.5.19.4", {"start": v(375.5, -102.4) * mm, "end": v(384.5, -102.4) * mm});
            skLineSegment(sketch, "E19.8.19.4", {"start": v(377.5, -143.56) * mm, "end": v(382.5, -143.56) * mm});
            skLineSegment(sketch, "E19.11.19.4", {"start": v(375.5, -102.4) * mm, "end": v(375.5, -141.56) * mm});
            skArc(sketch, "E19.14.19.4", {"start": v(382.5, -143.56) * mm, "mid": v(383.91, -142.98) * mm, "end": v(384.5, -141.56) * mm});
            skArc(sketch, "E19.18.19.4", {"start": v(375.5, -141.56) * mm, "mid": v(376.09, -142.98) * mm, "end": v(377.5, -143.56) * mm});
            skPoint(sketch, "E19.0.19.5", {"position": v(375.5, -178.2) * mm});
            skLineSegment(sketch, "E19.1.19.5", {"start": v(384.5, -137.03) * mm, "end": v(384.5, -176.2) * mm});
            skPoint(sketch, "E19.4.19.5", {"position": v(384.5, -178.2) * mm});
            skLineSegment(sketch, "E19.5.19.5", {"start": v(375.5, -137.03) * mm, "end": v(384.5, -137.03) * mm});
            skLineSegment(sketch, "E19.8.19.5", {"start": v(377.5, -178.2) * mm, "end": v(382.5, -178.2) * mm});
            skLineSegment(sketch, "E19.11.19.5", {"start": v(375.5, -137.03) * mm, "end": v(375.5, -176.2) * mm});
            skArc(sketch, "E19.14.19.5", {"start": v(382.5, -178.2) * mm, "mid": v(383.91, -177.62) * mm, "end": v(384.5, -176.2) * mm});
            skArc(sketch, "E19.18.19.5", {"start": v(375.5, -176.2) * mm, "mid": v(376.09, -177.62) * mm, "end": v(377.5, -178.2) * mm});
            skPoint(sketch, "E19.0.19.6", {"position": v(375.5, -212.85) * mm});
            skLineSegment(sketch, "E19.1.19.6", {"start": v(384.5, -171.67) * mm, "end": v(384.5, -210.85) * mm});
            skPoint(sketch, "E19.4.19.6", {"position": v(384.5, -212.85) * mm});
            skLineSegment(sketch, "E19.5.19.6", {"start": v(375.5, -171.67) * mm, "end": v(384.5, -171.67) * mm});
            skLineSegment(sketch, "E19.8.19.6", {"start": v(377.5, -212.85) * mm, "end": v(382.5, -212.85) * mm});
            skLineSegment(sketch, "E19.11.19.6", {"start": v(375.5, -171.67) * mm, "end": v(375.5, -210.85) * mm});
            skArc(sketch, "E19.14.19.6", {"start": v(382.5, -212.85) * mm, "mid": v(383.91, -212.26) * mm, "end": v(384.5, -210.85) * mm});
            skArc(sketch, "E19.18.19.6", {"start": v(375.5, -210.85) * mm, "mid": v(376.09, -212.26) * mm, "end": v(377.5, -212.85) * mm});
            skPoint(sketch, "E19.0.19.7", {"position": v(375.5, -247.49) * mm});
            skLineSegment(sketch, "E19.1.19.7", {"start": v(384.5, -206.31) * mm, "end": v(384.5, -245.49) * mm});
            skPoint(sketch, "E19.4.19.7", {"position": v(384.5, -247.49) * mm});
            skLineSegment(sketch, "E19.5.19.7", {"start": v(375.5, -206.31) * mm, "end": v(384.5, -206.31) * mm});
            skLineSegment(sketch, "E19.8.19.7", {"start": v(377.5, -247.49) * mm, "end": v(382.5, -247.49) * mm});
            skLineSegment(sketch, "E19.11.19.7", {"start": v(375.5, -206.31) * mm, "end": v(375.5, -245.49) * mm});
            skArc(sketch, "E19.14.19.7", {"start": v(382.5, -247.49) * mm, "mid": v(383.91, -246.9) * mm, "end": v(384.5, -245.49) * mm});
            skArc(sketch, "E19.18.19.7", {"start": v(375.5, -245.49) * mm, "mid": v(376.09, -246.9) * mm, "end": v(377.5, -247.49) * mm});
            skPoint(sketch, "E19.0.19.8", {"position": v(375.5, -282.13) * mm});
            skLineSegment(sketch, "E19.1.19.8", {"start": v(384.5, -240.95) * mm, "end": v(384.5, -280.13) * mm});
            skPoint(sketch, "E19.4.19.8", {"position": v(384.5, -282.13) * mm});
            skLineSegment(sketch, "E19.5.19.8", {"start": v(375.5, -240.95) * mm, "end": v(384.5, -240.95) * mm});
            skLineSegment(sketch, "E19.8.19.8", {"start": v(377.5, -282.13) * mm, "end": v(382.5, -282.13) * mm});
            skLineSegment(sketch, "E19.11.19.8", {"start": v(375.5, -240.95) * mm, "end": v(375.5, -280.13) * mm});
            skArc(sketch, "E19.14.19.8", {"start": v(382.5, -282.13) * mm, "mid": v(383.91, -281.54) * mm, "end": v(384.5, -280.13) * mm});
            skArc(sketch, "E19.18.19.8", {"start": v(375.5, -280.13) * mm, "mid": v(376.09, -281.54) * mm, "end": v(377.5, -282.13) * mm});
            skPoint(sketch, "E19.0.19.9", {"position": v(375.5, -316.77) * mm});
            skLineSegment(sketch, "E19.1.19.9", {"start": v(384.5, -275.6) * mm, "end": v(384.5, -314.77) * mm});
            skPoint(sketch, "E19.4.19.9", {"position": v(384.5, -316.77) * mm});
            skLineSegment(sketch, "E19.5.19.9", {"start": v(375.5, -275.6) * mm, "end": v(384.5, -275.6) * mm});
            skLineSegment(sketch, "E19.8.19.9", {"start": v(377.5, -316.77) * mm, "end": v(382.5, -316.77) * mm});
            skLineSegment(sketch, "E19.11.19.9", {"start": v(375.5, -275.6) * mm, "end": v(375.5, -314.77) * mm});
            skArc(sketch, "E19.14.19.9", {"start": v(382.5, -316.77) * mm, "mid": v(383.91, -316.18) * mm, "end": v(384.5, -314.77) * mm});
            skArc(sketch, "E19.18.19.9", {"start": v(375.5, -314.77) * mm, "mid": v(376.09, -316.18) * mm, "end": v(377.5, -316.77) * mm});
            skPoint(sketch, "E19.0.19.10", {"position": v(375.5, -351.41) * mm});
            skLineSegment(sketch, "E19.1.19.10", {"start": v(384.5, -310.24) * mm, "end": v(384.5, -349.41) * mm});
            skPoint(sketch, "E19.4.19.10", {"position": v(384.5, -351.41) * mm});
            skLineSegment(sketch, "E19.5.19.10", {"start": v(375.5, -310.24) * mm, "end": v(384.5, -310.24) * mm});
            skLineSegment(sketch, "E19.8.19.10", {"start": v(377.5, -351.41) * mm, "end": v(382.5, -351.41) * mm});
            skLineSegment(sketch, "E19.11.19.10", {"start": v(375.5, -310.24) * mm, "end": v(375.5, -349.41) * mm});
            skArc(sketch, "E19.14.19.10", {"start": v(382.5, -351.41) * mm, "mid": v(383.91, -350.82) * mm, "end": v(384.5, -349.41) * mm});
            skArc(sketch, "E19.18.19.10", {"start": v(375.5, -349.41) * mm, "mid": v(376.09, -350.82) * mm, "end": v(377.5, -351.41) * mm});
            skPoint(sketch, "E19.0.19.11", {"position": v(375.5, -386.05) * mm});
            skLineSegment(sketch, "E19.1.19.11", {"start": v(384.5, -344.88) * mm, "end": v(384.5, -384.05) * mm});
            skPoint(sketch, "E19.4.19.11", {"position": v(384.5, -386.05) * mm});
            skLineSegment(sketch, "E19.5.19.11", {"start": v(375.5, -344.88) * mm, "end": v(384.5, -344.88) * mm});
            skLineSegment(sketch, "E19.8.19.11", {"start": v(377.5, -386.05) * mm, "end": v(382.5, -386.05) * mm});
            skLineSegment(sketch, "E19.11.19.11", {"start": v(375.5, -344.88) * mm, "end": v(375.5, -384.05) * mm});
            skArc(sketch, "E19.14.19.11", {"start": v(382.5, -386.05) * mm, "mid": v(383.91, -385.47) * mm, "end": v(384.5, -384.05) * mm});
            skArc(sketch, "E19.18.19.11", {"start": v(375.5, -384.05) * mm, "mid": v(376.09, -385.47) * mm, "end": v(377.5, -386.05) * mm});
            skPoint(sketch, "E19.0.19.12", {"position": v(375.5, -420.7) * mm});
            skLineSegment(sketch, "E19.1.19.12", {"start": v(384.5, -379.52) * mm, "end": v(384.5, -418.7) * mm});
            skPoint(sketch, "E19.4.19.12", {"position": v(384.5, -420.7) * mm});
            skLineSegment(sketch, "E19.5.19.12", {"start": v(375.5, -379.52) * mm, "end": v(384.5, -379.52) * mm});
            skLineSegment(sketch, "E19.8.19.12", {"start": v(377.5, -420.7) * mm, "end": v(382.5, -420.7) * mm});
            skLineSegment(sketch, "E19.11.19.12", {"start": v(375.5, -379.52) * mm, "end": v(375.5, -418.7) * mm});
            skArc(sketch, "E19.14.19.12", {"start": v(382.5, -420.7) * mm, "mid": v(383.91, -420.1) * mm, "end": v(384.5, -418.7) * mm});
            skArc(sketch, "E19.18.19.12", {"start": v(375.5, -418.7) * mm, "mid": v(376.09, -420.1) * mm, "end": v(377.5, -420.7) * mm});
            skPoint(sketch, "E19.0.19.13", {"position": v(375.5, -455.33) * mm});
            skLineSegment(sketch, "E19.1.19.13", {"start": v(384.5, -414.16) * mm, "end": v(384.5, -453.33) * mm});
            skPoint(sketch, "E19.4.19.13", {"position": v(384.5, -455.33) * mm});
            skLineSegment(sketch, "E19.5.19.13", {"start": v(375.5, -414.16) * mm, "end": v(384.5, -414.16) * mm});
            skLineSegment(sketch, "E19.8.19.13", {"start": v(377.5, -455.33) * mm, "end": v(382.5, -455.33) * mm});
            skLineSegment(sketch, "E19.11.19.13", {"start": v(375.5, -414.16) * mm, "end": v(375.5, -453.33) * mm});
            skArc(sketch, "E19.14.19.13", {"start": v(382.5, -455.33) * mm, "mid": v(383.91, -454.75) * mm, "end": v(384.5, -453.33) * mm});
            skArc(sketch, "E19.18.19.13", {"start": v(375.5, -453.33) * mm, "mid": v(376.09, -454.75) * mm, "end": v(377.5, -455.33) * mm});
            skPoint(sketch, "E19.0.19.14", {"position": v(375.5, -489.97) * mm});
            skLineSegment(sketch, "E19.1.19.14", {"start": v(384.5, -448.8) * mm, "end": v(384.5, -487.97) * mm});
            skPoint(sketch, "E19.4.19.14", {"position": v(384.5, -489.97) * mm});
            skLineSegment(sketch, "E19.5.19.14", {"start": v(375.5, -448.8) * mm, "end": v(384.5, -448.8) * mm});
            skLineSegment(sketch, "E19.8.19.14", {"start": v(377.5, -489.97) * mm, "end": v(382.5, -489.97) * mm});
            skLineSegment(sketch, "E19.11.19.14", {"start": v(375.5, -448.8) * mm, "end": v(375.5, -487.97) * mm});
            skArc(sketch, "E19.14.19.14", {"start": v(382.5, -489.97) * mm, "mid": v(383.91, -489.39) * mm, "end": v(384.5, -487.97) * mm});
            skArc(sketch, "E19.18.19.14", {"start": v(375.5, -487.97) * mm, "mid": v(376.09, -489.39) * mm, "end": v(377.5, -489.97) * mm});
            skPoint(sketch, "E19.0.20.0", {"position": v(395.5, -5) * mm});
            skLineSegment(sketch, "E19.1.20.0", {"start": v(404.5, 36.17) * mm, "end": v(404.5, -3) * mm});
            skPoint(sketch, "E19.4.20.0", {"position": v(404.5, -5) * mm});
            skLineSegment(sketch, "E19.5.20.0", {"start": v(395.5, 36.17) * mm, "end": v(404.5, 36.17) * mm});
            skLineSegment(sketch, "E19.8.20.0", {"start": v(397.5, -5) * mm, "end": v(402.5, -5) * mm});
            skLineSegment(sketch, "E19.11.20.0", {"start": v(395.5, 36.17) * mm, "end": v(395.5, -3) * mm});
            skArc(sketch, "E19.14.20.0", {"start": v(402.5, -5) * mm, "mid": v(403.91, -4.41) * mm, "end": v(404.5, -3) * mm});
            skArc(sketch, "E19.18.20.0", {"start": v(395.5, -3) * mm, "mid": v(396.09, -4.41) * mm, "end": v(397.5, -5) * mm});
            skPoint(sketch, "E19.0.20.1", {"position": v(395.5, -39.64) * mm});
            skLineSegment(sketch, "E19.1.20.1", {"start": v(404.5, 1.53) * mm, "end": v(404.5, -37.64) * mm});
            skPoint(sketch, "E19.4.20.1", {"position": v(404.5, -39.64) * mm});
            skLineSegment(sketch, "E19.5.20.1", {"start": v(395.5, 1.53) * mm, "end": v(404.5, 1.53) * mm});
            skLineSegment(sketch, "E19.8.20.1", {"start": v(397.5, -39.64) * mm, "end": v(402.5, -39.64) * mm});
            skLineSegment(sketch, "E19.11.20.1", {"start": v(395.5, 1.53) * mm, "end": v(395.5, -37.64) * mm});
            skArc(sketch, "E19.14.20.1", {"start": v(402.5, -39.64) * mm, "mid": v(403.91, -39.06) * mm, "end": v(404.5, -37.64) * mm});
            skArc(sketch, "E19.18.20.1", {"start": v(395.5, -37.64) * mm, "mid": v(396.09, -39.06) * mm, "end": v(397.5, -39.64) * mm});
            skPoint(sketch, "E19.0.20.2", {"position": v(395.5, -74.28) * mm});
            skLineSegment(sketch, "E19.1.20.2", {"start": v(404.5, -33.1) * mm, "end": v(404.5, -72.28) * mm});
            skPoint(sketch, "E19.4.20.2", {"position": v(404.5, -74.28) * mm});
            skLineSegment(sketch, "E19.5.20.2", {"start": v(395.5, -33.1) * mm, "end": v(404.5, -33.1) * mm});
            skLineSegment(sketch, "E19.8.20.2", {"start": v(397.5, -74.28) * mm, "end": v(402.5, -74.28) * mm});
            skLineSegment(sketch, "E19.11.20.2", {"start": v(395.5, -33.1) * mm, "end": v(395.5, -72.28) * mm});
            skArc(sketch, "E19.14.20.2", {"start": v(402.5, -74.28) * mm, "mid": v(403.91, -73.7) * mm, "end": v(404.5, -72.28) * mm});
            skArc(sketch, "E19.18.20.2", {"start": v(395.5, -72.28) * mm, "mid": v(396.09, -73.7) * mm, "end": v(397.5, -74.28) * mm});
            skPoint(sketch, "E19.0.20.3", {"position": v(395.5, -108.92) * mm});
            skLineSegment(sketch, "E19.1.20.3", {"start": v(404.5, -67.75) * mm, "end": v(404.5, -106.92) * mm});
            skPoint(sketch, "E19.4.20.3", {"position": v(404.5, -108.92) * mm});
            skLineSegment(sketch, "E19.5.20.3", {"start": v(395.5, -67.75) * mm, "end": v(404.5, -67.75) * mm});
            skLineSegment(sketch, "E19.8.20.3", {"start": v(397.5, -108.92) * mm, "end": v(402.5, -108.92) * mm});
            skLineSegment(sketch, "E19.11.20.3", {"start": v(395.5, -67.75) * mm, "end": v(395.5, -106.92) * mm});
            skArc(sketch, "E19.14.20.3", {"start": v(402.5, -108.92) * mm, "mid": v(403.91, -108.34) * mm, "end": v(404.5, -106.92) * mm});
            skArc(sketch, "E19.18.20.3", {"start": v(395.5, -106.92) * mm, "mid": v(396.09, -108.34) * mm, "end": v(397.5, -108.92) * mm});
            skPoint(sketch, "E19.0.20.4", {"position": v(395.5, -143.56) * mm});
            skLineSegment(sketch, "E19.1.20.4", {"start": v(404.5, -102.4) * mm, "end": v(404.5, -141.56) * mm});
            skPoint(sketch, "E19.4.20.4", {"position": v(404.5, -143.56) * mm});
            skLineSegment(sketch, "E19.5.20.4", {"start": v(395.5, -102.4) * mm, "end": v(404.5, -102.4) * mm});
            skLineSegment(sketch, "E19.8.20.4", {"start": v(397.5, -143.56) * mm, "end": v(402.5, -143.56) * mm});
            skLineSegment(sketch, "E19.11.20.4", {"start": v(395.5, -102.4) * mm, "end": v(395.5, -141.56) * mm});
            skArc(sketch, "E19.14.20.4", {"start": v(402.5, -143.56) * mm, "mid": v(403.91, -142.98) * mm, "end": v(404.5, -141.56) * mm});
            skArc(sketch, "E19.18.20.4", {"start": v(395.5, -141.56) * mm, "mid": v(396.09, -142.98) * mm, "end": v(397.5, -143.56) * mm});
            skPoint(sketch, "E19.0.20.5", {"position": v(395.5, -178.2) * mm});
            skLineSegment(sketch, "E19.1.20.5", {"start": v(404.5, -137.03) * mm, "end": v(404.5, -176.2) * mm});
            skPoint(sketch, "E19.4.20.5", {"position": v(404.5, -178.2) * mm});
            skLineSegment(sketch, "E19.5.20.5", {"start": v(395.5, -137.03) * mm, "end": v(404.5, -137.03) * mm});
            skLineSegment(sketch, "E19.8.20.5", {"start": v(397.5, -178.2) * mm, "end": v(402.5, -178.2) * mm});
            skLineSegment(sketch, "E19.11.20.5", {"start": v(395.5, -137.03) * mm, "end": v(395.5, -176.2) * mm});
            skArc(sketch, "E19.14.20.5", {"start": v(402.5, -178.2) * mm, "mid": v(403.91, -177.62) * mm, "end": v(404.5, -176.2) * mm});
            skArc(sketch, "E19.18.20.5", {"start": v(395.5, -176.2) * mm, "mid": v(396.09, -177.62) * mm, "end": v(397.5, -178.2) * mm});
            skPoint(sketch, "E19.0.20.6", {"position": v(395.5, -212.85) * mm});
            skLineSegment(sketch, "E19.1.20.6", {"start": v(404.5, -171.67) * mm, "end": v(404.5, -210.85) * mm});
            skPoint(sketch, "E19.4.20.6", {"position": v(404.5, -212.85) * mm});
            skLineSegment(sketch, "E19.5.20.6", {"start": v(395.5, -171.67) * mm, "end": v(404.5, -171.67) * mm});
            skLineSegment(sketch, "E19.8.20.6", {"start": v(397.5, -212.85) * mm, "end": v(402.5, -212.85) * mm});
            skLineSegment(sketch, "E19.11.20.6", {"start": v(395.5, -171.67) * mm, "end": v(395.5, -210.85) * mm});
            skArc(sketch, "E19.14.20.6", {"start": v(402.5, -212.85) * mm, "mid": v(403.91, -212.26) * mm, "end": v(404.5, -210.85) * mm});
            skArc(sketch, "E19.18.20.6", {"start": v(395.5, -210.85) * mm, "mid": v(396.09, -212.26) * mm, "end": v(397.5, -212.85) * mm});
            skPoint(sketch, "E19.0.20.7", {"position": v(395.5, -247.49) * mm});
            skLineSegment(sketch, "E19.1.20.7", {"start": v(404.5, -206.31) * mm, "end": v(404.5, -245.49) * mm});
            skPoint(sketch, "E19.4.20.7", {"position": v(404.5, -247.49) * mm});
            skLineSegment(sketch, "E19.5.20.7", {"start": v(395.5, -206.31) * mm, "end": v(404.5, -206.31) * mm});
            skLineSegment(sketch, "E19.8.20.7", {"start": v(397.5, -247.49) * mm, "end": v(402.5, -247.49) * mm});
            skLineSegment(sketch, "E19.11.20.7", {"start": v(395.5, -206.31) * mm, "end": v(395.5, -245.49) * mm});
            skArc(sketch, "E19.14.20.7", {"start": v(402.5, -247.49) * mm, "mid": v(403.91, -246.9) * mm, "end": v(404.5, -245.49) * mm});
            skArc(sketch, "E19.18.20.7", {"start": v(395.5, -245.49) * mm, "mid": v(396.09, -246.9) * mm, "end": v(397.5, -247.49) * mm});
            skPoint(sketch, "E19.0.20.8", {"position": v(395.5, -282.13) * mm});
            skLineSegment(sketch, "E19.1.20.8", {"start": v(404.5, -240.95) * mm, "end": v(404.5, -280.13) * mm});
            skPoint(sketch, "E19.4.20.8", {"position": v(404.5, -282.13) * mm});
            skLineSegment(sketch, "E19.5.20.8", {"start": v(395.5, -240.95) * mm, "end": v(404.5, -240.95) * mm});
            skLineSegment(sketch, "E19.8.20.8", {"start": v(397.5, -282.13) * mm, "end": v(402.5, -282.13) * mm});
            skLineSegment(sketch, "E19.11.20.8", {"start": v(395.5, -240.95) * mm, "end": v(395.5, -280.13) * mm});
            skArc(sketch, "E19.14.20.8", {"start": v(402.5, -282.13) * mm, "mid": v(403.91, -281.54) * mm, "end": v(404.5, -280.13) * mm});
            skArc(sketch, "E19.18.20.8", {"start": v(395.5, -280.13) * mm, "mid": v(396.09, -281.54) * mm, "end": v(397.5, -282.13) * mm});
            skPoint(sketch, "E19.0.20.9", {"position": v(395.5, -316.77) * mm});
            skLineSegment(sketch, "E19.1.20.9", {"start": v(404.5, -275.6) * mm, "end": v(404.5, -314.77) * mm});
            skPoint(sketch, "E19.4.20.9", {"position": v(404.5, -316.77) * mm});
            skLineSegment(sketch, "E19.5.20.9", {"start": v(395.5, -275.6) * mm, "end": v(404.5, -275.6) * mm});
            skLineSegment(sketch, "E19.8.20.9", {"start": v(397.5, -316.77) * mm, "end": v(402.5, -316.77) * mm});
            skLineSegment(sketch, "E19.11.20.9", {"start": v(395.5, -275.6) * mm, "end": v(395.5, -314.77) * mm});
            skArc(sketch, "E19.14.20.9", {"start": v(402.5, -316.77) * mm, "mid": v(403.91, -316.18) * mm, "end": v(404.5, -314.77) * mm});
            skArc(sketch, "E19.18.20.9", {"start": v(395.5, -314.77) * mm, "mid": v(396.09, -316.18) * mm, "end": v(397.5, -316.77) * mm});
            skPoint(sketch, "E19.0.20.10", {"position": v(395.5, -351.41) * mm});
            skLineSegment(sketch, "E19.1.20.10", {"start": v(404.5, -310.24) * mm, "end": v(404.5, -349.41) * mm});
            skPoint(sketch, "E19.4.20.10", {"position": v(404.5, -351.41) * mm});
            skLineSegment(sketch, "E19.5.20.10", {"start": v(395.5, -310.24) * mm, "end": v(404.5, -310.24) * mm});
            skLineSegment(sketch, "E19.8.20.10", {"start": v(397.5, -351.41) * mm, "end": v(402.5, -351.41) * mm});
            skLineSegment(sketch, "E19.11.20.10", {"start": v(395.5, -310.24) * mm, "end": v(395.5, -349.41) * mm});
            skArc(sketch, "E19.14.20.10", {"start": v(402.5, -351.41) * mm, "mid": v(403.91, -350.82) * mm, "end": v(404.5, -349.41) * mm});
            skArc(sketch, "E19.18.20.10", {"start": v(395.5, -349.41) * mm, "mid": v(396.09, -350.82) * mm, "end": v(397.5, -351.41) * mm});
            skPoint(sketch, "E19.0.20.11", {"position": v(395.5, -386.05) * mm});
            skLineSegment(sketch, "E19.1.20.11", {"start": v(404.5, -344.88) * mm, "end": v(404.5, -384.05) * mm});
            skPoint(sketch, "E19.4.20.11", {"position": v(404.5, -386.05) * mm});
            skLineSegment(sketch, "E19.5.20.11", {"start": v(395.5, -344.88) * mm, "end": v(404.5, -344.88) * mm});
            skLineSegment(sketch, "E19.8.20.11", {"start": v(397.5, -386.05) * mm, "end": v(402.5, -386.05) * mm});
            skLineSegment(sketch, "E19.11.20.11", {"start": v(395.5, -344.88) * mm, "end": v(395.5, -384.05) * mm});
            skArc(sketch, "E19.14.20.11", {"start": v(402.5, -386.05) * mm, "mid": v(403.91, -385.47) * mm, "end": v(404.5, -384.05) * mm});
            skArc(sketch, "E19.18.20.11", {"start": v(395.5, -384.05) * mm, "mid": v(396.09, -385.47) * mm, "end": v(397.5, -386.05) * mm});
            skPoint(sketch, "E19.0.20.12", {"position": v(395.5, -420.7) * mm});
            skLineSegment(sketch, "E19.1.20.12", {"start": v(404.5, -379.52) * mm, "end": v(404.5, -418.7) * mm});
            skPoint(sketch, "E19.4.20.12", {"position": v(404.5, -420.7) * mm});
            skLineSegment(sketch, "E19.5.20.12", {"start": v(395.5, -379.52) * mm, "end": v(404.5, -379.52) * mm});
            skLineSegment(sketch, "E19.8.20.12", {"start": v(397.5, -420.7) * mm, "end": v(402.5, -420.7) * mm});
            skLineSegment(sketch, "E19.11.20.12", {"start": v(395.5, -379.52) * mm, "end": v(395.5, -418.7) * mm});
            skArc(sketch, "E19.14.20.12", {"start": v(402.5, -420.7) * mm, "mid": v(403.91, -420.1) * mm, "end": v(404.5, -418.7) * mm});
            skArc(sketch, "E19.18.20.12", {"start": v(395.5, -418.7) * mm, "mid": v(396.09, -420.1) * mm, "end": v(397.5, -420.7) * mm});
            skPoint(sketch, "E19.0.20.13", {"position": v(395.5, -455.33) * mm});
            skLineSegment(sketch, "E19.1.20.13", {"start": v(404.5, -414.16) * mm, "end": v(404.5, -453.33) * mm});
            skPoint(sketch, "E19.4.20.13", {"position": v(404.5, -455.33) * mm});
            skLineSegment(sketch, "E19.5.20.13", {"start": v(395.5, -414.16) * mm, "end": v(404.5, -414.16) * mm});
            skLineSegment(sketch, "E19.8.20.13", {"start": v(397.5, -455.33) * mm, "end": v(402.5, -455.33) * mm});
            skLineSegment(sketch, "E19.11.20.13", {"start": v(395.5, -414.16) * mm, "end": v(395.5, -453.33) * mm});
            skArc(sketch, "E19.14.20.13", {"start": v(402.5, -455.33) * mm, "mid": v(403.91, -454.75) * mm, "end": v(404.5, -453.33) * mm});
            skArc(sketch, "E19.18.20.13", {"start": v(395.5, -453.33) * mm, "mid": v(396.09, -454.75) * mm, "end": v(397.5, -455.33) * mm});
            skPoint(sketch, "E19.0.20.14", {"position": v(395.5, -489.97) * mm});
            skLineSegment(sketch, "E19.1.20.14", {"start": v(404.5, -448.8) * mm, "end": v(404.5, -487.97) * mm});
            skPoint(sketch, "E19.4.20.14", {"position": v(404.5, -489.97) * mm});
            skLineSegment(sketch, "E19.5.20.14", {"start": v(395.5, -448.8) * mm, "end": v(404.5, -448.8) * mm});
            skLineSegment(sketch, "E19.8.20.14", {"start": v(397.5, -489.97) * mm, "end": v(402.5, -489.97) * mm});
            skLineSegment(sketch, "E19.11.20.14", {"start": v(395.5, -448.8) * mm, "end": v(395.5, -487.97) * mm});
            skArc(sketch, "E19.14.20.14", {"start": v(402.5, -489.97) * mm, "mid": v(403.91, -489.39) * mm, "end": v(404.5, -487.97) * mm});
            skArc(sketch, "E19.18.20.14", {"start": v(395.5, -487.97) * mm, "mid": v(396.09, -489.39) * mm, "end": v(397.5, -489.97) * mm});
            skPoint(sketch, "E19.0.21.0", {"position": v(415.5, -5) * mm});
            skLineSegment(sketch, "E19.1.21.0", {"start": v(424.5, 36.17) * mm, "end": v(424.5, -3) * mm});
            skPoint(sketch, "E19.4.21.0", {"position": v(424.5, -5) * mm});
            skLineSegment(sketch, "E19.5.21.0", {"start": v(415.5, 36.17) * mm, "end": v(424.5, 36.17) * mm});
            skLineSegment(sketch, "E19.8.21.0", {"start": v(417.5, -5) * mm, "end": v(422.5, -5) * mm});
            skLineSegment(sketch, "E19.11.21.0", {"start": v(415.5, 36.17) * mm, "end": v(415.5, -3) * mm});
            skArc(sketch, "E19.14.21.0", {"start": v(422.5, -5) * mm, "mid": v(423.91, -4.41) * mm, "end": v(424.5, -3) * mm});
            skArc(sketch, "E19.18.21.0", {"start": v(415.5, -3) * mm, "mid": v(416.09, -4.41) * mm, "end": v(417.5, -5) * mm});
            skPoint(sketch, "E19.0.21.1", {"position": v(415.5, -39.64) * mm});
            skLineSegment(sketch, "E19.1.21.1", {"start": v(424.5, 1.53) * mm, "end": v(424.5, -37.64) * mm});
            skPoint(sketch, "E19.4.21.1", {"position": v(424.5, -39.64) * mm});
            skLineSegment(sketch, "E19.5.21.1", {"start": v(415.5, 1.53) * mm, "end": v(424.5, 1.53) * mm});
            skLineSegment(sketch, "E19.8.21.1", {"start": v(417.5, -39.64) * mm, "end": v(422.5, -39.64) * mm});
            skLineSegment(sketch, "E19.11.21.1", {"start": v(415.5, 1.53) * mm, "end": v(415.5, -37.64) * mm});
            skArc(sketch, "E19.14.21.1", {"start": v(422.5, -39.64) * mm, "mid": v(423.91, -39.06) * mm, "end": v(424.5, -37.64) * mm});
            skArc(sketch, "E19.18.21.1", {"start": v(415.5, -37.64) * mm, "mid": v(416.09, -39.06) * mm, "end": v(417.5, -39.64) * mm});
            skPoint(sketch, "E19.0.21.2", {"position": v(415.5, -74.28) * mm});
            skLineSegment(sketch, "E19.1.21.2", {"start": v(424.5, -33.1) * mm, "end": v(424.5, -72.28) * mm});
            skPoint(sketch, "E19.4.21.2", {"position": v(424.5, -74.28) * mm});
            skLineSegment(sketch, "E19.5.21.2", {"start": v(415.5, -33.1) * mm, "end": v(424.5, -33.1) * mm});
            skLineSegment(sketch, "E19.8.21.2", {"start": v(417.5, -74.28) * mm, "end": v(422.5, -74.28) * mm});
            skLineSegment(sketch, "E19.11.21.2", {"start": v(415.5, -33.1) * mm, "end": v(415.5, -72.28) * mm});
            skArc(sketch, "E19.14.21.2", {"start": v(422.5, -74.28) * mm, "mid": v(423.91, -73.7) * mm, "end": v(424.5, -72.28) * mm});
            skArc(sketch, "E19.18.21.2", {"start": v(415.5, -72.28) * mm, "mid": v(416.09, -73.7) * mm, "end": v(417.5, -74.28) * mm});
            skPoint(sketch, "E19.0.21.3", {"position": v(415.5, -108.92) * mm});
            skLineSegment(sketch, "E19.1.21.3", {"start": v(424.5, -67.75) * mm, "end": v(424.5, -106.92) * mm});
            skPoint(sketch, "E19.4.21.3", {"position": v(424.5, -108.92) * mm});
            skLineSegment(sketch, "E19.5.21.3", {"start": v(415.5, -67.75) * mm, "end": v(424.5, -67.75) * mm});
            skLineSegment(sketch, "E19.8.21.3", {"start": v(417.5, -108.92) * mm, "end": v(422.5, -108.92) * mm});
            skLineSegment(sketch, "E19.11.21.3", {"start": v(415.5, -67.75) * mm, "end": v(415.5, -106.92) * mm});
            skArc(sketch, "E19.14.21.3", {"start": v(422.5, -108.92) * mm, "mid": v(423.91, -108.34) * mm, "end": v(424.5, -106.92) * mm});
            skArc(sketch, "E19.18.21.3", {"start": v(415.5, -106.92) * mm, "mid": v(416.09, -108.34) * mm, "end": v(417.5, -108.92) * mm});
            skPoint(sketch, "E19.0.21.4", {"position": v(415.5, -143.56) * mm});
            skLineSegment(sketch, "E19.1.21.4", {"start": v(424.5, -102.4) * mm, "end": v(424.5, -141.56) * mm});
            skPoint(sketch, "E19.4.21.4", {"position": v(424.5, -143.56) * mm});
            skLineSegment(sketch, "E19.5.21.4", {"start": v(415.5, -102.4) * mm, "end": v(424.5, -102.4) * mm});
            skLineSegment(sketch, "E19.8.21.4", {"start": v(417.5, -143.56) * mm, "end": v(422.5, -143.56) * mm});
            skLineSegment(sketch, "E19.11.21.4", {"start": v(415.5, -102.4) * mm, "end": v(415.5, -141.56) * mm});
            skArc(sketch, "E19.14.21.4", {"start": v(422.5, -143.56) * mm, "mid": v(423.91, -142.98) * mm, "end": v(424.5, -141.56) * mm});
            skArc(sketch, "E19.18.21.4", {"start": v(415.5, -141.56) * mm, "mid": v(416.09, -142.98) * mm, "end": v(417.5, -143.56) * mm});
            skPoint(sketch, "E19.0.21.5", {"position": v(415.5, -178.2) * mm});
            skLineSegment(sketch, "E19.1.21.5", {"start": v(424.5, -137.03) * mm, "end": v(424.5, -176.2) * mm});
            skPoint(sketch, "E19.4.21.5", {"position": v(424.5, -178.2) * mm});
            skLineSegment(sketch, "E19.5.21.5", {"start": v(415.5, -137.03) * mm, "end": v(424.5, -137.03) * mm});
            skLineSegment(sketch, "E19.8.21.5", {"start": v(417.5, -178.2) * mm, "end": v(422.5, -178.2) * mm});
            skLineSegment(sketch, "E19.11.21.5", {"start": v(415.5, -137.03) * mm, "end": v(415.5, -176.2) * mm});
            skArc(sketch, "E19.14.21.5", {"start": v(422.5, -178.2) * mm, "mid": v(423.91, -177.62) * mm, "end": v(424.5, -176.2) * mm});
            skArc(sketch, "E19.18.21.5", {"start": v(415.5, -176.2) * mm, "mid": v(416.09, -177.62) * mm, "end": v(417.5, -178.2) * mm});
            skPoint(sketch, "E19.0.21.6", {"position": v(415.5, -212.85) * mm});
            skLineSegment(sketch, "E19.1.21.6", {"start": v(424.5, -171.67) * mm, "end": v(424.5, -210.85) * mm});
            skPoint(sketch, "E19.4.21.6", {"position": v(424.5, -212.85) * mm});
            skLineSegment(sketch, "E19.5.21.6", {"start": v(415.5, -171.67) * mm, "end": v(424.5, -171.67) * mm});
            skLineSegment(sketch, "E19.8.21.6", {"start": v(417.5, -212.85) * mm, "end": v(422.5, -212.85) * mm});
            skLineSegment(sketch, "E19.11.21.6", {"start": v(415.5, -171.67) * mm, "end": v(415.5, -210.85) * mm});
            skArc(sketch, "E19.14.21.6", {"start": v(422.5, -212.85) * mm, "mid": v(423.91, -212.26) * mm, "end": v(424.5, -210.85) * mm});
            skArc(sketch, "E19.18.21.6", {"start": v(415.5, -210.85) * mm, "mid": v(416.09, -212.26) * mm, "end": v(417.5, -212.85) * mm});
            skPoint(sketch, "E19.0.21.7", {"position": v(415.5, -247.49) * mm});
            skLineSegment(sketch, "E19.1.21.7", {"start": v(424.5, -206.31) * mm, "end": v(424.5, -245.49) * mm});
            skPoint(sketch, "E19.4.21.7", {"position": v(424.5, -247.49) * mm});
            skLineSegment(sketch, "E19.5.21.7", {"start": v(415.5, -206.31) * mm, "end": v(424.5, -206.31) * mm});
            skLineSegment(sketch, "E19.8.21.7", {"start": v(417.5, -247.49) * mm, "end": v(422.5, -247.49) * mm});
            skLineSegment(sketch, "E19.11.21.7", {"start": v(415.5, -206.31) * mm, "end": v(415.5, -245.49) * mm});
            skArc(sketch, "E19.14.21.7", {"start": v(422.5, -247.49) * mm, "mid": v(423.91, -246.9) * mm, "end": v(424.5, -245.49) * mm});
            skArc(sketch, "E19.18.21.7", {"start": v(415.5, -245.49) * mm, "mid": v(416.09, -246.9) * mm, "end": v(417.5, -247.49) * mm});
            skPoint(sketch, "E19.0.21.8", {"position": v(415.5, -282.13) * mm});
            skLineSegment(sketch, "E19.1.21.8", {"start": v(424.5, -240.95) * mm, "end": v(424.5, -280.13) * mm});
            skPoint(sketch, "E19.4.21.8", {"position": v(424.5, -282.13) * mm});
            skLineSegment(sketch, "E19.5.21.8", {"start": v(415.5, -240.95) * mm, "end": v(424.5, -240.95) * mm});
            skLineSegment(sketch, "E19.8.21.8", {"start": v(417.5, -282.13) * mm, "end": v(422.5, -282.13) * mm});
            skLineSegment(sketch, "E19.11.21.8", {"start": v(415.5, -240.95) * mm, "end": v(415.5, -280.13) * mm});
            skArc(sketch, "E19.14.21.8", {"start": v(422.5, -282.13) * mm, "mid": v(423.91, -281.54) * mm, "end": v(424.5, -280.13) * mm});
            skArc(sketch, "E19.18.21.8", {"start": v(415.5, -280.13) * mm, "mid": v(416.09, -281.54) * mm, "end": v(417.5, -282.13) * mm});
            skPoint(sketch, "E19.0.21.9", {"position": v(415.5, -316.77) * mm});
            skLineSegment(sketch, "E19.1.21.9", {"start": v(424.5, -275.6) * mm, "end": v(424.5, -314.77) * mm});
            skPoint(sketch, "E19.4.21.9", {"position": v(424.5, -316.77) * mm});
            skLineSegment(sketch, "E19.5.21.9", {"start": v(415.5, -275.6) * mm, "end": v(424.5, -275.6) * mm});
            skLineSegment(sketch, "E19.8.21.9", {"start": v(417.5, -316.77) * mm, "end": v(422.5, -316.77) * mm});
            skLineSegment(sketch, "E19.11.21.9", {"start": v(415.5, -275.6) * mm, "end": v(415.5, -314.77) * mm});
            skArc(sketch, "E19.14.21.9", {"start": v(422.5, -316.77) * mm, "mid": v(423.91, -316.18) * mm, "end": v(424.5, -314.77) * mm});
            skArc(sketch, "E19.18.21.9", {"start": v(415.5, -314.77) * mm, "mid": v(416.09, -316.18) * mm, "end": v(417.5, -316.77) * mm});
            skPoint(sketch, "E19.0.21.10", {"position": v(415.5, -351.41) * mm});
            skLineSegment(sketch, "E19.1.21.10", {"start": v(424.5, -310.24) * mm, "end": v(424.5, -349.41) * mm});
            skPoint(sketch, "E19.4.21.10", {"position": v(424.5, -351.41) * mm});
            skLineSegment(sketch, "E19.5.21.10", {"start": v(415.5, -310.24) * mm, "end": v(424.5, -310.24) * mm});
            skLineSegment(sketch, "E19.8.21.10", {"start": v(417.5, -351.41) * mm, "end": v(422.5, -351.41) * mm});
            skLineSegment(sketch, "E19.11.21.10", {"start": v(415.5, -310.24) * mm, "end": v(415.5, -349.41) * mm});
            skArc(sketch, "E19.14.21.10", {"start": v(422.5, -351.41) * mm, "mid": v(423.91, -350.82) * mm, "end": v(424.5, -349.41) * mm});
            skArc(sketch, "E19.18.21.10", {"start": v(415.5, -349.41) * mm, "mid": v(416.09, -350.82) * mm, "end": v(417.5, -351.41) * mm});
            skPoint(sketch, "E19.0.21.11", {"position": v(415.5, -386.05) * mm});
            skLineSegment(sketch, "E19.1.21.11", {"start": v(424.5, -344.88) * mm, "end": v(424.5, -384.05) * mm});
            skPoint(sketch, "E19.4.21.11", {"position": v(424.5, -386.05) * mm});
            skLineSegment(sketch, "E19.5.21.11", {"start": v(415.5, -344.88) * mm, "end": v(424.5, -344.88) * mm});
            skLineSegment(sketch, "E19.8.21.11", {"start": v(417.5, -386.05) * mm, "end": v(422.5, -386.05) * mm});
            skLineSegment(sketch, "E19.11.21.11", {"start": v(415.5, -344.88) * mm, "end": v(415.5, -384.05) * mm});
            skArc(sketch, "E19.14.21.11", {"start": v(422.5, -386.05) * mm, "mid": v(423.91, -385.47) * mm, "end": v(424.5, -384.05) * mm});
            skArc(sketch, "E19.18.21.11", {"start": v(415.5, -384.05) * mm, "mid": v(416.09, -385.47) * mm, "end": v(417.5, -386.05) * mm});
            skPoint(sketch, "E19.0.21.12", {"position": v(415.5, -420.7) * mm});
            skLineSegment(sketch, "E19.1.21.12", {"start": v(424.5, -379.52) * mm, "end": v(424.5, -418.7) * mm});
            skPoint(sketch, "E19.4.21.12", {"position": v(424.5, -420.7) * mm});
            skLineSegment(sketch, "E19.5.21.12", {"start": v(415.5, -379.52) * mm, "end": v(424.5, -379.52) * mm});
            skLineSegment(sketch, "E19.8.21.12", {"start": v(417.5, -420.7) * mm, "end": v(422.5, -420.7) * mm});
            skLineSegment(sketch, "E19.11.21.12", {"start": v(415.5, -379.52) * mm, "end": v(415.5, -418.7) * mm});
            skArc(sketch, "E19.14.21.12", {"start": v(422.5, -420.7) * mm, "mid": v(423.91, -420.1) * mm, "end": v(424.5, -418.7) * mm});
            skArc(sketch, "E19.18.21.12", {"start": v(415.5, -418.7) * mm, "mid": v(416.09, -420.1) * mm, "end": v(417.5, -420.7) * mm});
            skPoint(sketch, "E19.0.21.13", {"position": v(415.5, -455.33) * mm});
            skLineSegment(sketch, "E19.1.21.13", {"start": v(424.5, -414.16) * mm, "end": v(424.5, -453.33) * mm});
            skPoint(sketch, "E19.4.21.13", {"position": v(424.5, -455.33) * mm});
            skLineSegment(sketch, "E19.5.21.13", {"start": v(415.5, -414.16) * mm, "end": v(424.5, -414.16) * mm});
            skLineSegment(sketch, "E19.8.21.13", {"start": v(417.5, -455.33) * mm, "end": v(422.5, -455.33) * mm});
            skLineSegment(sketch, "E19.11.21.13", {"start": v(415.5, -414.16) * mm, "end": v(415.5, -453.33) * mm});
            skArc(sketch, "E19.14.21.13", {"start": v(422.5, -455.33) * mm, "mid": v(423.91, -454.75) * mm, "end": v(424.5, -453.33) * mm});
            skArc(sketch, "E19.18.21.13", {"start": v(415.5, -453.33) * mm, "mid": v(416.09, -454.75) * mm, "end": v(417.5, -455.33) * mm});
            skPoint(sketch, "E19.0.21.14", {"position": v(415.5, -489.97) * mm});
            skLineSegment(sketch, "E19.1.21.14", {"start": v(424.5, -448.8) * mm, "end": v(424.5, -487.97) * mm});
            skPoint(sketch, "E19.4.21.14", {"position": v(424.5, -489.97) * mm});
            skLineSegment(sketch, "E19.5.21.14", {"start": v(415.5, -448.8) * mm, "end": v(424.5, -448.8) * mm});
            skLineSegment(sketch, "E19.8.21.14", {"start": v(417.5, -489.97) * mm, "end": v(422.5, -489.97) * mm});
            skLineSegment(sketch, "E19.11.21.14", {"start": v(415.5, -448.8) * mm, "end": v(415.5, -487.97) * mm});
            skArc(sketch, "E19.14.21.14", {"start": v(422.5, -489.97) * mm, "mid": v(423.91, -489.39) * mm, "end": v(424.5, -487.97) * mm});
            skArc(sketch, "E19.18.21.14", {"start": v(415.5, -487.97) * mm, "mid": v(416.09, -489.39) * mm, "end": v(417.5, -489.97) * mm});
            skPoint(sketch, "E19.0.22.0", {"position": v(435.5, -5) * mm});
            skLineSegment(sketch, "E19.1.22.0", {"start": v(444.5, 36.17) * mm, "end": v(444.5, -3) * mm});
            skPoint(sketch, "E19.4.22.0", {"position": v(444.5, -5) * mm});
            skLineSegment(sketch, "E19.5.22.0", {"start": v(435.5, 36.17) * mm, "end": v(444.5, 36.17) * mm});
            skLineSegment(sketch, "E19.8.22.0", {"start": v(437.5, -5) * mm, "end": v(442.5, -5) * mm});
            skLineSegment(sketch, "E19.11.22.0", {"start": v(435.5, 36.17) * mm, "end": v(435.5, -3) * mm});
            skArc(sketch, "E19.14.22.0", {"start": v(442.5, -5) * mm, "mid": v(443.91, -4.41) * mm, "end": v(444.5, -3) * mm});
            skArc(sketch, "E19.18.22.0", {"start": v(435.5, -3) * mm, "mid": v(436.09, -4.41) * mm, "end": v(437.5, -5) * mm});
            skPoint(sketch, "E19.0.22.1", {"position": v(435.5, -39.64) * mm});
            skLineSegment(sketch, "E19.1.22.1", {"start": v(444.5, 1.53) * mm, "end": v(444.5, -37.64) * mm});
            skPoint(sketch, "E19.4.22.1", {"position": v(444.5, -39.64) * mm});
            skLineSegment(sketch, "E19.5.22.1", {"start": v(435.5, 1.53) * mm, "end": v(444.5, 1.53) * mm});
            skLineSegment(sketch, "E19.8.22.1", {"start": v(437.5, -39.64) * mm, "end": v(442.5, -39.64) * mm});
            skLineSegment(sketch, "E19.11.22.1", {"start": v(435.5, 1.53) * mm, "end": v(435.5, -37.64) * mm});
            skArc(sketch, "E19.14.22.1", {"start": v(442.5, -39.64) * mm, "mid": v(443.91, -39.06) * mm, "end": v(444.5, -37.64) * mm});
            skArc(sketch, "E19.18.22.1", {"start": v(435.5, -37.64) * mm, "mid": v(436.09, -39.06) * mm, "end": v(437.5, -39.64) * mm});
            skPoint(sketch, "E19.0.22.2", {"position": v(435.5, -74.28) * mm});
            skLineSegment(sketch, "E19.1.22.2", {"start": v(444.5, -33.1) * mm, "end": v(444.5, -72.28) * mm});
            skPoint(sketch, "E19.4.22.2", {"position": v(444.5, -74.28) * mm});
            skLineSegment(sketch, "E19.5.22.2", {"start": v(435.5, -33.1) * mm, "end": v(444.5, -33.1) * mm});
            skLineSegment(sketch, "E19.8.22.2", {"start": v(437.5, -74.28) * mm, "end": v(442.5, -74.28) * mm});
            skLineSegment(sketch, "E19.11.22.2", {"start": v(435.5, -33.1) * mm, "end": v(435.5, -72.28) * mm});
            skArc(sketch, "E19.14.22.2", {"start": v(442.5, -74.28) * mm, "mid": v(443.91, -73.7) * mm, "end": v(444.5, -72.28) * mm});
            skArc(sketch, "E19.18.22.2", {"start": v(435.5, -72.28) * mm, "mid": v(436.09, -73.7) * mm, "end": v(437.5, -74.28) * mm});
            skPoint(sketch, "E19.0.22.3", {"position": v(435.5, -108.92) * mm});
            skLineSegment(sketch, "E19.1.22.3", {"start": v(444.5, -67.75) * mm, "end": v(444.5, -106.92) * mm});
            skPoint(sketch, "E19.4.22.3", {"position": v(444.5, -108.92) * mm});
            skLineSegment(sketch, "E19.5.22.3", {"start": v(435.5, -67.75) * mm, "end": v(444.5, -67.75) * mm});
            skLineSegment(sketch, "E19.8.22.3", {"start": v(437.5, -108.92) * mm, "end": v(442.5, -108.92) * mm});
            skLineSegment(sketch, "E19.11.22.3", {"start": v(435.5, -67.75) * mm, "end": v(435.5, -106.92) * mm});
            skArc(sketch, "E19.14.22.3", {"start": v(442.5, -108.92) * mm, "mid": v(443.91, -108.34) * mm, "end": v(444.5, -106.92) * mm});
            skArc(sketch, "E19.18.22.3", {"start": v(435.5, -106.92) * mm, "mid": v(436.09, -108.34) * mm, "end": v(437.5, -108.92) * mm});
            skPoint(sketch, "E19.0.22.4", {"position": v(435.5, -143.56) * mm});
            skLineSegment(sketch, "E19.1.22.4", {"start": v(444.5, -102.4) * mm, "end": v(444.5, -141.56) * mm});
            skPoint(sketch, "E19.4.22.4", {"position": v(444.5, -143.56) * mm});
            skLineSegment(sketch, "E19.5.22.4", {"start": v(435.5, -102.4) * mm, "end": v(444.5, -102.4) * mm});
            skLineSegment(sketch, "E19.8.22.4", {"start": v(437.5, -143.56) * mm, "end": v(442.5, -143.56) * mm});
            skLineSegment(sketch, "E19.11.22.4", {"start": v(435.5, -102.4) * mm, "end": v(435.5, -141.56) * mm});
            skArc(sketch, "E19.14.22.4", {"start": v(442.5, -143.56) * mm, "mid": v(443.91, -142.98) * mm, "end": v(444.5, -141.56) * mm});
            skArc(sketch, "E19.18.22.4", {"start": v(435.5, -141.56) * mm, "mid": v(436.09, -142.98) * mm, "end": v(437.5, -143.56) * mm});
            skPoint(sketch, "E19.0.22.5", {"position": v(435.5, -178.2) * mm});
            skLineSegment(sketch, "E19.1.22.5", {"start": v(444.5, -137.03) * mm, "end": v(444.5, -176.2) * mm});
            skPoint(sketch, "E19.4.22.5", {"position": v(444.5, -178.2) * mm});
            skLineSegment(sketch, "E19.5.22.5", {"start": v(435.5, -137.03) * mm, "end": v(444.5, -137.03) * mm});
            skLineSegment(sketch, "E19.8.22.5", {"start": v(437.5, -178.2) * mm, "end": v(442.5, -178.2) * mm});
            skLineSegment(sketch, "E19.11.22.5", {"start": v(435.5, -137.03) * mm, "end": v(435.5, -176.2) * mm});
            skArc(sketch, "E19.14.22.5", {"start": v(442.5, -178.2) * mm, "mid": v(443.91, -177.62) * mm, "end": v(444.5, -176.2) * mm});
            skArc(sketch, "E19.18.22.5", {"start": v(435.5, -176.2) * mm, "mid": v(436.09, -177.62) * mm, "end": v(437.5, -178.2) * mm});
            skPoint(sketch, "E19.0.22.6", {"position": v(435.5, -212.85) * mm});
            skLineSegment(sketch, "E19.1.22.6", {"start": v(444.5, -171.67) * mm, "end": v(444.5, -210.85) * mm});
            skPoint(sketch, "E19.4.22.6", {"position": v(444.5, -212.85) * mm});
            skLineSegment(sketch, "E19.5.22.6", {"start": v(435.5, -171.67) * mm, "end": v(444.5, -171.67) * mm});
            skLineSegment(sketch, "E19.8.22.6", {"start": v(437.5, -212.85) * mm, "end": v(442.5, -212.85) * mm});
            skLineSegment(sketch, "E19.11.22.6", {"start": v(435.5, -171.67) * mm, "end": v(435.5, -210.85) * mm});
            skArc(sketch, "E19.14.22.6", {"start": v(442.5, -212.85) * mm, "mid": v(443.91, -212.26) * mm, "end": v(444.5, -210.85) * mm});
            skArc(sketch, "E19.18.22.6", {"start": v(435.5, -210.85) * mm, "mid": v(436.09, -212.26) * mm, "end": v(437.5, -212.85) * mm});
            skPoint(sketch, "E19.0.22.7", {"position": v(435.5, -247.49) * mm});
            skLineSegment(sketch, "E19.1.22.7", {"start": v(444.5, -206.31) * mm, "end": v(444.5, -245.49) * mm});
            skPoint(sketch, "E19.4.22.7", {"position": v(444.5, -247.49) * mm});
            skLineSegment(sketch, "E19.5.22.7", {"start": v(435.5, -206.31) * mm, "end": v(444.5, -206.31) * mm});
            skLineSegment(sketch, "E19.8.22.7", {"start": v(437.5, -247.49) * mm, "end": v(442.5, -247.49) * mm});
            skLineSegment(sketch, "E19.11.22.7", {"start": v(435.5, -206.31) * mm, "end": v(435.5, -245.49) * mm});
            skArc(sketch, "E19.14.22.7", {"start": v(442.5, -247.49) * mm, "mid": v(443.91, -246.9) * mm, "end": v(444.5, -245.49) * mm});
            skArc(sketch, "E19.18.22.7", {"start": v(435.5, -245.49) * mm, "mid": v(436.09, -246.9) * mm, "end": v(437.5, -247.49) * mm});
            skPoint(sketch, "E19.0.22.8", {"position": v(435.5, -282.13) * mm});
            skLineSegment(sketch, "E19.1.22.8", {"start": v(444.5, -240.95) * mm, "end": v(444.5, -280.13) * mm});
            skPoint(sketch, "E19.4.22.8", {"position": v(444.5, -282.13) * mm});
            skLineSegment(sketch, "E19.5.22.8", {"start": v(435.5, -240.95) * mm, "end": v(444.5, -240.95) * mm});
            skLineSegment(sketch, "E19.8.22.8", {"start": v(437.5, -282.13) * mm, "end": v(442.5, -282.13) * mm});
            skLineSegment(sketch, "E19.11.22.8", {"start": v(435.5, -240.95) * mm, "end": v(435.5, -280.13) * mm});
            skArc(sketch, "E19.14.22.8", {"start": v(442.5, -282.13) * mm, "mid": v(443.91, -281.54) * mm, "end": v(444.5, -280.13) * mm});
            skArc(sketch, "E19.18.22.8", {"start": v(435.5, -280.13) * mm, "mid": v(436.09, -281.54) * mm, "end": v(437.5, -282.13) * mm});
            skPoint(sketch, "E19.0.22.9", {"position": v(435.5, -316.77) * mm});
            skLineSegment(sketch, "E19.1.22.9", {"start": v(444.5, -275.6) * mm, "end": v(444.5, -314.77) * mm});
            skPoint(sketch, "E19.4.22.9", {"position": v(444.5, -316.77) * mm});
            skLineSegment(sketch, "E19.5.22.9", {"start": v(435.5, -275.6) * mm, "end": v(444.5, -275.6) * mm});
            skLineSegment(sketch, "E19.8.22.9", {"start": v(437.5, -316.77) * mm, "end": v(442.5, -316.77) * mm});
            skLineSegment(sketch, "E19.11.22.9", {"start": v(435.5, -275.6) * mm, "end": v(435.5, -314.77) * mm});
            skArc(sketch, "E19.14.22.9", {"start": v(442.5, -316.77) * mm, "mid": v(443.91, -316.18) * mm, "end": v(444.5, -314.77) * mm});
            skArc(sketch, "E19.18.22.9", {"start": v(435.5, -314.77) * mm, "mid": v(436.09, -316.18) * mm, "end": v(437.5, -316.77) * mm});
            skPoint(sketch, "E19.0.22.10", {"position": v(435.5, -351.41) * mm});
            skLineSegment(sketch, "E19.1.22.10", {"start": v(444.5, -310.24) * mm, "end": v(444.5, -349.41) * mm});
            skPoint(sketch, "E19.4.22.10", {"position": v(444.5, -351.41) * mm});
            skLineSegment(sketch, "E19.5.22.10", {"start": v(435.5, -310.24) * mm, "end": v(444.5, -310.24) * mm});
            skLineSegment(sketch, "E19.8.22.10", {"start": v(437.5, -351.41) * mm, "end": v(442.5, -351.41) * mm});
            skLineSegment(sketch, "E19.11.22.10", {"start": v(435.5, -310.24) * mm, "end": v(435.5, -349.41) * mm});
            skArc(sketch, "E19.14.22.10", {"start": v(442.5, -351.41) * mm, "mid": v(443.91, -350.82) * mm, "end": v(444.5, -349.41) * mm});
            skArc(sketch, "E19.18.22.10", {"start": v(435.5, -349.41) * mm, "mid": v(436.09, -350.82) * mm, "end": v(437.5, -351.41) * mm});
            skPoint(sketch, "E19.0.22.11", {"position": v(435.5, -386.05) * mm});
            skLineSegment(sketch, "E19.1.22.11", {"start": v(444.5, -344.88) * mm, "end": v(444.5, -384.05) * mm});
            skPoint(sketch, "E19.4.22.11", {"position": v(444.5, -386.05) * mm});
            skLineSegment(sketch, "E19.5.22.11", {"start": v(435.5, -344.88) * mm, "end": v(444.5, -344.88) * mm});
            skLineSegment(sketch, "E19.8.22.11", {"start": v(437.5, -386.05) * mm, "end": v(442.5, -386.05) * mm});
            skLineSegment(sketch, "E19.11.22.11", {"start": v(435.5, -344.88) * mm, "end": v(435.5, -384.05) * mm});
            skArc(sketch, "E19.14.22.11", {"start": v(442.5, -386.05) * mm, "mid": v(443.91, -385.47) * mm, "end": v(444.5, -384.05) * mm});
            skArc(sketch, "E19.18.22.11", {"start": v(435.5, -384.05) * mm, "mid": v(436.09, -385.47) * mm, "end": v(437.5, -386.05) * mm});
            skPoint(sketch, "E19.0.22.12", {"position": v(435.5, -420.7) * mm});
            skLineSegment(sketch, "E19.1.22.12", {"start": v(444.5, -379.52) * mm, "end": v(444.5, -418.7) * mm});
            skPoint(sketch, "E19.4.22.12", {"position": v(444.5, -420.7) * mm});
            skLineSegment(sketch, "E19.5.22.12", {"start": v(435.5, -379.52) * mm, "end": v(444.5, -379.52) * mm});
            skLineSegment(sketch, "E19.8.22.12", {"start": v(437.5, -420.7) * mm, "end": v(442.5, -420.7) * mm});
            skLineSegment(sketch, "E19.11.22.12", {"start": v(435.5, -379.52) * mm, "end": v(435.5, -418.7) * mm});
            skArc(sketch, "E19.14.22.12", {"start": v(442.5, -420.7) * mm, "mid": v(443.91, -420.1) * mm, "end": v(444.5, -418.7) * mm});
            skArc(sketch, "E19.18.22.12", {"start": v(435.5, -418.7) * mm, "mid": v(436.09, -420.1) * mm, "end": v(437.5, -420.7) * mm});
            skPoint(sketch, "E19.0.22.13", {"position": v(435.5, -455.33) * mm});
            skLineSegment(sketch, "E19.1.22.13", {"start": v(444.5, -414.16) * mm, "end": v(444.5, -453.33) * mm});
            skPoint(sketch, "E19.4.22.13", {"position": v(444.5, -455.33) * mm});
            skLineSegment(sketch, "E19.5.22.13", {"start": v(435.5, -414.16) * mm, "end": v(444.5, -414.16) * mm});
            skLineSegment(sketch, "E19.8.22.13", {"start": v(437.5, -455.33) * mm, "end": v(442.5, -455.33) * mm});
            skLineSegment(sketch, "E19.11.22.13", {"start": v(435.5, -414.16) * mm, "end": v(435.5, -453.33) * mm});
            skArc(sketch, "E19.14.22.13", {"start": v(442.5, -455.33) * mm, "mid": v(443.91, -454.75) * mm, "end": v(444.5, -453.33) * mm});
            skArc(sketch, "E19.18.22.13", {"start": v(435.5, -453.33) * mm, "mid": v(436.09, -454.75) * mm, "end": v(437.5, -455.33) * mm});
            skPoint(sketch, "E19.0.22.14", {"position": v(435.5, -489.97) * mm});
            skLineSegment(sketch, "E19.1.22.14", {"start": v(444.5, -448.8) * mm, "end": v(444.5, -487.97) * mm});
            skPoint(sketch, "E19.4.22.14", {"position": v(444.5, -489.97) * mm});
            skLineSegment(sketch, "E19.5.22.14", {"start": v(435.5, -448.8) * mm, "end": v(444.5, -448.8) * mm});
            skLineSegment(sketch, "E19.8.22.14", {"start": v(437.5, -489.97) * mm, "end": v(442.5, -489.97) * mm});
            skLineSegment(sketch, "E19.11.22.14", {"start": v(435.5, -448.8) * mm, "end": v(435.5, -487.97) * mm});
            skArc(sketch, "E19.14.22.14", {"start": v(442.5, -489.97) * mm, "mid": v(443.91, -489.39) * mm, "end": v(444.5, -487.97) * mm});
            skArc(sketch, "E19.18.22.14", {"start": v(435.5, -487.97) * mm, "mid": v(436.09, -489.39) * mm, "end": v(437.5, -489.97) * mm});
            skPoint(sketch, "E19.0.23.0", {"position": v(455.5, -5) * mm});
            skLineSegment(sketch, "E19.1.23.0", {"start": v(464.5, 36.17) * mm, "end": v(464.5, -3) * mm});
            skPoint(sketch, "E19.4.23.0", {"position": v(464.5, -5) * mm});
            skLineSegment(sketch, "E19.5.23.0", {"start": v(455.5, 36.17) * mm, "end": v(464.5, 36.17) * mm});
            skLineSegment(sketch, "E19.8.23.0", {"start": v(457.5, -5) * mm, "end": v(462.5, -5) * mm});
            skLineSegment(sketch, "E19.11.23.0", {"start": v(455.5, 36.17) * mm, "end": v(455.5, -3) * mm});
            skArc(sketch, "E19.14.23.0", {"start": v(462.5, -5) * mm, "mid": v(463.91, -4.41) * mm, "end": v(464.5, -3) * mm});
            skArc(sketch, "E19.18.23.0", {"start": v(455.5, -3) * mm, "mid": v(456.09, -4.41) * mm, "end": v(457.5, -5) * mm});
            skPoint(sketch, "E19.0.23.1", {"position": v(455.5, -39.64) * mm});
            skLineSegment(sketch, "E19.1.23.1", {"start": v(464.5, 1.53) * mm, "end": v(464.5, -37.64) * mm});
            skPoint(sketch, "E19.4.23.1", {"position": v(464.5, -39.64) * mm});
            skLineSegment(sketch, "E19.5.23.1", {"start": v(455.5, 1.53) * mm, "end": v(464.5, 1.53) * mm});
            skLineSegment(sketch, "E19.8.23.1", {"start": v(457.5, -39.64) * mm, "end": v(462.5, -39.64) * mm});
            skLineSegment(sketch, "E19.11.23.1", {"start": v(455.5, 1.53) * mm, "end": v(455.5, -37.64) * mm});
            skArc(sketch, "E19.14.23.1", {"start": v(462.5, -39.64) * mm, "mid": v(463.91, -39.06) * mm, "end": v(464.5, -37.64) * mm});
            skArc(sketch, "E19.18.23.1", {"start": v(455.5, -37.64) * mm, "mid": v(456.09, -39.06) * mm, "end": v(457.5, -39.64) * mm});
            skPoint(sketch, "E19.0.23.2", {"position": v(455.5, -74.28) * mm});
            skLineSegment(sketch, "E19.1.23.2", {"start": v(464.5, -33.1) * mm, "end": v(464.5, -72.28) * mm});
            skPoint(sketch, "E19.4.23.2", {"position": v(464.5, -74.28) * mm});
            skLineSegment(sketch, "E19.5.23.2", {"start": v(455.5, -33.1) * mm, "end": v(464.5, -33.1) * mm});
            skLineSegment(sketch, "E19.8.23.2", {"start": v(457.5, -74.28) * mm, "end": v(462.5, -74.28) * mm});
            skLineSegment(sketch, "E19.11.23.2", {"start": v(455.5, -33.1) * mm, "end": v(455.5, -72.28) * mm});
            skArc(sketch, "E19.14.23.2", {"start": v(462.5, -74.28) * mm, "mid": v(463.91, -73.7) * mm, "end": v(464.5, -72.28) * mm});
            skArc(sketch, "E19.18.23.2", {"start": v(455.5, -72.28) * mm, "mid": v(456.09, -73.7) * mm, "end": v(457.5, -74.28) * mm});
            skPoint(sketch, "E19.0.23.3", {"position": v(455.5, -108.92) * mm});
            skLineSegment(sketch, "E19.1.23.3", {"start": v(464.5, -67.75) * mm, "end": v(464.5, -106.92) * mm});
            skPoint(sketch, "E19.4.23.3", {"position": v(464.5, -108.92) * mm});
            skLineSegment(sketch, "E19.5.23.3", {"start": v(455.5, -67.75) * mm, "end": v(464.5, -67.75) * mm});
            skLineSegment(sketch, "E19.8.23.3", {"start": v(457.5, -108.92) * mm, "end": v(462.5, -108.92) * mm});
            skLineSegment(sketch, "E19.11.23.3", {"start": v(455.5, -67.75) * mm, "end": v(455.5, -106.92) * mm});
            skArc(sketch, "E19.14.23.3", {"start": v(462.5, -108.92) * mm, "mid": v(463.91, -108.34) * mm, "end": v(464.5, -106.92) * mm});
            skArc(sketch, "E19.18.23.3", {"start": v(455.5, -106.92) * mm, "mid": v(456.09, -108.34) * mm, "end": v(457.5, -108.92) * mm});
            skPoint(sketch, "E19.0.23.4", {"position": v(455.5, -143.56) * mm});
            skLineSegment(sketch, "E19.1.23.4", {"start": v(464.5, -102.4) * mm, "end": v(464.5, -141.56) * mm});
            skPoint(sketch, "E19.4.23.4", {"position": v(464.5, -143.56) * mm});
            skLineSegment(sketch, "E19.5.23.4", {"start": v(455.5, -102.4) * mm, "end": v(464.5, -102.4) * mm});
            skLineSegment(sketch, "E19.8.23.4", {"start": v(457.5, -143.56) * mm, "end": v(462.5, -143.56) * mm});
            skLineSegment(sketch, "E19.11.23.4", {"start": v(455.5, -102.4) * mm, "end": v(455.5, -141.56) * mm});
            skArc(sketch, "E19.14.23.4", {"start": v(462.5, -143.56) * mm, "mid": v(463.91, -142.98) * mm, "end": v(464.5, -141.56) * mm});
            skArc(sketch, "E19.18.23.4", {"start": v(455.5, -141.56) * mm, "mid": v(456.09, -142.98) * mm, "end": v(457.5, -143.56) * mm});
            skPoint(sketch, "E19.0.23.5", {"position": v(455.5, -178.2) * mm});
            skLineSegment(sketch, "E19.1.23.5", {"start": v(464.5, -137.03) * mm, "end": v(464.5, -176.2) * mm});
            skPoint(sketch, "E19.4.23.5", {"position": v(464.5, -178.2) * mm});
            skLineSegment(sketch, "E19.5.23.5", {"start": v(455.5, -137.03) * mm, "end": v(464.5, -137.03) * mm});
            skLineSegment(sketch, "E19.8.23.5", {"start": v(457.5, -178.2) * mm, "end": v(462.5, -178.2) * mm});
            skLineSegment(sketch, "E19.11.23.5", {"start": v(455.5, -137.03) * mm, "end": v(455.5, -176.2) * mm});
            skArc(sketch, "E19.14.23.5", {"start": v(462.5, -178.2) * mm, "mid": v(463.91, -177.62) * mm, "end": v(464.5, -176.2) * mm});
            skArc(sketch, "E19.18.23.5", {"start": v(455.5, -176.2) * mm, "mid": v(456.09, -177.62) * mm, "end": v(457.5, -178.2) * mm});
            skPoint(sketch, "E19.0.23.6", {"position": v(455.5, -212.85) * mm});
            skLineSegment(sketch, "E19.1.23.6", {"start": v(464.5, -171.67) * mm, "end": v(464.5, -210.85) * mm});
            skPoint(sketch, "E19.4.23.6", {"position": v(464.5, -212.85) * mm});
            skLineSegment(sketch, "E19.5.23.6", {"start": v(455.5, -171.67) * mm, "end": v(464.5, -171.67) * mm});
            skLineSegment(sketch, "E19.8.23.6", {"start": v(457.5, -212.85) * mm, "end": v(462.5, -212.85) * mm});
            skLineSegment(sketch, "E19.11.23.6", {"start": v(455.5, -171.67) * mm, "end": v(455.5, -210.85) * mm});
            skArc(sketch, "E19.14.23.6", {"start": v(462.5, -212.85) * mm, "mid": v(463.91, -212.26) * mm, "end": v(464.5, -210.85) * mm});
            skArc(sketch, "E19.18.23.6", {"start": v(455.5, -210.85) * mm, "mid": v(456.09, -212.26) * mm, "end": v(457.5, -212.85) * mm});
            skPoint(sketch, "E19.0.23.7", {"position": v(455.5, -247.49) * mm});
            skLineSegment(sketch, "E19.1.23.7", {"start": v(464.5, -206.31) * mm, "end": v(464.5, -245.49) * mm});
            skPoint(sketch, "E19.4.23.7", {"position": v(464.5, -247.49) * mm});
            skLineSegment(sketch, "E19.5.23.7", {"start": v(455.5, -206.31) * mm, "end": v(464.5, -206.31) * mm});
            skLineSegment(sketch, "E19.8.23.7", {"start": v(457.5, -247.49) * mm, "end": v(462.5, -247.49) * mm});
            skLineSegment(sketch, "E19.11.23.7", {"start": v(455.5, -206.31) * mm, "end": v(455.5, -245.49) * mm});
            skArc(sketch, "E19.14.23.7", {"start": v(462.5, -247.49) * mm, "mid": v(463.91, -246.9) * mm, "end": v(464.5, -245.49) * mm});
            skArc(sketch, "E19.18.23.7", {"start": v(455.5, -245.49) * mm, "mid": v(456.09, -246.9) * mm, "end": v(457.5, -247.49) * mm});
            skPoint(sketch, "E19.0.23.8", {"position": v(455.5, -282.13) * mm});
            skLineSegment(sketch, "E19.1.23.8", {"start": v(464.5, -240.95) * mm, "end": v(464.5, -280.13) * mm});
            skPoint(sketch, "E19.4.23.8", {"position": v(464.5, -282.13) * mm});
            skLineSegment(sketch, "E19.5.23.8", {"start": v(455.5, -240.95) * mm, "end": v(464.5, -240.95) * mm});
            skLineSegment(sketch, "E19.8.23.8", {"start": v(457.5, -282.13) * mm, "end": v(462.5, -282.13) * mm});
            skLineSegment(sketch, "E19.11.23.8", {"start": v(455.5, -240.95) * mm, "end": v(455.5, -280.13) * mm});
            skArc(sketch, "E19.14.23.8", {"start": v(462.5, -282.13) * mm, "mid": v(463.91, -281.54) * mm, "end": v(464.5, -280.13) * mm});
            skArc(sketch, "E19.18.23.8", {"start": v(455.5, -280.13) * mm, "mid": v(456.09, -281.54) * mm, "end": v(457.5, -282.13) * mm});
            skPoint(sketch, "E19.0.23.9", {"position": v(455.5, -316.77) * mm});
            skLineSegment(sketch, "E19.1.23.9", {"start": v(464.5, -275.6) * mm, "end": v(464.5, -314.77) * mm});
            skPoint(sketch, "E19.4.23.9", {"position": v(464.5, -316.77) * mm});
            skLineSegment(sketch, "E19.5.23.9", {"start": v(455.5, -275.6) * mm, "end": v(464.5, -275.6) * mm});
            skLineSegment(sketch, "E19.8.23.9", {"start": v(457.5, -316.77) * mm, "end": v(462.5, -316.77) * mm});
            skLineSegment(sketch, "E19.11.23.9", {"start": v(455.5, -275.6) * mm, "end": v(455.5, -314.77) * mm});
            skArc(sketch, "E19.14.23.9", {"start": v(462.5, -316.77) * mm, "mid": v(463.91, -316.18) * mm, "end": v(464.5, -314.77) * mm});
            skArc(sketch, "E19.18.23.9", {"start": v(455.5, -314.77) * mm, "mid": v(456.09, -316.18) * mm, "end": v(457.5, -316.77) * mm});
            skPoint(sketch, "E19.0.23.10", {"position": v(455.5, -351.41) * mm});
            skLineSegment(sketch, "E19.1.23.10", {"start": v(464.5, -310.24) * mm, "end": v(464.5, -349.41) * mm});
            skPoint(sketch, "E19.4.23.10", {"position": v(464.5, -351.41) * mm});
            skLineSegment(sketch, "E19.5.23.10", {"start": v(455.5, -310.24) * mm, "end": v(464.5, -310.24) * mm});
            skLineSegment(sketch, "E19.8.23.10", {"start": v(457.5, -351.41) * mm, "end": v(462.5, -351.41) * mm});
            skLineSegment(sketch, "E19.11.23.10", {"start": v(455.5, -310.24) * mm, "end": v(455.5, -349.41) * mm});
            skArc(sketch, "E19.14.23.10", {"start": v(462.5, -351.41) * mm, "mid": v(463.91, -350.82) * mm, "end": v(464.5, -349.41) * mm});
            skArc(sketch, "E19.18.23.10", {"start": v(455.5, -349.41) * mm, "mid": v(456.09, -350.82) * mm, "end": v(457.5, -351.41) * mm});
            skPoint(sketch, "E19.0.23.11", {"position": v(455.5, -386.05) * mm});
            skLineSegment(sketch, "E19.1.23.11", {"start": v(464.5, -344.88) * mm, "end": v(464.5, -384.05) * mm});
            skPoint(sketch, "E19.4.23.11", {"position": v(464.5, -386.05) * mm});
            skLineSegment(sketch, "E19.5.23.11", {"start": v(455.5, -344.88) * mm, "end": v(464.5, -344.88) * mm});
            skLineSegment(sketch, "E19.8.23.11", {"start": v(457.5, -386.05) * mm, "end": v(462.5, -386.05) * mm});
            skLineSegment(sketch, "E19.11.23.11", {"start": v(455.5, -344.88) * mm, "end": v(455.5, -384.05) * mm});
            skArc(sketch, "E19.14.23.11", {"start": v(462.5, -386.05) * mm, "mid": v(463.91, -385.47) * mm, "end": v(464.5, -384.05) * mm});
            skArc(sketch, "E19.18.23.11", {"start": v(455.5, -384.05) * mm, "mid": v(456.09, -385.47) * mm, "end": v(457.5, -386.05) * mm});
            skPoint(sketch, "E19.0.23.12", {"position": v(455.5, -420.7) * mm});
            skLineSegment(sketch, "E19.1.23.12", {"start": v(464.5, -379.52) * mm, "end": v(464.5, -418.7) * mm});
            skPoint(sketch, "E19.4.23.12", {"position": v(464.5, -420.7) * mm});
            skLineSegment(sketch, "E19.5.23.12", {"start": v(455.5, -379.52) * mm, "end": v(464.5, -379.52) * mm});
            skLineSegment(sketch, "E19.8.23.12", {"start": v(457.5, -420.7) * mm, "end": v(462.5, -420.7) * mm});
            skLineSegment(sketch, "E19.11.23.12", {"start": v(455.5, -379.52) * mm, "end": v(455.5, -418.7) * mm});
            skArc(sketch, "E19.14.23.12", {"start": v(462.5, -420.7) * mm, "mid": v(463.91, -420.1) * mm, "end": v(464.5, -418.7) * mm});
            skArc(sketch, "E19.18.23.12", {"start": v(455.5, -418.7) * mm, "mid": v(456.09, -420.1) * mm, "end": v(457.5, -420.7) * mm});
            skPoint(sketch, "E19.0.23.13", {"position": v(455.5, -455.33) * mm});
            skLineSegment(sketch, "E19.1.23.13", {"start": v(464.5, -414.16) * mm, "end": v(464.5, -453.33) * mm});
            skPoint(sketch, "E19.4.23.13", {"position": v(464.5, -455.33) * mm});
            skLineSegment(sketch, "E19.5.23.13", {"start": v(455.5, -414.16) * mm, "end": v(464.5, -414.16) * mm});
            skLineSegment(sketch, "E19.8.23.13", {"start": v(457.5, -455.33) * mm, "end": v(462.5, -455.33) * mm});
            skLineSegment(sketch, "E19.11.23.13", {"start": v(455.5, -414.16) * mm, "end": v(455.5, -453.33) * mm});
            skArc(sketch, "E19.14.23.13", {"start": v(462.5, -455.33) * mm, "mid": v(463.91, -454.75) * mm, "end": v(464.5, -453.33) * mm});
            skArc(sketch, "E19.18.23.13", {"start": v(455.5, -453.33) * mm, "mid": v(456.09, -454.75) * mm, "end": v(457.5, -455.33) * mm});
            skPoint(sketch, "E19.0.23.14", {"position": v(455.5, -489.97) * mm});
            skLineSegment(sketch, "E19.1.23.14", {"start": v(464.5, -448.8) * mm, "end": v(464.5, -487.97) * mm});
            skPoint(sketch, "E19.4.23.14", {"position": v(464.5, -489.97) * mm});
            skLineSegment(sketch, "E19.5.23.14", {"start": v(455.5, -448.8) * mm, "end": v(464.5, -448.8) * mm});
            skLineSegment(sketch, "E19.8.23.14", {"start": v(457.5, -489.97) * mm, "end": v(462.5, -489.97) * mm});
            skLineSegment(sketch, "E19.11.23.14", {"start": v(455.5, -448.8) * mm, "end": v(455.5, -487.97) * mm});
            skArc(sketch, "E19.14.23.14", {"start": v(462.5, -489.97) * mm, "mid": v(463.91, -489.39) * mm, "end": v(464.5, -487.97) * mm});
            skArc(sketch, "E19.18.23.14", {"start": v(455.5, -487.97) * mm, "mid": v(456.09, -489.39) * mm, "end": v(457.5, -489.97) * mm});
            skSolve(sketch);
        }
        {
            var Q0;
            Q0 = qSketchRegion(id + "F6", true);
            extrude(context, id + "F7", {"entities" : qUnion([Q0]), "operationType" : NewBodyOperationType.REMOVE, "oppositeDirection" : true, "depth" : 2 * mm});
        }
    });
